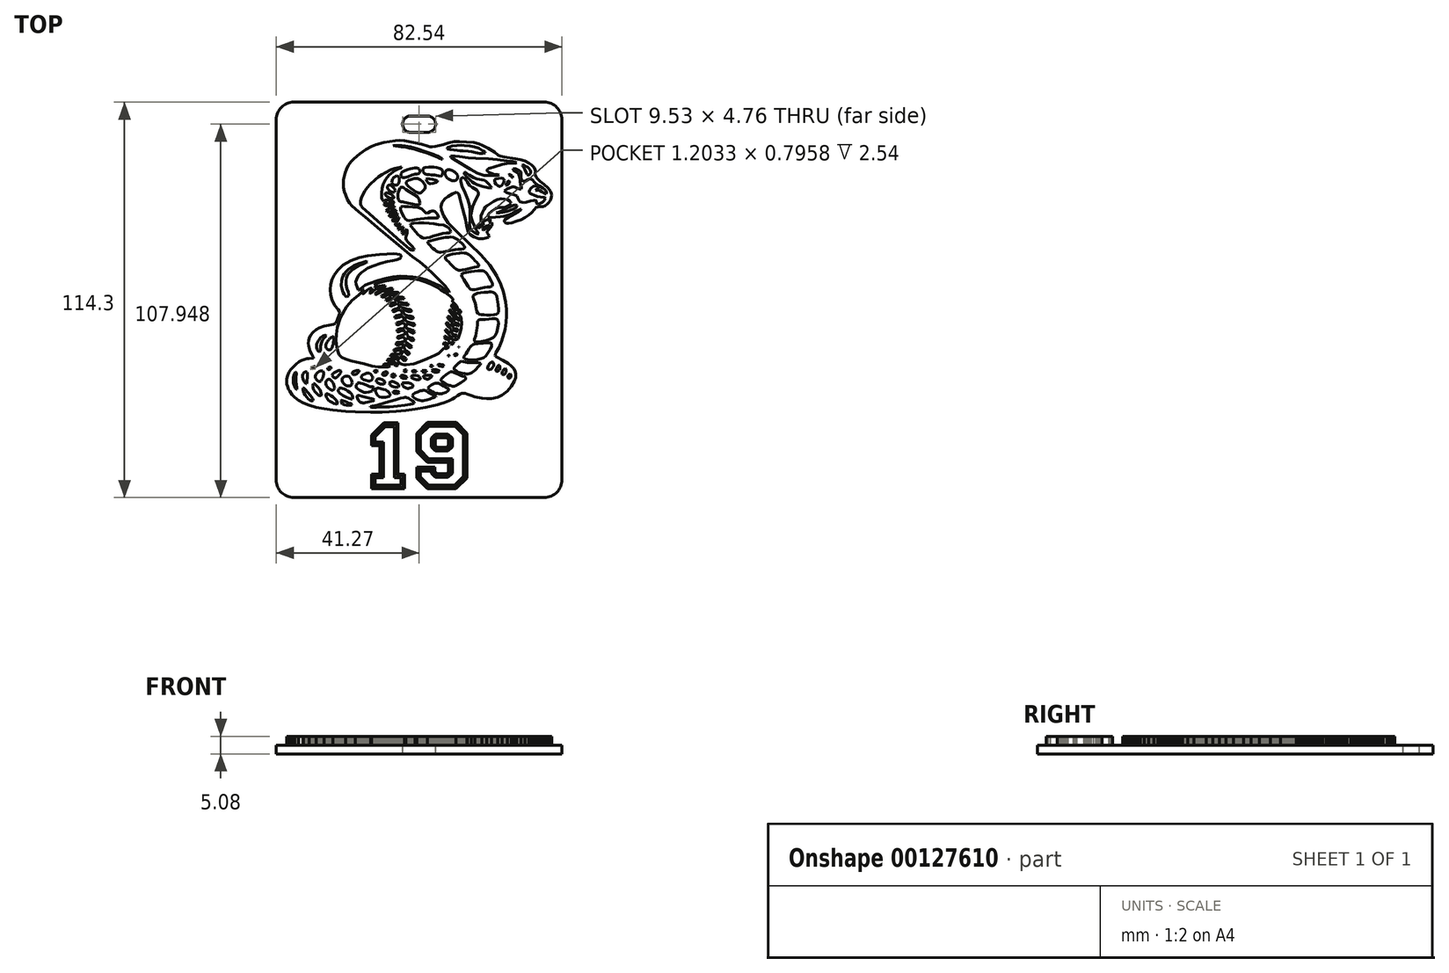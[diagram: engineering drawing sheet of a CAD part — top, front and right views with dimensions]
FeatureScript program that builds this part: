
annotation { "Feature Type Name" : "Feature", "Feature Type Description" : "" }
export const myFeature = defineFeature(function(context is Context, id is Id, definition is map)
    precondition{}
    {
        {
            var Q0;
            Q0=qCreatedBy(makeId("Top.planeOp"),FACE);
            var sketch = newSketch(context, id + "F0", { "sketchPlane" : qUnion([Q0])});
            skLineSegment(sketch, "E0", {"start": v(-25, -17.47) * mm, "end": v(-25.2, -17.55) * mm});
            skLineSegment(sketch, "E1", {"start": v(-25.2, -17.55) * mm, "end": v(-25.4, -17.66) * mm});
            skLineSegment(sketch, "E2", {"start": v(-25.4, -17.66) * mm, "end": v(-25.6, -17.8) * mm});
            skLineSegment(sketch, "E3", {"start": v(-25.6, -17.8) * mm, "end": v(-25.8, -17.96) * mm});
            skLineSegment(sketch, "E4", {"start": v(-25.8, -17.96) * mm, "end": v(-25.99, -18.14) * mm});
            skLineSegment(sketch, "E5", {"start": v(-25.99, -18.14) * mm, "end": v(-26.17, -18.34) * mm});
            skLineSegment(sketch, "E6", {"start": v(-26.17, -18.34) * mm, "end": v(-26.34, -18.55) * mm});
            skLineSegment(sketch, "E7", {"start": v(-26.34, -18.55) * mm, "end": v(-26.5, -18.77) * mm});
            skLineSegment(sketch, "E8", {"start": v(-26.5, -18.77) * mm, "end": v(-26.63, -19) * mm});
            skLineSegment(sketch, "E9", {"start": v(-26.63, -19) * mm, "end": v(-26.75, -19.22) * mm});
            skLineSegment(sketch, "E10", {"start": v(-26.75, -19.22) * mm, "end": v(-26.85, -19.44) * mm});
            skLineSegment(sketch, "E11", {"start": v(-26.85, -19.44) * mm, "end": v(-26.92, -19.66) * mm});
            skLineSegment(sketch, "E12", {"start": v(-26.92, -19.66) * mm, "end": v(-26.97, -19.87) * mm});
            skLineSegment(sketch, "E13", {"start": v(-26.97, -19.87) * mm, "end": v(-26.98, -20.1) * mm});
            skLineSegment(sketch, "E14", {"start": v(-26.98, -20.1) * mm, "end": v(-26.96, -20.32) * mm});
            skLineSegment(sketch, "E15", {"start": v(-26.96, -20.32) * mm, "end": v(-26.9, -20.53) * mm});
            skLineSegment(sketch, "E16", {"start": v(-26.9, -20.53) * mm, "end": v(-26.82, -20.72) * mm});
            skLineSegment(sketch, "E17", {"start": v(-26.82, -20.72) * mm, "end": v(-26.7, -20.88) * mm});
            skLineSegment(sketch, "E18", {"start": v(-26.7, -20.88) * mm, "end": v(-26.56, -21.02) * mm});
            skLineSegment(sketch, "E19", {"start": v(-26.56, -21.02) * mm, "end": v(-26.39, -21.13) * mm});
            skLineSegment(sketch, "E20", {"start": v(-26.39, -21.13) * mm, "end": v(-26.2, -21.2) * mm});
            skLineSegment(sketch, "E21", {"start": v(-26.2, -21.2) * mm, "end": v(-25.98, -21.2) * mm});
            skLineSegment(sketch, "E22", {"start": v(-25.98, -21.2) * mm, "end": v(-25.75, -21.17) * mm});
            skLineSegment(sketch, "E23", {"start": v(-25.75, -21.17) * mm, "end": v(-25.56, -21.1) * mm});
            skLineSegment(sketch, "E24", {"start": v(-25.56, -21.1) * mm, "end": v(-25.44, -20.98) * mm});
            skLineSegment(sketch, "E25", {"start": v(-25.44, -20.98) * mm, "end": v(-25.32, -20.82) * mm});
            skLineSegment(sketch, "E26", {"start": v(-25.32, -20.82) * mm, "end": v(-25.2, -20.6) * mm});
            skLineSegment(sketch, "E27", {"start": v(-25.2, -20.6) * mm, "end": v(-25.1, -20.36) * mm});
            skLineSegment(sketch, "E28", {"start": v(-25.1, -20.36) * mm, "end": v(-25.01, -20.09) * mm});
            skLineSegment(sketch, "E29", {"start": v(-25.01, -20.09) * mm, "end": v(-24.93, -19.8) * mm});
            skLineSegment(sketch, "E30", {"start": v(-24.93, -19.8) * mm, "end": v(-24.85, -19.52) * mm});
            skLineSegment(sketch, "E31", {"start": v(-24.85, -19.52) * mm, "end": v(-24.79, -19.23) * mm});
            skLineSegment(sketch, "E32", {"start": v(-24.79, -19.23) * mm, "end": v(-24.73, -18.97) * mm});
            skLineSegment(sketch, "E33", {"start": v(-24.73, -18.97) * mm, "end": v(-24.68, -18.72) * mm});
            skLineSegment(sketch, "E34", {"start": v(-24.68, -18.72) * mm, "end": v(-24.65, -18.51) * mm});
            skLineSegment(sketch, "E35", {"start": v(-24.65, -18.51) * mm, "end": v(-24.62, -18.35) * mm});
            skLineSegment(sketch, "E36", {"start": v(-24.62, -18.35) * mm, "end": v(-24.6, -18.17) * mm});
            skLineSegment(sketch, "E37", {"start": v(-24.6, -18.17) * mm, "end": v(-24.6, -17.96) * mm});
            skLineSegment(sketch, "E38", {"start": v(-24.6, -17.96) * mm, "end": v(-24.6, -17.74) * mm});
            skLineSegment(sketch, "E39", {"start": v(-24.6, -17.74) * mm, "end": v(-24.67, -17.56) * mm});
            skLineSegment(sketch, "E40", {"start": v(-24.67, -17.56) * mm, "end": v(-24.8, -17.46) * mm});
            skLineSegment(sketch, "E41", {"start": v(-24.8, -17.46) * mm, "end": v(-25, -17.47) * mm});
            skLineSegment(sketch, "E42", {"start": v(-12.5, 38.08) * mm, "end": v(-13.78, 37.58) * mm});
            skLineSegment(sketch, "E43", {"start": v(-13.78, 37.58) * mm, "end": v(-15.37, 36.7) * mm});
            skLineSegment(sketch, "E44", {"start": v(-15.37, 36.7) * mm, "end": v(-17.17, 35.45) * mm});
            skLineSegment(sketch, "E45", {"start": v(-17.17, 35.45) * mm, "end": v(-18.84, 34.02) * mm});
            skLineSegment(sketch, "E46", {"start": v(-18.84, 34.02) * mm, "end": v(-19.59, 33.23) * mm});
            skLineSegment(sketch, "E47", {"start": v(-19.59, 33.23) * mm, "end": v(-20.42, 32.07) * mm});
            skLineSegment(sketch, "E48", {"start": v(-20.42, 32.07) * mm, "end": v(-21.02, 30.93) * mm});
            skLineSegment(sketch, "E49", {"start": v(-21.02, 30.93) * mm, "end": v(-21.4, 29.95) * mm});
            skLineSegment(sketch, "E50", {"start": v(-21.4, 29.95) * mm, "end": v(-21.75, 28.48) * mm});
            skLineSegment(sketch, "E51", {"start": v(-21.75, 28.48) * mm, "end": v(-21.82, 27.9) * mm});
            skLineSegment(sketch, "E52", {"start": v(-21.82, 27.9) * mm, "end": v(-21.87, 26.75) * mm});
            skLineSegment(sketch, "E53", {"start": v(-21.87, 26.75) * mm, "end": v(-21.82, 25.82) * mm});
            skLineSegment(sketch, "E54", {"start": v(-21.82, 25.82) * mm, "end": v(-21.57, 24.45) * mm});
            skLineSegment(sketch, "E55", {"start": v(-21.57, 24.45) * mm, "end": v(-21.3, 23.55) * mm});
            skLineSegment(sketch, "E56", {"start": v(-21.3, 23.55) * mm, "end": v(-20.71, 22.25) * mm});
            skLineSegment(sketch, "E57", {"start": v(-20.71, 22.25) * mm, "end": v(-20.07, 21.21) * mm});
            skLineSegment(sketch, "E58", {"start": v(-20.07, 21.21) * mm, "end": v(-19.42, 20.42) * mm});
            skLineSegment(sketch, "E59", {"start": v(-19.42, 20.42) * mm, "end": v(-18.5, 19.54) * mm});
            skLineSegment(sketch, "E60", {"start": v(-18.5, 19.54) * mm, "end": v(-17.42, 18.64) * mm});
            skLineSegment(sketch, "E61", {"start": v(-17.42, 18.64) * mm, "end": v(-15.55, 17.08) * mm});
            skLineSegment(sketch, "E62", {"start": v(-15.55, 17.08) * mm, "end": v(-11.25, 13.43) * mm});
            skLineSegment(sketch, "E63", {"start": v(-11.25, 13.43) * mm, "end": v(-6.61, 9.59) * mm});
            skLineSegment(sketch, "E64", {"start": v(-6.61, 9.59) * mm, "end": v(-3.48, 6.97) * mm});
            skLineSegment(sketch, "E65", {"start": v(-3.48, 6.97) * mm, "end": v(-1.87, 5.73) * mm});
            skLineSegment(sketch, "E66", {"start": v(-1.87, 5.73) * mm, "end": v(0.18, 4.21) * mm});
            skLineSegment(sketch, "E67", {"start": v(0.18, 4.21) * mm, "end": v(1.93, 2.74) * mm});
            skLineSegment(sketch, "E68", {"start": v(1.93, 2.74) * mm, "end": v(4.36, 0.48) * mm});
            skLineSegment(sketch, "E69", {"start": v(4.36, 0.48) * mm, "end": v(6.86, -2.06) * mm});
            skLineSegment(sketch, "E70", {"start": v(6.86, -2.06) * mm, "end": v(7.56, -2.84) * mm});
            skLineSegment(sketch, "E71", {"start": v(7.56, -2.84) * mm, "end": v(8.48, -4.07) * mm});
            skLineSegment(sketch, "E72", {"start": v(8.48, -4.07) * mm, "end": v(8.76, -4.46) * mm});
            skLineSegment(sketch, "E73", {"start": v(8.76, -4.46) * mm, "end": v(8.71, -4.6) * mm});
            skLineSegment(sketch, "E74", {"start": v(8.71, -4.6) * mm, "end": v(7.64, -3.81) * mm});
            skLineSegment(sketch, "E75", {"start": v(7.64, -3.81) * mm, "end": v(6.2, -2.87) * mm});
            skLineSegment(sketch, "E76", {"start": v(6.2, -2.87) * mm, "end": v(4.71, -2.12) * mm});
            skLineSegment(sketch, "E77", {"start": v(4.71, -2.12) * mm, "end": v(2.14, -1.05) * mm});
            skLineSegment(sketch, "E78", {"start": v(2.14, -1.05) * mm, "end": v(0.04, -0.43) * mm});
            skLineSegment(sketch, "E79", {"start": v(0.04, -0.43) * mm, "end": v(-1.8, -0.1) * mm});
            skLineSegment(sketch, "E80", {"start": v(-1.8, -0.1) * mm, "end": v(-3.45, 0.04) * mm});
            skLineSegment(sketch, "E81", {"start": v(-3.45, 0.04) * mm, "end": v(-5.49, 0.05) * mm});
            skLineSegment(sketch, "E82", {"start": v(-5.49, 0.05) * mm, "end": v(-7.5, -0.12) * mm});
            skLineSegment(sketch, "E83", {"start": v(-7.5, -0.12) * mm, "end": v(-9.48, -0.47) * mm});
            skLineSegment(sketch, "E84", {"start": v(-9.48, -0.47) * mm, "end": v(-11.8, -1.16) * mm});
            skLineSegment(sketch, "E85", {"start": v(-11.8, -1.16) * mm, "end": v(-14.7, -2.17) * mm});
            skLineSegment(sketch, "E86", {"start": v(-14.7, -2.17) * mm, "end": v(-15.63, -2.56) * mm});
            skLineSegment(sketch, "E87", {"start": v(-15.63, -2.56) * mm, "end": v(-16.3, -3) * mm});
            skLineSegment(sketch, "E88", {"start": v(-16.3, -3) * mm, "end": v(-16.86, -3.54) * mm});
            skLineSegment(sketch, "E89", {"start": v(-16.86, -3.54) * mm, "end": v(-17.17, -3.82) * mm});
            skLineSegment(sketch, "E90", {"start": v(-17.17, -3.82) * mm, "end": v(-17.34, -3.95) * mm});
            skLineSegment(sketch, "E91", {"start": v(-17.34, -3.95) * mm, "end": v(-17.56, -3.93) * mm});
            skLineSegment(sketch, "E92", {"start": v(-17.56, -3.93) * mm, "end": v(-17.85, -3.32) * mm});
            skLineSegment(sketch, "E93", {"start": v(-17.85, -3.32) * mm, "end": v(-18.2, -2.35) * mm});
            skLineSegment(sketch, "E94", {"start": v(-18.2, -2.35) * mm, "end": v(-18.28, -1.6) * mm});
            skLineSegment(sketch, "E95", {"start": v(-18.28, -1.6) * mm, "end": v(-18.12, -0.9) * mm});
            skLineSegment(sketch, "E96", {"start": v(-18.12, -0.9) * mm, "end": v(-17.5, 0.19) * mm});
            skLineSegment(sketch, "E97", {"start": v(-17.5, 0.19) * mm, "end": v(-16.7, 1.08) * mm});
            skLineSegment(sketch, "E98", {"start": v(-16.7, 1.08) * mm, "end": v(-15.96, 1.7) * mm});
            skLineSegment(sketch, "E99", {"start": v(-15.96, 1.7) * mm, "end": v(-14.9, 2.35) * mm});
            skLineSegment(sketch, "E100", {"start": v(-14.9, 2.35) * mm, "end": v(-13.29, 3.1) * mm});
            skLineSegment(sketch, "E101", {"start": v(-13.29, 3.1) * mm, "end": v(-11.09, 3.81) * mm});
            skLineSegment(sketch, "E102", {"start": v(-11.09, 3.81) * mm, "end": v(-9.17, 4.31) * mm});
            skLineSegment(sketch, "E103", {"start": v(-9.17, 4.31) * mm, "end": v(-7.68, 4.6) * mm});
            skLineSegment(sketch, "E104", {"start": v(-7.68, 4.6) * mm, "end": v(-6.49, 4.84) * mm});
            skLineSegment(sketch, "E105", {"start": v(-6.49, 4.84) * mm, "end": v(-5.5, 5.25) * mm});
            skLineSegment(sketch, "E106", {"start": v(-5.5, 5.25) * mm, "end": v(-5.2, 5.6) * mm});
            skLineSegment(sketch, "E107", {"start": v(-5.2, 5.6) * mm, "end": v(-5.24, 6.07) * mm});
            skLineSegment(sketch, "E108", {"start": v(-5.24, 6.07) * mm, "end": v(-5.54, 6.37) * mm});
            skLineSegment(sketch, "E109", {"start": v(-5.54, 6.37) * mm, "end": v(-6.43, 6.46) * mm});
            skLineSegment(sketch, "E110", {"start": v(-6.43, 6.46) * mm, "end": v(-7.45, 6.57) * mm});
            skLineSegment(sketch, "E111", {"start": v(-7.45, 6.57) * mm, "end": v(-9.23, 6.5) * mm});
            skLineSegment(sketch, "E112", {"start": v(-9.23, 6.5) * mm, "end": v(-11.41, 6.4) * mm});
            skLineSegment(sketch, "E113", {"start": v(-11.41, 6.4) * mm, "end": v(-14.93, 6.01) * mm});
            skLineSegment(sketch, "E114", {"start": v(-14.93, 6.01) * mm, "end": v(-17.28, 5.47) * mm});
            skLineSegment(sketch, "E115", {"start": v(-17.28, 5.47) * mm, "end": v(-19.74, 4.54) * mm});
            skLineSegment(sketch, "E116", {"start": v(-19.74, 4.54) * mm, "end": v(-21.95, 3.24) * mm});
            skLineSegment(sketch, "E117", {"start": v(-21.95, 3.24) * mm, "end": v(-23.55, 1.78) * mm});
            skLineSegment(sketch, "E118", {"start": v(-23.55, 1.78) * mm, "end": v(-24.57, 0.39) * mm});
            skLineSegment(sketch, "E119", {"start": v(-24.57, 0.39) * mm, "end": v(-25.2, -0.89) * mm});
            skLineSegment(sketch, "E120", {"start": v(-25.2, -0.89) * mm, "end": v(-25.61, -2.29) * mm});
            skLineSegment(sketch, "E121", {"start": v(-25.61, -2.29) * mm, "end": v(-25.72, -3.78) * mm});
            skLineSegment(sketch, "E122", {"start": v(-25.72, -3.78) * mm, "end": v(-25.56, -5.3) * mm});
            skLineSegment(sketch, "E123", {"start": v(-25.56, -5.3) * mm, "end": v(-25.17, -6.8) * mm});
            skLineSegment(sketch, "E124", {"start": v(-25.17, -6.8) * mm, "end": v(-24.4, -8.44) * mm});
            skLineSegment(sketch, "E125", {"start": v(-24.4, -8.44) * mm, "end": v(-23.39, -9.6) * mm});
            skLineSegment(sketch, "E126", {"start": v(-23.39, -9.6) * mm, "end": v(-22.97, -10.2) * mm});
            skLineSegment(sketch, "E127", {"start": v(-22.97, -10.2) * mm, "end": v(-22.91, -10.52) * mm});
            skLineSegment(sketch, "E128", {"start": v(-22.91, -10.52) * mm, "end": v(-23.1, -11.24) * mm});
            skLineSegment(sketch, "E129", {"start": v(-23.1, -11.24) * mm, "end": v(-23.62, -12.57) * mm});
            skLineSegment(sketch, "E130", {"start": v(-23.62, -12.57) * mm, "end": v(-23.9, -13.16) * mm});
            skLineSegment(sketch, "E131", {"start": v(-23.9, -13.16) * mm, "end": v(-24, -13.4) * mm});
            skLineSegment(sketch, "E132", {"start": v(-24, -13.4) * mm, "end": v(-24.16, -13.58) * mm});
            skLineSegment(sketch, "E133", {"start": v(-24.16, -13.58) * mm, "end": v(-24.78, -13.85) * mm});
            skLineSegment(sketch, "E134", {"start": v(-24.78, -13.85) * mm, "end": v(-26.07, -14.09) * mm});
            skLineSegment(sketch, "E135", {"start": v(-26.07, -14.09) * mm, "end": v(-27.5, -14.33) * mm});
            skLineSegment(sketch, "E136", {"start": v(-27.5, -14.33) * mm, "end": v(-28.88, -14.85) * mm});
            skLineSegment(sketch, "E137", {"start": v(-28.88, -14.85) * mm, "end": v(-29.72, -15.33) * mm});
            skLineSegment(sketch, "E138", {"start": v(-29.72, -15.33) * mm, "end": v(-30.64, -16.1) * mm});
            skLineSegment(sketch, "E139", {"start": v(-30.64, -16.1) * mm, "end": v(-31.37, -17.06) * mm});
            skLineSegment(sketch, "E140", {"start": v(-31.37, -17.06) * mm, "end": v(-31.8, -17.97) * mm});
            skLineSegment(sketch, "E141", {"start": v(-31.8, -17.97) * mm, "end": v(-31.94, -18.58) * mm});
            skLineSegment(sketch, "E142", {"start": v(-31.94, -18.58) * mm, "end": v(-31.99, -19.3) * mm});
            skLineSegment(sketch, "E143", {"start": v(-31.99, -19.3) * mm, "end": v(-31.88, -20.14) * mm});
            skLineSegment(sketch, "E144", {"start": v(-31.88, -20.14) * mm, "end": v(-31.62, -21.1) * mm});
            skLineSegment(sketch, "E145", {"start": v(-31.62, -21.1) * mm, "end": v(-31.46, -21.57) * mm});
            skLineSegment(sketch, "E146", {"start": v(-31.46, -21.57) * mm, "end": v(-31.01, -22.54) * mm});
            skLineSegment(sketch, "E147", {"start": v(-31.01, -22.54) * mm, "end": v(-30.59, -23.23) * mm});
            skLineSegment(sketch, "E148", {"start": v(-30.59, -23.23) * mm, "end": v(-30.53, -23.34) * mm});
            skLineSegment(sketch, "E149", {"start": v(-30.53, -23.34) * mm, "end": v(-30.55, -23.58) * mm});
            skLineSegment(sketch, "E150", {"start": v(-30.55, -23.58) * mm, "end": v(-30.98, -23.69) * mm});
            skLineSegment(sketch, "E151", {"start": v(-30.98, -23.69) * mm, "end": v(-31.83, -23.74) * mm});
            skLineSegment(sketch, "E152", {"start": v(-31.83, -23.74) * mm, "end": v(-32.4, -23.77) * mm});
            skLineSegment(sketch, "E153", {"start": v(-32.4, -23.77) * mm, "end": v(-32.85, -23.85) * mm});
            skLineSegment(sketch, "E154", {"start": v(-32.85, -23.85) * mm, "end": v(-33.87, -24.26) * mm});
            skLineSegment(sketch, "E155", {"start": v(-33.87, -24.26) * mm, "end": v(-34.68, -24.71) * mm});
            skLineSegment(sketch, "E156", {"start": v(-34.68, -24.71) * mm, "end": v(-35.63, -25.4) * mm});
            skLineSegment(sketch, "E157", {"start": v(-35.63, -25.4) * mm, "end": v(-36.41, -26.13) * mm});
            skLineSegment(sketch, "E158", {"start": v(-36.41, -26.13) * mm, "end": v(-37.09, -26.95) * mm});
            skLineSegment(sketch, "E159", {"start": v(-37.09, -26.95) * mm, "end": v(-37.58, -27.74) * mm});
            skLineSegment(sketch, "E160", {"start": v(-37.58, -27.74) * mm, "end": v(-38, -28.7) * mm});
            skLineSegment(sketch, "E161", {"start": v(-38, -28.7) * mm, "end": v(-38.21, -29.58) * mm});
            skLineSegment(sketch, "E162", {"start": v(-38.21, -29.58) * mm, "end": v(-38.27, -30.38) * mm});
            skLineSegment(sketch, "E163", {"start": v(-38.27, -30.38) * mm, "end": v(-38.21, -31.08) * mm});
            skLineSegment(sketch, "E164", {"start": v(-38.21, -31.08) * mm, "end": v(-38.05, -31.77) * mm});
            skLineSegment(sketch, "E165", {"start": v(-38.05, -31.77) * mm, "end": v(-37.73, -32.62) * mm});
            skLineSegment(sketch, "E166", {"start": v(-37.73, -32.62) * mm, "end": v(-37.42, -33.22) * mm});
            skLineSegment(sketch, "E167", {"start": v(-37.42, -33.22) * mm, "end": v(-36.7, -34.2) * mm});
            skLineSegment(sketch, "E168", {"start": v(-36.7, -34.2) * mm, "end": v(-36, -34.9) * mm});
            skLineSegment(sketch, "E169", {"start": v(-36, -34.9) * mm, "end": v(-34.81, -35.8) * mm});
            skLineSegment(sketch, "E170", {"start": v(-34.81, -35.8) * mm, "end": v(-33.37, -36.58) * mm});
            skLineSegment(sketch, "E171", {"start": v(-33.37, -36.58) * mm, "end": v(-31.8, -37.22) * mm});
            skLineSegment(sketch, "E172", {"start": v(-31.8, -37.22) * mm, "end": v(-29.8, -37.8) * mm});
            skLineSegment(sketch, "E173", {"start": v(-29.8, -37.8) * mm, "end": v(-27.44, -38.3) * mm});
            skLineSegment(sketch, "E174", {"start": v(-27.44, -38.3) * mm, "end": v(-24.92, -38.64) * mm});
            skLineSegment(sketch, "E175", {"start": v(-24.92, -38.64) * mm, "end": v(-21.2, -39) * mm});
            skLineSegment(sketch, "E176", {"start": v(-21.2, -39) * mm, "end": v(-18.43, -39.18) * mm});
            skLineSegment(sketch, "E177", {"start": v(-18.43, -39.18) * mm, "end": v(-14, -39.3) * mm});
            skLineSegment(sketch, "E178", {"start": v(-14, -39.3) * mm, "end": v(-10.69, -39.24) * mm});
            skLineSegment(sketch, "E179", {"start": v(-10.69, -39.24) * mm, "end": v(-6.63, -39) * mm});
            skLineSegment(sketch, "E180", {"start": v(-6.63, -39) * mm, "end": v(-3.85, -38.73) * mm});
            skLineSegment(sketch, "E181", {"start": v(-3.85, -38.73) * mm, "end": v(-1.2, -38.37) * mm});
            skLineSegment(sketch, "E182", {"start": v(-1.2, -38.37) * mm, "end": v(1.91, -37.82) * mm});
            skLineSegment(sketch, "E183", {"start": v(1.91, -37.82) * mm, "end": v(5.37, -37.04) * mm});
            skLineSegment(sketch, "E184", {"start": v(5.37, -37.04) * mm, "end": v(6.11, -36.83) * mm});
            skLineSegment(sketch, "E185", {"start": v(6.11, -36.83) * mm, "end": v(7.35, -36.42) * mm});
            skLineSegment(sketch, "E186", {"start": v(7.35, -36.42) * mm, "end": v(8.57, -35.92) * mm});
            skLineSegment(sketch, "E187", {"start": v(8.57, -35.92) * mm, "end": v(9.61, -35.42) * mm});
            skLineSegment(sketch, "E188", {"start": v(9.61, -35.42) * mm, "end": v(10.24, -35.06) * mm});
            skLineSegment(sketch, "E189", {"start": v(10.24, -35.06) * mm, "end": v(11.1, -34.46) * mm});
            skLineSegment(sketch, "E190", {"start": v(11.1, -34.46) * mm, "end": v(11.8, -34.04) * mm});
            skLineSegment(sketch, "E191", {"start": v(11.8, -34.04) * mm, "end": v(12.34, -33.83) * mm});
            skLineSegment(sketch, "E192", {"start": v(12.34, -33.83) * mm, "end": v(12.66, -33.78) * mm});
            skLineSegment(sketch, "E193", {"start": v(12.66, -33.78) * mm, "end": v(13.24, -33.84) * mm});
            skLineSegment(sketch, "E194", {"start": v(13.24, -33.84) * mm, "end": v(14, -34.05) * mm});
            skLineSegment(sketch, "E195", {"start": v(14, -34.05) * mm, "end": v(15.13, -34.47) * mm});
            skLineSegment(sketch, "E196", {"start": v(15.13, -34.47) * mm, "end": v(16.14, -34.77) * mm});
            skLineSegment(sketch, "E197", {"start": v(16.14, -34.77) * mm, "end": v(18.11, -35.15) * mm});
            skLineSegment(sketch, "E198", {"start": v(18.11, -35.15) * mm, "end": v(19.54, -35.28) * mm});
            skLineSegment(sketch, "E199", {"start": v(19.54, -35.28) * mm, "end": v(20.95, -35.26) * mm});
            skLineSegment(sketch, "E200", {"start": v(20.95, -35.26) * mm, "end": v(22.74, -34.91) * mm});
            skLineSegment(sketch, "E201", {"start": v(22.74, -34.91) * mm, "end": v(23.97, -34.28) * mm});
            skLineSegment(sketch, "E202", {"start": v(23.97, -34.28) * mm, "end": v(25.45, -33.1) * mm});
            skLineSegment(sketch, "E203", {"start": v(25.45, -33.1) * mm, "end": v(26.6, -31.82) * mm});
            skLineSegment(sketch, "E204", {"start": v(26.6, -31.82) * mm, "end": v(27.54, -30.3) * mm});
            skLineSegment(sketch, "E205", {"start": v(27.54, -30.3) * mm, "end": v(27.91, -29.21) * mm});
            skLineSegment(sketch, "E206", {"start": v(27.91, -29.21) * mm, "end": v(27.97, -28.25) * mm});
            skLineSegment(sketch, "E207", {"start": v(27.97, -28.25) * mm, "end": v(27.79, -27.53) * mm});
            skLineSegment(sketch, "E208", {"start": v(27.79, -27.53) * mm, "end": v(27.36, -26.75) * mm});
            skLineSegment(sketch, "E209", {"start": v(27.36, -26.75) * mm, "end": v(26.7, -25.97) * mm});
            skLineSegment(sketch, "E210", {"start": v(26.7, -25.97) * mm, "end": v(25.74, -25.16) * mm});
            skLineSegment(sketch, "E211", {"start": v(25.74, -25.16) * mm, "end": v(24.3, -24.24) * mm});
            skLineSegment(sketch, "E212", {"start": v(24.3, -24.24) * mm, "end": v(22.38, -23.32) * mm});
            skLineSegment(sketch, "E213", {"start": v(22.38, -23.32) * mm, "end": v(22.07, -23.07) * mm});
            skLineSegment(sketch, "E214", {"start": v(22.07, -23.07) * mm, "end": v(22, -22.85) * mm});
            skLineSegment(sketch, "E215", {"start": v(22, -22.85) * mm, "end": v(22.07, -22.5) * mm});
            skLineSegment(sketch, "E216", {"start": v(22.07, -22.5) * mm, "end": v(22.26, -22) * mm});
            skLineSegment(sketch, "E217", {"start": v(22.26, -22) * mm, "end": v(23.08, -20.59) * mm});
            skLineSegment(sketch, "E218", {"start": v(23.08, -20.59) * mm, "end": v(23.8, -18.74) * mm});
            skLineSegment(sketch, "E219", {"start": v(23.8, -18.74) * mm, "end": v(24.83, -15.27) * mm});
            skLineSegment(sketch, "E220", {"start": v(24.83, -15.27) * mm, "end": v(25.17, -13.27) * mm});
            skLineSegment(sketch, "E221", {"start": v(25.17, -13.27) * mm, "end": v(25.29, -11.45) * mm});
            skLineSegment(sketch, "E222", {"start": v(25.29, -11.45) * mm, "end": v(25.25, -9.52) * mm});
            skLineSegment(sketch, "E223", {"start": v(25.25, -9.52) * mm, "end": v(25, -7.32) * mm});
            skLineSegment(sketch, "E224", {"start": v(25, -7.32) * mm, "end": v(24.35, -4.46) * mm});
            skLineSegment(sketch, "E225", {"start": v(24.35, -4.46) * mm, "end": v(23.58, -2.27) * mm});
            skLineSegment(sketch, "E226", {"start": v(23.58, -2.27) * mm, "end": v(22.42, 0.17) * mm});
            skLineSegment(sketch, "E227", {"start": v(22.42, 0.17) * mm, "end": v(20.4, 3.28) * mm});
            skLineSegment(sketch, "E228", {"start": v(20.4, 3.28) * mm, "end": v(17.82, 6.24) * mm});
            skLineSegment(sketch, "E229", {"start": v(17.82, 6.24) * mm, "end": v(14.58, 9.4) * mm});
            skLineSegment(sketch, "E230", {"start": v(14.58, 9.4) * mm, "end": v(11.12, 12.71) * mm});
            skLineSegment(sketch, "E231", {"start": v(11.12, 12.71) * mm, "end": v(8.41, 15.53) * mm});
            skLineSegment(sketch, "E232", {"start": v(8.41, 15.53) * mm, "end": v(7.06, 17.49) * mm});
            skLineSegment(sketch, "E233", {"start": v(7.06, 17.49) * mm, "end": v(6.42, 19.21) * mm});
            skLineSegment(sketch, "E234", {"start": v(6.42, 19.21) * mm, "end": v(6.35, 20.23) * mm});
            skLineSegment(sketch, "E235", {"start": v(6.35, 20.23) * mm, "end": v(6.62, 21.33) * mm});
            skLineSegment(sketch, "E236", {"start": v(6.62, 21.33) * mm, "end": v(7.47, 22.5) * mm});
            skLineSegment(sketch, "E237", {"start": v(7.47, 22.5) * mm, "end": v(8.32, 23.15) * mm});
            skLineSegment(sketch, "E238", {"start": v(8.32, 23.15) * mm, "end": v(9.58, 23.9) * mm});
            skLineSegment(sketch, "E239", {"start": v(9.58, 23.9) * mm, "end": v(10.5, 24.28) * mm});
            skLineSegment(sketch, "E240", {"start": v(10.5, 24.28) * mm, "end": v(10.82, 24.33) * mm});
            skLineSegment(sketch, "E241", {"start": v(10.82, 24.33) * mm, "end": v(11.2, 24.18) * mm});
            skLineSegment(sketch, "E242", {"start": v(11.2, 24.18) * mm, "end": v(11.5, 23.7) * mm});
            skLineSegment(sketch, "E243", {"start": v(11.5, 23.7) * mm, "end": v(11.85, 22.6) * mm});
            skLineSegment(sketch, "E244", {"start": v(11.85, 22.6) * mm, "end": v(12.21, 21.03) * mm});
            skLineSegment(sketch, "E245", {"start": v(12.21, 21.03) * mm, "end": v(13.4, 16.32) * mm});
            skLineSegment(sketch, "E246", {"start": v(13.4, 16.32) * mm, "end": v(13.66, 14.7) * mm});
            skLineSegment(sketch, "E247", {"start": v(13.66, 14.7) * mm, "end": v(14.2, 12.79) * mm});
            skLineSegment(sketch, "E248", {"start": v(14.2, 12.79) * mm, "end": v(14.8, 12.05) * mm});
            skLineSegment(sketch, "E249", {"start": v(14.8, 12.05) * mm, "end": v(15.83, 11.4) * mm});
            skLineSegment(sketch, "E250", {"start": v(15.83, 11.4) * mm, "end": v(17.26, 10.97) * mm});
            skLineSegment(sketch, "E251", {"start": v(17.26, 10.97) * mm, "end": v(18.46, 10.86) * mm});
            skLineSegment(sketch, "E252", {"start": v(18.46, 10.86) * mm, "end": v(20.02, 11.24) * mm});
            skLineSegment(sketch, "E253", {"start": v(20.02, 11.24) * mm, "end": v(20.23, 11.5) * mm});
            skLineSegment(sketch, "E254", {"start": v(20.23, 11.5) * mm, "end": v(20.26, 11.77) * mm});
            skLineSegment(sketch, "E255", {"start": v(20.26, 11.77) * mm, "end": v(20.08, 12.08) * mm});
            skLineSegment(sketch, "E256", {"start": v(20.08, 12.08) * mm, "end": v(19.69, 12.5) * mm});
            skLineSegment(sketch, "E257", {"start": v(19.69, 12.5) * mm, "end": v(19.6, 12.73) * mm});
            skLineSegment(sketch, "E258", {"start": v(19.6, 12.73) * mm, "end": v(19.68, 13.04) * mm});
            skLineSegment(sketch, "E259", {"start": v(19.68, 13.04) * mm, "end": v(19.89, 13.35) * mm});
            skLineSegment(sketch, "E260", {"start": v(19.89, 13.35) * mm, "end": v(20.73, 14.23) * mm});
            skLineSegment(sketch, "E261", {"start": v(20.73, 14.23) * mm, "end": v(20.98, 14.58) * mm});
            skLineSegment(sketch, "E262", {"start": v(20.98, 14.58) * mm, "end": v(21.12, 15) * mm});
            skLineSegment(sketch, "E263", {"start": v(21.12, 15) * mm, "end": v(21.1, 15.38) * mm});
            skLineSegment(sketch, "E264", {"start": v(21.1, 15.38) * mm, "end": v(20.91, 15.6) * mm});
            skLineSegment(sketch, "E265", {"start": v(20.91, 15.6) * mm, "end": v(20.43, 15.6) * mm});
            skLineSegment(sketch, "E266", {"start": v(20.43, 15.6) * mm, "end": v(20.24, 15.56) * mm});
            skLineSegment(sketch, "E267", {"start": v(20.24, 15.56) * mm, "end": v(20.37, 15.84) * mm});
            skLineSegment(sketch, "E268", {"start": v(20.37, 15.84) * mm, "end": v(20.52, 16.07) * mm});
            skLineSegment(sketch, "E269", {"start": v(20.52, 16.07) * mm, "end": v(20.58, 16.29) * mm});
            skLineSegment(sketch, "E270", {"start": v(20.58, 16.29) * mm, "end": v(20.49, 16.49) * mm});
            skLineSegment(sketch, "E271", {"start": v(20.49, 16.49) * mm, "end": v(20.2, 16.55) * mm});
            skLineSegment(sketch, "E272", {"start": v(20.2, 16.55) * mm, "end": v(19.68, 16.41) * mm});
            skLineSegment(sketch, "E273", {"start": v(19.68, 16.41) * mm, "end": v(18.97, 16.1) * mm});
            skLineSegment(sketch, "E274", {"start": v(18.97, 16.1) * mm, "end": v(18.17, 15.77) * mm});
            skLineSegment(sketch, "E275", {"start": v(18.17, 15.77) * mm, "end": v(18.05, 15.75) * mm});
            skLineSegment(sketch, "E276", {"start": v(18.05, 15.75) * mm, "end": v(17.97, 15.8) * mm});
            skLineSegment(sketch, "E277", {"start": v(17.97, 15.8) * mm, "end": v(17.9, 15.98) * mm});
            skLineSegment(sketch, "E278", {"start": v(17.9, 15.98) * mm, "end": v(17.83, 16.62) * mm});
            skLineSegment(sketch, "E279", {"start": v(17.83, 16.62) * mm, "end": v(17.83, 16.98) * mm});
            skLineSegment(sketch, "E280", {"start": v(17.83, 16.98) * mm, "end": v(17.94, 17.53) * mm});
            skLineSegment(sketch, "E281", {"start": v(17.94, 17.53) * mm, "end": v(18.3, 18.46) * mm});
            skLineSegment(sketch, "E282", {"start": v(18.3, 18.46) * mm, "end": v(18.8, 19.45) * mm});
            skLineSegment(sketch, "E283", {"start": v(18.8, 19.45) * mm, "end": v(19.11, 20) * mm});
            skLineSegment(sketch, "E284", {"start": v(19.11, 20) * mm, "end": v(19.36, 20.27) * mm});
            skLineSegment(sketch, "E285", {"start": v(19.36, 20.27) * mm, "end": v(19.65, 20.44) * mm});
            skLineSegment(sketch, "E286", {"start": v(19.65, 20.44) * mm, "end": v(20.1, 20.7) * mm});
            skLineSegment(sketch, "E287", {"start": v(20.1, 20.7) * mm, "end": v(21.5, 21.7) * mm});
            skLineSegment(sketch, "E288", {"start": v(21.5, 21.7) * mm, "end": v(22.58, 22.2) * mm});
            skLineSegment(sketch, "E289", {"start": v(22.58, 22.2) * mm, "end": v(23.78, 22.42) * mm});
            skLineSegment(sketch, "E290", {"start": v(23.78, 22.42) * mm, "end": v(24.74, 22.36) * mm});
            skLineSegment(sketch, "E291", {"start": v(24.74, 22.36) * mm, "end": v(25.55, 22.15) * mm});
            skLineSegment(sketch, "E292", {"start": v(25.55, 22.15) * mm, "end": v(26.08, 21.89) * mm});
            skLineSegment(sketch, "E293", {"start": v(26.08, 21.89) * mm, "end": v(26.43, 21.53) * mm});
            skLineSegment(sketch, "E294", {"start": v(26.43, 21.53) * mm, "end": v(26.47, 21.2) * mm});
            skLineSegment(sketch, "E295", {"start": v(26.47, 21.2) * mm, "end": v(26.25, 20.8) * mm});
            skLineSegment(sketch, "E296", {"start": v(26.25, 20.8) * mm, "end": v(25.7, 20.43) * mm});
            skLineSegment(sketch, "E297", {"start": v(25.7, 20.43) * mm, "end": v(24.96, 20.1) * mm});
            skLineSegment(sketch, "E298", {"start": v(24.96, 20.1) * mm, "end": v(24.43, 19.95) * mm});
            skLineSegment(sketch, "E299", {"start": v(24.43, 19.95) * mm, "end": v(23.61, 19.91) * mm});
            skLineSegment(sketch, "E300", {"start": v(23.61, 19.91) * mm, "end": v(23.02, 19.88) * mm});
            skLineSegment(sketch, "E301", {"start": v(23.02, 19.88) * mm, "end": v(22.2, 19.62) * mm});
            skLineSegment(sketch, "E302", {"start": v(22.2, 19.62) * mm, "end": v(21.08, 18.88) * mm});
            skLineSegment(sketch, "E303", {"start": v(21.08, 18.88) * mm, "end": v(20.17, 18.09) * mm});
            skLineSegment(sketch, "E304", {"start": v(20.17, 18.09) * mm, "end": v(19.9, 17.7) * mm});
            skLineSegment(sketch, "E305", {"start": v(19.9, 17.7) * mm, "end": v(19.88, 17.39) * mm});
            skLineSegment(sketch, "E306", {"start": v(19.88, 17.39) * mm, "end": v(19.97, 17.25) * mm});
            skLineSegment(sketch, "E307", {"start": v(19.97, 17.25) * mm, "end": v(20.13, 17.15) * mm});
            skLineSegment(sketch, "E308", {"start": v(20.13, 17.15) * mm, "end": v(20.35, 17.1) * mm});
            skLineSegment(sketch, "E309", {"start": v(20.35, 17.1) * mm, "end": v(20.88, 17.05) * mm});
            skLineSegment(sketch, "E310", {"start": v(20.88, 17.05) * mm, "end": v(22.12, 17.1) * mm});
            skLineSegment(sketch, "E311", {"start": v(22.12, 17.1) * mm, "end": v(23.42, 17.2) * mm});
            skLineSegment(sketch, "E312", {"start": v(23.42, 17.2) * mm, "end": v(24.5, 17.4) * mm});
            skLineSegment(sketch, "E313", {"start": v(24.5, 17.4) * mm, "end": v(25.87, 17.78) * mm});
            skLineSegment(sketch, "E314", {"start": v(25.87, 17.78) * mm, "end": v(27.16, 18.28) * mm});
            skLineSegment(sketch, "E315", {"start": v(27.16, 18.28) * mm, "end": v(28.18, 18.85) * mm});
            skLineSegment(sketch, "E316", {"start": v(28.18, 18.85) * mm, "end": v(29, 19.34) * mm});
            skLineSegment(sketch, "E317", {"start": v(29, 19.34) * mm, "end": v(29.34, 19.41) * mm});
            skLineSegment(sketch, "E318", {"start": v(29.34, 19.41) * mm, "end": v(29.43, 19.38) * mm});
            skLineSegment(sketch, "E319", {"start": v(29.43, 19.38) * mm, "end": v(29.45, 19.3) * mm});
            skLineSegment(sketch, "E320", {"start": v(29.45, 19.3) * mm, "end": v(29.4, 19.23) * mm});
            skLineSegment(sketch, "E321", {"start": v(29.4, 19.23) * mm, "end": v(29.27, 19.1) * mm});
            skLineSegment(sketch, "E322", {"start": v(29.27, 19.1) * mm, "end": v(28.63, 18.65) * mm});
            skLineSegment(sketch, "E323", {"start": v(28.63, 18.65) * mm, "end": v(27.81, 18.13) * mm});
            skLineSegment(sketch, "E324", {"start": v(27.81, 18.13) * mm, "end": v(26.91, 17.6) * mm});
            skLineSegment(sketch, "E325", {"start": v(26.91, 17.6) * mm, "end": v(25.54, 16.87) * mm});
            skLineSegment(sketch, "E326", {"start": v(25.54, 16.87) * mm, "end": v(24.86, 16.5) * mm});
            skLineSegment(sketch, "E327", {"start": v(24.86, 16.5) * mm, "end": v(24.64, 16.3) * mm});
            skLineSegment(sketch, "E328", {"start": v(24.64, 16.3) * mm, "end": v(24.56, 16.14) * mm});
            skLineSegment(sketch, "E329", {"start": v(24.56, 16.14) * mm, "end": v(24.58, 15.94) * mm});
            skLineSegment(sketch, "E330", {"start": v(24.58, 15.94) * mm, "end": v(24.74, 15.68) * mm});
            skLineSegment(sketch, "E331", {"start": v(24.74, 15.68) * mm, "end": v(24.98, 15.51) * mm});
            skLineSegment(sketch, "E332", {"start": v(24.98, 15.51) * mm, "end": v(25.38, 15.4) * mm});
            skLineSegment(sketch, "E333", {"start": v(25.38, 15.4) * mm, "end": v(25.86, 15.38) * mm});
            skLineSegment(sketch, "E334", {"start": v(25.86, 15.38) * mm, "end": v(26.75, 15.53) * mm});
            skLineSegment(sketch, "E335", {"start": v(26.75, 15.53) * mm, "end": v(28.12, 15.95) * mm});
            skLineSegment(sketch, "E336", {"start": v(28.12, 15.95) * mm, "end": v(29.42, 16.41) * mm});
            skLineSegment(sketch, "E337", {"start": v(29.42, 16.41) * mm, "end": v(30.59, 16.98) * mm});
            skLineSegment(sketch, "E338", {"start": v(30.59, 16.98) * mm, "end": v(31.77, 17.75) * mm});
            skLineSegment(sketch, "E339", {"start": v(31.77, 17.75) * mm, "end": v(32.54, 18.43) * mm});
            skLineSegment(sketch, "E340", {"start": v(32.54, 18.43) * mm, "end": v(33.36, 19.4) * mm});
            skLineSegment(sketch, "E341", {"start": v(33.36, 19.4) * mm, "end": v(33.8, 19.86) * mm});
            skLineSegment(sketch, "E342", {"start": v(33.8, 19.86) * mm, "end": v(34.2, 20.11) * mm});
            skLineSegment(sketch, "E343", {"start": v(34.2, 20.11) * mm, "end": v(34.56, 20.18) * mm});
            skLineSegment(sketch, "E344", {"start": v(34.56, 20.18) * mm, "end": v(35.1, 20.16) * mm});
            skLineSegment(sketch, "E345", {"start": v(35.1, 20.16) * mm, "end": v(35.73, 20.2) * mm});
            skLineSegment(sketch, "E346", {"start": v(35.73, 20.2) * mm, "end": v(36.42, 20.48) * mm});
            skLineSegment(sketch, "E347", {"start": v(36.42, 20.48) * mm, "end": v(37, 20.9) * mm});
            skLineSegment(sketch, "E348", {"start": v(37, 20.9) * mm, "end": v(37.42, 21.34) * mm});
            skLineSegment(sketch, "E349", {"start": v(37.42, 21.34) * mm, "end": v(37.76, 21.85) * mm});
            skLineSegment(sketch, "E350", {"start": v(37.76, 21.85) * mm, "end": v(38.04, 22.4) * mm});
            skLineSegment(sketch, "E351", {"start": v(38.04, 22.4) * mm, "end": v(38.23, 23) * mm});
            skLineSegment(sketch, "E352", {"start": v(38.23, 23) * mm, "end": v(38.27, 23.48) * mm});
            skLineSegment(sketch, "E353", {"start": v(38.27, 23.48) * mm, "end": v(38.2, 24) * mm});
            skLineSegment(sketch, "E354", {"start": v(38.2, 24) * mm, "end": v(37.93, 24.65) * mm});
            skLineSegment(sketch, "E355", {"start": v(37.93, 24.65) * mm, "end": v(37.3, 25.45) * mm});
            skLineSegment(sketch, "E356", {"start": v(37.3, 25.45) * mm, "end": v(36, 26.61) * mm});
            skLineSegment(sketch, "E357", {"start": v(36, 26.61) * mm, "end": v(35.01, 27.43) * mm});
            skLineSegment(sketch, "E358", {"start": v(35.01, 27.43) * mm, "end": v(34.28, 28.16) * mm});
            skLineSegment(sketch, "E359", {"start": v(34.28, 28.16) * mm, "end": v(33.8, 28.8) * mm});
            skLineSegment(sketch, "E360", {"start": v(33.8, 28.8) * mm, "end": v(33.5, 29.4) * mm});
            skLineSegment(sketch, "E361", {"start": v(33.5, 29.4) * mm, "end": v(33.48, 29.73) * mm});
            skLineSegment(sketch, "E362", {"start": v(33.48, 29.73) * mm, "end": v(33.58, 30.16) * mm});
            skLineSegment(sketch, "E363", {"start": v(33.58, 30.16) * mm, "end": v(33.64, 30.48) * mm});
            skLineSegment(sketch, "E364", {"start": v(33.64, 30.48) * mm, "end": v(33.56, 30.8) * mm});
            skLineSegment(sketch, "E365", {"start": v(33.56, 30.8) * mm, "end": v(33.2, 31.42) * mm});
            skLineSegment(sketch, "E366", {"start": v(33.2, 31.42) * mm, "end": v(32.44, 32.27) * mm});
            skLineSegment(sketch, "E367", {"start": v(32.44, 32.27) * mm, "end": v(31.71, 32.8) * mm});
            skLineSegment(sketch, "E368", {"start": v(31.71, 32.8) * mm, "end": v(30.6, 33.35) * mm});
            skLineSegment(sketch, "E369", {"start": v(30.6, 33.35) * mm, "end": v(29.24, 33.77) * mm});
            skLineSegment(sketch, "E370", {"start": v(29.24, 33.77) * mm, "end": v(27.82, 34.05) * mm});
            skLineSegment(sketch, "E371", {"start": v(27.82, 34.05) * mm, "end": v(24.57, 34.54) * mm});
            skLineSegment(sketch, "E372", {"start": v(24.57, 34.54) * mm, "end": v(23.54, 34.76) * mm});
            skLineSegment(sketch, "E373", {"start": v(23.54, 34.76) * mm, "end": v(22.88, 35.1) * mm});
            skLineSegment(sketch, "E374", {"start": v(22.88, 35.1) * mm, "end": v(21.85, 35.9) * mm});
            skLineSegment(sketch, "E375", {"start": v(21.85, 35.9) * mm, "end": v(19.96, 37.08) * mm});
            skLineSegment(sketch, "E376", {"start": v(19.96, 37.08) * mm, "end": v(18.43, 37.88) * mm});
            skLineSegment(sketch, "E377", {"start": v(18.43, 37.88) * mm, "end": v(17.21, 38.35) * mm});
            skLineSegment(sketch, "E378", {"start": v(17.21, 38.35) * mm, "end": v(15.9, 38.66) * mm});
            skLineSegment(sketch, "E379", {"start": v(15.9, 38.66) * mm, "end": v(13.68, 38.9) * mm});
            skLineSegment(sketch, "E380", {"start": v(13.68, 38.9) * mm, "end": v(11.67, 39) * mm});
            skLineSegment(sketch, "E381", {"start": v(11.67, 39) * mm, "end": v(10.11, 38.94) * mm});
            skLineSegment(sketch, "E382", {"start": v(10.11, 38.94) * mm, "end": v(8.52, 38.61) * mm});
            skLineSegment(sketch, "E383", {"start": v(8.52, 38.61) * mm, "end": v(6.93, 38.1) * mm});
            skLineSegment(sketch, "E384", {"start": v(6.93, 38.1) * mm, "end": v(4.73, 37.52) * mm});
            skLineSegment(sketch, "E385", {"start": v(4.73, 37.52) * mm, "end": v(3.78, 37.41) * mm});
            skLineSegment(sketch, "E386", {"start": v(3.78, 37.41) * mm, "end": v(3.1, 37.46) * mm});
            skLineSegment(sketch, "E387", {"start": v(3.1, 37.46) * mm, "end": v(2.37, 37.64) * mm});
            skLineSegment(sketch, "E388", {"start": v(2.37, 37.64) * mm, "end": v(0.73, 38.2) * mm});
            skLineSegment(sketch, "E389", {"start": v(0.73, 38.2) * mm, "end": v(-0.98, 38.62) * mm});
            skLineSegment(sketch, "E390", {"start": v(-0.98, 38.62) * mm, "end": v(-2.9, 39) * mm});
            skLineSegment(sketch, "E391", {"start": v(-2.9, 39) * mm, "end": v(-4.2, 39.2) * mm});
            skLineSegment(sketch, "E392", {"start": v(-4.2, 39.2) * mm, "end": v(-5.63, 39.3) * mm});
            skLineSegment(sketch, "E393", {"start": v(-5.63, 39.3) * mm, "end": v(-6.88, 39.26) * mm});
            skLineSegment(sketch, "E394", {"start": v(-6.88, 39.26) * mm, "end": v(-10.18, 38.67) * mm});
            skLineSegment(sketch, "E395", {"start": v(-10.18, 38.67) * mm, "end": v(-12.5, 38.08) * mm});
            skLineSegment(sketch, "E396", {"start": v(10.87, -18.23) * mm, "end": v(11.21, -18) * mm});
            skLineSegment(sketch, "E397", {"start": v(11.21, -18) * mm, "end": v(11.44, -17.55) * mm});
            skLineSegment(sketch, "E398", {"start": v(11.44, -17.55) * mm, "end": v(11.85, -16.44) * mm});
            skLineSegment(sketch, "E399", {"start": v(11.85, -16.44) * mm, "end": v(12.2, -14.97) * mm});
            skLineSegment(sketch, "E400", {"start": v(12.2, -14.97) * mm, "end": v(12.31, -13.5) * mm});
            skLineSegment(sketch, "E401", {"start": v(12.31, -13.5) * mm, "end": v(12.22, -12.15) * mm});
            skLineSegment(sketch, "E402", {"start": v(12.22, -12.15) * mm, "end": v(11.94, -11.43) * mm});
            skLineSegment(sketch, "E403", {"start": v(11.94, -11.43) * mm, "end": v(11.64, -11) * mm});
            skLineSegment(sketch, "E404", {"start": v(11.64, -11) * mm, "end": v(11.37, -10.77) * mm});
            skLineSegment(sketch, "E405", {"start": v(11.37, -10.77) * mm, "end": v(11.19, -10.68) * mm});
            skLineSegment(sketch, "E406", {"start": v(11.19, -10.68) * mm, "end": v(11, -10.66) * mm});
            skLineSegment(sketch, "E407", {"start": v(11, -10.66) * mm, "end": v(10.8, -10.7) * mm});
            skLineSegment(sketch, "E408", {"start": v(10.8, -10.7) * mm, "end": v(10.59, -10.82) * mm});
            skLineSegment(sketch, "E409", {"start": v(10.59, -10.82) * mm, "end": v(10.48, -10.95) * mm});
            skLineSegment(sketch, "E410", {"start": v(10.48, -10.95) * mm, "end": v(10.46, -11.09) * mm});
            skLineSegment(sketch, "E411", {"start": v(10.46, -11.09) * mm, "end": v(10.55, -11.3) * mm});
            skLineSegment(sketch, "E412", {"start": v(10.55, -11.3) * mm, "end": v(10.8, -11.57) * mm});
            skLineSegment(sketch, "E413", {"start": v(10.8, -11.57) * mm, "end": v(11.57, -12.22) * mm});
            skLineSegment(sketch, "E414", {"start": v(11.57, -12.22) * mm, "end": v(11.76, -12.42) * mm});
            skLineSegment(sketch, "E415", {"start": v(11.76, -12.42) * mm, "end": v(11.85, -12.55) * mm});
            skLineSegment(sketch, "E416", {"start": v(11.85, -12.55) * mm, "end": v(11.86, -12.67) * mm});
            skLineSegment(sketch, "E417", {"start": v(11.86, -12.67) * mm, "end": v(11.79, -12.77) * mm});
            skLineSegment(sketch, "E418", {"start": v(11.79, -12.77) * mm, "end": v(11.67, -12.81) * mm});
            skLineSegment(sketch, "E419", {"start": v(11.67, -12.81) * mm, "end": v(11.48, -12.76) * mm});
            skLineSegment(sketch, "E420", {"start": v(11.48, -12.76) * mm, "end": v(11.34, -12.67) * mm});
            skLineSegment(sketch, "E421", {"start": v(11.34, -12.67) * mm, "end": v(10.9, -12.33) * mm});
            skLineSegment(sketch, "E422", {"start": v(10.9, -12.33) * mm, "end": v(10.67, -12.2) * mm});
            skLineSegment(sketch, "E423", {"start": v(10.67, -12.2) * mm, "end": v(10.46, -12.2) * mm});
            skLineSegment(sketch, "E424", {"start": v(10.46, -12.2) * mm, "end": v(10.26, -12.33) * mm});
            skLineSegment(sketch, "E425", {"start": v(10.26, -12.33) * mm, "end": v(10.11, -12.61) * mm});
            skLineSegment(sketch, "E426", {"start": v(10.11, -12.61) * mm, "end": v(10.05, -12.86) * mm});
            skLineSegment(sketch, "E427", {"start": v(10.05, -12.86) * mm, "end": v(10.09, -13.05) * mm});
            skLineSegment(sketch, "E428", {"start": v(10.09, -13.05) * mm, "end": v(10.2, -13.2) * mm});
            skLineSegment(sketch, "E429", {"start": v(10.2, -13.2) * mm, "end": v(10.41, -13.35) * mm});
            skLineSegment(sketch, "E430", {"start": v(10.41, -13.35) * mm, "end": v(10.76, -13.49) * mm});
            skLineSegment(sketch, "E431", {"start": v(10.76, -13.49) * mm, "end": v(11.25, -13.65) * mm});
            skLineSegment(sketch, "E432", {"start": v(11.25, -13.65) * mm, "end": v(11.45, -13.78) * mm});
            skLineSegment(sketch, "E433", {"start": v(11.45, -13.78) * mm, "end": v(11.53, -13.9) * mm});
            skLineSegment(sketch, "E434", {"start": v(11.53, -13.9) * mm, "end": v(11.55, -14.1) * mm});
            skLineSegment(sketch, "E435", {"start": v(11.55, -14.1) * mm, "end": v(11.48, -14.22) * mm});
            skLineSegment(sketch, "E436", {"start": v(11.48, -14.22) * mm, "end": v(11.39, -14.3) * mm});
            skLineSegment(sketch, "E437", {"start": v(11.39, -14.3) * mm, "end": v(11.19, -14.31) * mm});
            skLineSegment(sketch, "E438", {"start": v(11.19, -14.31) * mm, "end": v(11, -14.26) * mm});
            skLineSegment(sketch, "E439", {"start": v(11, -14.26) * mm, "end": v(10.48, -14.02) * mm});
            skLineSegment(sketch, "E440", {"start": v(10.48, -14.02) * mm, "end": v(10.28, -13.96) * mm});
            skLineSegment(sketch, "E441", {"start": v(10.28, -13.96) * mm, "end": v(10.16, -13.94) * mm});
            skLineSegment(sketch, "E442", {"start": v(10.16, -13.94) * mm, "end": v(10, -13.97) * mm});
            skLineSegment(sketch, "E443", {"start": v(10, -13.97) * mm, "end": v(9.85, -14.08) * mm});
            skLineSegment(sketch, "E444", {"start": v(9.85, -14.08) * mm, "end": v(9.76, -14.31) * mm});
            skLineSegment(sketch, "E445", {"start": v(9.76, -14.31) * mm, "end": v(9.71, -14.62) * mm});
            skLineSegment(sketch, "E446", {"start": v(9.71, -14.62) * mm, "end": v(9.74, -14.77) * mm});
            skLineSegment(sketch, "E447", {"start": v(9.74, -14.77) * mm, "end": v(9.83, -14.88) * mm});
            skLineSegment(sketch, "E448", {"start": v(9.83, -14.88) * mm, "end": v(10.02, -15) * mm});
            skLineSegment(sketch, "E449", {"start": v(10.02, -15) * mm, "end": v(10.35, -15.1) * mm});
            skLineSegment(sketch, "E450", {"start": v(10.35, -15.1) * mm, "end": v(10.72, -15.17) * mm});
            skLineSegment(sketch, "E451", {"start": v(10.72, -15.17) * mm, "end": v(10.96, -15.23) * mm});
            skLineSegment(sketch, "E452", {"start": v(10.96, -15.23) * mm, "end": v(11.2, -15.35) * mm});
            skLineSegment(sketch, "E453", {"start": v(11.2, -15.35) * mm, "end": v(11.26, -15.51) * mm});
            skLineSegment(sketch, "E454", {"start": v(11.26, -15.51) * mm, "end": v(11.22, -15.73) * mm});
            skLineSegment(sketch, "E455", {"start": v(11.22, -15.73) * mm, "end": v(11.12, -15.82) * mm});
            skLineSegment(sketch, "E456", {"start": v(11.12, -15.82) * mm, "end": v(10.92, -15.86) * mm});
            skLineSegment(sketch, "E457", {"start": v(10.92, -15.86) * mm, "end": v(10.76, -15.83) * mm});
            skLineSegment(sketch, "E458", {"start": v(10.76, -15.83) * mm, "end": v(10.2, -15.65) * mm});
            skLineSegment(sketch, "E459", {"start": v(10.2, -15.65) * mm, "end": v(9.93, -15.6) * mm});
            skLineSegment(sketch, "E460", {"start": v(9.93, -15.6) * mm, "end": v(9.7, -15.62) * mm});
            skLineSegment(sketch, "E461", {"start": v(9.7, -15.62) * mm, "end": v(9.51, -15.76) * mm});
            skLineSegment(sketch, "E462", {"start": v(9.51, -15.76) * mm, "end": v(9.37, -16.04) * mm});
            skLineSegment(sketch, "E463", {"start": v(9.37, -16.04) * mm, "end": v(9.34, -16.2) * mm});
            skLineSegment(sketch, "E464", {"start": v(9.34, -16.2) * mm, "end": v(9.35, -16.39) * mm});
            skLineSegment(sketch, "E465", {"start": v(9.35, -16.39) * mm, "end": v(9.5, -16.56) * mm});
            skLineSegment(sketch, "E466", {"start": v(9.5, -16.56) * mm, "end": v(9.74, -16.67) * mm});
            skLineSegment(sketch, "E467", {"start": v(9.74, -16.67) * mm, "end": v(9.96, -16.73) * mm});
            skLineSegment(sketch, "E468", {"start": v(9.96, -16.73) * mm, "end": v(10.7, -16.87) * mm});
            skLineSegment(sketch, "E469", {"start": v(10.7, -16.87) * mm, "end": v(10.9, -16.97) * mm});
            skLineSegment(sketch, "E470", {"start": v(10.9, -16.97) * mm, "end": v(10.95, -17.1) * mm});
            skLineSegment(sketch, "E471", {"start": v(10.95, -17.1) * mm, "end": v(10.95, -17.2) * mm});
            skLineSegment(sketch, "E472", {"start": v(10.95, -17.2) * mm, "end": v(10.87, -17.33) * mm});
            skLineSegment(sketch, "E473", {"start": v(10.87, -17.33) * mm, "end": v(10.78, -17.39) * mm});
            skLineSegment(sketch, "E474", {"start": v(10.78, -17.39) * mm, "end": v(10.61, -17.42) * mm});
            skLineSegment(sketch, "E475", {"start": v(10.61, -17.42) * mm, "end": v(10.38, -17.4) * mm});
            skLineSegment(sketch, "E476", {"start": v(10.38, -17.4) * mm, "end": v(9.8, -17.3) * mm});
            skLineSegment(sketch, "E477", {"start": v(9.8, -17.3) * mm, "end": v(9.56, -17.32) * mm});
            skLineSegment(sketch, "E478", {"start": v(9.56, -17.32) * mm, "end": v(9.4, -17.4) * mm});
            skLineSegment(sketch, "E479", {"start": v(9.4, -17.4) * mm, "end": v(9.2, -17.58) * mm});
            skLineSegment(sketch, "E480", {"start": v(9.2, -17.58) * mm, "end": v(9.11, -17.7) * mm});
            skLineSegment(sketch, "E481", {"start": v(9.11, -17.7) * mm, "end": v(9.08, -17.83) * mm});
            skLineSegment(sketch, "E482", {"start": v(9.08, -17.83) * mm, "end": v(9.1, -17.93) * mm});
            skLineSegment(sketch, "E483", {"start": v(9.1, -17.93) * mm, "end": v(9.2, -18.06) * mm});
            skLineSegment(sketch, "E484", {"start": v(9.2, -18.06) * mm, "end": v(9.4, -18.15) * mm});
            skLineSegment(sketch, "E485", {"start": v(9.4, -18.15) * mm, "end": v(9.7, -18.23) * mm});
            skLineSegment(sketch, "E486", {"start": v(9.7, -18.23) * mm, "end": v(10.02, -18.28) * mm});
            skLineSegment(sketch, "E487", {"start": v(10.02, -18.28) * mm, "end": v(10.3, -18.29) * mm});
            skLineSegment(sketch, "E488", {"start": v(10.3, -18.29) * mm, "end": v(10.66, -18.27) * mm});
            skLineSegment(sketch, "E489", {"start": v(10.66, -18.27) * mm, "end": v(10.87, -18.23) * mm});
            skLineSegment(sketch, "E490", {"start": v(9.36, -19.66) * mm, "end": v(9.67, -19.55) * mm});
            skLineSegment(sketch, "E491", {"start": v(9.67, -19.55) * mm, "end": v(9.96, -19.22) * mm});
            skLineSegment(sketch, "E492", {"start": v(9.96, -19.22) * mm, "end": v(10, -19.09) * mm});
            skLineSegment(sketch, "E493", {"start": v(10, -19.09) * mm, "end": v(9.98, -18.99) * mm});
            skLineSegment(sketch, "E494", {"start": v(9.98, -18.99) * mm, "end": v(9.88, -18.93) * mm});
            skLineSegment(sketch, "E495", {"start": v(9.88, -18.93) * mm, "end": v(9.7, -18.92) * mm});
            skLineSegment(sketch, "E496", {"start": v(9.7, -18.92) * mm, "end": v(9.54, -19) * mm});
            skLineSegment(sketch, "E497", {"start": v(9.54, -19) * mm, "end": v(9.4, -19.12) * mm});
            skLineSegment(sketch, "E498", {"start": v(9.4, -19.12) * mm, "end": v(9.26, -19.27) * mm});
            skLineSegment(sketch, "E499", {"start": v(9.26, -19.27) * mm, "end": v(9.18, -19.43) * mm});
            skLineSegment(sketch, "E500", {"start": v(9.18, -19.43) * mm, "end": v(9.17, -19.54) * mm});
            skLineSegment(sketch, "E501", {"start": v(9.17, -19.54) * mm, "end": v(9.21, -19.62) * mm});
            skLineSegment(sketch, "E502", {"start": v(9.21, -19.62) * mm, "end": v(9.36, -19.66) * mm});
            skLineSegment(sketch, "E503", {"start": v(12.04, -10.33) * mm, "end": v(12.02, -10.2) * mm});
            skLineSegment(sketch, "E504", {"start": v(12.02, -10.2) * mm, "end": v(11.89, -9.93) * mm});
            skLineSegment(sketch, "E505", {"start": v(11.89, -9.93) * mm, "end": v(11.7, -9.7) * mm});
            skLineSegment(sketch, "E506", {"start": v(11.7, -9.7) * mm, "end": v(11.52, -9.57) * mm});
            skLineSegment(sketch, "E507", {"start": v(11.52, -9.57) * mm, "end": v(11.39, -9.53) * mm});
            skLineSegment(sketch, "E508", {"start": v(11.39, -9.53) * mm, "end": v(11.28, -9.54) * mm});
            skLineSegment(sketch, "E509", {"start": v(11.28, -9.54) * mm, "end": v(11.13, -9.63) * mm});
            skLineSegment(sketch, "E510", {"start": v(11.13, -9.63) * mm, "end": v(11.09, -9.76) * mm});
            skLineSegment(sketch, "E511", {"start": v(11.09, -9.76) * mm, "end": v(11.11, -9.92) * mm});
            skLineSegment(sketch, "E512", {"start": v(11.11, -9.92) * mm, "end": v(11.2, -10.08) * mm});
            skLineSegment(sketch, "E513", {"start": v(11.2, -10.08) * mm, "end": v(11.36, -10.28) * mm});
            skLineSegment(sketch, "E514", {"start": v(11.36, -10.28) * mm, "end": v(11.56, -10.44) * mm});
            skLineSegment(sketch, "E515", {"start": v(11.56, -10.44) * mm, "end": v(11.75, -10.54) * mm});
            skLineSegment(sketch, "E516", {"start": v(11.75, -10.54) * mm, "end": v(11.85, -10.55) * mm});
            skLineSegment(sketch, "E517", {"start": v(11.85, -10.55) * mm, "end": v(11.94, -10.53) * mm});
            skLineSegment(sketch, "E518", {"start": v(11.94, -10.53) * mm, "end": v(12.01, -10.47) * mm});
            skLineSegment(sketch, "E519", {"start": v(12.01, -10.47) * mm, "end": v(12.04, -10.38) * mm});
            skLineSegment(sketch, "E520", {"start": v(12.04, -10.38) * mm, "end": v(12.04, -10.33) * mm});
            skLineSegment(sketch, "E521", {"start": v(-6.64, -25.8) * mm, "end": v(-6.37, -25.78) * mm});
            skLineSegment(sketch, "E522", {"start": v(-6.37, -25.78) * mm, "end": v(-6.16, -25.7) * mm});
            skLineSegment(sketch, "E523", {"start": v(-6.16, -25.7) * mm, "end": v(-6.11, -25.6) * mm});
            skLineSegment(sketch, "E524", {"start": v(-6.11, -25.6) * mm, "end": v(-6.11, -25.46) * mm});
            skLineSegment(sketch, "E525", {"start": v(-6.11, -25.46) * mm, "end": v(-6.27, -25.27) * mm});
            skLineSegment(sketch, "E526", {"start": v(-6.27, -25.27) * mm, "end": v(-6.51, -25.13) * mm});
            skLineSegment(sketch, "E527", {"start": v(-6.51, -25.13) * mm, "end": v(-6.78, -25.12) * mm});
            skLineSegment(sketch, "E528", {"start": v(-6.78, -25.12) * mm, "end": v(-6.88, -25.17) * mm});
            skLineSegment(sketch, "E529", {"start": v(-6.88, -25.17) * mm, "end": v(-7.04, -25.28) * mm});
            skLineSegment(sketch, "E530", {"start": v(-7.04, -25.28) * mm, "end": v(-7.11, -25.4) * mm});
            skLineSegment(sketch, "E531", {"start": v(-7.11, -25.4) * mm, "end": v(-7.09, -25.55) * mm});
            skLineSegment(sketch, "E532", {"start": v(-7.09, -25.55) * mm, "end": v(-6.97, -25.69) * mm});
            skLineSegment(sketch, "E533", {"start": v(-6.97, -25.69) * mm, "end": v(-6.82, -25.77) * mm});
            skLineSegment(sketch, "E534", {"start": v(-6.82, -25.77) * mm, "end": v(-6.64, -25.8) * mm});
            skLineSegment(sketch, "E535", {"start": v(-3.75, -25.5) * mm, "end": v(-1.54, -25.24) * mm});
            skLineSegment(sketch, "E536", {"start": v(-1.54, -25.24) * mm, "end": v(0.22, -24.7) * mm});
            skLineSegment(sketch, "E537", {"start": v(0.22, -24.7) * mm, "end": v(2.38, -23.8) * mm});
            skLineSegment(sketch, "E538", {"start": v(2.38, -23.8) * mm, "end": v(4.64, -22.8) * mm});
            skLineSegment(sketch, "E539", {"start": v(4.64, -22.8) * mm, "end": v(5.65, -22.23) * mm});
            skLineSegment(sketch, "E540", {"start": v(5.65, -22.23) * mm, "end": v(6.74, -21.17) * mm});
            skLineSegment(sketch, "E541", {"start": v(6.74, -21.17) * mm, "end": v(7.1, -20.82) * mm});
            skLineSegment(sketch, "E542", {"start": v(7.1, -20.82) * mm, "end": v(7.17, -20.78) * mm});
            skLineSegment(sketch, "E543", {"start": v(7.17, -20.78) * mm, "end": v(7.28, -20.74) * mm});
            skLineSegment(sketch, "E544", {"start": v(7.28, -20.74) * mm, "end": v(7.4, -20.75) * mm});
            skLineSegment(sketch, "E545", {"start": v(7.4, -20.75) * mm, "end": v(7.56, -20.8) * mm});
            skLineSegment(sketch, "E546", {"start": v(7.56, -20.8) * mm, "end": v(7.8, -20.83) * mm});
            skLineSegment(sketch, "E547", {"start": v(7.8, -20.83) * mm, "end": v(8.06, -20.8) * mm});
            skLineSegment(sketch, "E548", {"start": v(8.06, -20.8) * mm, "end": v(8.35, -20.64) * mm});
            skLineSegment(sketch, "E549", {"start": v(8.35, -20.64) * mm, "end": v(8.53, -20.47) * mm});
            skLineSegment(sketch, "E550", {"start": v(8.53, -20.47) * mm, "end": v(8.58, -20.28) * mm});
            skLineSegment(sketch, "E551", {"start": v(8.58, -20.28) * mm, "end": v(8.5, -20.13) * mm});
            skLineSegment(sketch, "E552", {"start": v(8.5, -20.13) * mm, "end": v(8.37, -20.03) * mm});
            skLineSegment(sketch, "E553", {"start": v(8.37, -20.03) * mm, "end": v(8.11, -19.95) * mm});
            skLineSegment(sketch, "E554", {"start": v(8.11, -19.95) * mm, "end": v(7.7, -19.9) * mm});
            skLineSegment(sketch, "E555", {"start": v(7.7, -19.9) * mm, "end": v(7.4, -19.84) * mm});
            skLineSegment(sketch, "E556", {"start": v(7.4, -19.84) * mm, "end": v(7.24, -19.77) * mm});
            skLineSegment(sketch, "E557", {"start": v(7.24, -19.77) * mm, "end": v(7.1, -19.6) * mm});
            skLineSegment(sketch, "E558", {"start": v(7.1, -19.6) * mm, "end": v(7.06, -19.42) * mm});
            skLineSegment(sketch, "E559", {"start": v(7.06, -19.42) * mm, "end": v(7.16, -19.18) * mm});
            skLineSegment(sketch, "E560", {"start": v(7.16, -19.18) * mm, "end": v(7.28, -19.08) * mm});
            skLineSegment(sketch, "E561", {"start": v(7.28, -19.08) * mm, "end": v(7.57, -19.13) * mm});
            skLineSegment(sketch, "E562", {"start": v(7.57, -19.13) * mm, "end": v(8.04, -19.38) * mm});
            skLineSegment(sketch, "E563", {"start": v(8.04, -19.38) * mm, "end": v(8.33, -19.42) * mm});
            skLineSegment(sketch, "E564", {"start": v(8.33, -19.42) * mm, "end": v(8.55, -19.35) * mm});
            skLineSegment(sketch, "E565", {"start": v(8.55, -19.35) * mm, "end": v(8.72, -19.16) * mm});
            skLineSegment(sketch, "E566", {"start": v(8.72, -19.16) * mm, "end": v(8.71, -18.86) * mm});
            skLineSegment(sketch, "E567", {"start": v(8.71, -18.86) * mm, "end": v(8.66, -18.7) * mm});
            skLineSegment(sketch, "E568", {"start": v(8.66, -18.7) * mm, "end": v(8.5, -18.5) * mm});
            skLineSegment(sketch, "E569", {"start": v(8.5, -18.5) * mm, "end": v(8.32, -18.34) * mm});
            skLineSegment(sketch, "E570", {"start": v(8.32, -18.34) * mm, "end": v(7.93, -18.17) * mm});
            skLineSegment(sketch, "E571", {"start": v(7.93, -18.17) * mm, "end": v(7.64, -18.04) * mm});
            skLineSegment(sketch, "E572", {"start": v(7.64, -18.04) * mm, "end": v(7.43, -17.9) * mm});
            skLineSegment(sketch, "E573", {"start": v(7.43, -17.9) * mm, "end": v(7.3, -17.7) * mm});
            skLineSegment(sketch, "E574", {"start": v(7.3, -17.7) * mm, "end": v(7.27, -17.49) * mm});
            skLineSegment(sketch, "E575", {"start": v(7.27, -17.49) * mm, "end": v(7.3, -17.39) * mm});
            skLineSegment(sketch, "E576", {"start": v(7.3, -17.39) * mm, "end": v(7.4, -17.27) * mm});
            skLineSegment(sketch, "E577", {"start": v(7.4, -17.27) * mm, "end": v(7.54, -17.24) * mm});
            skLineSegment(sketch, "E578", {"start": v(7.54, -17.24) * mm, "end": v(7.7, -17.29) * mm});
            skLineSegment(sketch, "E579", {"start": v(7.7, -17.29) * mm, "end": v(7.87, -17.39) * mm});
            skLineSegment(sketch, "E580", {"start": v(7.87, -17.39) * mm, "end": v(8.22, -17.67) * mm});
            skLineSegment(sketch, "E581", {"start": v(8.22, -17.67) * mm, "end": v(8.52, -17.92) * mm});
            skLineSegment(sketch, "E582", {"start": v(8.52, -17.92) * mm, "end": v(8.65, -17.98) * mm});
            skLineSegment(sketch, "E583", {"start": v(8.65, -17.98) * mm, "end": v(8.74, -17.97) * mm});
            skLineSegment(sketch, "E584", {"start": v(8.74, -17.97) * mm, "end": v(8.83, -17.86) * mm});
            skLineSegment(sketch, "E585", {"start": v(8.83, -17.86) * mm, "end": v(8.9, -17.68) * mm});
            skLineSegment(sketch, "E586", {"start": v(8.9, -17.68) * mm, "end": v(8.92, -17.51) * mm});
            skLineSegment(sketch, "E587", {"start": v(8.92, -17.51) * mm, "end": v(8.9, -17.27) * mm});
            skLineSegment(sketch, "E588", {"start": v(8.9, -17.27) * mm, "end": v(8.8, -17.03) * mm});
            skLineSegment(sketch, "E589", {"start": v(8.8, -17.03) * mm, "end": v(8.58, -16.74) * mm});
            skLineSegment(sketch, "E590", {"start": v(8.58, -16.74) * mm, "end": v(8.38, -16.53) * mm});
            skLineSegment(sketch, "E591", {"start": v(8.38, -16.53) * mm, "end": v(7.74, -15.92) * mm});
            skLineSegment(sketch, "E592", {"start": v(7.74, -15.92) * mm, "end": v(7.62, -15.76) * mm});
            skLineSegment(sketch, "E593", {"start": v(7.62, -15.76) * mm, "end": v(7.59, -15.71) * mm});
            skLineSegment(sketch, "E594", {"start": v(7.59, -15.71) * mm, "end": v(7.57, -15.52) * mm});
            skLineSegment(sketch, "E595", {"start": v(7.57, -15.52) * mm, "end": v(7.63, -15.39) * mm});
            skLineSegment(sketch, "E596", {"start": v(7.63, -15.39) * mm, "end": v(7.74, -15.32) * mm});
            skLineSegment(sketch, "E597", {"start": v(7.74, -15.32) * mm, "end": v(7.87, -15.33) * mm});
            skLineSegment(sketch, "E598", {"start": v(7.87, -15.33) * mm, "end": v(8, -15.4) * mm});
            skLineSegment(sketch, "E599", {"start": v(8, -15.4) * mm, "end": v(8.14, -15.54) * mm});
            skLineSegment(sketch, "E600", {"start": v(8.14, -15.54) * mm, "end": v(8.42, -15.87) * mm});
            skLineSegment(sketch, "E601", {"start": v(8.42, -15.87) * mm, "end": v(8.63, -16.08) * mm});
            skLineSegment(sketch, "E602", {"start": v(8.63, -16.08) * mm, "end": v(8.7, -16.12) * mm});
            skLineSegment(sketch, "E603", {"start": v(8.7, -16.12) * mm, "end": v(8.85, -16.16) * mm});
            skLineSegment(sketch, "E604", {"start": v(8.85, -16.16) * mm, "end": v(9, -16.11) * mm});
            skLineSegment(sketch, "E605", {"start": v(9, -16.11) * mm, "end": v(9.18, -15.95) * mm});
            skLineSegment(sketch, "E606", {"start": v(9.18, -15.95) * mm, "end": v(9.24, -15.83) * mm});
            skLineSegment(sketch, "E607", {"start": v(9.24, -15.83) * mm, "end": v(9.26, -15.63) * mm});
            skLineSegment(sketch, "E608", {"start": v(9.26, -15.63) * mm, "end": v(9.21, -15.43) * mm});
            skLineSegment(sketch, "E609", {"start": v(9.21, -15.43) * mm, "end": v(9.05, -15.15) * mm});
            skLineSegment(sketch, "E610", {"start": v(9.05, -15.15) * mm, "end": v(8.8, -14.87) * mm});
            skLineSegment(sketch, "E611", {"start": v(8.8, -14.87) * mm, "end": v(8.4, -14.45) * mm});
            skLineSegment(sketch, "E612", {"start": v(8.4, -14.45) * mm, "end": v(8.07, -14.12) * mm});
            skLineSegment(sketch, "E613", {"start": v(8.07, -14.12) * mm, "end": v(7.85, -13.83) * mm});
            skLineSegment(sketch, "E614", {"start": v(7.85, -13.83) * mm, "end": v(7.8, -13.67) * mm});
            skLineSegment(sketch, "E615", {"start": v(7.8, -13.67) * mm, "end": v(7.8, -13.53) * mm});
            skLineSegment(sketch, "E616", {"start": v(7.8, -13.53) * mm, "end": v(7.87, -13.45) * mm});
            skLineSegment(sketch, "E617", {"start": v(7.87, -13.45) * mm, "end": v(8, -13.37) * mm});
            skLineSegment(sketch, "E618", {"start": v(8, -13.37) * mm, "end": v(8.2, -13.38) * mm});
            skLineSegment(sketch, "E619", {"start": v(8.2, -13.38) * mm, "end": v(8.34, -13.47) * mm});
            skLineSegment(sketch, "E620", {"start": v(8.34, -13.47) * mm, "end": v(8.63, -13.84) * mm});
            skLineSegment(sketch, "E621", {"start": v(8.63, -13.84) * mm, "end": v(8.8, -14.08) * mm});
            skLineSegment(sketch, "E622", {"start": v(8.8, -14.08) * mm, "end": v(9.02, -14.25) * mm});
            skLineSegment(sketch, "E623", {"start": v(9.02, -14.25) * mm, "end": v(9.25, -14.3) * mm});
            skLineSegment(sketch, "E624", {"start": v(9.25, -14.3) * mm, "end": v(9.35, -14.2) * mm});
            skLineSegment(sketch, "E625", {"start": v(9.35, -14.2) * mm, "end": v(9.45, -13.94) * mm});
            skLineSegment(sketch, "E626", {"start": v(9.45, -13.94) * mm, "end": v(9.5, -13.61) * mm});
            skLineSegment(sketch, "E627", {"start": v(9.5, -13.61) * mm, "end": v(9.5, -13.41) * mm});
            skLineSegment(sketch, "E628", {"start": v(9.5, -13.41) * mm, "end": v(9.44, -13.28) * mm});
            skLineSegment(sketch, "E629", {"start": v(9.44, -13.28) * mm, "end": v(9.14, -12.95) * mm});
            skLineSegment(sketch, "E630", {"start": v(9.14, -12.95) * mm, "end": v(8.48, -12.32) * mm});
            skLineSegment(sketch, "E631", {"start": v(8.48, -12.32) * mm, "end": v(8.3, -12.1) * mm});
            skLineSegment(sketch, "E632", {"start": v(8.3, -12.1) * mm, "end": v(8.24, -11.95) * mm});
            skLineSegment(sketch, "E633", {"start": v(8.24, -11.95) * mm, "end": v(8.22, -11.82) * mm});
            skLineSegment(sketch, "E634", {"start": v(8.22, -11.82) * mm, "end": v(8.26, -11.7) * mm});
            skLineSegment(sketch, "E635", {"start": v(8.26, -11.7) * mm, "end": v(8.46, -11.55) * mm});
            skLineSegment(sketch, "E636", {"start": v(8.46, -11.55) * mm, "end": v(8.65, -11.56) * mm});
            skLineSegment(sketch, "E637", {"start": v(8.65, -11.56) * mm, "end": v(8.89, -11.75) * mm});
            skLineSegment(sketch, "E638", {"start": v(8.89, -11.75) * mm, "end": v(9.08, -12.02) * mm});
            skLineSegment(sketch, "E639", {"start": v(9.08, -12.02) * mm, "end": v(9.32, -12.39) * mm});
            skLineSegment(sketch, "E640", {"start": v(9.32, -12.39) * mm, "end": v(9.51, -12.53) * mm});
            skLineSegment(sketch, "E641", {"start": v(9.51, -12.53) * mm, "end": v(9.65, -12.55) * mm});
            skLineSegment(sketch, "E642", {"start": v(9.65, -12.55) * mm, "end": v(9.82, -12.48) * mm});
            skLineSegment(sketch, "E643", {"start": v(9.82, -12.48) * mm, "end": v(9.97, -12.33) * mm});
            skLineSegment(sketch, "E644", {"start": v(9.97, -12.33) * mm, "end": v(10.03, -12.16) * mm});
            skLineSegment(sketch, "E645", {"start": v(10.03, -12.16) * mm, "end": v(10, -11.88) * mm});
            skLineSegment(sketch, "E646", {"start": v(10, -11.88) * mm, "end": v(9.84, -11.57) * mm});
            skLineSegment(sketch, "E647", {"start": v(9.84, -11.57) * mm, "end": v(9.62, -11.24) * mm});
            skLineSegment(sketch, "E648", {"start": v(9.62, -11.24) * mm, "end": v(9, -10.43) * mm});
            skLineSegment(sketch, "E649", {"start": v(9, -10.43) * mm, "end": v(8.82, -10.15) * mm});
            skLineSegment(sketch, "E650", {"start": v(8.82, -10.15) * mm, "end": v(8.76, -10.03) * mm});
            skLineSegment(sketch, "E651", {"start": v(8.76, -10.03) * mm, "end": v(8.73, -9.88) * mm});
            skLineSegment(sketch, "E652", {"start": v(8.73, -9.88) * mm, "end": v(8.77, -9.76) * mm});
            skLineSegment(sketch, "E653", {"start": v(8.77, -9.76) * mm, "end": v(8.88, -9.7) * mm});
            skLineSegment(sketch, "E654", {"start": v(8.88, -9.7) * mm, "end": v(9.03, -9.67) * mm});
            skLineSegment(sketch, "E655", {"start": v(9.03, -9.67) * mm, "end": v(9.17, -9.7) * mm});
            skLineSegment(sketch, "E656", {"start": v(9.17, -9.7) * mm, "end": v(9.3, -9.8) * mm});
            skLineSegment(sketch, "E657", {"start": v(9.3, -9.8) * mm, "end": v(9.4, -9.95) * mm});
            skLineSegment(sketch, "E658", {"start": v(9.4, -9.95) * mm, "end": v(9.5, -10.12) * mm});
            skLineSegment(sketch, "E659", {"start": v(9.5, -10.12) * mm, "end": v(9.79, -10.71) * mm});
            skLineSegment(sketch, "E660", {"start": v(9.79, -10.71) * mm, "end": v(9.9, -10.9) * mm});
            skLineSegment(sketch, "E661", {"start": v(9.9, -10.9) * mm, "end": v(10.04, -11.02) * mm});
            skLineSegment(sketch, "E662", {"start": v(10.04, -11.02) * mm, "end": v(10.23, -10.99) * mm});
            skLineSegment(sketch, "E663", {"start": v(10.23, -10.99) * mm, "end": v(10.37, -10.9) * mm});
            skLineSegment(sketch, "E664", {"start": v(10.37, -10.9) * mm, "end": v(10.53, -10.69) * mm});
            skLineSegment(sketch, "E665", {"start": v(10.53, -10.69) * mm, "end": v(10.54, -10.5) * mm});
            skLineSegment(sketch, "E666", {"start": v(10.54, -10.5) * mm, "end": v(10.5, -10.3) * mm});
            skLineSegment(sketch, "E667", {"start": v(10.5, -10.3) * mm, "end": v(10.3, -9.92) * mm});
            skLineSegment(sketch, "E668", {"start": v(10.3, -9.92) * mm, "end": v(10.02, -9.53) * mm});
            skLineSegment(sketch, "E669", {"start": v(10.02, -9.53) * mm, "end": v(9.53, -8.85) * mm});
            skLineSegment(sketch, "E670", {"start": v(9.53, -8.85) * mm, "end": v(9.39, -8.59) * mm});
            skLineSegment(sketch, "E671", {"start": v(9.39, -8.59) * mm, "end": v(9.35, -8.41) * mm});
            skLineSegment(sketch, "E672", {"start": v(9.35, -8.41) * mm, "end": v(9.38, -8.27) * mm});
            skLineSegment(sketch, "E673", {"start": v(9.38, -8.27) * mm, "end": v(9.44, -8.19) * mm});
            skLineSegment(sketch, "E674", {"start": v(9.44, -8.19) * mm, "end": v(9.63, -8.13) * mm});
            skLineSegment(sketch, "E675", {"start": v(9.63, -8.13) * mm, "end": v(9.76, -8.17) * mm});
            skLineSegment(sketch, "E676", {"start": v(9.76, -8.17) * mm, "end": v(9.95, -8.33) * mm});
            skLineSegment(sketch, "E677", {"start": v(9.95, -8.33) * mm, "end": v(10.24, -8.77) * mm});
            skLineSegment(sketch, "E678", {"start": v(10.24, -8.77) * mm, "end": v(10.4, -9.06) * mm});
            skLineSegment(sketch, "E679", {"start": v(10.4, -9.06) * mm, "end": v(10.6, -9.36) * mm});
            skLineSegment(sketch, "E680", {"start": v(10.6, -9.36) * mm, "end": v(10.64, -9.4) * mm});
            skLineSegment(sketch, "E681", {"start": v(10.64, -9.4) * mm, "end": v(10.73, -9.47) * mm});
            skLineSegment(sketch, "E682", {"start": v(10.73, -9.47) * mm, "end": v(10.86, -9.39) * mm});
            skLineSegment(sketch, "E683", {"start": v(10.86, -9.39) * mm, "end": v(10.97, -9.14) * mm});
            skLineSegment(sketch, "E684", {"start": v(10.97, -9.14) * mm, "end": v(10.98, -8.94) * mm});
            skLineSegment(sketch, "E685", {"start": v(10.98, -8.94) * mm, "end": v(10.9, -8.65) * mm});
            skLineSegment(sketch, "E686", {"start": v(10.9, -8.65) * mm, "end": v(10.72, -8.37) * mm});
            skLineSegment(sketch, "E687", {"start": v(10.72, -8.37) * mm, "end": v(10.49, -8.1) * mm});
            skLineSegment(sketch, "E688", {"start": v(10.49, -8.1) * mm, "end": v(9.83, -7.5) * mm});
            skLineSegment(sketch, "E689", {"start": v(9.83, -7.5) * mm, "end": v(9.7, -7.33) * mm});
            skLineSegment(sketch, "E690", {"start": v(9.7, -7.33) * mm, "end": v(9.67, -7.16) * mm});
            skLineSegment(sketch, "E691", {"start": v(9.67, -7.16) * mm, "end": v(9.7, -7.02) * mm});
            skLineSegment(sketch, "E692", {"start": v(9.7, -7.02) * mm, "end": v(9.79, -6.9) * mm});
            skLineSegment(sketch, "E693", {"start": v(9.79, -6.9) * mm, "end": v(9.8, -6.68) * mm});
            skLineSegment(sketch, "E694", {"start": v(9.8, -6.68) * mm, "end": v(9.6, -6.33) * mm});
            skLineSegment(sketch, "E695", {"start": v(9.6, -6.33) * mm, "end": v(9.05, -5.77) * mm});
            skLineSegment(sketch, "E696", {"start": v(9.05, -5.77) * mm, "end": v(7.53, -4.64) * mm});
            skLineSegment(sketch, "E697", {"start": v(7.53, -4.64) * mm, "end": v(6.26, -3.78) * mm});
            skLineSegment(sketch, "E698", {"start": v(6.26, -3.78) * mm, "end": v(5.1, -3.1) * mm});
            skLineSegment(sketch, "E699", {"start": v(5.1, -3.1) * mm, "end": v(3.52, -2.31) * mm});
            skLineSegment(sketch, "E700", {"start": v(3.52, -2.31) * mm, "end": v(1.99, -1.69) * mm});
            skLineSegment(sketch, "E701", {"start": v(1.99, -1.69) * mm, "end": v(0.05, -1.08) * mm});
            skLineSegment(sketch, "E702", {"start": v(0.05, -1.08) * mm, "end": v(-1.19, -0.8) * mm});
            skLineSegment(sketch, "E703", {"start": v(-1.19, -0.8) * mm, "end": v(-2.67, -0.6) * mm});
            skLineSegment(sketch, "E704", {"start": v(-2.67, -0.6) * mm, "end": v(-3.9, -0.53) * mm});
            skLineSegment(sketch, "E705", {"start": v(-3.9, -0.53) * mm, "end": v(-5.24, -0.58) * mm});
            skLineSegment(sketch, "E706", {"start": v(-5.24, -0.58) * mm, "end": v(-7.43, -0.93) * mm});
            skLineSegment(sketch, "E707", {"start": v(-7.43, -0.93) * mm, "end": v(-9.55, -1.26) * mm});
            skLineSegment(sketch, "E708", {"start": v(-9.55, -1.26) * mm, "end": v(-11.91, -1.98) * mm});
            skLineSegment(sketch, "E709", {"start": v(-11.91, -1.98) * mm, "end": v(-13.03, -2.5) * mm});
            skLineSegment(sketch, "E710", {"start": v(-13.03, -2.5) * mm, "end": v(-13.04, -2.56) * mm});
            skLineSegment(sketch, "E711", {"start": v(-13.04, -2.56) * mm, "end": v(-12.98, -2.58) * mm});
            skLineSegment(sketch, "E712", {"start": v(-12.98, -2.58) * mm, "end": v(-12.7, -2.54) * mm});
            skLineSegment(sketch, "E713", {"start": v(-12.7, -2.54) * mm, "end": v(-12.46, -2.5) * mm});
            skLineSegment(sketch, "E714", {"start": v(-12.46, -2.5) * mm, "end": v(-12.25, -2.56) * mm});
            skLineSegment(sketch, "E715", {"start": v(-12.25, -2.56) * mm, "end": v(-12.16, -2.68) * mm});
            skLineSegment(sketch, "E716", {"start": v(-12.16, -2.68) * mm, "end": v(-12.18, -2.79) * mm});
            skLineSegment(sketch, "E717", {"start": v(-12.18, -2.79) * mm, "end": v(-12.3, -2.9) * mm});
            skLineSegment(sketch, "E718", {"start": v(-12.3, -2.9) * mm, "end": v(-12.55, -3) * mm});
            skLineSegment(sketch, "E719", {"start": v(-12.55, -3) * mm, "end": v(-12.88, -3.13) * mm});
            skLineSegment(sketch, "E720", {"start": v(-12.88, -3.13) * mm, "end": v(-12.9, -3.16) * mm});
            skLineSegment(sketch, "E721", {"start": v(-12.9, -3.16) * mm, "end": v(-12.9, -3.17) * mm});
            skLineSegment(sketch, "E722", {"start": v(-12.9, -3.17) * mm, "end": v(-12.74, -3.19) * mm});
            skLineSegment(sketch, "E723", {"start": v(-12.74, -3.19) * mm, "end": v(-12.47, -3.16) * mm});
            skLineSegment(sketch, "E724", {"start": v(-12.47, -3.16) * mm, "end": v(-12.18, -3.1) * mm});
            skLineSegment(sketch, "E725", {"start": v(-12.18, -3.1) * mm, "end": v(-11.44, -2.87) * mm});
            skLineSegment(sketch, "E726", {"start": v(-11.44, -2.87) * mm, "end": v(-10.65, -2.65) * mm});
            skLineSegment(sketch, "E727", {"start": v(-10.65, -2.65) * mm, "end": v(-10.2, -2.6) * mm});
            skLineSegment(sketch, "E728", {"start": v(-10.2, -2.6) * mm, "end": v(-9.95, -2.64) * mm});
            skLineSegment(sketch, "E729", {"start": v(-9.95, -2.64) * mm, "end": v(-9.83, -2.72) * mm});
            skLineSegment(sketch, "E730", {"start": v(-9.83, -2.72) * mm, "end": v(-9.76, -2.84) * mm});
            skLineSegment(sketch, "E731", {"start": v(-9.76, -2.84) * mm, "end": v(-9.76, -2.96) * mm});
            skLineSegment(sketch, "E732", {"start": v(-9.76, -2.96) * mm, "end": v(-9.9, -3.1) * mm});
            skLineSegment(sketch, "E733", {"start": v(-9.9, -3.1) * mm, "end": v(-10.17, -3.2) * mm});
            skLineSegment(sketch, "E734", {"start": v(-10.17, -3.2) * mm, "end": v(-10.6, -3.28) * mm});
            skLineSegment(sketch, "E735", {"start": v(-10.6, -3.28) * mm, "end": v(-11.17, -3.35) * mm});
            skLineSegment(sketch, "E736", {"start": v(-11.17, -3.35) * mm, "end": v(-11.32, -3.38) * mm});
            skLineSegment(sketch, "E737", {"start": v(-11.32, -3.38) * mm, "end": v(-11.42, -3.44) * mm});
            skLineSegment(sketch, "E738", {"start": v(-11.42, -3.44) * mm, "end": v(-11.41, -3.49) * mm});
            skLineSegment(sketch, "E739", {"start": v(-11.41, -3.49) * mm, "end": v(-11.3, -3.6) * mm});
            skLineSegment(sketch, "E740", {"start": v(-11.3, -3.6) * mm, "end": v(-11.1, -3.7) * mm});
            skLineSegment(sketch, "E741", {"start": v(-11.1, -3.7) * mm, "end": v(-10.86, -3.75) * mm});
            skLineSegment(sketch, "E742", {"start": v(-10.86, -3.75) * mm, "end": v(-10.55, -3.77) * mm});
            skLineSegment(sketch, "E743", {"start": v(-10.55, -3.77) * mm, "end": v(-10.06, -3.74) * mm});
            skLineSegment(sketch, "E744", {"start": v(-10.06, -3.74) * mm, "end": v(-9.46, -3.65) * mm});
            skLineSegment(sketch, "E745", {"start": v(-9.46, -3.65) * mm, "end": v(-8.84, -3.54) * mm});
            skLineSegment(sketch, "E746", {"start": v(-8.84, -3.54) * mm, "end": v(-8.43, -3.46) * mm});
            skLineSegment(sketch, "E747", {"start": v(-8.43, -3.46) * mm, "end": v(-8.13, -3.44) * mm});
            skLineSegment(sketch, "E748", {"start": v(-8.13, -3.44) * mm, "end": v(-7.89, -3.46) * mm});
            skLineSegment(sketch, "E749", {"start": v(-7.89, -3.46) * mm, "end": v(-7.7, -3.53) * mm});
            skLineSegment(sketch, "E750", {"start": v(-7.7, -3.53) * mm, "end": v(-7.62, -3.61) * mm});
            skLineSegment(sketch, "E751", {"start": v(-7.62, -3.61) * mm, "end": v(-7.6, -3.72) * mm});
            skLineSegment(sketch, "E752", {"start": v(-7.6, -3.72) * mm, "end": v(-7.65, -3.83) * mm});
            skLineSegment(sketch, "E753", {"start": v(-7.65, -3.83) * mm, "end": v(-7.8, -3.9) * mm});
            skLineSegment(sketch, "E754", {"start": v(-7.8, -3.9) * mm, "end": v(-7.96, -3.95) * mm});
            skLineSegment(sketch, "E755", {"start": v(-7.96, -3.95) * mm, "end": v(-8.25, -4) * mm});
            skLineSegment(sketch, "E756", {"start": v(-8.25, -4) * mm, "end": v(-9.25, -4.13) * mm});
            skLineSegment(sketch, "E757", {"start": v(-9.25, -4.13) * mm, "end": v(-9.45, -4.17) * mm});
            skLineSegment(sketch, "E758", {"start": v(-9.45, -4.17) * mm, "end": v(-9.5, -4.2) * mm});
            skLineSegment(sketch, "E759", {"start": v(-9.5, -4.2) * mm, "end": v(-9.5, -4.25) * mm});
            skLineSegment(sketch, "E760", {"start": v(-9.5, -4.25) * mm, "end": v(-9.38, -4.42) * mm});
            skLineSegment(sketch, "E761", {"start": v(-9.38, -4.42) * mm, "end": v(-9.25, -4.52) * mm});
            skLineSegment(sketch, "E762", {"start": v(-9.25, -4.52) * mm, "end": v(-9.08, -4.6) * mm});
            skLineSegment(sketch, "E763", {"start": v(-9.08, -4.6) * mm, "end": v(-8.93, -4.64) * mm});
            skLineSegment(sketch, "E764", {"start": v(-8.93, -4.64) * mm, "end": v(-8.67, -4.67) * mm});
            skLineSegment(sketch, "E765", {"start": v(-8.67, -4.67) * mm, "end": v(-8.32, -4.67) * mm});
            skLineSegment(sketch, "E766", {"start": v(-8.32, -4.67) * mm, "end": v(-8, -4.65) * mm});
            skLineSegment(sketch, "E767", {"start": v(-8, -4.65) * mm, "end": v(-7.37, -4.58) * mm});
            skLineSegment(sketch, "E768", {"start": v(-7.37, -4.58) * mm, "end": v(-6.81, -4.53) * mm});
            skLineSegment(sketch, "E769", {"start": v(-6.81, -4.53) * mm, "end": v(-6.52, -4.54) * mm});
            skLineSegment(sketch, "E770", {"start": v(-6.52, -4.54) * mm, "end": v(-6.25, -4.57) * mm});
            skLineSegment(sketch, "E771", {"start": v(-6.25, -4.57) * mm, "end": v(-6.04, -4.67) * mm});
            skLineSegment(sketch, "E772", {"start": v(-6.04, -4.67) * mm, "end": v(-5.86, -4.85) * mm});
            skLineSegment(sketch, "E773", {"start": v(-5.86, -4.85) * mm, "end": v(-5.82, -5) * mm});
            skLineSegment(sketch, "E774", {"start": v(-5.82, -5) * mm, "end": v(-5.85, -5.1) * mm});
            skLineSegment(sketch, "E775", {"start": v(-5.85, -5.1) * mm, "end": v(-5.95, -5.15) * mm});
            skLineSegment(sketch, "E776", {"start": v(-5.95, -5.15) * mm, "end": v(-6.09, -5.17) * mm});
            skLineSegment(sketch, "E777", {"start": v(-6.09, -5.17) * mm, "end": v(-6.23, -5.18) * mm});
            skLineSegment(sketch, "E778", {"start": v(-6.23, -5.18) * mm, "end": v(-6.58, -5.17) * mm});
            skLineSegment(sketch, "E779", {"start": v(-6.58, -5.17) * mm, "end": v(-7.28, -5.12) * mm});
            skLineSegment(sketch, "E780", {"start": v(-7.28, -5.12) * mm, "end": v(-7.52, -5.13) * mm});
            skLineSegment(sketch, "E781", {"start": v(-7.52, -5.13) * mm, "end": v(-7.66, -5.16) * mm});
            skLineSegment(sketch, "E782", {"start": v(-7.66, -5.16) * mm, "end": v(-7.75, -5.2) * mm});
            skLineSegment(sketch, "E783", {"start": v(-7.75, -5.2) * mm, "end": v(-7.78, -5.29) * mm});
            skLineSegment(sketch, "E784", {"start": v(-7.78, -5.29) * mm, "end": v(-7.77, -5.4) * mm});
            skLineSegment(sketch, "E785", {"start": v(-7.77, -5.4) * mm, "end": v(-7.74, -5.52) * mm});
            skLineSegment(sketch, "E786", {"start": v(-7.74, -5.52) * mm, "end": v(-7.6, -5.7) * mm});
            skLineSegment(sketch, "E787", {"start": v(-7.6, -5.7) * mm, "end": v(-7.47, -5.78) * mm});
            skLineSegment(sketch, "E788", {"start": v(-7.47, -5.78) * mm, "end": v(-7.27, -5.86) * mm});
            skLineSegment(sketch, "E789", {"start": v(-7.27, -5.86) * mm, "end": v(-7.03, -5.92) * mm});
            skLineSegment(sketch, "E790", {"start": v(-7.03, -5.92) * mm, "end": v(-6.67, -5.96) * mm});
            skLineSegment(sketch, "E791", {"start": v(-6.67, -5.96) * mm, "end": v(-5.94, -5.99) * mm});
            skLineSegment(sketch, "E792", {"start": v(-5.94, -5.99) * mm, "end": v(-5.11, -6) * mm});
            skLineSegment(sketch, "E793", {"start": v(-5.11, -6) * mm, "end": v(-4.8, -6.04) * mm});
            skLineSegment(sketch, "E794", {"start": v(-4.8, -6.04) * mm, "end": v(-4.55, -6.1) * mm});
            skLineSegment(sketch, "E795", {"start": v(-4.55, -6.1) * mm, "end": v(-4.38, -6.22) * mm});
            skLineSegment(sketch, "E796", {"start": v(-4.38, -6.22) * mm, "end": v(-4.3, -6.33) * mm});
            skLineSegment(sketch, "E797", {"start": v(-4.3, -6.33) * mm, "end": v(-4.32, -6.42) * mm});
            skLineSegment(sketch, "E798", {"start": v(-4.32, -6.42) * mm, "end": v(-4.4, -6.49) * mm});
            skLineSegment(sketch, "E799", {"start": v(-4.4, -6.49) * mm, "end": v(-4.52, -6.53) * mm});
            skLineSegment(sketch, "E800", {"start": v(-4.52, -6.53) * mm, "end": v(-4.68, -6.55) * mm});
            skLineSegment(sketch, "E801", {"start": v(-4.68, -6.55) * mm, "end": v(-4.9, -6.56) * mm});
            skLineSegment(sketch, "E802", {"start": v(-4.9, -6.56) * mm, "end": v(-5.46, -6.54) * mm});
            skLineSegment(sketch, "E803", {"start": v(-5.46, -6.54) * mm, "end": v(-6.14, -6.52) * mm});
            skLineSegment(sketch, "E804", {"start": v(-6.14, -6.52) * mm, "end": v(-6.4, -6.53) * mm});
            skLineSegment(sketch, "E805", {"start": v(-6.4, -6.53) * mm, "end": v(-6.54, -6.57) * mm});
            skLineSegment(sketch, "E806", {"start": v(-6.54, -6.57) * mm, "end": v(-6.56, -6.63) * mm});
            skLineSegment(sketch, "E807", {"start": v(-6.56, -6.63) * mm, "end": v(-6.53, -6.71) * mm});
            skLineSegment(sketch, "E808", {"start": v(-6.53, -6.71) * mm, "end": v(-6.44, -6.86) * mm});
            skLineSegment(sketch, "E809", {"start": v(-6.44, -6.86) * mm, "end": v(-6.1, -7.17) * mm});
            skLineSegment(sketch, "E810", {"start": v(-6.1, -7.17) * mm, "end": v(-5.78, -7.32) * mm});
            skLineSegment(sketch, "E811", {"start": v(-5.78, -7.32) * mm, "end": v(-5.2, -7.5) * mm});
            skLineSegment(sketch, "E812", {"start": v(-5.2, -7.5) * mm, "end": v(-4.05, -7.72) * mm});
            skLineSegment(sketch, "E813", {"start": v(-4.05, -7.72) * mm, "end": v(-3.34, -7.8) * mm});
            skLineSegment(sketch, "E814", {"start": v(-3.34, -7.8) * mm, "end": v(-3.13, -7.97) * mm});
            skLineSegment(sketch, "E815", {"start": v(-3.13, -7.97) * mm, "end": v(-3.06, -8.12) * mm});
            skLineSegment(sketch, "E816", {"start": v(-3.06, -8.12) * mm, "end": v(-3.07, -8.23) * mm});
            skLineSegment(sketch, "E817", {"start": v(-3.07, -8.23) * mm, "end": v(-3.14, -8.3) * mm});
            skLineSegment(sketch, "E818", {"start": v(-3.14, -8.3) * mm, "end": v(-3.34, -8.34) * mm});
            skLineSegment(sketch, "E819", {"start": v(-3.34, -8.34) * mm, "end": v(-3.74, -8.3) * mm});
            skLineSegment(sketch, "E820", {"start": v(-3.74, -8.3) * mm, "end": v(-4.7, -8.12) * mm});
            skLineSegment(sketch, "E821", {"start": v(-4.7, -8.12) * mm, "end": v(-5.21, -8.03) * mm});
            skLineSegment(sketch, "E822", {"start": v(-5.21, -8.03) * mm, "end": v(-5.38, -8.03) * mm});
            skLineSegment(sketch, "E823", {"start": v(-5.38, -8.03) * mm, "end": v(-5.5, -8.08) * mm});
            skLineSegment(sketch, "E824", {"start": v(-5.5, -8.08) * mm, "end": v(-5.52, -8.23) * mm});
            skLineSegment(sketch, "E825", {"start": v(-5.52, -8.23) * mm, "end": v(-5.51, -8.4) * mm});
            skLineSegment(sketch, "E826", {"start": v(-5.51, -8.4) * mm, "end": v(-5.43, -8.66) * mm});
            skLineSegment(sketch, "E827", {"start": v(-5.43, -8.66) * mm, "end": v(-5.28, -8.84) * mm});
            skLineSegment(sketch, "E828", {"start": v(-5.28, -8.84) * mm, "end": v(-5.09, -8.97) * mm});
            skLineSegment(sketch, "E829", {"start": v(-5.09, -8.97) * mm, "end": v(-4.76, -9.12) * mm});
            skLineSegment(sketch, "E830", {"start": v(-4.76, -9.12) * mm, "end": v(-4.38, -9.22) * mm});
            skLineSegment(sketch, "E831", {"start": v(-4.38, -9.22) * mm, "end": v(-3.56, -9.35) * mm});
            skLineSegment(sketch, "E832", {"start": v(-3.56, -9.35) * mm, "end": v(-2.72, -9.5) * mm});
            skLineSegment(sketch, "E833", {"start": v(-2.72, -9.5) * mm, "end": v(-2.44, -9.62) * mm});
            skLineSegment(sketch, "E834", {"start": v(-2.44, -9.62) * mm, "end": v(-2.26, -9.76) * mm});
            skLineSegment(sketch, "E835", {"start": v(-2.26, -9.76) * mm, "end": v(-2.2, -9.91) * mm});
            skLineSegment(sketch, "E836", {"start": v(-2.2, -9.91) * mm, "end": v(-2.2, -10.1) * mm});
            skLineSegment(sketch, "E837", {"start": v(-2.2, -10.1) * mm, "end": v(-2.32, -10.2) * mm});
            skLineSegment(sketch, "E838", {"start": v(-2.32, -10.2) * mm, "end": v(-2.44, -10.22) * mm});
            skLineSegment(sketch, "E839", {"start": v(-2.44, -10.22) * mm, "end": v(-2.6, -10.22) * mm});
            skLineSegment(sketch, "E840", {"start": v(-2.6, -10.22) * mm, "end": v(-3.08, -10.12) * mm});
            skLineSegment(sketch, "E841", {"start": v(-3.08, -10.12) * mm, "end": v(-4.06, -9.82) * mm});
            skLineSegment(sketch, "E842", {"start": v(-4.06, -9.82) * mm, "end": v(-4.41, -9.74) * mm});
            skLineSegment(sketch, "E843", {"start": v(-4.41, -9.74) * mm, "end": v(-4.55, -9.74) * mm});
            skLineSegment(sketch, "E844", {"start": v(-4.55, -9.74) * mm, "end": v(-4.68, -9.79) * mm});
            skLineSegment(sketch, "E845", {"start": v(-4.68, -9.79) * mm, "end": v(-4.71, -9.87) * mm});
            skLineSegment(sketch, "E846", {"start": v(-4.71, -9.87) * mm, "end": v(-4.72, -10.07) * mm});
            skLineSegment(sketch, "E847", {"start": v(-4.72, -10.07) * mm, "end": v(-4.66, -10.36) * mm});
            skLineSegment(sketch, "E848", {"start": v(-4.66, -10.36) * mm, "end": v(-4.52, -10.6) * mm});
            skLineSegment(sketch, "E849", {"start": v(-4.52, -10.6) * mm, "end": v(-4.21, -10.92) * mm});
            skLineSegment(sketch, "E850", {"start": v(-4.21, -10.92) * mm, "end": v(-3.88, -11.13) * mm});
            skLineSegment(sketch, "E851", {"start": v(-3.88, -11.13) * mm, "end": v(-3.48, -11.3) * mm});
            skLineSegment(sketch, "E852", {"start": v(-3.48, -11.3) * mm, "end": v(-3.04, -11.42) * mm});
            skLineSegment(sketch, "E853", {"start": v(-3.04, -11.42) * mm, "end": v(-2.62, -11.49) * mm});
            skLineSegment(sketch, "E854", {"start": v(-2.62, -11.49) * mm, "end": v(-2.07, -11.55) * mm});
            skLineSegment(sketch, "E855", {"start": v(-2.07, -11.55) * mm, "end": v(-1.87, -11.63) * mm});
            skLineSegment(sketch, "E856", {"start": v(-1.87, -11.63) * mm, "end": v(-1.72, -11.77) * mm});
            skLineSegment(sketch, "E857", {"start": v(-1.72, -11.77) * mm, "end": v(-1.66, -11.97) * mm});
            skLineSegment(sketch, "E858", {"start": v(-1.66, -11.97) * mm, "end": v(-1.69, -12.12) * mm});
            skLineSegment(sketch, "E859", {"start": v(-1.69, -12.12) * mm, "end": v(-1.76, -12.2) * mm});
            skLineSegment(sketch, "E860", {"start": v(-1.76, -12.2) * mm, "end": v(-1.89, -12.24) * mm});
            skLineSegment(sketch, "E861", {"start": v(-1.89, -12.24) * mm, "end": v(-2.1, -12.24) * mm});
            skLineSegment(sketch, "E862", {"start": v(-2.1, -12.24) * mm, "end": v(-2.44, -12.17) * mm});
            skLineSegment(sketch, "E863", {"start": v(-2.44, -12.17) * mm, "end": v(-3.41, -11.88) * mm});
            skLineSegment(sketch, "E864", {"start": v(-3.41, -11.88) * mm, "end": v(-3.73, -11.8) * mm});
            skLineSegment(sketch, "E865", {"start": v(-3.73, -11.8) * mm, "end": v(-3.89, -11.78) * mm});
            skLineSegment(sketch, "E866", {"start": v(-3.89, -11.78) * mm, "end": v(-4, -11.8) * mm});
            skLineSegment(sketch, "E867", {"start": v(-4, -11.8) * mm, "end": v(-4.06, -11.85) * mm});
            skLineSegment(sketch, "E868", {"start": v(-4.06, -11.85) * mm, "end": v(-4.1, -11.98) * mm});
            skLineSegment(sketch, "E869", {"start": v(-4.1, -11.98) * mm, "end": v(-4.07, -12.27) * mm});
            skLineSegment(sketch, "E870", {"start": v(-4.07, -12.27) * mm, "end": v(-3.94, -12.66) * mm});
            skLineSegment(sketch, "E871", {"start": v(-3.94, -12.66) * mm, "end": v(-3.82, -12.82) * mm});
            skLineSegment(sketch, "E872", {"start": v(-3.82, -12.82) * mm, "end": v(-3.4, -13.13) * mm});
            skLineSegment(sketch, "E873", {"start": v(-3.4, -13.13) * mm, "end": v(-2.66, -13.38) * mm});
            skLineSegment(sketch, "E874", {"start": v(-2.66, -13.38) * mm, "end": v(-2.15, -13.5) * mm});
            skLineSegment(sketch, "E875", {"start": v(-2.15, -13.5) * mm, "end": v(-1.6, -13.61) * mm});
            skLineSegment(sketch, "E876", {"start": v(-1.6, -13.61) * mm, "end": v(-1.43, -13.73) * mm});
            skLineSegment(sketch, "E877", {"start": v(-1.43, -13.73) * mm, "end": v(-1.35, -13.91) * mm});
            skLineSegment(sketch, "E878", {"start": v(-1.35, -13.91) * mm, "end": v(-1.35, -14.1) * mm});
            skLineSegment(sketch, "E879", {"start": v(-1.35, -14.1) * mm, "end": v(-1.46, -14.22) * mm});
            skLineSegment(sketch, "E880", {"start": v(-1.46, -14.22) * mm, "end": v(-1.58, -14.24) * mm});
            skLineSegment(sketch, "E881", {"start": v(-1.58, -14.24) * mm, "end": v(-1.9, -14.18) * mm});
            skLineSegment(sketch, "E882", {"start": v(-1.9, -14.18) * mm, "end": v(-2.3, -14.03) * mm});
            skLineSegment(sketch, "E883", {"start": v(-2.3, -14.03) * mm, "end": v(-3.02, -13.75) * mm});
            skLineSegment(sketch, "E884", {"start": v(-3.02, -13.75) * mm, "end": v(-3.28, -13.68) * mm});
            skLineSegment(sketch, "E885", {"start": v(-3.28, -13.68) * mm, "end": v(-3.48, -13.7) * mm});
            skLineSegment(sketch, "E886", {"start": v(-3.48, -13.7) * mm, "end": v(-3.62, -13.8) * mm});
            skLineSegment(sketch, "E887", {"start": v(-3.62, -13.8) * mm, "end": v(-3.76, -14.12) * mm});
            skLineSegment(sketch, "E888", {"start": v(-3.76, -14.12) * mm, "end": v(-3.81, -14.47) * mm});
            skLineSegment(sketch, "E889", {"start": v(-3.81, -14.47) * mm, "end": v(-3.77, -14.68) * mm});
            skLineSegment(sketch, "E890", {"start": v(-3.77, -14.68) * mm, "end": v(-3.68, -14.85) * mm});
            skLineSegment(sketch, "E891", {"start": v(-3.68, -14.85) * mm, "end": v(-3.53, -14.99) * mm});
            skLineSegment(sketch, "E892", {"start": v(-3.53, -14.99) * mm, "end": v(-3.2, -15.16) * mm});
            skLineSegment(sketch, "E893", {"start": v(-3.2, -15.16) * mm, "end": v(-2.72, -15.3) * mm});
            skLineSegment(sketch, "E894", {"start": v(-2.72, -15.3) * mm, "end": v(-2.05, -15.47) * mm});
            skLineSegment(sketch, "E895", {"start": v(-2.05, -15.47) * mm, "end": v(-1.58, -15.66) * mm});
            skLineSegment(sketch, "E896", {"start": v(-1.58, -15.66) * mm, "end": v(-1.37, -15.86) * mm});
            skLineSegment(sketch, "E897", {"start": v(-1.37, -15.86) * mm, "end": v(-1.32, -16.06) * mm});
            skLineSegment(sketch, "E898", {"start": v(-1.32, -16.06) * mm, "end": v(-1.4, -16.25) * mm});
            skLineSegment(sketch, "E899", {"start": v(-1.4, -16.25) * mm, "end": v(-1.6, -16.36) * mm});
            skLineSegment(sketch, "E900", {"start": v(-1.6, -16.36) * mm, "end": v(-1.8, -16.36) * mm});
            skLineSegment(sketch, "E901", {"start": v(-1.8, -16.36) * mm, "end": v(-2.8, -15.93) * mm});
            skLineSegment(sketch, "E902", {"start": v(-2.8, -15.93) * mm, "end": v(-3.19, -15.82) * mm});
            skLineSegment(sketch, "E903", {"start": v(-3.19, -15.82) * mm, "end": v(-3.28, -15.83) * mm});
            skLineSegment(sketch, "E904", {"start": v(-3.28, -15.83) * mm, "end": v(-3.45, -15.9) * mm});
            skLineSegment(sketch, "E905", {"start": v(-3.45, -15.9) * mm, "end": v(-3.62, -16.12) * mm});
            skLineSegment(sketch, "E906", {"start": v(-3.62, -16.12) * mm, "end": v(-3.62, -16.54) * mm});
            skLineSegment(sketch, "E907", {"start": v(-3.62, -16.54) * mm, "end": v(-3.5, -16.87) * mm});
            skLineSegment(sketch, "E908", {"start": v(-3.5, -16.87) * mm, "end": v(-3.23, -17.26) * mm});
            skLineSegment(sketch, "E909", {"start": v(-3.23, -17.26) * mm, "end": v(-2.95, -17.52) * mm});
            skLineSegment(sketch, "E910", {"start": v(-2.95, -17.52) * mm, "end": v(-2.63, -17.66) * mm});
            skLineSegment(sketch, "E911", {"start": v(-2.63, -17.66) * mm, "end": v(-1.99, -17.82) * mm});
            skLineSegment(sketch, "E912", {"start": v(-1.99, -17.82) * mm, "end": v(-1.77, -17.92) * mm});
            skLineSegment(sketch, "E913", {"start": v(-1.77, -17.92) * mm, "end": v(-1.56, -18.17) * mm});
            skLineSegment(sketch, "E914", {"start": v(-1.56, -18.17) * mm, "end": v(-1.6, -18.48) * mm});
            skLineSegment(sketch, "E915", {"start": v(-1.6, -18.48) * mm, "end": v(-1.76, -18.65) * mm});
            skLineSegment(sketch, "E916", {"start": v(-1.76, -18.65) * mm, "end": v(-2.05, -18.62) * mm});
            skLineSegment(sketch, "E917", {"start": v(-2.05, -18.62) * mm, "end": v(-2.39, -18.42) * mm});
            skLineSegment(sketch, "E918", {"start": v(-2.39, -18.42) * mm, "end": v(-3.11, -17.95) * mm});
            skLineSegment(sketch, "E919", {"start": v(-3.11, -17.95) * mm, "end": v(-3.36, -17.87) * mm});
            skLineSegment(sketch, "E920", {"start": v(-3.36, -17.87) * mm, "end": v(-3.58, -17.9) * mm});
            skLineSegment(sketch, "E921", {"start": v(-3.58, -17.9) * mm, "end": v(-3.77, -18.08) * mm});
            skLineSegment(sketch, "E922", {"start": v(-3.77, -18.08) * mm, "end": v(-3.92, -18.34) * mm});
            skLineSegment(sketch, "E923", {"start": v(-3.92, -18.34) * mm, "end": v(-3.96, -18.65) * mm});
            skLineSegment(sketch, "E924", {"start": v(-3.96, -18.65) * mm, "end": v(-3.86, -18.92) * mm});
            skLineSegment(sketch, "E925", {"start": v(-3.86, -18.92) * mm, "end": v(-3.6, -19.21) * mm});
            skLineSegment(sketch, "E926", {"start": v(-3.6, -19.21) * mm, "end": v(-3.38, -19.37) * mm});
            skLineSegment(sketch, "E927", {"start": v(-3.38, -19.37) * mm, "end": v(-2.4, -19.94) * mm});
            skLineSegment(sketch, "E928", {"start": v(-2.4, -19.94) * mm, "end": v(-2.16, -20.15) * mm});
            skLineSegment(sketch, "E929", {"start": v(-2.16, -20.15) * mm, "end": v(-2.1, -20.31) * mm});
            skLineSegment(sketch, "E930", {"start": v(-2.1, -20.31) * mm, "end": v(-2.12, -20.4) * mm});
            skLineSegment(sketch, "E931", {"start": v(-2.12, -20.4) * mm, "end": v(-2.27, -20.58) * mm});
            skLineSegment(sketch, "E932", {"start": v(-2.27, -20.58) * mm, "end": v(-2.39, -20.62) * mm});
            skLineSegment(sketch, "E933", {"start": v(-2.39, -20.62) * mm, "end": v(-2.52, -20.62) * mm});
            skLineSegment(sketch, "E934", {"start": v(-2.52, -20.62) * mm, "end": v(-2.74, -20.53) * mm});
            skLineSegment(sketch, "E935", {"start": v(-2.74, -20.53) * mm, "end": v(-2.9, -20.44) * mm});
            skLineSegment(sketch, "E936", {"start": v(-2.9, -20.44) * mm, "end": v(-3.6, -19.92) * mm});
            skLineSegment(sketch, "E937", {"start": v(-3.6, -19.92) * mm, "end": v(-3.8, -19.84) * mm});
            skLineSegment(sketch, "E938", {"start": v(-3.8, -19.84) * mm, "end": v(-3.93, -19.8) * mm});
            skLineSegment(sketch, "E939", {"start": v(-3.93, -19.8) * mm, "end": v(-4.04, -19.85) * mm});
            skLineSegment(sketch, "E940", {"start": v(-4.04, -19.85) * mm, "end": v(-4.23, -20.07) * mm});
            skLineSegment(sketch, "E941", {"start": v(-4.23, -20.07) * mm, "end": v(-4.33, -20.36) * mm});
            skLineSegment(sketch, "E942", {"start": v(-4.33, -20.36) * mm, "end": v(-4.35, -20.57) * mm});
            skLineSegment(sketch, "E943", {"start": v(-4.35, -20.57) * mm, "end": v(-4.26, -20.9) * mm});
            skLineSegment(sketch, "E944", {"start": v(-4.26, -20.9) * mm, "end": v(-4.12, -21.13) * mm});
            skLineSegment(sketch, "E945", {"start": v(-4.12, -21.13) * mm, "end": v(-3.8, -21.43) * mm});
            skLineSegment(sketch, "E946", {"start": v(-3.8, -21.43) * mm, "end": v(-3.51, -21.63) * mm});
            skLineSegment(sketch, "E947", {"start": v(-3.51, -21.63) * mm, "end": v(-3.02, -21.85) * mm});
            skLineSegment(sketch, "E948", {"start": v(-3.02, -21.85) * mm, "end": v(-2.8, -22.07) * mm});
            skLineSegment(sketch, "E949", {"start": v(-2.8, -22.07) * mm, "end": v(-2.82, -22.28) * mm});
            skLineSegment(sketch, "E950", {"start": v(-2.82, -22.28) * mm, "end": v(-2.94, -22.5) * mm});
            skLineSegment(sketch, "E951", {"start": v(-2.94, -22.5) * mm, "end": v(-3.03, -22.58) * mm});
            skLineSegment(sketch, "E952", {"start": v(-3.03, -22.58) * mm, "end": v(-3.24, -22.58) * mm});
            skLineSegment(sketch, "E953", {"start": v(-3.24, -22.58) * mm, "end": v(-3.47, -22.44) * mm});
            skLineSegment(sketch, "E954", {"start": v(-3.47, -22.44) * mm, "end": v(-3.78, -22.15) * mm});
            skLineSegment(sketch, "E955", {"start": v(-3.78, -22.15) * mm, "end": v(-4.17, -21.8) * mm});
            skLineSegment(sketch, "E956", {"start": v(-4.17, -21.8) * mm, "end": v(-4.42, -21.66) * mm});
            skLineSegment(sketch, "E957", {"start": v(-4.42, -21.66) * mm, "end": v(-4.6, -21.66) * mm});
            skLineSegment(sketch, "E958", {"start": v(-4.6, -21.66) * mm, "end": v(-4.8, -21.8) * mm});
            skLineSegment(sketch, "E959", {"start": v(-4.8, -21.8) * mm, "end": v(-4.98, -22.26) * mm});
            skLineSegment(sketch, "E960", {"start": v(-4.98, -22.26) * mm, "end": v(-5.2, -22.81) * mm});
            skLineSegment(sketch, "E961", {"start": v(-5.2, -22.81) * mm, "end": v(-5.12, -23.01) * mm});
            skLineSegment(sketch, "E962", {"start": v(-5.12, -23.01) * mm, "end": v(-4.97, -23.14) * mm});
            skLineSegment(sketch, "E963", {"start": v(-4.97, -23.14) * mm, "end": v(-4.66, -23.3) * mm});
            skLineSegment(sketch, "E964", {"start": v(-4.66, -23.3) * mm, "end": v(-3.95, -23.63) * mm});
            skLineSegment(sketch, "E965", {"start": v(-3.95, -23.63) * mm, "end": v(-3.75, -23.8) * mm});
            skLineSegment(sketch, "E966", {"start": v(-3.75, -23.8) * mm, "end": v(-3.7, -23.92) * mm});
            skLineSegment(sketch, "E967", {"start": v(-3.7, -23.92) * mm, "end": v(-3.71, -24.04) * mm});
            skLineSegment(sketch, "E968", {"start": v(-3.71, -24.04) * mm, "end": v(-3.92, -24.3) * mm});
            skLineSegment(sketch, "E969", {"start": v(-3.92, -24.3) * mm, "end": v(-4.2, -24.39) * mm});
            skLineSegment(sketch, "E970", {"start": v(-4.2, -24.39) * mm, "end": v(-4.45, -24.27) * mm});
            skLineSegment(sketch, "E971", {"start": v(-4.45, -24.27) * mm, "end": v(-4.66, -24.08) * mm});
            skLineSegment(sketch, "E972", {"start": v(-4.66, -24.08) * mm, "end": v(-5.09, -23.64) * mm});
            skLineSegment(sketch, "E973", {"start": v(-5.09, -23.64) * mm, "end": v(-5.32, -23.51) * mm});
            skLineSegment(sketch, "E974", {"start": v(-5.32, -23.51) * mm, "end": v(-5.53, -23.48) * mm});
            skLineSegment(sketch, "E975", {"start": v(-5.53, -23.48) * mm, "end": v(-5.8, -23.64) * mm});
            skLineSegment(sketch, "E976", {"start": v(-5.8, -23.64) * mm, "end": v(-6.02, -24) * mm});
            skLineSegment(sketch, "E977", {"start": v(-6.02, -24) * mm, "end": v(-6.1, -24.25) * mm});
            skLineSegment(sketch, "E978", {"start": v(-6.1, -24.25) * mm, "end": v(-6.09, -24.49) * mm});
            skLineSegment(sketch, "E979", {"start": v(-6.09, -24.49) * mm, "end": v(-5.85, -24.84) * mm});
            skLineSegment(sketch, "E980", {"start": v(-5.85, -24.84) * mm, "end": v(-5.56, -25.1) * mm});
            skLineSegment(sketch, "E981", {"start": v(-5.56, -25.1) * mm, "end": v(-5.23, -25.29) * mm});
            skLineSegment(sketch, "E982", {"start": v(-5.23, -25.29) * mm, "end": v(-4.88, -25.42) * mm});
            skLineSegment(sketch, "E983", {"start": v(-4.88, -25.42) * mm, "end": v(-4.4, -25.48) * mm});
            skLineSegment(sketch, "E984", {"start": v(-4.4, -25.48) * mm, "end": v(-3.75, -25.5) * mm});
            skLineSegment(sketch, "E985", {"start": v(-11.85, -26.16) * mm, "end": v(-10.99, -26.23) * mm});
            skLineSegment(sketch, "E986", {"start": v(-10.99, -26.23) * mm, "end": v(-10.01, -26.22) * mm});
            skLineSegment(sketch, "E987", {"start": v(-10.01, -26.22) * mm, "end": v(-9.06, -26.12) * mm});
            skLineSegment(sketch, "E988", {"start": v(-9.06, -26.12) * mm, "end": v(-8.7, -26.04) * mm});
            skLineSegment(sketch, "E989", {"start": v(-8.7, -26.04) * mm, "end": v(-8.38, -25.96) * mm});
            skLineSegment(sketch, "E990", {"start": v(-8.38, -25.96) * mm, "end": v(-8.32, -25.94) * mm});
            skLineSegment(sketch, "E991", {"start": v(-8.32, -25.94) * mm, "end": v(-8.33, -25.9) * mm});
            skLineSegment(sketch, "E992", {"start": v(-8.33, -25.9) * mm, "end": v(-8.4, -25.9) * mm});
            skLineSegment(sketch, "E993", {"start": v(-8.4, -25.9) * mm, "end": v(-8.87, -25.88) * mm});
            skLineSegment(sketch, "E994", {"start": v(-8.87, -25.88) * mm, "end": v(-9.53, -25.85) * mm});
            skLineSegment(sketch, "E995", {"start": v(-9.53, -25.85) * mm, "end": v(-9.86, -25.82) * mm});
            skLineSegment(sketch, "E996", {"start": v(-9.86, -25.82) * mm, "end": v(-10.18, -25.75) * mm});
            skLineSegment(sketch, "E997", {"start": v(-10.18, -25.75) * mm, "end": v(-10.3, -25.7) * mm});
            skLineSegment(sketch, "E998", {"start": v(-10.3, -25.7) * mm, "end": v(-10.35, -25.63) * mm});
            skLineSegment(sketch, "E999", {"start": v(-10.35, -25.63) * mm, "end": v(-10.34, -25.54) * mm});
            skLineSegment(sketch, "E1000", {"start": v(-10.34, -25.54) * mm, "end": v(-10.24, -25.38) * mm});
            skLineSegment(sketch, "E1001", {"start": v(-10.24, -25.38) * mm, "end": v(-10.06, -25.3) * mm});
            skLineSegment(sketch, "E1002", {"start": v(-10.06, -25.3) * mm, "end": v(-9.84, -25.25) * mm});
            skLineSegment(sketch, "E1003", {"start": v(-9.84, -25.25) * mm, "end": v(-9.58, -25.23) * mm});
            skLineSegment(sketch, "E1004", {"start": v(-9.58, -25.23) * mm, "end": v(-9.07, -25.26) * mm});
            skLineSegment(sketch, "E1005", {"start": v(-9.07, -25.26) * mm, "end": v(-8.5, -25.3) * mm});
            skLineSegment(sketch, "E1006", {"start": v(-8.5, -25.3) * mm, "end": v(-8.02, -25.3) * mm});
            skLineSegment(sketch, "E1007", {"start": v(-8.02, -25.3) * mm, "end": v(-7.66, -25.26) * mm});
            skLineSegment(sketch, "E1008", {"start": v(-7.66, -25.26) * mm, "end": v(-7.42, -25.15) * mm});
            skLineSegment(sketch, "E1009", {"start": v(-7.42, -25.15) * mm, "end": v(-7.24, -24.98) * mm});
            skLineSegment(sketch, "E1010", {"start": v(-7.24, -24.98) * mm, "end": v(-7.18, -24.88) * mm});
            skLineSegment(sketch, "E1011", {"start": v(-7.18, -24.88) * mm, "end": v(-7.13, -24.65) * mm});
            skLineSegment(sketch, "E1012", {"start": v(-7.13, -24.65) * mm, "end": v(-7.16, -24.55) * mm});
            skLineSegment(sketch, "E1013", {"start": v(-7.16, -24.55) * mm, "end": v(-7.3, -24.46) * mm});
            skLineSegment(sketch, "E1014", {"start": v(-7.3, -24.46) * mm, "end": v(-7.67, -24.44) * mm});
            skLineSegment(sketch, "E1015", {"start": v(-7.67, -24.44) * mm, "end": v(-8.55, -24.55) * mm});
            skLineSegment(sketch, "E1016", {"start": v(-8.55, -24.55) * mm, "end": v(-8.88, -24.57) * mm});
            skLineSegment(sketch, "E1017", {"start": v(-8.88, -24.57) * mm, "end": v(-9.05, -24.55) * mm});
            skLineSegment(sketch, "E1018", {"start": v(-9.05, -24.55) * mm, "end": v(-9.2, -24.47) * mm});
            skLineSegment(sketch, "E1019", {"start": v(-9.2, -24.47) * mm, "end": v(-9.21, -24.31) * mm});
            skLineSegment(sketch, "E1020", {"start": v(-9.21, -24.31) * mm, "end": v(-9.17, -24.18) * mm});
            skLineSegment(sketch, "E1021", {"start": v(-9.17, -24.18) * mm, "end": v(-9.03, -24.02) * mm});
            skLineSegment(sketch, "E1022", {"start": v(-9.03, -24.02) * mm, "end": v(-8.81, -23.93) * mm});
            skLineSegment(sketch, "E1023", {"start": v(-8.81, -23.93) * mm, "end": v(-8.55, -23.88) * mm});
            skLineSegment(sketch, "E1024", {"start": v(-8.55, -23.88) * mm, "end": v(-8.14, -23.87) * mm});
            skLineSegment(sketch, "E1025", {"start": v(-8.14, -23.87) * mm, "end": v(-7.3, -23.89) * mm});
            skLineSegment(sketch, "E1026", {"start": v(-7.3, -23.89) * mm, "end": v(-6.88, -23.87) * mm});
            skLineSegment(sketch, "E1027", {"start": v(-6.88, -23.87) * mm, "end": v(-6.6, -23.82) * mm});
            skLineSegment(sketch, "E1028", {"start": v(-6.6, -23.82) * mm, "end": v(-6.35, -23.72) * mm});
            skLineSegment(sketch, "E1029", {"start": v(-6.35, -23.72) * mm, "end": v(-6.15, -23.57) * mm});
            skLineSegment(sketch, "E1030", {"start": v(-6.15, -23.57) * mm, "end": v(-6.03, -23.37) * mm});
            skLineSegment(sketch, "E1031", {"start": v(-6.03, -23.37) * mm, "end": v(-6.01, -23.21) * mm});
            skLineSegment(sketch, "E1032", {"start": v(-6.01, -23.21) * mm, "end": v(-6.1, -23.12) * mm});
            skLineSegment(sketch, "E1033", {"start": v(-6.1, -23.12) * mm, "end": v(-6.34, -23.07) * mm});
            skLineSegment(sketch, "E1034", {"start": v(-6.34, -23.07) * mm, "end": v(-6.67, -23.08) * mm});
            skLineSegment(sketch, "E1035", {"start": v(-6.67, -23.08) * mm, "end": v(-7.16, -23.14) * mm});
            skLineSegment(sketch, "E1036", {"start": v(-7.16, -23.14) * mm, "end": v(-7.59, -23.2) * mm});
            skLineSegment(sketch, "E1037", {"start": v(-7.59, -23.2) * mm, "end": v(-7.96, -23.2) * mm});
            skLineSegment(sketch, "E1038", {"start": v(-7.96, -23.2) * mm, "end": v(-8.14, -23.18) * mm});
            skLineSegment(sketch, "E1039", {"start": v(-8.14, -23.18) * mm, "end": v(-8.24, -23.1) * mm});
            skLineSegment(sketch, "E1040", {"start": v(-8.24, -23.1) * mm, "end": v(-8.26, -22.99) * mm});
            skLineSegment(sketch, "E1041", {"start": v(-8.26, -22.99) * mm, "end": v(-8.16, -22.8) * mm});
            skLineSegment(sketch, "E1042", {"start": v(-8.16, -22.8) * mm, "end": v(-8.03, -22.67) * mm});
            skLineSegment(sketch, "E1043", {"start": v(-8.03, -22.67) * mm, "end": v(-7.8, -22.56) * mm});
            skLineSegment(sketch, "E1044", {"start": v(-7.8, -22.56) * mm, "end": v(-7.56, -22.5) * mm});
            skLineSegment(sketch, "E1045", {"start": v(-7.56, -22.5) * mm, "end": v(-7.25, -22.46) * mm});
            skLineSegment(sketch, "E1046", {"start": v(-7.25, -22.46) * mm, "end": v(-7.02, -22.45) * mm});
            skLineSegment(sketch, "E1047", {"start": v(-7.02, -22.45) * mm, "end": v(-6.2, -22.44) * mm});
            skLineSegment(sketch, "E1048", {"start": v(-6.2, -22.44) * mm, "end": v(-5.65, -22.35) * mm});
            skLineSegment(sketch, "E1049", {"start": v(-5.65, -22.35) * mm, "end": v(-5.38, -22.21) * mm});
            skLineSegment(sketch, "E1050", {"start": v(-5.38, -22.21) * mm, "end": v(-5.18, -21.98) * mm});
            skLineSegment(sketch, "E1051", {"start": v(-5.18, -21.98) * mm, "end": v(-5.13, -21.83) * mm});
            skLineSegment(sketch, "E1052", {"start": v(-5.13, -21.83) * mm, "end": v(-5.08, -21.5) * mm});
            skLineSegment(sketch, "E1053", {"start": v(-5.08, -21.5) * mm, "end": v(-5.25, -21.3) * mm});
            skLineSegment(sketch, "E1054", {"start": v(-5.25, -21.3) * mm, "end": v(-5.46, -21.28) * mm});
            skLineSegment(sketch, "E1055", {"start": v(-5.46, -21.28) * mm, "end": v(-5.78, -21.33) * mm});
            skLineSegment(sketch, "E1056", {"start": v(-5.78, -21.33) * mm, "end": v(-6.45, -21.5) * mm});
            skLineSegment(sketch, "E1057", {"start": v(-6.45, -21.5) * mm, "end": v(-6.81, -21.6) * mm});
            skLineSegment(sketch, "E1058", {"start": v(-6.81, -21.6) * mm, "end": v(-7.07, -21.63) * mm});
            skLineSegment(sketch, "E1059", {"start": v(-7.07, -21.63) * mm, "end": v(-7.2, -21.62) * mm});
            skLineSegment(sketch, "E1060", {"start": v(-7.2, -21.62) * mm, "end": v(-7.3, -21.55) * mm});
            skLineSegment(sketch, "E1061", {"start": v(-7.3, -21.55) * mm, "end": v(-7.32, -21.43) * mm});
            skLineSegment(sketch, "E1062", {"start": v(-7.32, -21.43) * mm, "end": v(-7.29, -21.27) * mm});
            skLineSegment(sketch, "E1063", {"start": v(-7.29, -21.27) * mm, "end": v(-7.2, -21.13) * mm});
            skLineSegment(sketch, "E1064", {"start": v(-7.2, -21.13) * mm, "end": v(-7.07, -21.04) * mm});
            skLineSegment(sketch, "E1065", {"start": v(-7.07, -21.04) * mm, "end": v(-6.79, -20.92) * mm});
            skLineSegment(sketch, "E1066", {"start": v(-6.79, -20.92) * mm, "end": v(-6.42, -20.84) * mm});
            skLineSegment(sketch, "E1067", {"start": v(-6.42, -20.84) * mm, "end": v(-5.83, -20.75) * mm});
            skLineSegment(sketch, "E1068", {"start": v(-5.83, -20.75) * mm, "end": v(-5.38, -20.67) * mm});
            skLineSegment(sketch, "E1069", {"start": v(-5.38, -20.67) * mm, "end": v(-5, -20.56) * mm});
            skLineSegment(sketch, "E1070", {"start": v(-5, -20.56) * mm, "end": v(-4.73, -20.42) * mm});
            skLineSegment(sketch, "E1071", {"start": v(-4.73, -20.42) * mm, "end": v(-4.59, -20.25) * mm});
            skLineSegment(sketch, "E1072", {"start": v(-4.59, -20.25) * mm, "end": v(-4.5, -19.99) * mm});
            skLineSegment(sketch, "E1073", {"start": v(-4.5, -19.99) * mm, "end": v(-4.47, -19.79) * mm});
            skLineSegment(sketch, "E1074", {"start": v(-4.47, -19.79) * mm, "end": v(-4.53, -19.66) * mm});
            skLineSegment(sketch, "E1075", {"start": v(-4.53, -19.66) * mm, "end": v(-4.63, -19.59) * mm});
            skLineSegment(sketch, "E1076", {"start": v(-4.63, -19.59) * mm, "end": v(-4.78, -19.56) * mm});
            skLineSegment(sketch, "E1077", {"start": v(-4.78, -19.56) * mm, "end": v(-5.04, -19.57) * mm});
            skLineSegment(sketch, "E1078", {"start": v(-5.04, -19.57) * mm, "end": v(-5.26, -19.61) * mm});
            skLineSegment(sketch, "E1079", {"start": v(-5.26, -19.61) * mm, "end": v(-6.05, -19.78) * mm});
            skLineSegment(sketch, "E1080", {"start": v(-6.05, -19.78) * mm, "end": v(-6.26, -19.8) * mm});
            skLineSegment(sketch, "E1081", {"start": v(-6.26, -19.8) * mm, "end": v(-6.44, -19.8) * mm});
            skLineSegment(sketch, "E1082", {"start": v(-6.44, -19.8) * mm, "end": v(-6.57, -19.76) * mm});
            skLineSegment(sketch, "E1083", {"start": v(-6.57, -19.76) * mm, "end": v(-6.66, -19.68) * mm});
            skLineSegment(sketch, "E1084", {"start": v(-6.66, -19.68) * mm, "end": v(-6.68, -19.53) * mm});
            skLineSegment(sketch, "E1085", {"start": v(-6.68, -19.53) * mm, "end": v(-6.67, -19.42) * mm});
            skLineSegment(sketch, "E1086", {"start": v(-6.67, -19.42) * mm, "end": v(-6.6, -19.27) * mm});
            skLineSegment(sketch, "E1087", {"start": v(-6.6, -19.27) * mm, "end": v(-6.46, -19.17) * mm});
            skLineSegment(sketch, "E1088", {"start": v(-6.46, -19.17) * mm, "end": v(-6.23, -19.09) * mm});
            skLineSegment(sketch, "E1089", {"start": v(-6.23, -19.09) * mm, "end": v(-5.94, -19.04) * mm});
            skLineSegment(sketch, "E1090", {"start": v(-5.94, -19.04) * mm, "end": v(-5.04, -18.98) * mm});
            skLineSegment(sketch, "E1091", {"start": v(-5.04, -18.98) * mm, "end": v(-4.73, -18.93) * mm});
            skLineSegment(sketch, "E1092", {"start": v(-4.73, -18.93) * mm, "end": v(-4.47, -18.83) * mm});
            skLineSegment(sketch, "E1093", {"start": v(-4.47, -18.83) * mm, "end": v(-4.26, -18.67) * mm});
            skLineSegment(sketch, "E1094", {"start": v(-4.26, -18.67) * mm, "end": v(-4.14, -18.42) * mm});
            skLineSegment(sketch, "E1095", {"start": v(-4.14, -18.42) * mm, "end": v(-4.13, -18.07) * mm});
            skLineSegment(sketch, "E1096", {"start": v(-4.13, -18.07) * mm, "end": v(-4.17, -17.9) * mm});
            skLineSegment(sketch, "E1097", {"start": v(-4.17, -17.9) * mm, "end": v(-4.29, -17.69) * mm});
            skLineSegment(sketch, "E1098", {"start": v(-4.29, -17.69) * mm, "end": v(-4.52, -17.55) * mm});
            skLineSegment(sketch, "E1099", {"start": v(-4.52, -17.55) * mm, "end": v(-4.78, -17.54) * mm});
            skLineSegment(sketch, "E1100", {"start": v(-4.78, -17.54) * mm, "end": v(-5.21, -17.67) * mm});
            skLineSegment(sketch, "E1101", {"start": v(-5.21, -17.67) * mm, "end": v(-5.65, -17.83) * mm});
            skLineSegment(sketch, "E1102", {"start": v(-5.65, -17.83) * mm, "end": v(-5.87, -17.9) * mm});
            skLineSegment(sketch, "E1103", {"start": v(-5.87, -17.9) * mm, "end": v(-6.12, -17.9) * mm});
            skLineSegment(sketch, "E1104", {"start": v(-6.12, -17.9) * mm, "end": v(-6.24, -17.8) * mm});
            skLineSegment(sketch, "E1105", {"start": v(-6.24, -17.8) * mm, "end": v(-6.27, -17.53) * mm});
            skLineSegment(sketch, "E1106", {"start": v(-6.27, -17.53) * mm, "end": v(-6.17, -17.39) * mm});
            skLineSegment(sketch, "E1107", {"start": v(-6.17, -17.39) * mm, "end": v(-5.9, -17.25) * mm});
            skLineSegment(sketch, "E1108", {"start": v(-5.9, -17.25) * mm, "end": v(-5.32, -17.1) * mm});
            skLineSegment(sketch, "E1109", {"start": v(-5.32, -17.1) * mm, "end": v(-4.57, -16.88) * mm});
            skLineSegment(sketch, "E1110", {"start": v(-4.57, -16.88) * mm, "end": v(-4.32, -16.77) * mm});
            skLineSegment(sketch, "E1111", {"start": v(-4.32, -16.77) * mm, "end": v(-4.08, -16.45) * mm});
            skLineSegment(sketch, "E1112", {"start": v(-4.08, -16.45) * mm, "end": v(-4.04, -16.1) * mm});
            skLineSegment(sketch, "E1113", {"start": v(-4.04, -16.1) * mm, "end": v(-4.13, -15.8) * mm});
            skLineSegment(sketch, "E1114", {"start": v(-4.13, -15.8) * mm, "end": v(-4.29, -15.66) * mm});
            skLineSegment(sketch, "E1115", {"start": v(-4.29, -15.66) * mm, "end": v(-4.55, -15.6) * mm});
            skLineSegment(sketch, "E1116", {"start": v(-4.55, -15.6) * mm, "end": v(-4.87, -15.65) * mm});
            skLineSegment(sketch, "E1117", {"start": v(-4.87, -15.65) * mm, "end": v(-5.33, -15.79) * mm});
            skLineSegment(sketch, "E1118", {"start": v(-5.33, -15.79) * mm, "end": v(-5.84, -15.96) * mm});
            skLineSegment(sketch, "E1119", {"start": v(-5.84, -15.96) * mm, "end": v(-6.17, -16) * mm});
            skLineSegment(sketch, "E1120", {"start": v(-6.17, -16) * mm, "end": v(-6.3, -15.92) * mm});
            skLineSegment(sketch, "E1121", {"start": v(-6.3, -15.92) * mm, "end": v(-6.35, -15.74) * mm});
            skLineSegment(sketch, "E1122", {"start": v(-6.35, -15.74) * mm, "end": v(-6.32, -15.58) * mm});
            skLineSegment(sketch, "E1123", {"start": v(-6.32, -15.58) * mm, "end": v(-6.18, -15.4) * mm});
            skLineSegment(sketch, "E1124", {"start": v(-6.18, -15.4) * mm, "end": v(-5.9, -15.27) * mm});
            skLineSegment(sketch, "E1125", {"start": v(-5.9, -15.27) * mm, "end": v(-5.46, -15.14) * mm});
            skLineSegment(sketch, "E1126", {"start": v(-5.46, -15.14) * mm, "end": v(-4.64, -14.96) * mm});
            skLineSegment(sketch, "E1127", {"start": v(-4.64, -14.96) * mm, "end": v(-4.23, -14.8) * mm});
            skLineSegment(sketch, "E1128", {"start": v(-4.23, -14.8) * mm, "end": v(-4.05, -14.62) * mm});
            skLineSegment(sketch, "E1129", {"start": v(-4.05, -14.62) * mm, "end": v(-3.98, -14.3) * mm});
            skLineSegment(sketch, "E1130", {"start": v(-3.98, -14.3) * mm, "end": v(-4.06, -13.96) * mm});
            skLineSegment(sketch, "E1131", {"start": v(-4.06, -13.96) * mm, "end": v(-4.3, -13.6) * mm});
            skLineSegment(sketch, "E1132", {"start": v(-4.3, -13.6) * mm, "end": v(-4.49, -13.5) * mm});
            skLineSegment(sketch, "E1133", {"start": v(-4.49, -13.5) * mm, "end": v(-4.8, -13.5) * mm});
            skLineSegment(sketch, "E1134", {"start": v(-4.8, -13.5) * mm, "end": v(-5.17, -13.61) * mm});
            skLineSegment(sketch, "E1135", {"start": v(-5.17, -13.61) * mm, "end": v(-5.99, -13.93) * mm});
            skLineSegment(sketch, "E1136", {"start": v(-5.99, -13.93) * mm, "end": v(-6.29, -13.97) * mm});
            skLineSegment(sketch, "E1137", {"start": v(-6.29, -13.97) * mm, "end": v(-6.53, -13.83) * mm});
            skLineSegment(sketch, "E1138", {"start": v(-6.53, -13.83) * mm, "end": v(-6.6, -13.67) * mm});
            skLineSegment(sketch, "E1139", {"start": v(-6.6, -13.67) * mm, "end": v(-6.55, -13.5) * mm});
            skLineSegment(sketch, "E1140", {"start": v(-6.55, -13.5) * mm, "end": v(-6.3, -13.32) * mm});
            skLineSegment(sketch, "E1141", {"start": v(-6.3, -13.32) * mm, "end": v(-5.89, -13.21) * mm});
            skLineSegment(sketch, "E1142", {"start": v(-5.89, -13.21) * mm, "end": v(-5.24, -13.08) * mm});
            skLineSegment(sketch, "E1143", {"start": v(-5.24, -13.08) * mm, "end": v(-4.66, -12.89) * mm});
            skLineSegment(sketch, "E1144", {"start": v(-4.66, -12.89) * mm, "end": v(-4.46, -12.73) * mm});
            skLineSegment(sketch, "E1145", {"start": v(-4.46, -12.73) * mm, "end": v(-4.37, -12.6) * mm});
            skLineSegment(sketch, "E1146", {"start": v(-4.37, -12.6) * mm, "end": v(-4.33, -12.33) * mm});
            skLineSegment(sketch, "E1147", {"start": v(-4.33, -12.33) * mm, "end": v(-4.47, -11.91) * mm});
            skLineSegment(sketch, "E1148", {"start": v(-4.47, -11.91) * mm, "end": v(-4.78, -11.63) * mm});
            skLineSegment(sketch, "E1149", {"start": v(-4.78, -11.63) * mm, "end": v(-5.27, -11.64) * mm});
            skLineSegment(sketch, "E1150", {"start": v(-5.27, -11.64) * mm, "end": v(-5.72, -11.77) * mm});
            skLineSegment(sketch, "E1151", {"start": v(-5.72, -11.77) * mm, "end": v(-6.39, -12.01) * mm});
            skLineSegment(sketch, "E1152", {"start": v(-6.39, -12.01) * mm, "end": v(-6.7, -12.07) * mm});
            skLineSegment(sketch, "E1153", {"start": v(-6.7, -12.07) * mm, "end": v(-7.01, -11.9) * mm});
            skLineSegment(sketch, "E1154", {"start": v(-7.01, -11.9) * mm, "end": v(-7.06, -11.68) * mm});
            skLineSegment(sketch, "E1155", {"start": v(-7.06, -11.68) * mm, "end": v(-6.92, -11.5) * mm});
            skLineSegment(sketch, "E1156", {"start": v(-6.92, -11.5) * mm, "end": v(-6.47, -11.31) * mm});
            skLineSegment(sketch, "E1157", {"start": v(-6.47, -11.31) * mm, "end": v(-5.37, -11.04) * mm});
            skLineSegment(sketch, "E1158", {"start": v(-5.37, -11.04) * mm, "end": v(-5, -10.85) * mm});
            skLineSegment(sketch, "E1159", {"start": v(-5, -10.85) * mm, "end": v(-4.9, -10.55) * mm});
            skLineSegment(sketch, "E1160", {"start": v(-4.9, -10.55) * mm, "end": v(-5.16, -9.87) * mm});
            skLineSegment(sketch, "E1161", {"start": v(-5.16, -9.87) * mm, "end": v(-5.47, -9.7) * mm});
            skLineSegment(sketch, "E1162", {"start": v(-5.47, -9.7) * mm, "end": v(-5.93, -9.72) * mm});
            skLineSegment(sketch, "E1163", {"start": v(-5.93, -9.72) * mm, "end": v(-6.63, -9.95) * mm});
            skLineSegment(sketch, "E1164", {"start": v(-6.63, -9.95) * mm, "end": v(-7.1, -10.12) * mm});
            skLineSegment(sketch, "E1165", {"start": v(-7.1, -10.12) * mm, "end": v(-7.44, -10.13) * mm});
            skLineSegment(sketch, "E1166", {"start": v(-7.44, -10.13) * mm, "end": v(-7.61, -10.01) * mm});
            skLineSegment(sketch, "E1167", {"start": v(-7.61, -10.01) * mm, "end": v(-7.65, -9.76) * mm});
            skLineSegment(sketch, "E1168", {"start": v(-7.65, -9.76) * mm, "end": v(-7.56, -9.64) * mm});
            skLineSegment(sketch, "E1169", {"start": v(-7.56, -9.64) * mm, "end": v(-7.2, -9.46) * mm});
            skLineSegment(sketch, "E1170", {"start": v(-7.2, -9.46) * mm, "end": v(-6.44, -9.28) * mm});
            skLineSegment(sketch, "E1171", {"start": v(-6.44, -9.28) * mm, "end": v(-5.93, -9.08) * mm});
            skLineSegment(sketch, "E1172", {"start": v(-5.93, -9.08) * mm, "end": v(-5.73, -8.85) * mm});
            skLineSegment(sketch, "E1173", {"start": v(-5.73, -8.85) * mm, "end": v(-5.73, -8.47) * mm});
            skLineSegment(sketch, "E1174", {"start": v(-5.73, -8.47) * mm, "end": v(-5.92, -8.12) * mm});
            skLineSegment(sketch, "E1175", {"start": v(-5.92, -8.12) * mm, "end": v(-6.12, -7.98) * mm});
            skLineSegment(sketch, "E1176", {"start": v(-6.12, -7.98) * mm, "end": v(-6.41, -7.93) * mm});
            skLineSegment(sketch, "E1177", {"start": v(-6.41, -7.93) * mm, "end": v(-6.95, -8.1) * mm});
            skLineSegment(sketch, "E1178", {"start": v(-6.95, -8.1) * mm, "end": v(-7.88, -8.48) * mm});
            skLineSegment(sketch, "E1179", {"start": v(-7.88, -8.48) * mm, "end": v(-8.1, -8.5) * mm});
            skLineSegment(sketch, "E1180", {"start": v(-8.1, -8.5) * mm, "end": v(-8.36, -8.4) * mm});
            skLineSegment(sketch, "E1181", {"start": v(-8.36, -8.4) * mm, "end": v(-8.48, -8.21) * mm});
            skLineSegment(sketch, "E1182", {"start": v(-8.48, -8.21) * mm, "end": v(-8.46, -8.05) * mm});
            skLineSegment(sketch, "E1183", {"start": v(-8.46, -8.05) * mm, "end": v(-8.17, -7.89) * mm});
            skLineSegment(sketch, "E1184", {"start": v(-8.17, -7.89) * mm, "end": v(-7.6, -7.67) * mm});
            skLineSegment(sketch, "E1185", {"start": v(-7.6, -7.67) * mm, "end": v(-7.07, -7.47) * mm});
            skLineSegment(sketch, "E1186", {"start": v(-7.07, -7.47) * mm, "end": v(-6.8, -7.3) * mm});
            skLineSegment(sketch, "E1187", {"start": v(-6.8, -7.3) * mm, "end": v(-6.7, -7.05) * mm});
            skLineSegment(sketch, "E1188", {"start": v(-6.7, -7.05) * mm, "end": v(-6.83, -6.68) * mm});
            skLineSegment(sketch, "E1189", {"start": v(-6.83, -6.68) * mm, "end": v(-7.07, -6.45) * mm});
            skLineSegment(sketch, "E1190", {"start": v(-7.07, -6.45) * mm, "end": v(-7.33, -6.4) * mm});
            skLineSegment(sketch, "E1191", {"start": v(-7.33, -6.4) * mm, "end": v(-7.77, -6.47) * mm});
            skLineSegment(sketch, "E1192", {"start": v(-7.77, -6.47) * mm, "end": v(-8.25, -6.66) * mm});
            skLineSegment(sketch, "E1193", {"start": v(-8.25, -6.66) * mm, "end": v(-9.1, -6.97) * mm});
            skLineSegment(sketch, "E1194", {"start": v(-9.1, -6.97) * mm, "end": v(-9.34, -7) * mm});
            skLineSegment(sketch, "E1195", {"start": v(-9.34, -7) * mm, "end": v(-9.5, -6.94) * mm});
            skLineSegment(sketch, "E1196", {"start": v(-9.5, -6.94) * mm, "end": v(-9.64, -6.76) * mm});
            skLineSegment(sketch, "E1197", {"start": v(-9.64, -6.76) * mm, "end": v(-9.56, -6.59) * mm});
            skLineSegment(sketch, "E1198", {"start": v(-9.56, -6.59) * mm, "end": v(-9.33, -6.45) * mm});
            skLineSegment(sketch, "E1199", {"start": v(-9.33, -6.45) * mm, "end": v(-8.35, -6.03) * mm});
            skLineSegment(sketch, "E1200", {"start": v(-8.35, -6.03) * mm, "end": v(-8.12, -5.75) * mm});
            skLineSegment(sketch, "E1201", {"start": v(-8.12, -5.75) * mm, "end": v(-8.2, -5.47) * mm});
            skLineSegment(sketch, "E1202", {"start": v(-8.2, -5.47) * mm, "end": v(-8.45, -5.21) * mm});
            skLineSegment(sketch, "E1203", {"start": v(-8.45, -5.21) * mm, "end": v(-8.86, -5.17) * mm});
            skLineSegment(sketch, "E1204", {"start": v(-8.86, -5.17) * mm, "end": v(-9.34, -5.35) * mm});
            skLineSegment(sketch, "E1205", {"start": v(-9.34, -5.35) * mm, "end": v(-10.35, -5.94) * mm});
            skLineSegment(sketch, "E1206", {"start": v(-10.35, -5.94) * mm, "end": v(-10.74, -5.92) * mm});
            skLineSegment(sketch, "E1207", {"start": v(-10.74, -5.92) * mm, "end": v(-10.9, -5.73) * mm});
            skLineSegment(sketch, "E1208", {"start": v(-10.9, -5.73) * mm, "end": v(-10.8, -5.52) * mm});
            skLineSegment(sketch, "E1209", {"start": v(-10.8, -5.52) * mm, "end": v(-10.46, -5.33) * mm});
            skLineSegment(sketch, "E1210", {"start": v(-10.46, -5.33) * mm, "end": v(-9.68, -4.96) * mm});
            skLineSegment(sketch, "E1211", {"start": v(-9.68, -4.96) * mm, "end": v(-9.53, -4.72) * mm});
            skLineSegment(sketch, "E1212", {"start": v(-9.53, -4.72) * mm, "end": v(-9.62, -4.44) * mm});
            skLineSegment(sketch, "E1213", {"start": v(-9.62, -4.44) * mm, "end": v(-9.92, -4.23) * mm});
            skLineSegment(sketch, "E1214", {"start": v(-9.92, -4.23) * mm, "end": v(-10.56, -4.26) * mm});
            skLineSegment(sketch, "E1215", {"start": v(-10.56, -4.26) * mm, "end": v(-11.4, -4.69) * mm});
            skLineSegment(sketch, "E1216", {"start": v(-11.4, -4.69) * mm, "end": v(-12.21, -5.15) * mm});
            skLineSegment(sketch, "E1217", {"start": v(-12.21, -5.15) * mm, "end": v(-12.5, -5.23) * mm});
            skLineSegment(sketch, "E1218", {"start": v(-12.5, -5.23) * mm, "end": v(-12.63, -5.17) * mm});
            skLineSegment(sketch, "E1219", {"start": v(-12.63, -5.17) * mm, "end": v(-12.68, -5.04) * mm});
            skLineSegment(sketch, "E1220", {"start": v(-12.68, -5.04) * mm, "end": v(-12.55, -4.82) * mm});
            skLineSegment(sketch, "E1221", {"start": v(-12.55, -4.82) * mm, "end": v(-11.7, -4.23) * mm});
            skLineSegment(sketch, "E1222", {"start": v(-11.7, -4.23) * mm, "end": v(-11.57, -4.07) * mm});
            skLineSegment(sketch, "E1223", {"start": v(-11.57, -4.07) * mm, "end": v(-11.63, -3.83) * mm});
            skLineSegment(sketch, "E1224", {"start": v(-11.63, -3.83) * mm, "end": v(-11.92, -3.63) * mm});
            skLineSegment(sketch, "E1225", {"start": v(-11.92, -3.63) * mm, "end": v(-12.32, -3.61) * mm});
            skLineSegment(sketch, "E1226", {"start": v(-12.32, -3.61) * mm, "end": v(-12.7, -3.77) * mm});
            skLineSegment(sketch, "E1227", {"start": v(-12.7, -3.77) * mm, "end": v(-13.2, -4.22) * mm});
            skLineSegment(sketch, "E1228", {"start": v(-13.2, -4.22) * mm, "end": v(-13.83, -4.78) * mm});
            skLineSegment(sketch, "E1229", {"start": v(-13.83, -4.78) * mm, "end": v(-14.11, -4.9) * mm});
            skLineSegment(sketch, "E1230", {"start": v(-14.11, -4.9) * mm, "end": v(-14.3, -4.86) * mm});
            skLineSegment(sketch, "E1231", {"start": v(-14.3, -4.86) * mm, "end": v(-14.38, -4.76) * mm});
            skLineSegment(sketch, "E1232", {"start": v(-14.38, -4.76) * mm, "end": v(-14.28, -4.53) * mm});
            skLineSegment(sketch, "E1233", {"start": v(-14.28, -4.53) * mm, "end": v(-13.6, -3.74) * mm});
            skLineSegment(sketch, "E1234", {"start": v(-13.6, -3.74) * mm, "end": v(-13.58, -3.64) * mm});
            skLineSegment(sketch, "E1235", {"start": v(-13.58, -3.64) * mm, "end": v(-13.65, -3.48) * mm});
            skLineSegment(sketch, "E1236", {"start": v(-13.65, -3.48) * mm, "end": v(-13.84, -3.42) * mm});
            skLineSegment(sketch, "E1237", {"start": v(-13.84, -3.42) * mm, "end": v(-14.23, -3.48) * mm});
            skLineSegment(sketch, "E1238", {"start": v(-14.23, -3.48) * mm, "end": v(-14.66, -3.64) * mm});
            skLineSegment(sketch, "E1239", {"start": v(-14.66, -3.64) * mm, "end": v(-15.07, -4) * mm});
            skLineSegment(sketch, "E1240", {"start": v(-15.07, -4) * mm, "end": v(-15.62, -4.6) * mm});
            skLineSegment(sketch, "E1241", {"start": v(-15.62, -4.6) * mm, "end": v(-15.85, -4.78) * mm});
            skLineSegment(sketch, "E1242", {"start": v(-15.85, -4.78) * mm, "end": v(-16.12, -4.9) * mm});
            skLineSegment(sketch, "E1243", {"start": v(-16.12, -4.9) * mm, "end": v(-16.3, -4.94) * mm});
            skLineSegment(sketch, "E1244", {"start": v(-16.3, -4.94) * mm, "end": v(-16.43, -4.92) * mm});
            skLineSegment(sketch, "E1245", {"start": v(-16.43, -4.92) * mm, "end": v(-16.47, -4.84) * mm});
            skLineSegment(sketch, "E1246", {"start": v(-16.47, -4.84) * mm, "end": v(-16.45, -4.72) * mm});
            skLineSegment(sketch, "E1247", {"start": v(-16.45, -4.72) * mm, "end": v(-16.32, -4.47) * mm});
            skLineSegment(sketch, "E1248", {"start": v(-16.32, -4.47) * mm, "end": v(-15.99, -4.02) * mm});
            skLineSegment(sketch, "E1249", {"start": v(-15.99, -4.02) * mm, "end": v(-15.9, -3.89) * mm});
            skLineSegment(sketch, "E1250", {"start": v(-15.9, -3.89) * mm, "end": v(-15.95, -3.86) * mm});
            skLineSegment(sketch, "E1251", {"start": v(-15.95, -3.86) * mm, "end": v(-16.1, -3.89) * mm});
            skLineSegment(sketch, "E1252", {"start": v(-16.1, -3.89) * mm, "end": v(-16.34, -4.03) * mm});
            skLineSegment(sketch, "E1253", {"start": v(-16.34, -4.03) * mm, "end": v(-16.6, -4.32) * mm});
            skLineSegment(sketch, "E1254", {"start": v(-16.6, -4.32) * mm, "end": v(-16.95, -4.9) * mm});
            skLineSegment(sketch, "E1255", {"start": v(-16.95, -4.9) * mm, "end": v(-17.47, -5.41) * mm});
            skLineSegment(sketch, "E1256", {"start": v(-17.47, -5.41) * mm, "end": v(-18.83, -6.44) * mm});
            skLineSegment(sketch, "E1257", {"start": v(-18.83, -6.44) * mm, "end": v(-19.34, -6.86) * mm});
            skLineSegment(sketch, "E1258", {"start": v(-19.34, -6.86) * mm, "end": v(-20.13, -7.73) * mm});
            skLineSegment(sketch, "E1259", {"start": v(-20.13, -7.73) * mm, "end": v(-20.92, -8.76) * mm});
            skLineSegment(sketch, "E1260", {"start": v(-20.92, -8.76) * mm, "end": v(-21.51, -9.67) * mm});
            skLineSegment(sketch, "E1261", {"start": v(-21.51, -9.67) * mm, "end": v(-22.28, -11.06) * mm});
            skLineSegment(sketch, "E1262", {"start": v(-22.28, -11.06) * mm, "end": v(-22.83, -12.3) * mm});
            skLineSegment(sketch, "E1263", {"start": v(-22.83, -12.3) * mm, "end": v(-23.62, -14.77) * mm});
            skLineSegment(sketch, "E1264", {"start": v(-23.62, -14.77) * mm, "end": v(-23.96, -16.83) * mm});
            skLineSegment(sketch, "E1265", {"start": v(-23.96, -16.83) * mm, "end": v(-24.02, -18.53) * mm});
            skLineSegment(sketch, "E1266", {"start": v(-24.02, -18.53) * mm, "end": v(-23.8, -20.44) * mm});
            skLineSegment(sketch, "E1267", {"start": v(-23.8, -20.44) * mm, "end": v(-23.45, -21.83) * mm});
            skLineSegment(sketch, "E1268", {"start": v(-23.45, -21.83) * mm, "end": v(-23.13, -22.59) * mm});
            skLineSegment(sketch, "E1269", {"start": v(-23.13, -22.59) * mm, "end": v(-22.41, -23.34) * mm});
            skLineSegment(sketch, "E1270", {"start": v(-22.41, -23.34) * mm, "end": v(-21.2, -23.95) * mm});
            skLineSegment(sketch, "E1271", {"start": v(-21.2, -23.95) * mm, "end": v(-19.66, -24.37) * mm});
            skLineSegment(sketch, "E1272", {"start": v(-19.66, -24.37) * mm, "end": v(-15.7, -25.34) * mm});
            skLineSegment(sketch, "E1273", {"start": v(-15.7, -25.34) * mm, "end": v(-13.6, -25.86) * mm});
            skLineSegment(sketch, "E1274", {"start": v(-13.6, -25.86) * mm, "end": v(-11.85, -26.16) * mm});
            skLineSegment(sketch, "E1275", {"start": v(22.43, 18.36) * mm, "end": v(22.64, 18.33) * mm});
            skLineSegment(sketch, "E1276", {"start": v(22.64, 18.33) * mm, "end": v(23.2, 18.4) * mm});
            skLineSegment(sketch, "E1277", {"start": v(23.2, 18.4) * mm, "end": v(24.06, 18.5) * mm});
            skLineSegment(sketch, "E1278", {"start": v(24.06, 18.5) * mm, "end": v(25.31, 18.75) * mm});
            skLineSegment(sketch, "E1279", {"start": v(25.31, 18.75) * mm, "end": v(27.1, 19.48) * mm});
            skLineSegment(sketch, "E1280", {"start": v(27.1, 19.48) * mm, "end": v(28, 19.92) * mm});
            skLineSegment(sketch, "E1281", {"start": v(28, 19.92) * mm, "end": v(28.26, 20.27) * mm});
            skLineSegment(sketch, "E1282", {"start": v(28.26, 20.27) * mm, "end": v(28.24, 20.44) * mm});
            skLineSegment(sketch, "E1283", {"start": v(28.24, 20.44) * mm, "end": v(28.1, 20.56) * mm});
            skLineSegment(sketch, "E1284", {"start": v(28.1, 20.56) * mm, "end": v(27.75, 20.63) * mm});
            skLineSegment(sketch, "E1285", {"start": v(27.75, 20.63) * mm, "end": v(27.28, 20.57) * mm});
            skLineSegment(sketch, "E1286", {"start": v(27.28, 20.57) * mm, "end": v(26.36, 20.2) * mm});
            skLineSegment(sketch, "E1287", {"start": v(26.36, 20.2) * mm, "end": v(25.27, 19.64) * mm});
            skLineSegment(sketch, "E1288", {"start": v(25.27, 19.64) * mm, "end": v(24.14, 19.05) * mm});
            skLineSegment(sketch, "E1289", {"start": v(24.14, 19.05) * mm, "end": v(23.2, 18.7) * mm});
            skLineSegment(sketch, "E1290", {"start": v(23.2, 18.7) * mm, "end": v(22.35, 18.4) * mm});
            skLineSegment(sketch, "E1291", {"start": v(22.35, 18.4) * mm, "end": v(22.43, 18.36) * mm});
            skLineSegment(sketch, "E1292", {"start": v(18.9, 15.34) * mm, "end": v(18.66, 15.2) * mm});
            skLineSegment(sketch, "E1293", {"start": v(18.66, 15.2) * mm, "end": v(18.18, 14.68) * mm});
            skLineSegment(sketch, "E1294", {"start": v(18.18, 14.68) * mm, "end": v(17.8, 14.31) * mm});
            skLineSegment(sketch, "E1295", {"start": v(17.8, 14.31) * mm, "end": v(17.39, 14.05) * mm});
            skLineSegment(sketch, "E1296", {"start": v(17.39, 14.05) * mm, "end": v(17.17, 14) * mm});
            skLineSegment(sketch, "E1297", {"start": v(17.17, 14) * mm, "end": v(16.94, 14.04) * mm});
            skLineSegment(sketch, "E1298", {"start": v(16.94, 14.04) * mm, "end": v(16.8, 14.17) * mm});
            skLineSegment(sketch, "E1299", {"start": v(16.8, 14.17) * mm, "end": v(16.85, 14.42) * mm});
            skLineSegment(sketch, "E1300", {"start": v(16.85, 14.42) * mm, "end": v(17.02, 14.59) * mm});
            skLineSegment(sketch, "E1301", {"start": v(17.02, 14.59) * mm, "end": v(17.32, 14.76) * mm});
            skLineSegment(sketch, "E1302", {"start": v(17.32, 14.76) * mm, "end": v(18.1, 15.11) * mm});
            skLineSegment(sketch, "E1303", {"start": v(18.1, 15.11) * mm, "end": v(18.6, 15.28) * mm});
            skLineSegment(sketch, "E1304", {"start": v(18.6, 15.28) * mm, "end": v(18.9, 15.34) * mm});
            skLineSegment(sketch, "E1305", {"start": v(20.4, 14.82) * mm, "end": v(20.15, 14.68) * mm});
            skLineSegment(sketch, "E1306", {"start": v(20.15, 14.68) * mm, "end": v(19.67, 14.16) * mm});
            skLineSegment(sketch, "E1307", {"start": v(19.67, 14.16) * mm, "end": v(19.3, 13.8) * mm});
            skLineSegment(sketch, "E1308", {"start": v(19.3, 13.8) * mm, "end": v(18.88, 13.53) * mm});
            skLineSegment(sketch, "E1309", {"start": v(18.88, 13.53) * mm, "end": v(18.67, 13.48) * mm});
            skLineSegment(sketch, "E1310", {"start": v(18.67, 13.48) * mm, "end": v(18.43, 13.52) * mm});
            skLineSegment(sketch, "E1311", {"start": v(18.43, 13.52) * mm, "end": v(18.29, 13.65) * mm});
            skLineSegment(sketch, "E1312", {"start": v(18.29, 13.65) * mm, "end": v(18.34, 13.9) * mm});
            skLineSegment(sketch, "E1313", {"start": v(18.34, 13.9) * mm, "end": v(18.51, 14.07) * mm});
            skLineSegment(sketch, "E1314", {"start": v(18.51, 14.07) * mm, "end": v(18.81, 14.24) * mm});
            skLineSegment(sketch, "E1315", {"start": v(18.81, 14.24) * mm, "end": v(19.6, 14.6) * mm});
            skLineSegment(sketch, "E1316", {"start": v(19.6, 14.6) * mm, "end": v(20.1, 14.76) * mm});
            skLineSegment(sketch, "E1317", {"start": v(20.1, 14.76) * mm, "end": v(20.4, 14.82) * mm});
            skLineSegment(sketch, "E1318", {"start": v(33.58, 24.9) * mm, "end": v(33.72, 24.87) * mm});
            skLineSegment(sketch, "E1319", {"start": v(33.72, 24.87) * mm, "end": v(34.19, 24.92) * mm});
            skLineSegment(sketch, "E1320", {"start": v(34.19, 24.92) * mm, "end": v(34.53, 24.98) * mm});
            skLineSegment(sketch, "E1321", {"start": v(34.53, 24.98) * mm, "end": v(34.68, 24.98) * mm});
            skLineSegment(sketch, "E1322", {"start": v(34.68, 24.98) * mm, "end": v(34.83, 24.93) * mm});
            skLineSegment(sketch, "E1323", {"start": v(34.83, 24.93) * mm, "end": v(35.43, 24.51) * mm});
            skLineSegment(sketch, "E1324", {"start": v(35.43, 24.51) * mm, "end": v(36.26, 24) * mm});
            skLineSegment(sketch, "E1325", {"start": v(36.26, 24) * mm, "end": v(36.5, 23.9) * mm});
            skLineSegment(sketch, "E1326", {"start": v(36.5, 23.9) * mm, "end": v(36.73, 23.92) * mm});
            skLineSegment(sketch, "E1327", {"start": v(36.73, 23.92) * mm, "end": v(36.82, 24.06) * mm});
            skLineSegment(sketch, "E1328", {"start": v(36.82, 24.06) * mm, "end": v(36.82, 24.32) * mm});
            skLineSegment(sketch, "E1329", {"start": v(36.82, 24.32) * mm, "end": v(36.73, 24.59) * mm});
            skLineSegment(sketch, "E1330", {"start": v(36.73, 24.59) * mm, "end": v(36.58, 24.84) * mm});
            skLineSegment(sketch, "E1331", {"start": v(36.58, 24.84) * mm, "end": v(36.28, 25.16) * mm});
            skLineSegment(sketch, "E1332", {"start": v(36.28, 25.16) * mm, "end": v(35.8, 25.54) * mm});
            skLineSegment(sketch, "E1333", {"start": v(35.8, 25.54) * mm, "end": v(34.78, 26.16) * mm});
            skLineSegment(sketch, "E1334", {"start": v(34.78, 26.16) * mm, "end": v(33.9, 26.68) * mm});
            skLineSegment(sketch, "E1335", {"start": v(33.9, 26.68) * mm, "end": v(33.31, 27.13) * mm});
            skLineSegment(sketch, "E1336", {"start": v(33.31, 27.13) * mm, "end": v(32.68, 27.89) * mm});
            skLineSegment(sketch, "E1337", {"start": v(32.68, 27.89) * mm, "end": v(32.28, 28.15) * mm});
            skLineSegment(sketch, "E1338", {"start": v(32.28, 28.15) * mm, "end": v(31.88, 28.18) * mm});
            skLineSegment(sketch, "E1339", {"start": v(31.88, 28.18) * mm, "end": v(31.38, 27.98) * mm});
            skLineSegment(sketch, "E1340", {"start": v(31.38, 27.98) * mm, "end": v(30.7, 27.6) * mm});
            skLineSegment(sketch, "E1341", {"start": v(30.7, 27.6) * mm, "end": v(30.2, 27.5) * mm});
            skLineSegment(sketch, "E1342", {"start": v(30.2, 27.5) * mm, "end": v(29.8, 27.65) * mm});
            skLineSegment(sketch, "E1343", {"start": v(29.8, 27.65) * mm, "end": v(29.62, 27.87) * mm});
            skLineSegment(sketch, "E1344", {"start": v(29.62, 27.87) * mm, "end": v(29.5, 28.14) * mm});
            skLineSegment(sketch, "E1345", {"start": v(29.5, 28.14) * mm, "end": v(29.47, 28.45) * mm});
            skLineSegment(sketch, "E1346", {"start": v(29.47, 28.45) * mm, "end": v(29.5, 29.26) * mm});
            skLineSegment(sketch, "E1347", {"start": v(29.5, 29.26) * mm, "end": v(29.46, 30.05) * mm});
            skLineSegment(sketch, "E1348", {"start": v(29.46, 30.05) * mm, "end": v(29.42, 30.18) * mm});
            skLineSegment(sketch, "E1349", {"start": v(29.42, 30.18) * mm, "end": v(29.28, 30.38) * mm});
            skLineSegment(sketch, "E1350", {"start": v(29.28, 30.38) * mm, "end": v(28.94, 30.63) * mm});
            skLineSegment(sketch, "E1351", {"start": v(28.94, 30.63) * mm, "end": v(28.46, 30.88) * mm});
            skLineSegment(sketch, "E1352", {"start": v(28.46, 30.88) * mm, "end": v(27.93, 31.08) * mm});
            skLineSegment(sketch, "E1353", {"start": v(27.93, 31.08) * mm, "end": v(27.57, 31.15) * mm});
            skLineSegment(sketch, "E1354", {"start": v(27.57, 31.15) * mm, "end": v(27.28, 31.14) * mm});
            skLineSegment(sketch, "E1355", {"start": v(27.28, 31.14) * mm, "end": v(27.14, 31.06) * mm});
            skLineSegment(sketch, "E1356", {"start": v(27.14, 31.06) * mm, "end": v(27.1, 31) * mm});
            skLineSegment(sketch, "E1357", {"start": v(27.1, 31) * mm, "end": v(27.13, 30.9) * mm});
            skLineSegment(sketch, "E1358", {"start": v(27.13, 30.9) * mm, "end": v(27.27, 30.76) * mm});
            skLineSegment(sketch, "E1359", {"start": v(27.27, 30.76) * mm, "end": v(27.89, 30.35) * mm});
            skLineSegment(sketch, "E1360", {"start": v(27.89, 30.35) * mm, "end": v(28.59, 29.9) * mm});
            skLineSegment(sketch, "E1361", {"start": v(28.59, 29.9) * mm, "end": v(28.87, 29.44) * mm});
            skLineSegment(sketch, "E1362", {"start": v(28.87, 29.44) * mm, "end": v(29.14, 28.22) * mm});
            skLineSegment(sketch, "E1363", {"start": v(29.14, 28.22) * mm, "end": v(29.22, 27.43) * mm});
            skLineSegment(sketch, "E1364", {"start": v(29.22, 27.43) * mm, "end": v(29.36, 26.57) * mm});
            skLineSegment(sketch, "E1365", {"start": v(29.36, 26.57) * mm, "end": v(29.61, 25.8) * mm});
            skLineSegment(sketch, "E1366", {"start": v(29.61, 25.8) * mm, "end": v(29.62, 25.45) * mm});
            skLineSegment(sketch, "E1367", {"start": v(29.62, 25.45) * mm, "end": v(29.47, 25.3) * mm});
            skLineSegment(sketch, "E1368", {"start": v(29.47, 25.3) * mm, "end": v(29.1, 25.22) * mm});
            skLineSegment(sketch, "E1369", {"start": v(29.1, 25.22) * mm, "end": v(28.52, 25.42) * mm});
            skLineSegment(sketch, "E1370", {"start": v(28.52, 25.42) * mm, "end": v(27.8, 25.78) * mm});
            skLineSegment(sketch, "E1371", {"start": v(27.8, 25.78) * mm, "end": v(27.4, 25.9) * mm});
            skLineSegment(sketch, "E1372", {"start": v(27.4, 25.9) * mm, "end": v(26.96, 25.84) * mm});
            skLineSegment(sketch, "E1373", {"start": v(26.96, 25.84) * mm, "end": v(25.42, 25.22) * mm});
            skLineSegment(sketch, "E1374", {"start": v(25.42, 25.22) * mm, "end": v(24.81, 24.9) * mm});
            skLineSegment(sketch, "E1375", {"start": v(24.81, 24.9) * mm, "end": v(24.66, 24.74) * mm});
            skLineSegment(sketch, "E1376", {"start": v(24.66, 24.74) * mm, "end": v(24.77, 24.6) * mm});
            skLineSegment(sketch, "E1377", {"start": v(24.77, 24.6) * mm, "end": v(25.3, 24.23) * mm});
            skLineSegment(sketch, "E1378", {"start": v(25.3, 24.23) * mm, "end": v(26.33, 23.9) * mm});
            skLineSegment(sketch, "E1379", {"start": v(26.33, 23.9) * mm, "end": v(27.38, 23.64) * mm});
            skLineSegment(sketch, "E1380", {"start": v(27.38, 23.64) * mm, "end": v(27.98, 23.4) * mm});
            skLineSegment(sketch, "E1381", {"start": v(27.98, 23.4) * mm, "end": v(28.24, 23.17) * mm});
            skLineSegment(sketch, "E1382", {"start": v(28.24, 23.17) * mm, "end": v(28.47, 22.78) * mm});
            skLineSegment(sketch, "E1383", {"start": v(28.47, 22.78) * mm, "end": v(28.76, 22.04) * mm});
            skLineSegment(sketch, "E1384", {"start": v(28.76, 22.04) * mm, "end": v(28.92, 21.78) * mm});
            skLineSegment(sketch, "E1385", {"start": v(28.92, 21.78) * mm, "end": v(29.18, 21.57) * mm});
            skLineSegment(sketch, "E1386", {"start": v(29.18, 21.57) * mm, "end": v(29.72, 21.38) * mm});
            skLineSegment(sketch, "E1387", {"start": v(29.72, 21.38) * mm, "end": v(30.3, 21.33) * mm});
            skLineSegment(sketch, "E1388", {"start": v(30.3, 21.33) * mm, "end": v(30.98, 21.41) * mm});
            skLineSegment(sketch, "E1389", {"start": v(30.98, 21.41) * mm, "end": v(32.2, 21.77) * mm});
            skLineSegment(sketch, "E1390", {"start": v(32.2, 21.77) * mm, "end": v(33.09, 22) * mm});
            skLineSegment(sketch, "E1391", {"start": v(33.09, 22) * mm, "end": v(33.64, 22.05) * mm});
            skLineSegment(sketch, "E1392", {"start": v(33.64, 22.05) * mm, "end": v(33.78, 21.97) * mm});
            skLineSegment(sketch, "E1393", {"start": v(33.78, 21.97) * mm, "end": v(33.85, 21.79) * mm});
            skLineSegment(sketch, "E1394", {"start": v(33.85, 21.79) * mm, "end": v(33.87, 21.23) * mm});
            skLineSegment(sketch, "E1395", {"start": v(33.87, 21.23) * mm, "end": v(34.01, 21.06) * mm});
            skLineSegment(sketch, "E1396", {"start": v(34.01, 21.06) * mm, "end": v(34.39, 20.95) * mm});
            skLineSegment(sketch, "E1397", {"start": v(34.39, 20.95) * mm, "end": v(34.94, 21.04) * mm});
            skLineSegment(sketch, "E1398", {"start": v(34.94, 21.04) * mm, "end": v(35.6, 21.4) * mm});
            skLineSegment(sketch, "E1399", {"start": v(35.6, 21.4) * mm, "end": v(36.22, 21.97) * mm});
            skLineSegment(sketch, "E1400", {"start": v(36.22, 21.97) * mm, "end": v(36.48, 22.41) * mm});
            skLineSegment(sketch, "E1401", {"start": v(36.48, 22.41) * mm, "end": v(36.49, 22.6) * mm});
            skLineSegment(sketch, "E1402", {"start": v(36.49, 22.6) * mm, "end": v(36.26, 22.8) * mm});
            skLineSegment(sketch, "E1403", {"start": v(36.26, 22.8) * mm, "end": v(35.86, 22.9) * mm});
            skLineSegment(sketch, "E1404", {"start": v(35.86, 22.9) * mm, "end": v(35, 22.98) * mm});
            skLineSegment(sketch, "E1405", {"start": v(35, 22.98) * mm, "end": v(34.16, 23.15) * mm});
            skLineSegment(sketch, "E1406", {"start": v(34.16, 23.15) * mm, "end": v(33.2, 23.43) * mm});
            skLineSegment(sketch, "E1407", {"start": v(33.2, 23.43) * mm, "end": v(32.57, 23.7) * mm});
            skLineSegment(sketch, "E1408", {"start": v(32.57, 23.7) * mm, "end": v(32.1, 24.01) * mm});
            skLineSegment(sketch, "E1409", {"start": v(32.1, 24.01) * mm, "end": v(31.9, 24.3) * mm});
            skLineSegment(sketch, "E1410", {"start": v(31.9, 24.3) * mm, "end": v(31.87, 24.63) * mm});
            skLineSegment(sketch, "E1411", {"start": v(31.87, 24.63) * mm, "end": v(31.99, 24.98) * mm});
            skLineSegment(sketch, "E1412", {"start": v(31.99, 24.98) * mm, "end": v(32.24, 25.37) * mm});
            skLineSegment(sketch, "E1413", {"start": v(32.24, 25.37) * mm, "end": v(32.5, 25.65) * mm});
            skLineSegment(sketch, "E1414", {"start": v(32.5, 25.65) * mm, "end": v(33.05, 26.01) * mm});
            skLineSegment(sketch, "E1415", {"start": v(33.05, 26.01) * mm, "end": v(33.54, 26.15) * mm});
            skLineSegment(sketch, "E1416", {"start": v(33.54, 26.15) * mm, "end": v(33.92, 26.13) * mm});
            skLineSegment(sketch, "E1417", {"start": v(33.92, 26.13) * mm, "end": v(34.26, 25.95) * mm});
            skLineSegment(sketch, "E1418", {"start": v(34.26, 25.95) * mm, "end": v(34.47, 25.71) * mm});
            skLineSegment(sketch, "E1419", {"start": v(34.47, 25.71) * mm, "end": v(34.44, 25.45) * mm});
            skLineSegment(sketch, "E1420", {"start": v(34.44, 25.45) * mm, "end": v(34.23, 25.24) * mm});
            skLineSegment(sketch, "E1421", {"start": v(34.23, 25.24) * mm, "end": v(33.58, 24.9) * mm});
            skLineSegment(sketch, "E1422", {"start": v(17.3, 12.28) * mm, "end": v(16.47, 13.5) * mm});
            skLineSegment(sketch, "E1423", {"start": v(16.47, 13.5) * mm, "end": v(15.52, 15.7) * mm});
            skLineSegment(sketch, "E1424", {"start": v(15.52, 15.7) * mm, "end": v(15.08, 16.87) * mm});
            skLineSegment(sketch, "E1425", {"start": v(15.08, 16.87) * mm, "end": v(15, 17.8) * mm});
            skLineSegment(sketch, "E1426", {"start": v(15, 17.8) * mm, "end": v(15.17, 19.03) * mm});
            skLineSegment(sketch, "E1427", {"start": v(15.17, 19.03) * mm, "end": v(15.5, 20.14) * mm});
            skLineSegment(sketch, "E1428", {"start": v(15.5, 20.14) * mm, "end": v(16.36, 22.26) * mm});
            skLineSegment(sketch, "E1429", {"start": v(16.36, 22.26) * mm, "end": v(17.08, 23.67) * mm});
            skLineSegment(sketch, "E1430", {"start": v(17.08, 23.67) * mm, "end": v(17.17, 24.32) * mm});
            skLineSegment(sketch, "E1431", {"start": v(17.17, 24.32) * mm, "end": v(16.65, 25) * mm});
            skLineSegment(sketch, "E1432", {"start": v(16.65, 25) * mm, "end": v(15.4, 25.77) * mm});
            skLineSegment(sketch, "E1433", {"start": v(15.4, 25.77) * mm, "end": v(14.6, 26.29) * mm});
            skLineSegment(sketch, "E1434", {"start": v(14.6, 26.29) * mm, "end": v(13.89, 27.3) * mm});
            skLineSegment(sketch, "E1435", {"start": v(13.89, 27.3) * mm, "end": v(13.26, 28.2) * mm});
            skLineSegment(sketch, "E1436", {"start": v(13.26, 28.2) * mm, "end": v(12.86, 28.52) * mm});
            skLineSegment(sketch, "E1437", {"start": v(12.86, 28.52) * mm, "end": v(12.43, 28.5) * mm});
            skLineSegment(sketch, "E1438", {"start": v(12.43, 28.5) * mm, "end": v(12.1, 28.14) * mm});
            skLineSegment(sketch, "E1439", {"start": v(12.1, 28.14) * mm, "end": v(12.05, 27.43) * mm});
            skLineSegment(sketch, "E1440", {"start": v(12.05, 27.43) * mm, "end": v(12.45, 26.04) * mm});
            skLineSegment(sketch, "E1441", {"start": v(12.45, 26.04) * mm, "end": v(13.36, 24.06) * mm});
            skLineSegment(sketch, "E1442", {"start": v(13.36, 24.06) * mm, "end": v(14.03, 22.26) * mm});
            skLineSegment(sketch, "E1443", {"start": v(14.03, 22.26) * mm, "end": v(14.52, 20.4) * mm});
            skLineSegment(sketch, "E1444", {"start": v(14.52, 20.4) * mm, "end": v(14.75, 19) * mm});
            skLineSegment(sketch, "E1445", {"start": v(14.75, 19) * mm, "end": v(14.66, 16.49) * mm});
            skLineSegment(sketch, "E1446", {"start": v(14.66, 16.49) * mm, "end": v(14.58, 15.22) * mm});
            skLineSegment(sketch, "E1447", {"start": v(14.58, 15.22) * mm, "end": v(14.7, 14.13) * mm});
            skLineSegment(sketch, "E1448", {"start": v(14.7, 14.13) * mm, "end": v(15.1, 13.34) * mm});
            skLineSegment(sketch, "E1449", {"start": v(15.1, 13.34) * mm, "end": v(15.92, 12.7) * mm});
            skLineSegment(sketch, "E1450", {"start": v(15.92, 12.7) * mm, "end": v(16.76, 12.34) * mm});
            skLineSegment(sketch, "E1451", {"start": v(16.76, 12.34) * mm, "end": v(17.3, 12.28) * mm});
            skLineSegment(sketch, "E1452", {"start": v(9.09, 34.6) * mm, "end": v(9.19, 34.44) * mm});
            skLineSegment(sketch, "E1453", {"start": v(9.19, 34.44) * mm, "end": v(10.7, 33.49) * mm});
            skLineSegment(sketch, "E1454", {"start": v(10.7, 33.49) * mm, "end": v(14.84, 30.93) * mm});
            skLineSegment(sketch, "E1455", {"start": v(14.84, 30.93) * mm, "end": v(16.89, 29.82) * mm});
            skLineSegment(sketch, "E1456", {"start": v(16.89, 29.82) * mm, "end": v(18.74, 29.25) * mm});
            skLineSegment(sketch, "E1457", {"start": v(18.74, 29.25) * mm, "end": v(20.61, 29.18) * mm});
            skLineSegment(sketch, "E1458", {"start": v(20.61, 29.18) * mm, "end": v(21.5, 29.24) * mm});
            skLineSegment(sketch, "E1459", {"start": v(21.5, 29.24) * mm, "end": v(22.97, 29.25) * mm});
            skLineSegment(sketch, "E1460", {"start": v(22.97, 29.25) * mm, "end": v(23.08, 29.29) * mm});
            skLineSegment(sketch, "E1461", {"start": v(23.08, 29.29) * mm, "end": v(23.14, 29.34) * mm});
            skLineSegment(sketch, "E1462", {"start": v(23.14, 29.34) * mm, "end": v(23.08, 29.36) * mm});
            skLineSegment(sketch, "E1463", {"start": v(23.08, 29.36) * mm, "end": v(22.61, 29.4) * mm});
            skLineSegment(sketch, "E1464", {"start": v(22.61, 29.4) * mm, "end": v(21.8, 29.5) * mm});
            skLineSegment(sketch, "E1465", {"start": v(21.8, 29.5) * mm, "end": v(20.8, 29.77) * mm});
            skLineSegment(sketch, "E1466", {"start": v(20.8, 29.77) * mm, "end": v(20.13, 30.06) * mm});
            skLineSegment(sketch, "E1467", {"start": v(20.13, 30.06) * mm, "end": v(19.74, 30.34) * mm});
            skLineSegment(sketch, "E1468", {"start": v(19.74, 30.34) * mm, "end": v(19.6, 30.59) * mm});
            skLineSegment(sketch, "E1469", {"start": v(19.6, 30.59) * mm, "end": v(19.63, 30.78) * mm});
            skLineSegment(sketch, "E1470", {"start": v(19.63, 30.78) * mm, "end": v(19.82, 30.98) * mm});
            skLineSegment(sketch, "E1471", {"start": v(19.82, 30.98) * mm, "end": v(20.14, 31.17) * mm});
            skLineSegment(sketch, "E1472", {"start": v(20.14, 31.17) * mm, "end": v(20.64, 31.34) * mm});
            skLineSegment(sketch, "E1473", {"start": v(20.64, 31.34) * mm, "end": v(21.62, 31.6) * mm});
            skLineSegment(sketch, "E1474", {"start": v(21.62, 31.6) * mm, "end": v(23.95, 32.35) * mm});
            skLineSegment(sketch, "E1475", {"start": v(23.95, 32.35) * mm, "end": v(25.2, 32.64) * mm});
            skLineSegment(sketch, "E1476", {"start": v(25.2, 32.64) * mm, "end": v(25.96, 32.71) * mm});
            skLineSegment(sketch, "E1477", {"start": v(25.96, 32.71) * mm, "end": v(27.59, 32.73) * mm});
            skLineSegment(sketch, "E1478", {"start": v(27.59, 32.73) * mm, "end": v(27.86, 32.75) * mm});
            skLineSegment(sketch, "E1479", {"start": v(27.86, 32.75) * mm, "end": v(28.18, 32.83) * mm});
            skLineSegment(sketch, "E1480", {"start": v(28.18, 32.83) * mm, "end": v(28.22, 32.89) * mm});
            skLineSegment(sketch, "E1481", {"start": v(28.22, 32.89) * mm, "end": v(27.82, 33) * mm});
            skLineSegment(sketch, "E1482", {"start": v(27.82, 33) * mm, "end": v(26.85, 33.25) * mm});
            skLineSegment(sketch, "E1483", {"start": v(26.85, 33.25) * mm, "end": v(25.39, 33.44) * mm});
            skLineSegment(sketch, "E1484", {"start": v(25.39, 33.44) * mm, "end": v(22.63, 33.83) * mm});
            skLineSegment(sketch, "E1485", {"start": v(22.63, 33.83) * mm, "end": v(20.06, 33.97) * mm});
            skLineSegment(sketch, "E1486", {"start": v(20.06, 33.97) * mm, "end": v(16.38, 34.1) * mm});
            skLineSegment(sketch, "E1487", {"start": v(16.38, 34.1) * mm, "end": v(14.25, 34.29) * mm});
            skLineSegment(sketch, "E1488", {"start": v(14.25, 34.29) * mm, "end": v(11.61, 34.66) * mm});
            skLineSegment(sketch, "E1489", {"start": v(11.61, 34.66) * mm, "end": v(10.34, 34.74) * mm});
            skLineSegment(sketch, "E1490", {"start": v(10.34, 34.74) * mm, "end": v(9.74, 34.76) * mm});
            skLineSegment(sketch, "E1491", {"start": v(9.74, 34.76) * mm, "end": v(9.44, 34.77) * mm});
            skLineSegment(sketch, "E1492", {"start": v(9.44, 34.77) * mm, "end": v(9.18, 34.74) * mm});
            skLineSegment(sketch, "E1493", {"start": v(9.18, 34.74) * mm, "end": v(9.09, 34.6) * mm});
            skLineSegment(sketch, "E1494", {"start": v(16.02, 26.92) * mm, "end": v(16.8, 26.53) * mm});
            skLineSegment(sketch, "E1495", {"start": v(16.8, 26.53) * mm, "end": v(18.22, 26.02) * mm});
            skLineSegment(sketch, "E1496", {"start": v(18.22, 26.02) * mm, "end": v(19.95, 25.6) * mm});
            skLineSegment(sketch, "E1497", {"start": v(19.95, 25.6) * mm, "end": v(20.56, 25.53) * mm});
            skLineSegment(sketch, "E1498", {"start": v(20.56, 25.53) * mm, "end": v(20.88, 25.58) * mm});
            skLineSegment(sketch, "E1499", {"start": v(20.88, 25.58) * mm, "end": v(20.96, 25.65) * mm});
            skLineSegment(sketch, "E1500", {"start": v(20.96, 25.65) * mm, "end": v(20.81, 25.92) * mm});
            skLineSegment(sketch, "E1501", {"start": v(20.81, 25.92) * mm, "end": v(20.17, 26.65) * mm});
            skLineSegment(sketch, "E1502", {"start": v(20.17, 26.65) * mm, "end": v(19.4, 27.43) * mm});
            skLineSegment(sketch, "E1503", {"start": v(19.4, 27.43) * mm, "end": v(18.88, 27.74) * mm});
            skLineSegment(sketch, "E1504", {"start": v(18.88, 27.74) * mm, "end": v(18.17, 27.93) * mm});
            skLineSegment(sketch, "E1505", {"start": v(18.17, 27.93) * mm, "end": v(16.8, 28.2) * mm});
            skLineSegment(sketch, "E1506", {"start": v(16.8, 28.2) * mm, "end": v(15.72, 28.61) * mm});
            skLineSegment(sketch, "E1507", {"start": v(15.72, 28.61) * mm, "end": v(14.5, 29.34) * mm});
            skLineSegment(sketch, "E1508", {"start": v(14.5, 29.34) * mm, "end": v(13.74, 29.87) * mm});
            skLineSegment(sketch, "E1509", {"start": v(13.74, 29.87) * mm, "end": v(13.38, 30.05) * mm});
            skLineSegment(sketch, "E1510", {"start": v(13.38, 30.05) * mm, "end": v(13.16, 30.07) * mm});
            skLineSegment(sketch, "E1511", {"start": v(13.16, 30.07) * mm, "end": v(13.03, 29.98) * mm});
            skLineSegment(sketch, "E1512", {"start": v(13.03, 29.98) * mm, "end": v(13, 29.79) * mm});
            skLineSegment(sketch, "E1513", {"start": v(13, 29.79) * mm, "end": v(13.2, 29.39) * mm});
            skLineSegment(sketch, "E1514", {"start": v(13.2, 29.39) * mm, "end": v(13.76, 28.74) * mm});
            skLineSegment(sketch, "E1515", {"start": v(13.76, 28.74) * mm, "end": v(14.68, 27.88) * mm});
            skLineSegment(sketch, "E1516", {"start": v(14.68, 27.88) * mm, "end": v(15.38, 27.33) * mm});
            skLineSegment(sketch, "E1517", {"start": v(15.38, 27.33) * mm, "end": v(16.02, 26.92) * mm});
            skLineSegment(sketch, "E1518", {"start": v(22.25, 26.71) * mm, "end": v(22.69, 26.32) * mm});
            skLineSegment(sketch, "E1519", {"start": v(22.69, 26.32) * mm, "end": v(23.15, 26.08) * mm});
            skLineSegment(sketch, "E1520", {"start": v(23.15, 26.08) * mm, "end": v(23.49, 26.08) * mm});
            skLineSegment(sketch, "E1521", {"start": v(23.49, 26.08) * mm, "end": v(23.83, 26.28) * mm});
            skLineSegment(sketch, "E1522", {"start": v(23.83, 26.28) * mm, "end": v(24.23, 26.74) * mm});
            skLineSegment(sketch, "E1523", {"start": v(24.23, 26.74) * mm, "end": v(24.52, 27.32) * mm});
            skLineSegment(sketch, "E1524", {"start": v(24.52, 27.32) * mm, "end": v(24.6, 27.66) * mm});
            skLineSegment(sketch, "E1525", {"start": v(24.6, 27.66) * mm, "end": v(24.55, 28.06) * mm});
            skLineSegment(sketch, "E1526", {"start": v(24.55, 28.06) * mm, "end": v(24.25, 28.32) * mm});
            skLineSegment(sketch, "E1527", {"start": v(24.25, 28.32) * mm, "end": v(23.75, 28.4) * mm});
            skLineSegment(sketch, "E1528", {"start": v(23.75, 28.4) * mm, "end": v(23, 28.35) * mm});
            skLineSegment(sketch, "E1529", {"start": v(23, 28.35) * mm, "end": v(22.18, 28.23) * mm});
            skLineSegment(sketch, "E1530", {"start": v(22.18, 28.23) * mm, "end": v(21.87, 28.01) * mm});
            skLineSegment(sketch, "E1531", {"start": v(21.87, 28.01) * mm, "end": v(21.79, 27.7) * mm});
            skLineSegment(sketch, "E1532", {"start": v(21.79, 27.7) * mm, "end": v(21.87, 27.3) * mm});
            skLineSegment(sketch, "E1533", {"start": v(21.87, 27.3) * mm, "end": v(22.25, 26.71) * mm});
            skLineSegment(sketch, "E1534", {"start": v(25.88, 26.77) * mm, "end": v(26.08, 27.21) * mm});
            skLineSegment(sketch, "E1535", {"start": v(26.08, 27.21) * mm, "end": v(26.1, 27.38) * mm});
            skLineSegment(sketch, "E1536", {"start": v(26.1, 27.38) * mm, "end": v(26.02, 27.52) * mm});
            skLineSegment(sketch, "E1537", {"start": v(26.02, 27.52) * mm, "end": v(25.9, 27.55) * mm});
            skLineSegment(sketch, "E1538", {"start": v(25.9, 27.55) * mm, "end": v(25.62, 27.36) * mm});
            skLineSegment(sketch, "E1539", {"start": v(25.62, 27.36) * mm, "end": v(25.4, 27.09) * mm});
            skLineSegment(sketch, "E1540", {"start": v(25.4, 27.09) * mm, "end": v(25.14, 26.58) * mm});
            skLineSegment(sketch, "E1541", {"start": v(25.14, 26.58) * mm, "end": v(25.15, 26.37) * mm});
            skLineSegment(sketch, "E1542", {"start": v(25.15, 26.37) * mm, "end": v(25.32, 26.29) * mm});
            skLineSegment(sketch, "E1543", {"start": v(25.32, 26.29) * mm, "end": v(25.56, 26.4) * mm});
            skLineSegment(sketch, "E1544", {"start": v(25.56, 26.4) * mm, "end": v(25.88, 26.77) * mm});
            skLineSegment(sketch, "E1545", {"start": v(26.59, 28.88) * mm, "end": v(26.83, 28.66) * mm});
            skLineSegment(sketch, "E1546", {"start": v(26.83, 28.66) * mm, "end": v(26.9, 28.6) * mm});
            skLineSegment(sketch, "E1547", {"start": v(26.9, 28.6) * mm, "end": v(27.02, 28.6) * mm});
            skLineSegment(sketch, "E1548", {"start": v(27.02, 28.6) * mm, "end": v(27.07, 28.7) * mm});
            skLineSegment(sketch, "E1549", {"start": v(27.07, 28.7) * mm, "end": v(27.05, 28.8) * mm});
            skLineSegment(sketch, "E1550", {"start": v(27.05, 28.8) * mm, "end": v(26.9, 29.01) * mm});
            skLineSegment(sketch, "E1551", {"start": v(26.9, 29.01) * mm, "end": v(26.63, 29.24) * mm});
            skLineSegment(sketch, "E1552", {"start": v(26.63, 29.24) * mm, "end": v(26.35, 29.38) * mm});
            skLineSegment(sketch, "E1553", {"start": v(26.35, 29.38) * mm, "end": v(26.12, 29.43) * mm});
            skLineSegment(sketch, "E1554", {"start": v(26.12, 29.43) * mm, "end": v(25.97, 29.4) * mm});
            skLineSegment(sketch, "E1555", {"start": v(25.97, 29.4) * mm, "end": v(25.9, 29.36) * mm});
            skLineSegment(sketch, "E1556", {"start": v(25.9, 29.36) * mm, "end": v(25.98, 29.37) * mm});
            skLineSegment(sketch, "E1557", {"start": v(25.98, 29.37) * mm, "end": v(26.07, 29.35) * mm});
            skLineSegment(sketch, "E1558", {"start": v(26.07, 29.35) * mm, "end": v(26.23, 29.24) * mm});
            skLineSegment(sketch, "E1559", {"start": v(26.23, 29.24) * mm, "end": v(26.59, 28.88) * mm});
            skLineSegment(sketch, "E1560", {"start": v(30.56, 30.82) * mm, "end": v(30.93, 29.95) * mm});
            skLineSegment(sketch, "E1561", {"start": v(30.93, 29.95) * mm, "end": v(31.26, 29.44) * mm});
            skLineSegment(sketch, "E1562", {"start": v(31.26, 29.44) * mm, "end": v(31.47, 29.3) * mm});
            skLineSegment(sketch, "E1563", {"start": v(31.47, 29.3) * mm, "end": v(31.65, 29.28) * mm});
            skLineSegment(sketch, "E1564", {"start": v(31.65, 29.28) * mm, "end": v(31.89, 29.43) * mm});
            skLineSegment(sketch, "E1565", {"start": v(31.89, 29.43) * mm, "end": v(32.08, 29.68) * mm});
            skLineSegment(sketch, "E1566", {"start": v(32.08, 29.68) * mm, "end": v(32.22, 30.01) * mm});
            skLineSegment(sketch, "E1567", {"start": v(32.22, 30.01) * mm, "end": v(32.25, 30.32) * mm});
            skLineSegment(sketch, "E1568", {"start": v(32.25, 30.32) * mm, "end": v(32.1, 30.72) * mm});
            skLineSegment(sketch, "E1569", {"start": v(32.1, 30.72) * mm, "end": v(31.76, 31.18) * mm});
            skLineSegment(sketch, "E1570", {"start": v(31.76, 31.18) * mm, "end": v(31.3, 31.56) * mm});
            skLineSegment(sketch, "E1571", {"start": v(31.3, 31.56) * mm, "end": v(30.78, 31.9) * mm});
            skLineSegment(sketch, "E1572", {"start": v(30.78, 31.9) * mm, "end": v(30.37, 32.1) * mm});
            skLineSegment(sketch, "E1573", {"start": v(30.37, 32.1) * mm, "end": v(30.1, 32.2) * mm});
            skLineSegment(sketch, "E1574", {"start": v(30.1, 32.2) * mm, "end": v(29.9, 32.22) * mm});
            skLineSegment(sketch, "E1575", {"start": v(29.9, 32.22) * mm, "end": v(29.85, 32.08) * mm});
            skLineSegment(sketch, "E1576", {"start": v(29.85, 32.08) * mm, "end": v(29.93, 31.86) * mm});
            skLineSegment(sketch, "E1577", {"start": v(29.93, 31.86) * mm, "end": v(30.28, 31.37) * mm});
            skLineSegment(sketch, "E1578", {"start": v(30.28, 31.37) * mm, "end": v(30.56, 30.82) * mm});
            skLineSegment(sketch, "E1579", {"start": v(12.67, 36.26) * mm, "end": v(14.14, 36.17) * mm});
            skLineSegment(sketch, "E1580", {"start": v(14.14, 36.17) * mm, "end": v(15.22, 36.04) * mm});
            skLineSegment(sketch, "E1581", {"start": v(15.22, 36.04) * mm, "end": v(16.17, 35.78) * mm});
            skLineSegment(sketch, "E1582", {"start": v(16.17, 35.78) * mm, "end": v(17.45, 35.59) * mm});
            skLineSegment(sketch, "E1583", {"start": v(17.45, 35.59) * mm, "end": v(18.28, 35.54) * mm});
            skLineSegment(sketch, "E1584", {"start": v(18.28, 35.54) * mm, "end": v(18.93, 35.61) * mm});
            skLineSegment(sketch, "E1585", {"start": v(18.93, 35.61) * mm, "end": v(19.1, 35.7) * mm});
            skLineSegment(sketch, "E1586", {"start": v(19.1, 35.7) * mm, "end": v(19.04, 35.92) * mm});
            skLineSegment(sketch, "E1587", {"start": v(19.04, 35.92) * mm, "end": v(18.39, 36.37) * mm});
            skLineSegment(sketch, "E1588", {"start": v(18.39, 36.37) * mm, "end": v(17.28, 37) * mm});
            skLineSegment(sketch, "E1589", {"start": v(17.28, 37) * mm, "end": v(16, 37.47) * mm});
            skLineSegment(sketch, "E1590", {"start": v(16, 37.47) * mm, "end": v(14.77, 37.73) * mm});
            skLineSegment(sketch, "E1591", {"start": v(14.77, 37.73) * mm, "end": v(13.1, 37.89) * mm});
            skLineSegment(sketch, "E1592", {"start": v(13.1, 37.89) * mm, "end": v(12.19, 37.9) * mm});
            skLineSegment(sketch, "E1593", {"start": v(12.19, 37.9) * mm, "end": v(10.92, 37.83) * mm});
            skLineSegment(sketch, "E1594", {"start": v(10.92, 37.83) * mm, "end": v(9.5, 37.66) * mm});
            skLineSegment(sketch, "E1595", {"start": v(9.5, 37.66) * mm, "end": v(8.8, 37.51) * mm});
            skLineSegment(sketch, "E1596", {"start": v(8.8, 37.51) * mm, "end": v(8.3, 37.3) * mm});
            skLineSegment(sketch, "E1597", {"start": v(8.3, 37.3) * mm, "end": v(8.11, 37.1) * mm});
            skLineSegment(sketch, "E1598", {"start": v(8.11, 37.1) * mm, "end": v(8.15, 36.96) * mm});
            skLineSegment(sketch, "E1599", {"start": v(8.15, 36.96) * mm, "end": v(8.32, 36.85) * mm});
            skLineSegment(sketch, "E1600", {"start": v(8.32, 36.85) * mm, "end": v(9.04, 36.7) * mm});
            skLineSegment(sketch, "E1601", {"start": v(9.04, 36.7) * mm, "end": v(9.96, 36.6) * mm});
            skLineSegment(sketch, "E1602", {"start": v(9.96, 36.6) * mm, "end": v(10.96, 36.43) * mm});
            skLineSegment(sketch, "E1603", {"start": v(10.96, 36.43) * mm, "end": v(11.78, 36.33) * mm});
            skLineSegment(sketch, "E1604", {"start": v(11.78, 36.33) * mm, "end": v(12.67, 36.26) * mm});
            skLineSegment(sketch, "E1605", {"start": v(-7.5, 37.74) * mm, "end": v(-7.27, 37.84) * mm});
            skLineSegment(sketch, "E1606", {"start": v(-7.27, 37.84) * mm, "end": v(-6.33, 37.89) * mm});
            skLineSegment(sketch, "E1607", {"start": v(-6.33, 37.89) * mm, "end": v(-4.98, 37.79) * mm});
            skLineSegment(sketch, "E1608", {"start": v(-4.98, 37.79) * mm, "end": v(-3.91, 37.74) * mm});
            skLineSegment(sketch, "E1609", {"start": v(-3.91, 37.74) * mm, "end": v(-2.43, 37.5) * mm});
            skLineSegment(sketch, "E1610", {"start": v(-2.43, 37.5) * mm, "end": v(-0.62, 37) * mm});
            skLineSegment(sketch, "E1611", {"start": v(-0.62, 37) * mm, "end": v(1.87, 36.1) * mm});
            skLineSegment(sketch, "E1612", {"start": v(1.87, 36.1) * mm, "end": v(4.1, 35.31) * mm});
            skLineSegment(sketch, "E1613", {"start": v(4.1, 35.31) * mm, "end": v(5.32, 34.73) * mm});
            skLineSegment(sketch, "E1614", {"start": v(5.32, 34.73) * mm, "end": v(6.3, 34.2) * mm});
            skLineSegment(sketch, "E1615", {"start": v(6.3, 34.2) * mm, "end": v(6.67, 34.02) * mm});
            skLineSegment(sketch, "E1616", {"start": v(6.67, 34.02) * mm, "end": v(6.7, 33.9) * mm});
            skLineSegment(sketch, "E1617", {"start": v(6.7, 33.9) * mm, "end": v(6.6, 33.88) * mm});
            skLineSegment(sketch, "E1618", {"start": v(6.6, 33.88) * mm, "end": v(6.37, 33.91) * mm});
            skLineSegment(sketch, "E1619", {"start": v(6.37, 33.91) * mm, "end": v(6.18, 34) * mm});
            skLineSegment(sketch, "E1620", {"start": v(6.18, 34) * mm, "end": v(5.8, 34.2) * mm});
            skLineSegment(sketch, "E1621", {"start": v(5.8, 34.2) * mm, "end": v(5.4, 34.4) * mm});
            skLineSegment(sketch, "E1622", {"start": v(5.4, 34.4) * mm, "end": v(4.55, 34.75) * mm});
            skLineSegment(sketch, "E1623", {"start": v(4.55, 34.75) * mm, "end": v(3.57, 35.16) * mm});
            skLineSegment(sketch, "E1624", {"start": v(3.57, 35.16) * mm, "end": v(2.28, 35.7) * mm});
            skLineSegment(sketch, "E1625", {"start": v(2.28, 35.7) * mm, "end": v(0.53, 36.16) * mm});
            skLineSegment(sketch, "E1626", {"start": v(0.53, 36.16) * mm, "end": v(-1.41, 36.76) * mm});
            skLineSegment(sketch, "E1627", {"start": v(-1.41, 36.76) * mm, "end": v(-2.76, 37.11) * mm});
            skLineSegment(sketch, "E1628", {"start": v(-2.76, 37.11) * mm, "end": v(-3.76, 37.3) * mm});
            skLineSegment(sketch, "E1629", {"start": v(-3.76, 37.3) * mm, "end": v(-5.23, 37.4) * mm});
            skLineSegment(sketch, "E1630", {"start": v(-5.23, 37.4) * mm, "end": v(-6, 37.55) * mm});
            skLineSegment(sketch, "E1631", {"start": v(-6, 37.55) * mm, "end": v(-6.8, 37.71) * mm});
            skLineSegment(sketch, "E1632", {"start": v(-6.8, 37.71) * mm, "end": v(-7.2, 37.77) * mm});
            skLineSegment(sketch, "E1633", {"start": v(-7.2, 37.77) * mm, "end": v(-7.5, 37.74) * mm});
            skLineSegment(sketch, "E1634", {"start": v(-15.45, 18.98) * mm, "end": v(-5.31, 10.2) * mm});
            skLineSegment(sketch, "E1635", {"start": v(-5.31, 10.2) * mm, "end": v(-2.8, 7.95) * mm});
            skLineSegment(sketch, "E1636", {"start": v(-2.8, 7.95) * mm, "end": v(-2.13, 7.57) * mm});
            skLineSegment(sketch, "E1637", {"start": v(-2.13, 7.57) * mm, "end": v(-1.55, 7.62) * mm});
            skLineSegment(sketch, "E1638", {"start": v(-1.55, 7.62) * mm, "end": v(-1.44, 7.77) * mm});
            skLineSegment(sketch, "E1639", {"start": v(-1.44, 7.77) * mm, "end": v(-1.53, 8.05) * mm});
            skLineSegment(sketch, "E1640", {"start": v(-1.53, 8.05) * mm, "end": v(-2.07, 8.7) * mm});
            skLineSegment(sketch, "E1641", {"start": v(-2.07, 8.7) * mm, "end": v(-3.1, 9.75) * mm});
            skLineSegment(sketch, "E1642", {"start": v(-3.1, 9.75) * mm, "end": v(-3.65, 10.47) * mm});
            skLineSegment(sketch, "E1643", {"start": v(-3.65, 10.47) * mm, "end": v(-3.82, 10.87) * mm});
            skLineSegment(sketch, "E1644", {"start": v(-3.82, 10.87) * mm, "end": v(-3.8, 11.33) * mm});
            skLineSegment(sketch, "E1645", {"start": v(-3.8, 11.33) * mm, "end": v(-3.65, 11.8) * mm});
            skLineSegment(sketch, "E1646", {"start": v(-3.65, 11.8) * mm, "end": v(-3.5, 12.55) * mm});
            skLineSegment(sketch, "E1647", {"start": v(-3.5, 12.55) * mm, "end": v(-3.51, 13.32) * mm});
            skLineSegment(sketch, "E1648", {"start": v(-3.51, 13.32) * mm, "end": v(-3.56, 13.55) * mm});
            skLineSegment(sketch, "E1649", {"start": v(-3.56, 13.55) * mm, "end": v(-3.62, 13.65) * mm});
            skLineSegment(sketch, "E1650", {"start": v(-3.62, 13.65) * mm, "end": v(-3.71, 13.6) * mm});
            skLineSegment(sketch, "E1651", {"start": v(-3.71, 13.6) * mm, "end": v(-3.84, 13.3) * mm});
            skLineSegment(sketch, "E1652", {"start": v(-3.84, 13.3) * mm, "end": v(-4.14, 12.5) * mm});
            skLineSegment(sketch, "E1653", {"start": v(-4.14, 12.5) * mm, "end": v(-4.27, 12.34) * mm});
            skLineSegment(sketch, "E1654", {"start": v(-4.27, 12.34) * mm, "end": v(-4.4, 12.28) * mm});
            skLineSegment(sketch, "E1655", {"start": v(-4.4, 12.28) * mm, "end": v(-4.62, 12.23) * mm});
            skLineSegment(sketch, "E1656", {"start": v(-4.62, 12.23) * mm, "end": v(-4.85, 12.33) * mm});
            skLineSegment(sketch, "E1657", {"start": v(-4.85, 12.33) * mm, "end": v(-4.92, 12.46) * mm});
            skLineSegment(sketch, "E1658", {"start": v(-4.92, 12.46) * mm, "end": v(-4.94, 12.63) * mm});
            skLineSegment(sketch, "E1659", {"start": v(-4.94, 12.63) * mm, "end": v(-4.87, 13.04) * mm});
            skLineSegment(sketch, "E1660", {"start": v(-4.87, 13.04) * mm, "end": v(-4.67, 13.71) * mm});
            skLineSegment(sketch, "E1661", {"start": v(-4.67, 13.71) * mm, "end": v(-4.57, 14.1) * mm});
            skLineSegment(sketch, "E1662", {"start": v(-4.57, 14.1) * mm, "end": v(-4.56, 14.24) * mm});
            skLineSegment(sketch, "E1663", {"start": v(-4.56, 14.24) * mm, "end": v(-4.57, 14.29) * mm});
            skLineSegment(sketch, "E1664", {"start": v(-4.57, 14.29) * mm, "end": v(-4.62, 14.35) * mm});
            skLineSegment(sketch, "E1665", {"start": v(-4.62, 14.35) * mm, "end": v(-4.69, 14.34) * mm});
            skLineSegment(sketch, "E1666", {"start": v(-4.69, 14.34) * mm, "end": v(-4.9, 14.15) * mm});
            skLineSegment(sketch, "E1667", {"start": v(-4.9, 14.15) * mm, "end": v(-5.26, 13.78) * mm});
            skLineSegment(sketch, "E1668", {"start": v(-5.26, 13.78) * mm, "end": v(-5.4, 13.65) * mm});
            skLineSegment(sketch, "E1669", {"start": v(-5.4, 13.65) * mm, "end": v(-5.59, 13.53) * mm});
            skLineSegment(sketch, "E1670", {"start": v(-5.59, 13.53) * mm, "end": v(-5.77, 13.5) * mm});
            skLineSegment(sketch, "E1671", {"start": v(-5.77, 13.5) * mm, "end": v(-5.98, 13.6) * mm});
            skLineSegment(sketch, "E1672", {"start": v(-5.98, 13.6) * mm, "end": v(-6.03, 13.71) * mm});
            skLineSegment(sketch, "E1673", {"start": v(-6.03, 13.71) * mm, "end": v(-6, 13.95) * mm});
            skLineSegment(sketch, "E1674", {"start": v(-6, 13.95) * mm, "end": v(-5.83, 14.36) * mm});
            skLineSegment(sketch, "E1675", {"start": v(-5.83, 14.36) * mm, "end": v(-5.52, 15.02) * mm});
            skLineSegment(sketch, "E1676", {"start": v(-5.52, 15.02) * mm, "end": v(-5.51, 15.2) * mm});
            skLineSegment(sketch, "E1677", {"start": v(-5.51, 15.2) * mm, "end": v(-5.57, 15.25) * mm});
            skLineSegment(sketch, "E1678", {"start": v(-5.57, 15.25) * mm, "end": v(-5.69, 15.25) * mm});
            skLineSegment(sketch, "E1679", {"start": v(-5.69, 15.25) * mm, "end": v(-5.87, 15.16) * mm});
            skLineSegment(sketch, "E1680", {"start": v(-5.87, 15.16) * mm, "end": v(-6.4, 14.75) * mm});
            skLineSegment(sketch, "E1681", {"start": v(-6.4, 14.75) * mm, "end": v(-6.55, 14.68) * mm});
            skLineSegment(sketch, "E1682", {"start": v(-6.55, 14.68) * mm, "end": v(-6.73, 14.75) * mm});
            skLineSegment(sketch, "E1683", {"start": v(-6.73, 14.75) * mm, "end": v(-6.83, 14.9) * mm});
            skLineSegment(sketch, "E1684", {"start": v(-6.83, 14.9) * mm, "end": v(-6.83, 15.11) * mm});
            skLineSegment(sketch, "E1685", {"start": v(-6.83, 15.11) * mm, "end": v(-6.76, 15.33) * mm});
            skLineSegment(sketch, "E1686", {"start": v(-6.76, 15.33) * mm, "end": v(-6.55, 15.67) * mm});
            skLineSegment(sketch, "E1687", {"start": v(-6.55, 15.67) * mm, "end": v(-5.96, 16.45) * mm});
            skLineSegment(sketch, "E1688", {"start": v(-5.96, 16.45) * mm, "end": v(-5.73, 16.9) * mm});
            skLineSegment(sketch, "E1689", {"start": v(-5.73, 16.9) * mm, "end": v(-5.72, 17) * mm});
            skLineSegment(sketch, "E1690", {"start": v(-5.72, 17) * mm, "end": v(-5.79, 17.04) * mm});
            skLineSegment(sketch, "E1691", {"start": v(-5.79, 17.04) * mm, "end": v(-5.95, 16.96) * mm});
            skLineSegment(sketch, "E1692", {"start": v(-5.95, 16.96) * mm, "end": v(-6.5, 16.5) * mm});
            skLineSegment(sketch, "E1693", {"start": v(-6.5, 16.5) * mm, "end": v(-7.04, 16.07) * mm});
            skLineSegment(sketch, "E1694", {"start": v(-7.04, 16.07) * mm, "end": v(-7.26, 15.95) * mm});
            skLineSegment(sketch, "E1695", {"start": v(-7.26, 15.95) * mm, "end": v(-7.5, 15.92) * mm});
            skLineSegment(sketch, "E1696", {"start": v(-7.5, 15.92) * mm, "end": v(-7.63, 16) * mm});
            skLineSegment(sketch, "E1697", {"start": v(-7.63, 16) * mm, "end": v(-7.7, 16.24) * mm});
            skLineSegment(sketch, "E1698", {"start": v(-7.7, 16.24) * mm, "end": v(-7.62, 16.42) * mm});
            skLineSegment(sketch, "E1699", {"start": v(-7.62, 16.42) * mm, "end": v(-7.46, 16.63) * mm});
            skLineSegment(sketch, "E1700", {"start": v(-7.46, 16.63) * mm, "end": v(-7.1, 16.97) * mm});
            skLineSegment(sketch, "E1701", {"start": v(-7.1, 16.97) * mm, "end": v(-6.5, 17.49) * mm});
            skLineSegment(sketch, "E1702", {"start": v(-6.5, 17.49) * mm, "end": v(-6.3, 17.71) * mm});
            skLineSegment(sketch, "E1703", {"start": v(-6.3, 17.71) * mm, "end": v(-6.17, 17.92) * mm});
            skLineSegment(sketch, "E1704", {"start": v(-6.17, 17.92) * mm, "end": v(-6.21, 18.06) * mm});
            skLineSegment(sketch, "E1705", {"start": v(-6.21, 18.06) * mm, "end": v(-6.29, 18.1) * mm});
            skLineSegment(sketch, "E1706", {"start": v(-6.29, 18.1) * mm, "end": v(-6.46, 18.08) * mm});
            skLineSegment(sketch, "E1707", {"start": v(-6.46, 18.08) * mm, "end": v(-6.82, 17.91) * mm});
            skLineSegment(sketch, "E1708", {"start": v(-6.82, 17.91) * mm, "end": v(-7.58, 17.5) * mm});
            skLineSegment(sketch, "E1709", {"start": v(-7.58, 17.5) * mm, "end": v(-8.04, 17.29) * mm});
            skLineSegment(sketch, "E1710", {"start": v(-8.04, 17.29) * mm, "end": v(-8.33, 17.22) * mm});
            skLineSegment(sketch, "E1711", {"start": v(-8.33, 17.22) * mm, "end": v(-8.47, 17.24) * mm});
            skLineSegment(sketch, "E1712", {"start": v(-8.47, 17.24) * mm, "end": v(-8.6, 17.33) * mm});
            skLineSegment(sketch, "E1713", {"start": v(-8.6, 17.33) * mm, "end": v(-8.66, 17.48) * mm});
            skLineSegment(sketch, "E1714", {"start": v(-8.66, 17.48) * mm, "end": v(-8.63, 17.69) * mm});
            skLineSegment(sketch, "E1715", {"start": v(-8.63, 17.69) * mm, "end": v(-8.45, 17.87) * mm});
            skLineSegment(sketch, "E1716", {"start": v(-8.45, 17.87) * mm, "end": v(-8.22, 18.03) * mm});
            skLineSegment(sketch, "E1717", {"start": v(-8.22, 18.03) * mm, "end": v(-7.69, 18.29) * mm});
            skLineSegment(sketch, "E1718", {"start": v(-7.69, 18.29) * mm, "end": v(-6.95, 18.63) * mm});
            skLineSegment(sketch, "E1719", {"start": v(-6.95, 18.63) * mm, "end": v(-6.72, 18.79) * mm});
            skLineSegment(sketch, "E1720", {"start": v(-6.72, 18.79) * mm, "end": v(-6.6, 18.94) * mm});
            skLineSegment(sketch, "E1721", {"start": v(-6.6, 18.94) * mm, "end": v(-6.61, 19.03) * mm});
            skLineSegment(sketch, "E1722", {"start": v(-6.61, 19.03) * mm, "end": v(-6.68, 19.11) * mm});
            skLineSegment(sketch, "E1723", {"start": v(-6.68, 19.11) * mm, "end": v(-6.84, 19.17) * mm});
            skLineSegment(sketch, "E1724", {"start": v(-6.84, 19.17) * mm, "end": v(-6.98, 19.16) * mm});
            skLineSegment(sketch, "E1725", {"start": v(-6.98, 19.16) * mm, "end": v(-7.14, 19.13) * mm});
            skLineSegment(sketch, "E1726", {"start": v(-7.14, 19.13) * mm, "end": v(-7.52, 19.01) * mm});
            skLineSegment(sketch, "E1727", {"start": v(-7.52, 19.01) * mm, "end": v(-8.12, 18.8) * mm});
            skLineSegment(sketch, "E1728", {"start": v(-8.12, 18.8) * mm, "end": v(-8.48, 18.68) * mm});
            skLineSegment(sketch, "E1729", {"start": v(-8.48, 18.68) * mm, "end": v(-8.78, 18.62) * mm});
            skLineSegment(sketch, "E1730", {"start": v(-8.78, 18.62) * mm, "end": v(-9.05, 18.6) * mm});
            skLineSegment(sketch, "E1731", {"start": v(-9.05, 18.6) * mm, "end": v(-9.33, 18.71) * mm});
            skLineSegment(sketch, "E1732", {"start": v(-9.33, 18.71) * mm, "end": v(-9.46, 18.9) * mm});
            skLineSegment(sketch, "E1733", {"start": v(-9.46, 18.9) * mm, "end": v(-9.5, 19.04) * mm});
            skLineSegment(sketch, "E1734", {"start": v(-9.5, 19.04) * mm, "end": v(-9.44, 19.2) * mm});
            skLineSegment(sketch, "E1735", {"start": v(-9.44, 19.2) * mm, "end": v(-9.28, 19.32) * mm});
            skLineSegment(sketch, "E1736", {"start": v(-9.28, 19.32) * mm, "end": v(-9.06, 19.4) * mm});
            skLineSegment(sketch, "E1737", {"start": v(-9.06, 19.4) * mm, "end": v(-8.67, 19.49) * mm});
            skLineSegment(sketch, "E1738", {"start": v(-8.67, 19.49) * mm, "end": v(-7.83, 19.62) * mm});
            skLineSegment(sketch, "E1739", {"start": v(-7.83, 19.62) * mm, "end": v(-7.35, 19.77) * mm});
            skLineSegment(sketch, "E1740", {"start": v(-7.35, 19.77) * mm, "end": v(-7.16, 19.89) * mm});
            skLineSegment(sketch, "E1741", {"start": v(-7.16, 19.89) * mm, "end": v(-7.09, 20.06) * mm});
            skLineSegment(sketch, "E1742", {"start": v(-7.09, 20.06) * mm, "end": v(-7.12, 20.25) * mm});
            skLineSegment(sketch, "E1743", {"start": v(-7.12, 20.25) * mm, "end": v(-7.3, 20.35) * mm});
            skLineSegment(sketch, "E1744", {"start": v(-7.3, 20.35) * mm, "end": v(-7.7, 20.39) * mm});
            skLineSegment(sketch, "E1745", {"start": v(-7.7, 20.39) * mm, "end": v(-8.55, 20.34) * mm});
            skLineSegment(sketch, "E1746", {"start": v(-8.55, 20.34) * mm, "end": v(-8.98, 20.34) * mm});
            skLineSegment(sketch, "E1747", {"start": v(-8.98, 20.34) * mm, "end": v(-9.57, 20.4) * mm});
            skLineSegment(sketch, "E1748", {"start": v(-9.57, 20.4) * mm, "end": v(-9.91, 20.54) * mm});
            skLineSegment(sketch, "E1749", {"start": v(-9.91, 20.54) * mm, "end": v(-10.1, 20.71) * mm});
            skLineSegment(sketch, "E1750", {"start": v(-10.1, 20.71) * mm, "end": v(-10.16, 20.9) * mm});
            skLineSegment(sketch, "E1751", {"start": v(-10.16, 20.9) * mm, "end": v(-10.1, 21.11) * mm});
            skLineSegment(sketch, "E1752", {"start": v(-10.1, 21.11) * mm, "end": v(-9.97, 21.18) * mm});
            skLineSegment(sketch, "E1753", {"start": v(-9.97, 21.18) * mm, "end": v(-9.81, 21.2) * mm});
            skLineSegment(sketch, "E1754", {"start": v(-9.81, 21.2) * mm, "end": v(-9.53, 21.21) * mm});
            skLineSegment(sketch, "E1755", {"start": v(-9.53, 21.21) * mm, "end": v(-9.26, 21.2) * mm});
            skLineSegment(sketch, "E1756", {"start": v(-9.26, 21.2) * mm, "end": v(-8.56, 21.1) * mm});
            skLineSegment(sketch, "E1757", {"start": v(-8.56, 21.1) * mm, "end": v(-8.1, 21.04) * mm});
            skLineSegment(sketch, "E1758", {"start": v(-8.1, 21.04) * mm, "end": v(-7.96, 21.04) * mm});
            skLineSegment(sketch, "E1759", {"start": v(-7.96, 21.04) * mm, "end": v(-7.77, 21.06) * mm});
            skLineSegment(sketch, "E1760", {"start": v(-7.77, 21.06) * mm, "end": v(-7.43, 21.17) * mm});
            skLineSegment(sketch, "E1761", {"start": v(-7.43, 21.17) * mm, "end": v(-7.31, 21.32) * mm});
            skLineSegment(sketch, "E1762", {"start": v(-7.31, 21.32) * mm, "end": v(-7.32, 21.47) * mm});
            skLineSegment(sketch, "E1763", {"start": v(-7.32, 21.47) * mm, "end": v(-7.38, 21.55) * mm});
            skLineSegment(sketch, "E1764", {"start": v(-7.38, 21.55) * mm, "end": v(-7.62, 21.69) * mm});
            skLineSegment(sketch, "E1765", {"start": v(-7.62, 21.69) * mm, "end": v(-8.14, 21.88) * mm});
            skLineSegment(sketch, "E1766", {"start": v(-8.14, 21.88) * mm, "end": v(-8.67, 22) * mm});
            skLineSegment(sketch, "E1767", {"start": v(-8.67, 22) * mm, "end": v(-9.17, 22.1) * mm});
            skLineSegment(sketch, "E1768", {"start": v(-9.17, 22.1) * mm, "end": v(-9.5, 22.12) * mm});
            skLineSegment(sketch, "E1769", {"start": v(-9.5, 22.12) * mm, "end": v(-9.68, 22.1) * mm});
            skLineSegment(sketch, "E1770", {"start": v(-9.68, 22.1) * mm, "end": v(-9.94, 21.95) * mm});
            skLineSegment(sketch, "E1771", {"start": v(-9.94, 21.95) * mm, "end": v(-10.17, 21.86) * mm});
            skLineSegment(sketch, "E1772", {"start": v(-10.17, 21.86) * mm, "end": v(-10.4, 21.93) * mm});
            skLineSegment(sketch, "E1773", {"start": v(-10.4, 21.93) * mm, "end": v(-10.54, 22.08) * mm});
            skLineSegment(sketch, "E1774", {"start": v(-10.54, 22.08) * mm, "end": v(-10.66, 22.28) * mm});
            skLineSegment(sketch, "E1775", {"start": v(-10.66, 22.28) * mm, "end": v(-10.78, 22.68) * mm});
            skLineSegment(sketch, "E1776", {"start": v(-10.78, 22.68) * mm, "end": v(-10.85, 23.26) * mm});
            skLineSegment(sketch, "E1777", {"start": v(-10.85, 23.26) * mm, "end": v(-10.85, 24.23) * mm});
            skLineSegment(sketch, "E1778", {"start": v(-10.85, 24.23) * mm, "end": v(-10.73, 25.35) * mm});
            skLineSegment(sketch, "E1779", {"start": v(-10.73, 25.35) * mm, "end": v(-10.41, 26.56) * mm});
            skLineSegment(sketch, "E1780", {"start": v(-10.41, 26.56) * mm, "end": v(-9.68, 28.05) * mm});
            skLineSegment(sketch, "E1781", {"start": v(-9.68, 28.05) * mm, "end": v(-8.63, 29.33) * mm});
            skLineSegment(sketch, "E1782", {"start": v(-8.63, 29.33) * mm, "end": v(-6.98, 30.64) * mm});
            skLineSegment(sketch, "E1783", {"start": v(-6.98, 30.64) * mm, "end": v(-6, 31.06) * mm});
            skLineSegment(sketch, "E1784", {"start": v(-6, 31.06) * mm, "end": v(-5.28, 31.4) * mm});
            skLineSegment(sketch, "E1785", {"start": v(-5.28, 31.4) * mm, "end": v(-5.15, 31.52) * mm});
            skLineSegment(sketch, "E1786", {"start": v(-5.15, 31.52) * mm, "end": v(-5.14, 31.6) * mm});
            skLineSegment(sketch, "E1787", {"start": v(-5.14, 31.6) * mm, "end": v(-5.23, 31.63) * mm});
            skLineSegment(sketch, "E1788", {"start": v(-5.23, 31.63) * mm, "end": v(-5.78, 31.53) * mm});
            skLineSegment(sketch, "E1789", {"start": v(-5.78, 31.53) * mm, "end": v(-6.97, 31.22) * mm});
            skLineSegment(sketch, "E1790", {"start": v(-6.97, 31.22) * mm, "end": v(-8.14, 30.8) * mm});
            skLineSegment(sketch, "E1791", {"start": v(-8.14, 30.8) * mm, "end": v(-9.74, 30.02) * mm});
            skLineSegment(sketch, "E1792", {"start": v(-9.74, 30.02) * mm, "end": v(-10.74, 29.42) * mm});
            skLineSegment(sketch, "E1793", {"start": v(-10.74, 29.42) * mm, "end": v(-11.69, 28.77) * mm});
            skLineSegment(sketch, "E1794", {"start": v(-11.69, 28.77) * mm, "end": v(-12.79, 27.9) * mm});
            skLineSegment(sketch, "E1795", {"start": v(-12.79, 27.9) * mm, "end": v(-14.07, 26.7) * mm});
            skLineSegment(sketch, "E1796", {"start": v(-14.07, 26.7) * mm, "end": v(-15.03, 25.62) * mm});
            skLineSegment(sketch, "E1797", {"start": v(-15.03, 25.62) * mm, "end": v(-15.69, 24.72) * mm});
            skLineSegment(sketch, "E1798", {"start": v(-15.69, 24.72) * mm, "end": v(-16.32, 23.57) * mm});
            skLineSegment(sketch, "E1799", {"start": v(-16.32, 23.57) * mm, "end": v(-16.69, 22.68) * mm});
            skLineSegment(sketch, "E1800", {"start": v(-16.69, 22.68) * mm, "end": v(-16.91, 21.8) * mm});
            skLineSegment(sketch, "E1801", {"start": v(-16.91, 21.8) * mm, "end": v(-16.95, 21.2) * mm});
            skLineSegment(sketch, "E1802", {"start": v(-16.95, 21.2) * mm, "end": v(-16.9, 20.77) * mm});
            skLineSegment(sketch, "E1803", {"start": v(-16.9, 20.77) * mm, "end": v(-16.7, 20.34) * mm});
            skLineSegment(sketch, "E1804", {"start": v(-16.7, 20.34) * mm, "end": v(-16.4, 19.92) * mm});
            skLineSegment(sketch, "E1805", {"start": v(-16.4, 19.92) * mm, "end": v(-15.45, 18.98) * mm});
            skLineSegment(sketch, "E1806", {"start": v(-20.8, -3.55) * mm, "end": v(-21.1, -2.3) * mm});
            skLineSegment(sketch, "E1807", {"start": v(-21.1, -2.3) * mm, "end": v(-21.14, -1.22) * mm});
            skLineSegment(sketch, "E1808", {"start": v(-21.14, -1.22) * mm, "end": v(-21, -0.42) * mm});
            skLineSegment(sketch, "E1809", {"start": v(-21, -0.42) * mm, "end": v(-20.56, 0.58) * mm});
            skLineSegment(sketch, "E1810", {"start": v(-20.56, 0.58) * mm, "end": v(-19.88, 1.44) * mm});
            skLineSegment(sketch, "E1811", {"start": v(-19.88, 1.44) * mm, "end": v(-19.02, 2.18) * mm});
            skLineSegment(sketch, "E1812", {"start": v(-19.02, 2.18) * mm, "end": v(-17.44, 3.14) * mm});
            skLineSegment(sketch, "E1813", {"start": v(-17.44, 3.14) * mm, "end": v(-16.33, 3.59) * mm});
            skLineSegment(sketch, "E1814", {"start": v(-16.33, 3.59) * mm, "end": v(-15.26, 4) * mm});
            skLineSegment(sketch, "E1815", {"start": v(-15.26, 4) * mm, "end": v(-15.08, 4.1) * mm});
            skLineSegment(sketch, "E1816", {"start": v(-15.08, 4.1) * mm, "end": v(-15.07, 4.17) * mm});
            skLineSegment(sketch, "E1817", {"start": v(-15.07, 4.17) * mm, "end": v(-15.13, 4.25) * mm});
            skLineSegment(sketch, "E1818", {"start": v(-15.13, 4.25) * mm, "end": v(-15.47, 4.26) * mm});
            skLineSegment(sketch, "E1819", {"start": v(-15.47, 4.26) * mm, "end": v(-16.27, 4.08) * mm});
            skLineSegment(sketch, "E1820", {"start": v(-16.27, 4.08) * mm, "end": v(-17.53, 3.67) * mm});
            skLineSegment(sketch, "E1821", {"start": v(-17.53, 3.67) * mm, "end": v(-18.8, 3.1) * mm});
            skLineSegment(sketch, "E1822", {"start": v(-18.8, 3.1) * mm, "end": v(-19.56, 2.67) * mm});
            skLineSegment(sketch, "E1823", {"start": v(-19.56, 2.67) * mm, "end": v(-20.47, 2) * mm});
            skLineSegment(sketch, "E1824", {"start": v(-20.47, 2) * mm, "end": v(-21.16, 1.32) * mm});
            skLineSegment(sketch, "E1825", {"start": v(-21.16, 1.32) * mm, "end": v(-21.6, 0.76) * mm});
            skLineSegment(sketch, "E1826", {"start": v(-21.6, 0.76) * mm, "end": v(-21.93, 0.15) * mm});
            skLineSegment(sketch, "E1827", {"start": v(-21.93, 0.15) * mm, "end": v(-22.1, -0.3) * mm});
            skLineSegment(sketch, "E1828", {"start": v(-22.1, -0.3) * mm, "end": v(-22.33, -1.16) * mm});
            skLineSegment(sketch, "E1829", {"start": v(-22.33, -1.16) * mm, "end": v(-22.44, -2.67) * mm});
            skLineSegment(sketch, "E1830", {"start": v(-22.44, -2.67) * mm, "end": v(-22.3, -3.66) * mm});
            skLineSegment(sketch, "E1831", {"start": v(-22.3, -3.66) * mm, "end": v(-21.99, -4.64) * mm});
            skLineSegment(sketch, "E1832", {"start": v(-21.99, -4.64) * mm, "end": v(-21.67, -5.26) * mm});
            skLineSegment(sketch, "E1833", {"start": v(-21.67, -5.26) * mm, "end": v(-21.28, -5.7) * mm});
            skLineSegment(sketch, "E1834", {"start": v(-21.28, -5.7) * mm, "end": v(-20.98, -5.83) * mm});
            skLineSegment(sketch, "E1835", {"start": v(-20.98, -5.83) * mm, "end": v(-20.64, -5.76) * mm});
            skLineSegment(sketch, "E1836", {"start": v(-20.64, -5.76) * mm, "end": v(-20.37, -5.56) * mm});
            skLineSegment(sketch, "E1837", {"start": v(-20.37, -5.56) * mm, "end": v(-20.3, -5.24) * mm});
            skLineSegment(sketch, "E1838", {"start": v(-20.3, -5.24) * mm, "end": v(-20.5, -4.49) * mm});
            skLineSegment(sketch, "E1839", {"start": v(-20.5, -4.49) * mm, "end": v(-20.8, -3.55) * mm});
            skLineSegment(sketch, "E1840", {"start": v(-28.35, -19.51) * mm, "end": v(-27.93, -18.37) * mm});
            skLineSegment(sketch, "E1841", {"start": v(-27.93, -18.37) * mm, "end": v(-27.5, -17.75) * mm});
            skLineSegment(sketch, "E1842", {"start": v(-27.5, -17.75) * mm, "end": v(-26.97, -17.31) * mm});
            skLineSegment(sketch, "E1843", {"start": v(-26.97, -17.31) * mm, "end": v(-26.83, -17.12) * mm});
            skLineSegment(sketch, "E1844", {"start": v(-26.83, -17.12) * mm, "end": v(-26.9, -17) * mm});
            skLineSegment(sketch, "E1845", {"start": v(-26.9, -17) * mm, "end": v(-27.15, -16.98) * mm});
            skLineSegment(sketch, "E1846", {"start": v(-27.15, -16.98) * mm, "end": v(-27.72, -17.17) * mm});
            skLineSegment(sketch, "E1847", {"start": v(-27.72, -17.17) * mm, "end": v(-28.14, -17.41) * mm});
            skLineSegment(sketch, "E1848", {"start": v(-28.14, -17.41) * mm, "end": v(-28.43, -17.64) * mm});
            skLineSegment(sketch, "E1849", {"start": v(-28.43, -17.64) * mm, "end": v(-28.78, -18) * mm});
            skLineSegment(sketch, "E1850", {"start": v(-28.78, -18) * mm, "end": v(-29.14, -18.5) * mm});
            skLineSegment(sketch, "E1851", {"start": v(-29.14, -18.5) * mm, "end": v(-29.41, -19.06) * mm});
            skLineSegment(sketch, "E1852", {"start": v(-29.41, -19.06) * mm, "end": v(-29.56, -19.52) * mm});
            skLineSegment(sketch, "E1853", {"start": v(-29.56, -19.52) * mm, "end": v(-29.63, -20.08) * mm});
            skLineSegment(sketch, "E1854", {"start": v(-29.63, -20.08) * mm, "end": v(-29.6, -20.48) * mm});
            skLineSegment(sketch, "E1855", {"start": v(-29.6, -20.48) * mm, "end": v(-29.43, -21.1) * mm});
            skLineSegment(sketch, "E1856", {"start": v(-29.43, -21.1) * mm, "end": v(-29.2, -21.51) * mm});
            skLineSegment(sketch, "E1857", {"start": v(-29.2, -21.51) * mm, "end": v(-29.05, -21.65) * mm});
            skLineSegment(sketch, "E1858", {"start": v(-29.05, -21.65) * mm, "end": v(-28.88, -21.72) * mm});
            skLineSegment(sketch, "E1859", {"start": v(-28.88, -21.72) * mm, "end": v(-28.62, -21.66) * mm});
            skLineSegment(sketch, "E1860", {"start": v(-28.62, -21.66) * mm, "end": v(-28.49, -21.44) * mm});
            skLineSegment(sketch, "E1861", {"start": v(-28.49, -21.44) * mm, "end": v(-28.47, -20.67) * mm});
            skLineSegment(sketch, "E1862", {"start": v(-28.47, -20.67) * mm, "end": v(-28.49, -20.18) * mm});
            skLineSegment(sketch, "E1863", {"start": v(-28.49, -20.18) * mm, "end": v(-28.35, -19.51) * mm});
            skLineSegment(sketch, "E1864", {"start": v(-35.57, -30.78) * mm, "end": v(-35.63, -29.9) * mm});
            skLineSegment(sketch, "E1865", {"start": v(-35.63, -29.9) * mm, "end": v(-35.58, -29.15) * mm});
            skLineSegment(sketch, "E1866", {"start": v(-35.58, -29.15) * mm, "end": v(-35.45, -28.33) * mm});
            skLineSegment(sketch, "E1867", {"start": v(-35.45, -28.33) * mm, "end": v(-35.42, -27.87) * mm});
            skLineSegment(sketch, "E1868", {"start": v(-35.42, -27.87) * mm, "end": v(-35.45, -27.79) * mm});
            skLineSegment(sketch, "E1869", {"start": v(-35.45, -27.79) * mm, "end": v(-35.53, -27.68) * mm});
            skLineSegment(sketch, "E1870", {"start": v(-35.53, -27.68) * mm, "end": v(-35.66, -27.68) * mm});
            skLineSegment(sketch, "E1871", {"start": v(-35.66, -27.68) * mm, "end": v(-35.84, -27.86) * mm});
            skLineSegment(sketch, "E1872", {"start": v(-35.84, -27.86) * mm, "end": v(-36.04, -28.11) * mm});
            skLineSegment(sketch, "E1873", {"start": v(-36.04, -28.11) * mm, "end": v(-36.14, -28.32) * mm});
            skLineSegment(sketch, "E1874", {"start": v(-36.14, -28.32) * mm, "end": v(-36.26, -28.66) * mm});
            skLineSegment(sketch, "E1875", {"start": v(-36.26, -28.66) * mm, "end": v(-36.36, -29.17) * mm});
            skLineSegment(sketch, "E1876", {"start": v(-36.36, -29.17) * mm, "end": v(-36.39, -29.5) * mm});
            skLineSegment(sketch, "E1877", {"start": v(-36.39, -29.5) * mm, "end": v(-36.4, -29.84) * mm});
            skLineSegment(sketch, "E1878", {"start": v(-36.4, -29.84) * mm, "end": v(-36.37, -30.37) * mm});
            skLineSegment(sketch, "E1879", {"start": v(-36.37, -30.37) * mm, "end": v(-36.32, -30.74) * mm});
            skLineSegment(sketch, "E1880", {"start": v(-36.32, -30.74) * mm, "end": v(-36.22, -31.17) * mm});
            skLineSegment(sketch, "E1881", {"start": v(-36.22, -31.17) * mm, "end": v(-35.97, -31.8) * mm});
            skLineSegment(sketch, "E1882", {"start": v(-35.97, -31.8) * mm, "end": v(-35.8, -32.2) * mm});
            skLineSegment(sketch, "E1883", {"start": v(-35.8, -32.2) * mm, "end": v(-35.65, -32.43) * mm});
            skLineSegment(sketch, "E1884", {"start": v(-35.65, -32.43) * mm, "end": v(-35.54, -32.55) * mm});
            skLineSegment(sketch, "E1885", {"start": v(-35.54, -32.55) * mm, "end": v(-35.44, -32.6) * mm});
            skLineSegment(sketch, "E1886", {"start": v(-35.44, -32.6) * mm, "end": v(-35.35, -32.6) * mm});
            skLineSegment(sketch, "E1887", {"start": v(-35.35, -32.6) * mm, "end": v(-35.28, -32.47) * mm});
            skLineSegment(sketch, "E1888", {"start": v(-35.28, -32.47) * mm, "end": v(-35.28, -32.23) * mm});
            skLineSegment(sketch, "E1889", {"start": v(-35.28, -32.23) * mm, "end": v(-35.32, -31.98) * mm});
            skLineSegment(sketch, "E1890", {"start": v(-35.32, -31.98) * mm, "end": v(-35.43, -31.5) * mm});
            skLineSegment(sketch, "E1891", {"start": v(-35.43, -31.5) * mm, "end": v(-35.52, -31.12) * mm});
            skLineSegment(sketch, "E1892", {"start": v(-35.52, -31.12) * mm, "end": v(-35.57, -30.78) * mm});
            skLineSegment(sketch, "E1893", {"start": v(-15.29, -33.5) * mm, "end": v(-14.48, -33.46) * mm});
            skLineSegment(sketch, "E1894", {"start": v(-14.48, -33.46) * mm, "end": v(-13.64, -33.2) * mm});
            skLineSegment(sketch, "E1895", {"start": v(-13.64, -33.2) * mm, "end": v(-13.47, -32.94) * mm});
            skLineSegment(sketch, "E1896", {"start": v(-13.47, -32.94) * mm, "end": v(-13.23, -32.37) * mm});
            skLineSegment(sketch, "E1897", {"start": v(-13.23, -32.37) * mm, "end": v(-13.16, -32.04) * mm});
            skLineSegment(sketch, "E1898", {"start": v(-13.16, -32.04) * mm, "end": v(-13.2, -31.95) * mm});
            skLineSegment(sketch, "E1899", {"start": v(-13.2, -31.95) * mm, "end": v(-13.32, -31.88) * mm});
            skLineSegment(sketch, "E1900", {"start": v(-13.32, -31.88) * mm, "end": v(-13.63, -31.84) * mm});
            skLineSegment(sketch, "E1901", {"start": v(-13.63, -31.84) * mm, "end": v(-14.1, -31.83) * mm});
            skLineSegment(sketch, "E1902", {"start": v(-14.1, -31.83) * mm, "end": v(-14.46, -31.77) * mm});
            skLineSegment(sketch, "E1903", {"start": v(-14.46, -31.77) * mm, "end": v(-15.3, -31.44) * mm});
            skLineSegment(sketch, "E1904", {"start": v(-15.3, -31.44) * mm, "end": v(-16.28, -31.04) * mm});
            skLineSegment(sketch, "E1905", {"start": v(-16.28, -31.04) * mm, "end": v(-16.92, -30.85) * mm});
            skLineSegment(sketch, "E1906", {"start": v(-16.92, -30.85) * mm, "end": v(-17.26, -30.8) * mm});
            skLineSegment(sketch, "E1907", {"start": v(-17.26, -30.8) * mm, "end": v(-17.55, -30.8) * mm});
            skLineSegment(sketch, "E1908", {"start": v(-17.55, -30.8) * mm, "end": v(-17.77, -30.9) * mm});
            skLineSegment(sketch, "E1909", {"start": v(-17.77, -30.9) * mm, "end": v(-17.96, -31.1) * mm});
            skLineSegment(sketch, "E1910", {"start": v(-17.96, -31.1) * mm, "end": v(-18.13, -31.36) * mm});
            skLineSegment(sketch, "E1911", {"start": v(-18.13, -31.36) * mm, "end": v(-18.19, -31.68) * mm});
            skLineSegment(sketch, "E1912", {"start": v(-18.19, -31.68) * mm, "end": v(-18.14, -31.9) * mm});
            skLineSegment(sketch, "E1913", {"start": v(-18.14, -31.9) * mm, "end": v(-18, -32.22) * mm});
            skLineSegment(sketch, "E1914", {"start": v(-18, -32.22) * mm, "end": v(-17.7, -32.58) * mm});
            skLineSegment(sketch, "E1915", {"start": v(-17.7, -32.58) * mm, "end": v(-17.21, -32.96) * mm});
            skLineSegment(sketch, "E1916", {"start": v(-17.21, -32.96) * mm, "end": v(-16.46, -33.34) * mm});
            skLineSegment(sketch, "E1917", {"start": v(-16.46, -33.34) * mm, "end": v(-15.9, -33.5) * mm});
            skLineSegment(sketch, "E1918", {"start": v(-15.9, -33.5) * mm, "end": v(-15.29, -33.5) * mm});
            skLineSegment(sketch, "E1919", {"start": v(-8.82, 22.8) * mm, "end": v(-8.42, 22.65) * mm});
            skLineSegment(sketch, "E1920", {"start": v(-8.42, 22.65) * mm, "end": v(-7.99, 22.56) * mm});
            skLineSegment(sketch, "E1921", {"start": v(-7.99, 22.56) * mm, "end": v(-7.6, 22.55) * mm});
            skLineSegment(sketch, "E1922", {"start": v(-7.6, 22.55) * mm, "end": v(-7.4, 22.62) * mm});
            skLineSegment(sketch, "E1923", {"start": v(-7.4, 22.62) * mm, "end": v(-7.29, 22.72) * mm});
            skLineSegment(sketch, "E1924", {"start": v(-7.29, 22.72) * mm, "end": v(-7.25, 22.89) * mm});
            skLineSegment(sketch, "E1925", {"start": v(-7.25, 22.89) * mm, "end": v(-7.36, 23.15) * mm});
            skLineSegment(sketch, "E1926", {"start": v(-7.36, 23.15) * mm, "end": v(-7.74, 23.5) * mm});
            skLineSegment(sketch, "E1927", {"start": v(-7.74, 23.5) * mm, "end": v(-8.24, 23.83) * mm});
            skLineSegment(sketch, "E1928", {"start": v(-8.24, 23.83) * mm, "end": v(-8.68, 24.04) * mm});
            skLineSegment(sketch, "E1929", {"start": v(-8.68, 24.04) * mm, "end": v(-9, 24.15) * mm});
            skLineSegment(sketch, "E1930", {"start": v(-9, 24.15) * mm, "end": v(-9.27, 24.2) * mm});
            skLineSegment(sketch, "E1931", {"start": v(-9.27, 24.2) * mm, "end": v(-9.54, 24.17) * mm});
            skLineSegment(sketch, "E1932", {"start": v(-9.54, 24.17) * mm, "end": v(-9.66, 24.07) * mm});
            skLineSegment(sketch, "E1933", {"start": v(-9.66, 24.07) * mm, "end": v(-9.79, 23.96) * mm});
            skLineSegment(sketch, "E1934", {"start": v(-9.79, 23.96) * mm, "end": v(-9.84, 23.85) * mm});
            skLineSegment(sketch, "E1935", {"start": v(-9.84, 23.85) * mm, "end": v(-9.82, 23.6) * mm});
            skLineSegment(sketch, "E1936", {"start": v(-9.82, 23.6) * mm, "end": v(-9.59, 23.3) * mm});
            skLineSegment(sketch, "E1937", {"start": v(-9.59, 23.3) * mm, "end": v(-9.27, 23.05) * mm});
            skLineSegment(sketch, "E1938", {"start": v(-9.27, 23.05) * mm, "end": v(-8.82, 22.8) * mm});
            skLineSegment(sketch, "E1939", {"start": v(-8.69, 24.88) * mm, "end": v(-8.45, 24.68) * mm});
            skLineSegment(sketch, "E1940", {"start": v(-8.45, 24.68) * mm, "end": v(-8.11, 24.47) * mm});
            skLineSegment(sketch, "E1941", {"start": v(-8.11, 24.47) * mm, "end": v(-7.77, 24.33) * mm});
            skLineSegment(sketch, "E1942", {"start": v(-7.77, 24.33) * mm, "end": v(-7.53, 24.29) * mm});
            skLineSegment(sketch, "E1943", {"start": v(-7.53, 24.29) * mm, "end": v(-7.31, 24.3) * mm});
            skLineSegment(sketch, "E1944", {"start": v(-7.31, 24.3) * mm, "end": v(-7.12, 24.42) * mm});
            skLineSegment(sketch, "E1945", {"start": v(-7.12, 24.42) * mm, "end": v(-6.97, 24.62) * mm});
            skLineSegment(sketch, "E1946", {"start": v(-6.97, 24.62) * mm, "end": v(-6.94, 24.85) * mm});
            skLineSegment(sketch, "E1947", {"start": v(-6.94, 24.85) * mm, "end": v(-6.99, 25.1) * mm});
            skLineSegment(sketch, "E1948", {"start": v(-6.99, 25.1) * mm, "end": v(-7.12, 25.36) * mm});
            skLineSegment(sketch, "E1949", {"start": v(-7.12, 25.36) * mm, "end": v(-7.38, 25.7) * mm});
            skLineSegment(sketch, "E1950", {"start": v(-7.38, 25.7) * mm, "end": v(-7.71, 26) * mm});
            skLineSegment(sketch, "E1951", {"start": v(-7.71, 26) * mm, "end": v(-8.07, 26.22) * mm});
            skLineSegment(sketch, "E1952", {"start": v(-8.07, 26.22) * mm, "end": v(-8.43, 26.35) * mm});
            skLineSegment(sketch, "E1953", {"start": v(-8.43, 26.35) * mm, "end": v(-8.68, 26.37) * mm});
            skLineSegment(sketch, "E1954", {"start": v(-8.68, 26.37) * mm, "end": v(-8.9, 26.28) * mm});
            skLineSegment(sketch, "E1955", {"start": v(-8.9, 26.28) * mm, "end": v(-9.1, 26.12) * mm});
            skLineSegment(sketch, "E1956", {"start": v(-9.1, 26.12) * mm, "end": v(-9.17, 26) * mm});
            skLineSegment(sketch, "E1957", {"start": v(-9.17, 26) * mm, "end": v(-9.2, 25.86) * mm});
            skLineSegment(sketch, "E1958", {"start": v(-9.2, 25.86) * mm, "end": v(-9.18, 25.64) * mm});
            skLineSegment(sketch, "E1959", {"start": v(-9.18, 25.64) * mm, "end": v(-9.1, 25.4) * mm});
            skLineSegment(sketch, "E1960", {"start": v(-9.1, 25.4) * mm, "end": v(-8.95, 25.18) * mm});
            skLineSegment(sketch, "E1961", {"start": v(-8.95, 25.18) * mm, "end": v(-8.69, 24.88) * mm});
            skLineSegment(sketch, "E1962", {"start": v(-5.83, 27.1) * mm, "end": v(-5.71, 27.52) * mm});
            skLineSegment(sketch, "E1963", {"start": v(-5.71, 27.52) * mm, "end": v(-5.7, 28.05) * mm});
            skLineSegment(sketch, "E1964", {"start": v(-5.7, 28.05) * mm, "end": v(-5.8, 28.5) * mm});
            skLineSegment(sketch, "E1965", {"start": v(-5.8, 28.5) * mm, "end": v(-5.91, 28.71) * mm});
            skLineSegment(sketch, "E1966", {"start": v(-5.91, 28.71) * mm, "end": v(-6.16, 28.94) * mm});
            skLineSegment(sketch, "E1967", {"start": v(-6.16, 28.94) * mm, "end": v(-6.5, 29.01) * mm});
            skLineSegment(sketch, "E1968", {"start": v(-6.5, 29.01) * mm, "end": v(-6.77, 28.95) * mm});
            skLineSegment(sketch, "E1969", {"start": v(-6.77, 28.95) * mm, "end": v(-7.18, 28.73) * mm});
            skLineSegment(sketch, "E1970", {"start": v(-7.18, 28.73) * mm, "end": v(-7.38, 28.55) * mm});
            skLineSegment(sketch, "E1971", {"start": v(-7.38, 28.55) * mm, "end": v(-7.64, 28.16) * mm});
            skLineSegment(sketch, "E1972", {"start": v(-7.64, 28.16) * mm, "end": v(-7.8, 27.74) * mm});
            skLineSegment(sketch, "E1973", {"start": v(-7.8, 27.74) * mm, "end": v(-7.84, 27.22) * mm});
            skLineSegment(sketch, "E1974", {"start": v(-7.84, 27.22) * mm, "end": v(-7.76, 26.91) * mm});
            skLineSegment(sketch, "E1975", {"start": v(-7.76, 26.91) * mm, "end": v(-7.6, 26.65) * mm});
            skLineSegment(sketch, "E1976", {"start": v(-7.6, 26.65) * mm, "end": v(-7.42, 26.5) * mm});
            skLineSegment(sketch, "E1977", {"start": v(-7.42, 26.5) * mm, "end": v(-7.1, 26.38) * mm});
            skLineSegment(sketch, "E1978", {"start": v(-7.1, 26.38) * mm, "end": v(-6.8, 26.35) * mm});
            skLineSegment(sketch, "E1979", {"start": v(-6.8, 26.35) * mm, "end": v(-6.5, 26.4) * mm});
            skLineSegment(sketch, "E1980", {"start": v(-6.5, 26.4) * mm, "end": v(-6.2, 26.57) * mm});
            skLineSegment(sketch, "E1981", {"start": v(-6.2, 26.57) * mm, "end": v(-5.96, 26.84) * mm});
            skLineSegment(sketch, "E1982", {"start": v(-5.96, 26.84) * mm, "end": v(-5.83, 27.1) * mm});
            skLineSegment(sketch, "E1983", {"start": v(8.49, 28.17) * mm, "end": v(8.98, 27.87) * mm});
            skLineSegment(sketch, "E1984", {"start": v(8.98, 27.87) * mm, "end": v(9.5, 27.68) * mm});
            skLineSegment(sketch, "E1985", {"start": v(9.5, 27.68) * mm, "end": v(9.94, 27.62) * mm});
            skLineSegment(sketch, "E1986", {"start": v(9.94, 27.62) * mm, "end": v(10.27, 27.66) * mm});
            skLineSegment(sketch, "E1987", {"start": v(10.27, 27.66) * mm, "end": v(10.67, 27.82) * mm});
            skLineSegment(sketch, "E1988", {"start": v(10.67, 27.82) * mm, "end": v(10.88, 27.99) * mm});
            skLineSegment(sketch, "E1989", {"start": v(10.88, 27.99) * mm, "end": v(11.06, 28.2) * mm});
            skLineSegment(sketch, "E1990", {"start": v(11.06, 28.2) * mm, "end": v(11.19, 28.51) * mm});
            skLineSegment(sketch, "E1991", {"start": v(11.19, 28.51) * mm, "end": v(11.2, 28.84) * mm});
            skLineSegment(sketch, "E1992", {"start": v(11.2, 28.84) * mm, "end": v(11.09, 29.24) * mm});
            skLineSegment(sketch, "E1993", {"start": v(11.09, 29.24) * mm, "end": v(10.84, 29.63) * mm});
            skLineSegment(sketch, "E1994", {"start": v(10.84, 29.63) * mm, "end": v(10.65, 29.86) * mm});
            skLineSegment(sketch, "E1995", {"start": v(10.65, 29.86) * mm, "end": v(10.26, 30.2) * mm});
            skLineSegment(sketch, "E1996", {"start": v(10.26, 30.2) * mm, "end": v(10, 30.38) * mm});
            skLineSegment(sketch, "E1997", {"start": v(10, 30.38) * mm, "end": v(9.63, 30.59) * mm});
            skLineSegment(sketch, "E1998", {"start": v(9.63, 30.59) * mm, "end": v(9.26, 30.74) * mm});
            skLineSegment(sketch, "E1999", {"start": v(9.26, 30.74) * mm, "end": v(8.89, 30.84) * mm});
            skLineSegment(sketch, "E2000", {"start": v(8.89, 30.84) * mm, "end": v(8.63, 30.87) * mm});
            skLineSegment(sketch, "E2001", {"start": v(8.63, 30.87) * mm, "end": v(8.38, 30.87) * mm});
            skLineSegment(sketch, "E2002", {"start": v(8.38, 30.87) * mm, "end": v(8.09, 30.79) * mm});
            skLineSegment(sketch, "E2003", {"start": v(8.09, 30.79) * mm, "end": v(7.96, 30.72) * mm});
            skLineSegment(sketch, "E2004", {"start": v(7.96, 30.72) * mm, "end": v(7.73, 30.47) * mm});
            skLineSegment(sketch, "E2005", {"start": v(7.73, 30.47) * mm, "end": v(7.62, 30.3) * mm});
            skLineSegment(sketch, "E2006", {"start": v(7.62, 30.3) * mm, "end": v(7.51, 29.96) * mm});
            skLineSegment(sketch, "E2007", {"start": v(7.51, 29.96) * mm, "end": v(7.52, 29.56) * mm});
            skLineSegment(sketch, "E2008", {"start": v(7.52, 29.56) * mm, "end": v(7.62, 29.25) * mm});
            skLineSegment(sketch, "E2009", {"start": v(7.62, 29.25) * mm, "end": v(7.83, 28.86) * mm});
            skLineSegment(sketch, "E2010", {"start": v(7.83, 28.86) * mm, "end": v(8.13, 28.5) * mm});
            skLineSegment(sketch, "E2011", {"start": v(8.13, 28.5) * mm, "end": v(8.49, 28.17) * mm});
            skLineSegment(sketch, "E2012", {"start": v(3.3, 26.82) * mm, "end": v(4.07, 26.93) * mm});
            skLineSegment(sketch, "E2013", {"start": v(4.07, 26.93) * mm, "end": v(4.92, 27.2) * mm});
            skLineSegment(sketch, "E2014", {"start": v(4.92, 27.2) * mm, "end": v(5.28, 27.42) * mm});
            skLineSegment(sketch, "E2015", {"start": v(5.28, 27.42) * mm, "end": v(5.32, 27.48) * mm});
            skLineSegment(sketch, "E2016", {"start": v(5.32, 27.48) * mm, "end": v(5.27, 27.61) * mm});
            skLineSegment(sketch, "E2017", {"start": v(5.27, 27.61) * mm, "end": v(5.05, 27.7) * mm});
            skLineSegment(sketch, "E2018", {"start": v(5.05, 27.7) * mm, "end": v(4.74, 27.77) * mm});
            skLineSegment(sketch, "E2019", {"start": v(4.74, 27.77) * mm, "end": v(3.87, 28) * mm});
            skLineSegment(sketch, "E2020", {"start": v(3.87, 28) * mm, "end": v(3, 28.2) * mm});
            skLineSegment(sketch, "E2021", {"start": v(3, 28.2) * mm, "end": v(2.48, 28.25) * mm});
            skLineSegment(sketch, "E2022", {"start": v(2.48, 28.25) * mm, "end": v(2.21, 28.2) * mm});
            skLineSegment(sketch, "E2023", {"start": v(2.21, 28.2) * mm, "end": v(2.05, 28.05) * mm});
            skLineSegment(sketch, "E2024", {"start": v(2.05, 28.05) * mm, "end": v(2.08, 27.75) * mm});
            skLineSegment(sketch, "E2025", {"start": v(2.08, 27.75) * mm, "end": v(2.35, 27.32) * mm});
            skLineSegment(sketch, "E2026", {"start": v(2.35, 27.32) * mm, "end": v(2.62, 27.04) * mm});
            skLineSegment(sketch, "E2027", {"start": v(2.62, 27.04) * mm, "end": v(2.85, 26.87) * mm});
            skLineSegment(sketch, "E2028", {"start": v(2.85, 26.87) * mm, "end": v(3.1, 26.82) * mm});
            skLineSegment(sketch, "E2029", {"start": v(3.1, 26.82) * mm, "end": v(3.3, 26.82) * mm});
            skLineSegment(sketch, "E2030", {"start": v(3.51, 29.34) * mm, "end": v(4.56, 29.27) * mm});
            skLineSegment(sketch, "E2031", {"start": v(4.56, 29.27) * mm, "end": v(5.07, 29.2) * mm});
            skLineSegment(sketch, "E2032", {"start": v(5.07, 29.2) * mm, "end": v(5.67, 29.04) * mm});
            skLineSegment(sketch, "E2033", {"start": v(5.67, 29.04) * mm, "end": v(6.12, 28.96) * mm});
            skLineSegment(sketch, "E2034", {"start": v(6.12, 28.96) * mm, "end": v(6.51, 29.08) * mm});
            skLineSegment(sketch, "E2035", {"start": v(6.51, 29.08) * mm, "end": v(6.72, 29.4) * mm});
            skLineSegment(sketch, "E2036", {"start": v(6.72, 29.4) * mm, "end": v(6.8, 29.85) * mm});
            skLineSegment(sketch, "E2037", {"start": v(6.8, 29.85) * mm, "end": v(6.8, 30.21) * mm});
            skLineSegment(sketch, "E2038", {"start": v(6.8, 30.21) * mm, "end": v(6.65, 30.76) * mm});
            skLineSegment(sketch, "E2039", {"start": v(6.65, 30.76) * mm, "end": v(6.5, 31) * mm});
            skLineSegment(sketch, "E2040", {"start": v(6.5, 31) * mm, "end": v(5.96, 31.27) * mm});
            skLineSegment(sketch, "E2041", {"start": v(5.96, 31.27) * mm, "end": v(5.1, 31.47) * mm});
            skLineSegment(sketch, "E2042", {"start": v(5.1, 31.47) * mm, "end": v(4.27, 31.57) * mm});
            skLineSegment(sketch, "E2043", {"start": v(4.27, 31.57) * mm, "end": v(3.49, 31.61) * mm});
            skLineSegment(sketch, "E2044", {"start": v(3.49, 31.61) * mm, "end": v(2.74, 31.6) * mm});
            skLineSegment(sketch, "E2045", {"start": v(2.74, 31.6) * mm, "end": v(1.8, 31.52) * mm});
            skLineSegment(sketch, "E2046", {"start": v(1.8, 31.52) * mm, "end": v(1.4, 31.39) * mm});
            skLineSegment(sketch, "E2047", {"start": v(1.4, 31.39) * mm, "end": v(1.16, 31.1) * mm});
            skLineSegment(sketch, "E2048", {"start": v(1.16, 31.1) * mm, "end": v(1.08, 30.7) * mm});
            skLineSegment(sketch, "E2049", {"start": v(1.08, 30.7) * mm, "end": v(1.15, 30.28) * mm});
            skLineSegment(sketch, "E2050", {"start": v(1.15, 30.28) * mm, "end": v(1.36, 29.92) * mm});
            skLineSegment(sketch, "E2051", {"start": v(1.36, 29.92) * mm, "end": v(1.6, 29.72) * mm});
            skLineSegment(sketch, "E2052", {"start": v(1.6, 29.72) * mm, "end": v(1.9, 29.58) * mm});
            skLineSegment(sketch, "E2053", {"start": v(1.9, 29.58) * mm, "end": v(2.27, 29.48) * mm});
            skLineSegment(sketch, "E2054", {"start": v(2.27, 29.48) * mm, "end": v(2.84, 29.39) * mm});
            skLineSegment(sketch, "E2055", {"start": v(2.84, 29.39) * mm, "end": v(3.51, 29.34) * mm});
            skLineSegment(sketch, "E2056", {"start": v(-3.16, 28.82) * mm, "end": v(-2.01, 29.3) * mm});
            skLineSegment(sketch, "E2057", {"start": v(-2.01, 29.3) * mm, "end": v(-1.55, 29.44) * mm});
            skLineSegment(sketch, "E2058", {"start": v(-1.55, 29.44) * mm, "end": v(-1.1, 29.52) * mm});
            skLineSegment(sketch, "E2059", {"start": v(-1.1, 29.52) * mm, "end": v(-0.6, 29.55) * mm});
            skLineSegment(sketch, "E2060", {"start": v(-0.6, 29.55) * mm, "end": v(-0.17, 29.68) * mm});
            skLineSegment(sketch, "E2061", {"start": v(-0.17, 29.68) * mm, "end": v(0.1, 29.94) * mm});
            skLineSegment(sketch, "E2062", {"start": v(0.1, 29.94) * mm, "end": v(0.18, 30.24) * mm});
            skLineSegment(sketch, "E2063", {"start": v(0.18, 30.24) * mm, "end": v(0.17, 30.57) * mm});
            skLineSegment(sketch, "E2064", {"start": v(0.17, 30.57) * mm, "end": v(0.06, 30.88) * mm});
            skLineSegment(sketch, "E2065", {"start": v(0.06, 30.88) * mm, "end": v(-0.06, 31.06) * mm});
            skLineSegment(sketch, "E2066", {"start": v(-0.06, 31.06) * mm, "end": v(-0.3, 31.27) * mm});
            skLineSegment(sketch, "E2067", {"start": v(-0.3, 31.27) * mm, "end": v(-0.71, 31.35) * mm});
            skLineSegment(sketch, "E2068", {"start": v(-0.71, 31.35) * mm, "end": v(-1.31, 31.33) * mm});
            skLineSegment(sketch, "E2069", {"start": v(-1.31, 31.33) * mm, "end": v(-1.96, 31.24) * mm});
            skLineSegment(sketch, "E2070", {"start": v(-1.96, 31.24) * mm, "end": v(-2.63, 31.09) * mm});
            skLineSegment(sketch, "E2071", {"start": v(-2.63, 31.09) * mm, "end": v(-3.41, 30.85) * mm});
            skLineSegment(sketch, "E2072", {"start": v(-3.41, 30.85) * mm, "end": v(-4.37, 30.45) * mm});
            skLineSegment(sketch, "E2073", {"start": v(-4.37, 30.45) * mm, "end": v(-4.86, 30.16) * mm});
            skLineSegment(sketch, "E2074", {"start": v(-4.86, 30.16) * mm, "end": v(-5.02, 30.02) * mm});
            skLineSegment(sketch, "E2075", {"start": v(-5.02, 30.02) * mm, "end": v(-5.21, 29.66) * mm});
            skLineSegment(sketch, "E2076", {"start": v(-5.21, 29.66) * mm, "end": v(-5.26, 29.36) * mm});
            skLineSegment(sketch, "E2077", {"start": v(-5.26, 29.36) * mm, "end": v(-5.22, 29.07) * mm});
            skLineSegment(sketch, "E2078", {"start": v(-5.22, 29.07) * mm, "end": v(-5.02, 28.73) * mm});
            skLineSegment(sketch, "E2079", {"start": v(-5.02, 28.73) * mm, "end": v(-4.85, 28.6) * mm});
            skLineSegment(sketch, "E2080", {"start": v(-4.85, 28.6) * mm, "end": v(-4.54, 28.5) * mm});
            skLineSegment(sketch, "E2081", {"start": v(-4.54, 28.5) * mm, "end": v(-4.23, 28.5) * mm});
            skLineSegment(sketch, "E2082", {"start": v(-4.23, 28.5) * mm, "end": v(-3.66, 28.64) * mm});
            skLineSegment(sketch, "E2083", {"start": v(-3.66, 28.64) * mm, "end": v(-3.16, 28.82) * mm});
            skLineSegment(sketch, "E2084", {"start": v(-2.44, 25.48) * mm, "end": v(-1.61, 24.84) * mm});
            skLineSegment(sketch, "E2085", {"start": v(-1.61, 24.84) * mm, "end": v(-1.02, 24.46) * mm});
            skLineSegment(sketch, "E2086", {"start": v(-1.02, 24.46) * mm, "end": v(-0.44, 24.19) * mm});
            skLineSegment(sketch, "E2087", {"start": v(-0.44, 24.19) * mm, "end": v(-0.1, 24.1) * mm});
            skLineSegment(sketch, "E2088", {"start": v(-0.1, 24.1) * mm, "end": v(0.36, 24.1) * mm});
            skLineSegment(sketch, "E2089", {"start": v(0.36, 24.1) * mm, "end": v(0.62, 24.23) * mm});
            skLineSegment(sketch, "E2090", {"start": v(0.62, 24.23) * mm, "end": v(1.02, 24.58) * mm});
            skLineSegment(sketch, "E2091", {"start": v(1.02, 24.58) * mm, "end": v(1.56, 25.25) * mm});
            skLineSegment(sketch, "E2092", {"start": v(1.56, 25.25) * mm, "end": v(1.73, 25.59) * mm});
            skLineSegment(sketch, "E2093", {"start": v(1.73, 25.59) * mm, "end": v(1.8, 25.97) * mm});
            skLineSegment(sketch, "E2094", {"start": v(1.8, 25.97) * mm, "end": v(1.72, 26.27) * mm});
            skLineSegment(sketch, "E2095", {"start": v(1.72, 26.27) * mm, "end": v(1.47, 26.8) * mm});
            skLineSegment(sketch, "E2096", {"start": v(1.47, 26.8) * mm, "end": v(0.95, 27.47) * mm});
            skLineSegment(sketch, "E2097", {"start": v(0.95, 27.47) * mm, "end": v(0.38, 27.95) * mm});
            skLineSegment(sketch, "E2098", {"start": v(0.38, 27.95) * mm, "end": v(-0.13, 28.21) * mm});
            skLineSegment(sketch, "E2099", {"start": v(-0.13, 28.21) * mm, "end": v(-0.45, 28.31) * mm});
            skLineSegment(sketch, "E2100", {"start": v(-0.45, 28.31) * mm, "end": v(-0.87, 28.34) * mm});
            skLineSegment(sketch, "E2101", {"start": v(-0.87, 28.34) * mm, "end": v(-1.47, 28.25) * mm});
            skLineSegment(sketch, "E2102", {"start": v(-1.47, 28.25) * mm, "end": v(-2.56, 27.98) * mm});
            skLineSegment(sketch, "E2103", {"start": v(-2.56, 27.98) * mm, "end": v(-3.08, 27.78) * mm});
            skLineSegment(sketch, "E2104", {"start": v(-3.08, 27.78) * mm, "end": v(-3.49, 27.53) * mm});
            skLineSegment(sketch, "E2105", {"start": v(-3.49, 27.53) * mm, "end": v(-3.7, 27.23) * mm});
            skLineSegment(sketch, "E2106", {"start": v(-3.7, 27.23) * mm, "end": v(-3.68, 26.9) * mm});
            skLineSegment(sketch, "E2107", {"start": v(-3.68, 26.9) * mm, "end": v(-3.43, 26.46) * mm});
            skLineSegment(sketch, "E2108", {"start": v(-3.43, 26.46) * mm, "end": v(-3.05, 26.05) * mm});
            skLineSegment(sketch, "E2109", {"start": v(-3.05, 26.05) * mm, "end": v(-2.44, 25.48) * mm});
            skLineSegment(sketch, "E2110", {"start": v(26.39, -29.26) * mm, "end": v(26.52, -28.99) * mm});
            skLineSegment(sketch, "E2111", {"start": v(26.52, -28.99) * mm, "end": v(26.56, -28.68) * mm});
            skLineSegment(sketch, "E2112", {"start": v(26.56, -28.68) * mm, "end": v(26.52, -28.4) * mm});
            skLineSegment(sketch, "E2113", {"start": v(26.52, -28.4) * mm, "end": v(26.34, -28.2) * mm});
            skLineSegment(sketch, "E2114", {"start": v(26.34, -28.2) * mm, "end": v(26.04, -28.32) * mm});
            skLineSegment(sketch, "E2115", {"start": v(26.04, -28.32) * mm, "end": v(25.79, -28.6) * mm});
            skLineSegment(sketch, "E2116", {"start": v(25.79, -28.6) * mm, "end": v(25.64, -28.95) * mm});
            skLineSegment(sketch, "E2117", {"start": v(25.64, -28.95) * mm, "end": v(25.64, -29.27) * mm});
            skLineSegment(sketch, "E2118", {"start": v(25.64, -29.27) * mm, "end": v(25.87, -29.45) * mm});
            skLineSegment(sketch, "E2119", {"start": v(25.87, -29.45) * mm, "end": v(26.17, -29.44) * mm});
            skLineSegment(sketch, "E2120", {"start": v(26.17, -29.44) * mm, "end": v(26.39, -29.26) * mm});
            skLineSegment(sketch, "E2121", {"start": v(24.9, -28.04) * mm, "end": v(25.07, -27.7) * mm});
            skLineSegment(sketch, "E2122", {"start": v(25.07, -27.7) * mm, "end": v(25.15, -27.35) * mm});
            skLineSegment(sketch, "E2123", {"start": v(25.15, -27.35) * mm, "end": v(25.14, -26.99) * mm});
            skLineSegment(sketch, "E2124", {"start": v(25.14, -26.99) * mm, "end": v(25.1, -26.76) * mm});
            skLineSegment(sketch, "E2125", {"start": v(25.1, -26.76) * mm, "end": v(25.03, -26.66) * mm});
            skLineSegment(sketch, "E2126", {"start": v(25.03, -26.66) * mm, "end": v(24.93, -26.56) * mm});
            skLineSegment(sketch, "E2127", {"start": v(24.93, -26.56) * mm, "end": v(24.74, -26.64) * mm});
            skLineSegment(sketch, "E2128", {"start": v(24.74, -26.64) * mm, "end": v(24.52, -26.88) * mm});
            skLineSegment(sketch, "E2129", {"start": v(24.52, -26.88) * mm, "end": v(24.34, -27.12) * mm});
            skLineSegment(sketch, "E2130", {"start": v(24.34, -27.12) * mm, "end": v(24.13, -27.48) * mm});
            skLineSegment(sketch, "E2131", {"start": v(24.13, -27.48) * mm, "end": v(23.98, -27.85) * mm});
            skLineSegment(sketch, "E2132", {"start": v(23.98, -27.85) * mm, "end": v(23.92, -28.1) * mm});
            skLineSegment(sketch, "E2133", {"start": v(23.92, -28.1) * mm, "end": v(23.96, -28.28) * mm});
            skLineSegment(sketch, "E2134", {"start": v(23.96, -28.28) * mm, "end": v(24.08, -28.4) * mm});
            skLineSegment(sketch, "E2135", {"start": v(24.08, -28.4) * mm, "end": v(24.22, -28.41) * mm});
            skLineSegment(sketch, "E2136", {"start": v(24.22, -28.41) * mm, "end": v(24.53, -28.34) * mm});
            skLineSegment(sketch, "E2137", {"start": v(24.53, -28.34) * mm, "end": v(24.73, -28.21) * mm});
            skLineSegment(sketch, "E2138", {"start": v(24.73, -28.21) * mm, "end": v(24.9, -28.04) * mm});
            skLineSegment(sketch, "E2139", {"start": v(23.16, -27.01) * mm, "end": v(23.32, -26.68) * mm});
            skLineSegment(sketch, "E2140", {"start": v(23.32, -26.68) * mm, "end": v(23.37, -26.36) * mm});
            skLineSegment(sketch, "E2141", {"start": v(23.37, -26.36) * mm, "end": v(23.37, -26.2) * mm});
            skLineSegment(sketch, "E2142", {"start": v(23.37, -26.2) * mm, "end": v(23.32, -25.94) * mm});
            skLineSegment(sketch, "E2143", {"start": v(23.32, -25.94) * mm, "end": v(23.24, -25.75) * mm});
            skLineSegment(sketch, "E2144", {"start": v(23.24, -25.75) * mm, "end": v(23.17, -25.68) * mm});
            skLineSegment(sketch, "E2145", {"start": v(23.17, -25.68) * mm, "end": v(23, -25.72) * mm});
            skLineSegment(sketch, "E2146", {"start": v(23, -25.72) * mm, "end": v(22.77, -25.94) * mm});
            skLineSegment(sketch, "E2147", {"start": v(22.77, -25.94) * mm, "end": v(22.58, -26.2) * mm});
            skLineSegment(sketch, "E2148", {"start": v(22.58, -26.2) * mm, "end": v(22.3, -26.7) * mm});
            skLineSegment(sketch, "E2149", {"start": v(22.3, -26.7) * mm, "end": v(22.19, -26.98) * mm});
            skLineSegment(sketch, "E2150", {"start": v(22.19, -26.98) * mm, "end": v(22.14, -27.24) * mm});
            skLineSegment(sketch, "E2151", {"start": v(22.14, -27.24) * mm, "end": v(22.15, -27.37) * mm});
            skLineSegment(sketch, "E2152", {"start": v(22.15, -27.37) * mm, "end": v(22.33, -27.51) * mm});
            skLineSegment(sketch, "E2153", {"start": v(22.33, -27.51) * mm, "end": v(22.52, -27.5) * mm});
            skLineSegment(sketch, "E2154", {"start": v(22.52, -27.5) * mm, "end": v(22.8, -27.38) * mm});
            skLineSegment(sketch, "E2155", {"start": v(22.8, -27.38) * mm, "end": v(22.98, -27.24) * mm});
            skLineSegment(sketch, "E2156", {"start": v(22.98, -27.24) * mm, "end": v(23.16, -27.01) * mm});
            skLineSegment(sketch, "E2157", {"start": v(21.43, -26.11) * mm, "end": v(21.56, -25.78) * mm});
            skLineSegment(sketch, "E2158", {"start": v(21.56, -25.78) * mm, "end": v(21.58, -25.47) * mm});
            skLineSegment(sketch, "E2159", {"start": v(21.58, -25.47) * mm, "end": v(21.49, -25.09) * mm});
            skLineSegment(sketch, "E2160", {"start": v(21.49, -25.09) * mm, "end": v(21.33, -24.8) * mm});
            skLineSegment(sketch, "E2161", {"start": v(21.33, -24.8) * mm, "end": v(21.16, -24.68) * mm});
            skLineSegment(sketch, "E2162", {"start": v(21.16, -24.68) * mm, "end": v(21, -24.67) * mm});
            skLineSegment(sketch, "E2163", {"start": v(21, -24.67) * mm, "end": v(20.7, -24.85) * mm});
            skLineSegment(sketch, "E2164", {"start": v(20.7, -24.85) * mm, "end": v(20.3, -25.27) * mm});
            skLineSegment(sketch, "E2165", {"start": v(20.3, -25.27) * mm, "end": v(20.03, -25.7) * mm});
            skLineSegment(sketch, "E2166", {"start": v(20.03, -25.7) * mm, "end": v(19.88, -26.06) * mm});
            skLineSegment(sketch, "E2167", {"start": v(19.88, -26.06) * mm, "end": v(19.81, -26.4) * mm});
            skLineSegment(sketch, "E2168", {"start": v(19.81, -26.4) * mm, "end": v(19.83, -26.6) * mm});
            skLineSegment(sketch, "E2169", {"start": v(19.83, -26.6) * mm, "end": v(19.93, -26.77) * mm});
            skLineSegment(sketch, "E2170", {"start": v(19.93, -26.77) * mm, "end": v(20.1, -26.88) * mm});
            skLineSegment(sketch, "E2171", {"start": v(20.1, -26.88) * mm, "end": v(20.35, -26.93) * mm});
            skLineSegment(sketch, "E2172", {"start": v(20.35, -26.93) * mm, "end": v(20.74, -26.86) * mm});
            skLineSegment(sketch, "E2173", {"start": v(20.74, -26.86) * mm, "end": v(21.08, -26.61) * mm});
            skLineSegment(sketch, "E2174", {"start": v(21.08, -26.61) * mm, "end": v(21.43, -26.11) * mm});
            skLineSegment(sketch, "E2175", {"start": v(-4.28, 21.47) * mm, "end": v(-2.5, 21.12) * mm});
            skLineSegment(sketch, "E2176", {"start": v(-2.5, 21.12) * mm, "end": v(-0.73, 20.73) * mm});
            skLineSegment(sketch, "E2177", {"start": v(-0.73, 20.73) * mm, "end": v(-0.06, 20.66) * mm});
            skLineSegment(sketch, "E2178", {"start": v(-0.06, 20.66) * mm, "end": v(0.16, 20.82) * mm});
            skLineSegment(sketch, "E2179", {"start": v(0.16, 20.82) * mm, "end": v(0.22, 21.14) * mm});
            skLineSegment(sketch, "E2180", {"start": v(0.22, 21.14) * mm, "end": v(0.16, 21.8) * mm});
            skLineSegment(sketch, "E2181", {"start": v(0.16, 21.8) * mm, "end": v(-0.04, 22.38) * mm});
            skLineSegment(sketch, "E2182", {"start": v(-0.04, 22.38) * mm, "end": v(-0.58, 23.04) * mm});
            skLineSegment(sketch, "E2183", {"start": v(-0.58, 23.04) * mm, "end": v(-1.5, 23.7) * mm});
            skLineSegment(sketch, "E2184", {"start": v(-1.5, 23.7) * mm, "end": v(-2.87, 24.5) * mm});
            skLineSegment(sketch, "E2185", {"start": v(-2.87, 24.5) * mm, "end": v(-3.8, 25.08) * mm});
            skLineSegment(sketch, "E2186", {"start": v(-3.8, 25.08) * mm, "end": v(-4.45, 25.62) * mm});
            skLineSegment(sketch, "E2187", {"start": v(-4.45, 25.62) * mm, "end": v(-4.78, 25.81) * mm});
            skLineSegment(sketch, "E2188", {"start": v(-4.78, 25.81) * mm, "end": v(-5.19, 25.82) * mm});
            skLineSegment(sketch, "E2189", {"start": v(-5.19, 25.82) * mm, "end": v(-5.47, 25.6) * mm});
            skLineSegment(sketch, "E2190", {"start": v(-5.47, 25.6) * mm, "end": v(-5.8, 25.03) * mm});
            skLineSegment(sketch, "E2191", {"start": v(-5.8, 25.03) * mm, "end": v(-5.99, 24.42) * mm});
            skLineSegment(sketch, "E2192", {"start": v(-5.99, 24.42) * mm, "end": v(-6.08, 23.88) * mm});
            skLineSegment(sketch, "E2193", {"start": v(-6.08, 23.88) * mm, "end": v(-6.11, 22.82) * mm});
            skLineSegment(sketch, "E2194", {"start": v(-6.11, 22.82) * mm, "end": v(-5.98, 22.18) * mm});
            skLineSegment(sketch, "E2195", {"start": v(-5.98, 22.18) * mm, "end": v(-5.72, 21.8) * mm});
            skLineSegment(sketch, "E2196", {"start": v(-5.72, 21.8) * mm, "end": v(-5.28, 21.59) * mm});
            skLineSegment(sketch, "E2197", {"start": v(-5.28, 21.59) * mm, "end": v(-4.78, 21.52) * mm});
            skLineSegment(sketch, "E2198", {"start": v(-4.78, 21.52) * mm, "end": v(-4.28, 21.47) * mm});
            skLineSegment(sketch, "E2199", {"start": v(-0.72, 16.44) * mm, "end": v(2.57, 16.85) * mm});
            skLineSegment(sketch, "E2200", {"start": v(2.57, 16.85) * mm, "end": v(3.65, 16.94) * mm});
            skLineSegment(sketch, "E2201", {"start": v(3.65, 16.94) * mm, "end": v(4.8, 16.89) * mm});
            skLineSegment(sketch, "E2202", {"start": v(4.8, 16.89) * mm, "end": v(5.23, 16.9) * mm});
            skLineSegment(sketch, "E2203", {"start": v(5.23, 16.9) * mm, "end": v(5.56, 17.03) * mm});
            skLineSegment(sketch, "E2204", {"start": v(5.56, 17.03) * mm, "end": v(5.6, 17.26) * mm});
            skLineSegment(sketch, "E2205", {"start": v(5.6, 17.26) * mm, "end": v(5.46, 17.67) * mm});
            skLineSegment(sketch, "E2206", {"start": v(5.46, 17.67) * mm, "end": v(5.12, 18.17) * mm});
            skLineSegment(sketch, "E2207", {"start": v(5.12, 18.17) * mm, "end": v(4.54, 18.78) * mm});
            skLineSegment(sketch, "E2208", {"start": v(4.54, 18.78) * mm, "end": v(4.11, 18.96) * mm});
            skLineSegment(sketch, "E2209", {"start": v(4.11, 18.96) * mm, "end": v(3.66, 18.9) * mm});
            skLineSegment(sketch, "E2210", {"start": v(3.66, 18.9) * mm, "end": v(3.29, 18.72) * mm});
            skLineSegment(sketch, "E2211", {"start": v(3.29, 18.72) * mm, "end": v(2.65, 18.37) * mm});
            skLineSegment(sketch, "E2212", {"start": v(2.65, 18.37) * mm, "end": v(2.27, 18.28) * mm});
            skLineSegment(sketch, "E2213", {"start": v(2.27, 18.28) * mm, "end": v(1.86, 18.4) * mm});
            skLineSegment(sketch, "E2214", {"start": v(1.86, 18.4) * mm, "end": v(1.26, 18.98) * mm});
            skLineSegment(sketch, "E2215", {"start": v(1.26, 18.98) * mm, "end": v(0.7, 19.5) * mm});
            skLineSegment(sketch, "E2216", {"start": v(0.7, 19.5) * mm, "end": v(-0.29, 19.86) * mm});
            skLineSegment(sketch, "E2217", {"start": v(-0.29, 19.86) * mm, "end": v(-1.86, 20.07) * mm});
            skLineSegment(sketch, "E2218", {"start": v(-1.86, 20.07) * mm, "end": v(-3.03, 20.12) * mm});
            skLineSegment(sketch, "E2219", {"start": v(-3.03, 20.12) * mm, "end": v(-4.13, 20.2) * mm});
            skLineSegment(sketch, "E2220", {"start": v(-4.13, 20.2) * mm, "end": v(-4.77, 20.25) * mm});
            skLineSegment(sketch, "E2221", {"start": v(-4.77, 20.25) * mm, "end": v(-5.23, 20.1) * mm});
            skLineSegment(sketch, "E2222", {"start": v(-5.23, 20.1) * mm, "end": v(-5.36, 19.74) * mm});
            skLineSegment(sketch, "E2223", {"start": v(-5.36, 19.74) * mm, "end": v(-5.3, 19.23) * mm});
            skLineSegment(sketch, "E2224", {"start": v(-5.3, 19.23) * mm, "end": v(-4.98, 18.33) * mm});
            skLineSegment(sketch, "E2225", {"start": v(-4.98, 18.33) * mm, "end": v(-4.36, 17.1) * mm});
            skLineSegment(sketch, "E2226", {"start": v(-4.36, 17.1) * mm, "end": v(-3.97, 16.6) * mm});
            skLineSegment(sketch, "E2227", {"start": v(-3.97, 16.6) * mm, "end": v(-3.41, 16.21) * mm});
            skLineSegment(sketch, "E2228", {"start": v(-3.41, 16.21) * mm, "end": v(-2.78, 16.13) * mm});
            skLineSegment(sketch, "E2229", {"start": v(-2.78, 16.13) * mm, "end": v(-1.95, 16.2) * mm});
            skLineSegment(sketch, "E2230", {"start": v(-1.95, 16.2) * mm, "end": v(-0.72, 16.44) * mm});
            skLineSegment(sketch, "E2231", {"start": v(4.1, 11.62) * mm, "end": v(5.57, 12.09) * mm});
            skLineSegment(sketch, "E2232", {"start": v(5.57, 12.09) * mm, "end": v(6.8, 12.4) * mm});
            skLineSegment(sketch, "E2233", {"start": v(6.8, 12.4) * mm, "end": v(7.9, 12.5) * mm});
            skLineSegment(sketch, "E2234", {"start": v(7.9, 12.5) * mm, "end": v(8.66, 12.56) * mm});
            skLineSegment(sketch, "E2235", {"start": v(8.66, 12.56) * mm, "end": v(9.04, 12.72) * mm});
            skLineSegment(sketch, "E2236", {"start": v(9.04, 12.72) * mm, "end": v(9.16, 12.95) * mm});
            skLineSegment(sketch, "E2237", {"start": v(9.16, 12.95) * mm, "end": v(9, 13.41) * mm});
            skLineSegment(sketch, "E2238", {"start": v(9, 13.41) * mm, "end": v(8.6, 13.9) * mm});
            skLineSegment(sketch, "E2239", {"start": v(8.6, 13.9) * mm, "end": v(8.06, 14.35) * mm});
            skLineSegment(sketch, "E2240", {"start": v(8.06, 14.35) * mm, "end": v(7.6, 14.63) * mm});
            skLineSegment(sketch, "E2241", {"start": v(7.6, 14.63) * mm, "end": v(7.1, 14.82) * mm});
            skLineSegment(sketch, "E2242", {"start": v(7.1, 14.82) * mm, "end": v(5.5, 15) * mm});
            skLineSegment(sketch, "E2243", {"start": v(5.5, 15) * mm, "end": v(4.25, 15.17) * mm});
            skLineSegment(sketch, "E2244", {"start": v(4.25, 15.17) * mm, "end": v(2.86, 15.34) * mm});
            skLineSegment(sketch, "E2245", {"start": v(2.86, 15.34) * mm, "end": v(1.35, 15.47) * mm});
            skLineSegment(sketch, "E2246", {"start": v(1.35, 15.47) * mm, "end": v(-0.19, 15.48) * mm});
            skLineSegment(sketch, "E2247", {"start": v(-0.19, 15.48) * mm, "end": v(-1.7, 15.36) * mm});
            skLineSegment(sketch, "E2248", {"start": v(-1.7, 15.36) * mm, "end": v(-2.2, 15.28) * mm});
            skLineSegment(sketch, "E2249", {"start": v(-2.2, 15.28) * mm, "end": v(-2.48, 15.1) * mm});
            skLineSegment(sketch, "E2250", {"start": v(-2.48, 15.1) * mm, "end": v(-2.53, 14.9) * mm});
            skLineSegment(sketch, "E2251", {"start": v(-2.53, 14.9) * mm, "end": v(-2.35, 14.46) * mm});
            skLineSegment(sketch, "E2252", {"start": v(-2.35, 14.46) * mm, "end": v(-1.55, 13.53) * mm});
            skLineSegment(sketch, "E2253", {"start": v(-1.55, 13.53) * mm, "end": v(-0.44, 12.22) * mm});
            skLineSegment(sketch, "E2254", {"start": v(-0.44, 12.22) * mm, "end": v(0.34, 11.5) * mm});
            skLineSegment(sketch, "E2255", {"start": v(0.34, 11.5) * mm, "end": v(0.95, 11.14) * mm});
            skLineSegment(sketch, "E2256", {"start": v(0.95, 11.14) * mm, "end": v(1.34, 11.05) * mm});
            skLineSegment(sketch, "E2257", {"start": v(1.34, 11.05) * mm, "end": v(2.15, 11.12) * mm});
            skLineSegment(sketch, "E2258", {"start": v(2.15, 11.12) * mm, "end": v(3.12, 11.33) * mm});
            skLineSegment(sketch, "E2259", {"start": v(3.12, 11.33) * mm, "end": v(4.1, 11.62) * mm});
            skLineSegment(sketch, "E2260", {"start": v(8.42, 7.3) * mm, "end": v(10.33, 7.7) * mm});
            skLineSegment(sketch, "E2261", {"start": v(10.33, 7.7) * mm, "end": v(11.27, 7.84) * mm});
            skLineSegment(sketch, "E2262", {"start": v(11.27, 7.84) * mm, "end": v(12.22, 7.9) * mm});
            skLineSegment(sketch, "E2263", {"start": v(12.22, 7.9) * mm, "end": v(12.76, 8) * mm});
            skLineSegment(sketch, "E2264", {"start": v(12.76, 8) * mm, "end": v(13.14, 8.21) * mm});
            skLineSegment(sketch, "E2265", {"start": v(13.14, 8.21) * mm, "end": v(13.18, 8.47) * mm});
            skLineSegment(sketch, "E2266", {"start": v(13.18, 8.47) * mm, "end": v(13.06, 8.77) * mm});
            skLineSegment(sketch, "E2267", {"start": v(13.06, 8.77) * mm, "end": v(12.53, 9.36) * mm});
            skLineSegment(sketch, "E2268", {"start": v(12.53, 9.36) * mm, "end": v(11.58, 10.27) * mm});
            skLineSegment(sketch, "E2269", {"start": v(11.58, 10.27) * mm, "end": v(11.12, 10.65) * mm});
            skLineSegment(sketch, "E2270", {"start": v(11.12, 10.65) * mm, "end": v(10.44, 11.05) * mm});
            skLineSegment(sketch, "E2271", {"start": v(10.44, 11.05) * mm, "end": v(9.82, 11.27) * mm});
            skLineSegment(sketch, "E2272", {"start": v(9.82, 11.27) * mm, "end": v(9.12, 11.36) * mm});
            skLineSegment(sketch, "E2273", {"start": v(9.12, 11.36) * mm, "end": v(8.46, 11.35) * mm});
            skLineSegment(sketch, "E2274", {"start": v(8.46, 11.35) * mm, "end": v(7.66, 11.24) * mm});
            skLineSegment(sketch, "E2275", {"start": v(7.66, 11.24) * mm, "end": v(5.75, 10.9) * mm});
            skLineSegment(sketch, "E2276", {"start": v(5.75, 10.9) * mm, "end": v(4.1, 10.53) * mm});
            skLineSegment(sketch, "E2277", {"start": v(4.1, 10.53) * mm, "end": v(3.22, 10.33) * mm});
            skLineSegment(sketch, "E2278", {"start": v(3.22, 10.33) * mm, "end": v(2.73, 10.13) * mm});
            skLineSegment(sketch, "E2279", {"start": v(2.73, 10.13) * mm, "end": v(2.57, 9.97) * mm});
            skLineSegment(sketch, "E2280", {"start": v(2.57, 9.97) * mm, "end": v(2.51, 9.78) * mm});
            skLineSegment(sketch, "E2281", {"start": v(2.51, 9.78) * mm, "end": v(2.57, 9.58) * mm});
            skLineSegment(sketch, "E2282", {"start": v(2.57, 9.58) * mm, "end": v(2.87, 9.2) * mm});
            skLineSegment(sketch, "E2283", {"start": v(2.87, 9.2) * mm, "end": v(3.97, 8.17) * mm});
            skLineSegment(sketch, "E2284", {"start": v(3.97, 8.17) * mm, "end": v(4.5, 7.72) * mm});
            skLineSegment(sketch, "E2285", {"start": v(4.5, 7.72) * mm, "end": v(4.94, 7.4) * mm});
            skLineSegment(sketch, "E2286", {"start": v(4.94, 7.4) * mm, "end": v(5.39, 7.14) * mm});
            skLineSegment(sketch, "E2287", {"start": v(5.39, 7.14) * mm, "end": v(5.93, 6.98) * mm});
            skLineSegment(sketch, "E2288", {"start": v(5.93, 6.98) * mm, "end": v(6.26, 6.98) * mm});
            skLineSegment(sketch, "E2289", {"start": v(6.26, 6.98) * mm, "end": v(7.02, 7.06) * mm});
            skLineSegment(sketch, "E2290", {"start": v(7.02, 7.06) * mm, "end": v(8.42, 7.3) * mm});
            skLineSegment(sketch, "E2291", {"start": v(13.38, 2.07) * mm, "end": v(15.42, 2.54) * mm});
            skLineSegment(sketch, "E2292", {"start": v(15.42, 2.54) * mm, "end": v(16.01, 2.66) * mm});
            skLineSegment(sketch, "E2293", {"start": v(16.01, 2.66) * mm, "end": v(16.78, 2.75) * mm});
            skLineSegment(sketch, "E2294", {"start": v(16.78, 2.75) * mm, "end": v(17.13, 2.86) * mm});
            skLineSegment(sketch, "E2295", {"start": v(17.13, 2.86) * mm, "end": v(17.26, 2.99) * mm});
            skLineSegment(sketch, "E2296", {"start": v(17.26, 2.99) * mm, "end": v(17.28, 3.17) * mm});
            skLineSegment(sketch, "E2297", {"start": v(17.28, 3.17) * mm, "end": v(17.2, 3.37) * mm});
            skLineSegment(sketch, "E2298", {"start": v(17.2, 3.37) * mm, "end": v(16.98, 3.7) * mm});
            skLineSegment(sketch, "E2299", {"start": v(16.98, 3.7) * mm, "end": v(16.59, 4.12) * mm});
            skLineSegment(sketch, "E2300", {"start": v(16.59, 4.12) * mm, "end": v(16.26, 4.45) * mm});
            skLineSegment(sketch, "E2301", {"start": v(16.26, 4.45) * mm, "end": v(15.65, 5.14) * mm});
            skLineSegment(sketch, "E2302", {"start": v(15.65, 5.14) * mm, "end": v(14.88, 5.91) * mm});
            skLineSegment(sketch, "E2303", {"start": v(14.88, 5.91) * mm, "end": v(14.27, 6.35) * mm});
            skLineSegment(sketch, "E2304", {"start": v(14.27, 6.35) * mm, "end": v(13.61, 6.66) * mm});
            skLineSegment(sketch, "E2305", {"start": v(13.61, 6.66) * mm, "end": v(13.07, 6.78) * mm});
            skLineSegment(sketch, "E2306", {"start": v(13.07, 6.78) * mm, "end": v(12.34, 6.82) * mm});
            skLineSegment(sketch, "E2307", {"start": v(12.34, 6.82) * mm, "end": v(11.63, 6.77) * mm});
            skLineSegment(sketch, "E2308", {"start": v(11.63, 6.77) * mm, "end": v(10.67, 6.64) * mm});
            skLineSegment(sketch, "E2309", {"start": v(10.67, 6.64) * mm, "end": v(9.58, 6.46) * mm});
            skLineSegment(sketch, "E2310", {"start": v(9.58, 6.46) * mm, "end": v(8.74, 6.27) * mm});
            skLineSegment(sketch, "E2311", {"start": v(8.74, 6.27) * mm, "end": v(8.37, 6.14) * mm});
            skLineSegment(sketch, "E2312", {"start": v(8.37, 6.14) * mm, "end": v(7.78, 5.83) * mm});
            skLineSegment(sketch, "E2313", {"start": v(7.78, 5.83) * mm, "end": v(7.57, 5.57) * mm});
            skLineSegment(sketch, "E2314", {"start": v(7.57, 5.57) * mm, "end": v(7.58, 5.26) * mm});
            skLineSegment(sketch, "E2315", {"start": v(7.58, 5.26) * mm, "end": v(7.77, 4.95) * mm});
            skLineSegment(sketch, "E2316", {"start": v(7.77, 4.95) * mm, "end": v(8.14, 4.6) * mm});
            skLineSegment(sketch, "E2317", {"start": v(8.14, 4.6) * mm, "end": v(8.5, 4.28) * mm});
            skLineSegment(sketch, "E2318", {"start": v(8.5, 4.28) * mm, "end": v(9.13, 3.57) * mm});
            skLineSegment(sketch, "E2319", {"start": v(9.13, 3.57) * mm, "end": v(10.15, 2.48) * mm});
            skLineSegment(sketch, "E2320", {"start": v(10.15, 2.48) * mm, "end": v(10.64, 2.09) * mm});
            skLineSegment(sketch, "E2321", {"start": v(10.64, 2.09) * mm, "end": v(11.12, 1.84) * mm});
            skLineSegment(sketch, "E2322", {"start": v(11.12, 1.84) * mm, "end": v(11.41, 1.77) * mm});
            skLineSegment(sketch, "E2323", {"start": v(11.41, 1.77) * mm, "end": v(11.97, 1.81) * mm});
            skLineSegment(sketch, "E2324", {"start": v(11.97, 1.81) * mm, "end": v(12.6, 1.91) * mm});
            skLineSegment(sketch, "E2325", {"start": v(12.6, 1.91) * mm, "end": v(13.38, 2.07) * mm});
            skLineSegment(sketch, "E2326", {"start": v(17.7, -3.45) * mm, "end": v(18.84, -3.19) * mm});
            skLineSegment(sketch, "E2327", {"start": v(18.84, -3.19) * mm, "end": v(19.6, -3.05) * mm});
            skLineSegment(sketch, "E2328", {"start": v(19.6, -3.05) * mm, "end": v(20.47, -3) * mm});
            skLineSegment(sketch, "E2329", {"start": v(20.47, -3) * mm, "end": v(21.04, -2.82) * mm});
            skLineSegment(sketch, "E2330", {"start": v(21.04, -2.82) * mm, "end": v(21.2, -2.55) * mm});
            skLineSegment(sketch, "E2331", {"start": v(21.2, -2.55) * mm, "end": v(21.18, -2.09) * mm});
            skLineSegment(sketch, "E2332", {"start": v(21.18, -2.09) * mm, "end": v(20.85, -1.28) * mm});
            skLineSegment(sketch, "E2333", {"start": v(20.85, -1.28) * mm, "end": v(20.09, 0.12) * mm});
            skLineSegment(sketch, "E2334", {"start": v(20.09, 0.12) * mm, "end": v(19.59, 0.82) * mm});
            skLineSegment(sketch, "E2335", {"start": v(19.59, 0.82) * mm, "end": v(19.17, 1.23) * mm});
            skLineSegment(sketch, "E2336", {"start": v(19.17, 1.23) * mm, "end": v(18.8, 1.48) * mm});
            skLineSegment(sketch, "E2337", {"start": v(18.8, 1.48) * mm, "end": v(18.4, 1.63) * mm});
            skLineSegment(sketch, "E2338", {"start": v(18.4, 1.63) * mm, "end": v(17.88, 1.67) * mm});
            skLineSegment(sketch, "E2339", {"start": v(17.88, 1.67) * mm, "end": v(17.05, 1.58) * mm});
            skLineSegment(sketch, "E2340", {"start": v(17.05, 1.58) * mm, "end": v(16.04, 1.48) * mm});
            skLineSegment(sketch, "E2341", {"start": v(16.04, 1.48) * mm, "end": v(14.9, 1.35) * mm});
            skLineSegment(sketch, "E2342", {"start": v(14.9, 1.35) * mm, "end": v(13.53, 1.1) * mm});
            skLineSegment(sketch, "E2343", {"start": v(13.53, 1.1) * mm, "end": v(12.88, 0.97) * mm});
            skLineSegment(sketch, "E2344", {"start": v(12.88, 0.97) * mm, "end": v(12.41, 0.77) * mm});
            skLineSegment(sketch, "E2345", {"start": v(12.41, 0.77) * mm, "end": v(12.21, 0.52) * mm});
            skLineSegment(sketch, "E2346", {"start": v(12.21, 0.52) * mm, "end": v(12.24, 0.2) * mm});
            skLineSegment(sketch, "E2347", {"start": v(12.24, 0.2) * mm, "end": v(12.4, -0.13) * mm});
            skLineSegment(sketch, "E2348", {"start": v(12.4, -0.13) * mm, "end": v(12.92, -0.85) * mm});
            skLineSegment(sketch, "E2349", {"start": v(12.92, -0.85) * mm, "end": v(13.3, -1.54) * mm});
            skLineSegment(sketch, "E2350", {"start": v(13.3, -1.54) * mm, "end": v(14.14, -2.97) * mm});
            skLineSegment(sketch, "E2351", {"start": v(14.14, -2.97) * mm, "end": v(14.53, -3.42) * mm});
            skLineSegment(sketch, "E2352", {"start": v(14.53, -3.42) * mm, "end": v(14.87, -3.68) * mm});
            skLineSegment(sketch, "E2353", {"start": v(14.87, -3.68) * mm, "end": v(15.39, -3.84) * mm});
            skLineSegment(sketch, "E2354", {"start": v(15.39, -3.84) * mm, "end": v(16.05, -3.79) * mm});
            skLineSegment(sketch, "E2355", {"start": v(16.05, -3.79) * mm, "end": v(16.68, -3.68) * mm});
            skLineSegment(sketch, "E2356", {"start": v(16.68, -3.68) * mm, "end": v(17.7, -3.45) * mm});
            skLineSegment(sketch, "E2357", {"start": v(19.6, -11.14) * mm, "end": v(20.62, -11.17) * mm});
            skLineSegment(sketch, "E2358", {"start": v(20.62, -11.17) * mm, "end": v(21.64, -11.1) * mm});
            skLineSegment(sketch, "E2359", {"start": v(21.64, -11.1) * mm, "end": v(22.35, -10.95) * mm});
            skLineSegment(sketch, "E2360", {"start": v(22.35, -10.95) * mm, "end": v(22.75, -10.67) * mm});
            skLineSegment(sketch, "E2361", {"start": v(22.75, -10.67) * mm, "end": v(22.94, -10.27) * mm});
            skLineSegment(sketch, "E2362", {"start": v(22.94, -10.27) * mm, "end": v(23, -9.57) * mm});
            skLineSegment(sketch, "E2363", {"start": v(23, -9.57) * mm, "end": v(22.8, -8.16) * mm});
            skLineSegment(sketch, "E2364", {"start": v(22.8, -8.16) * mm, "end": v(22.63, -6.63) * mm});
            skLineSegment(sketch, "E2365", {"start": v(22.63, -6.63) * mm, "end": v(22.4, -5.74) * mm});
            skLineSegment(sketch, "E2366", {"start": v(22.4, -5.74) * mm, "end": v(22.15, -5.26) * mm});
            skLineSegment(sketch, "E2367", {"start": v(22.15, -5.26) * mm, "end": v(21.8, -4.88) * mm});
            skLineSegment(sketch, "E2368", {"start": v(21.8, -4.88) * mm, "end": v(21.31, -4.63) * mm});
            skLineSegment(sketch, "E2369", {"start": v(21.31, -4.63) * mm, "end": v(20.8, -4.52) * mm});
            skLineSegment(sketch, "E2370", {"start": v(20.8, -4.52) * mm, "end": v(20.29, -4.52) * mm});
            skLineSegment(sketch, "E2371", {"start": v(20.29, -4.52) * mm, "end": v(19.77, -4.57) * mm});
            skLineSegment(sketch, "E2372", {"start": v(19.77, -4.57) * mm, "end": v(18.75, -4.65) * mm});
            skLineSegment(sketch, "E2373", {"start": v(18.75, -4.65) * mm, "end": v(17.77, -4.74) * mm});
            skLineSegment(sketch, "E2374", {"start": v(17.77, -4.74) * mm, "end": v(16.8, -4.9) * mm});
            skLineSegment(sketch, "E2375", {"start": v(16.8, -4.9) * mm, "end": v(16.33, -5.05) * mm});
            skLineSegment(sketch, "E2376", {"start": v(16.33, -5.05) * mm, "end": v(15.86, -5.3) * mm});
            skLineSegment(sketch, "E2377", {"start": v(15.86, -5.3) * mm, "end": v(15.61, -5.66) * mm});
            skLineSegment(sketch, "E2378", {"start": v(15.61, -5.66) * mm, "end": v(15.62, -5.98) * mm});
            skLineSegment(sketch, "E2379", {"start": v(15.62, -5.98) * mm, "end": v(15.76, -6.5) * mm});
            skLineSegment(sketch, "E2380", {"start": v(15.76, -6.5) * mm, "end": v(16.02, -7.16) * mm});
            skLineSegment(sketch, "E2381", {"start": v(16.02, -7.16) * mm, "end": v(16.2, -7.74) * mm});
            skLineSegment(sketch, "E2382", {"start": v(16.2, -7.74) * mm, "end": v(16.44, -9.17) * mm});
            skLineSegment(sketch, "E2383", {"start": v(16.44, -9.17) * mm, "end": v(16.66, -10.1) * mm});
            skLineSegment(sketch, "E2384", {"start": v(16.66, -10.1) * mm, "end": v(16.96, -10.7) * mm});
            skLineSegment(sketch, "E2385", {"start": v(16.96, -10.7) * mm, "end": v(17.34, -10.94) * mm});
            skLineSegment(sketch, "E2386", {"start": v(17.34, -10.94) * mm, "end": v(17.97, -11) * mm});
            skLineSegment(sketch, "E2387", {"start": v(17.97, -11) * mm, "end": v(18.34, -11.02) * mm});
            skLineSegment(sketch, "E2388", {"start": v(18.34, -11.02) * mm, "end": v(18.83, -11.07) * mm});
            skLineSegment(sketch, "E2389", {"start": v(18.83, -11.07) * mm, "end": v(19.6, -11.14) * mm});
            skLineSegment(sketch, "E2390", {"start": v(18.01, -18.82) * mm, "end": v(19.32, -18.55) * mm});
            skLineSegment(sketch, "E2391", {"start": v(19.32, -18.55) * mm, "end": v(20.38, -18.2) * mm});
            skLineSegment(sketch, "E2392", {"start": v(20.38, -18.2) * mm, "end": v(21.42, -17.65) * mm});
            skLineSegment(sketch, "E2393", {"start": v(21.42, -17.65) * mm, "end": v(21.97, -17.12) * mm});
            skLineSegment(sketch, "E2394", {"start": v(21.97, -17.12) * mm, "end": v(22.4, -16.14) * mm});
            skLineSegment(sketch, "E2395", {"start": v(22.4, -16.14) * mm, "end": v(22.77, -14.84) * mm});
            skLineSegment(sketch, "E2396", {"start": v(22.77, -14.84) * mm, "end": v(22.92, -13.62) * mm});
            skLineSegment(sketch, "E2397", {"start": v(22.92, -13.62) * mm, "end": v(22.82, -12.88) * mm});
            skLineSegment(sketch, "E2398", {"start": v(22.82, -12.88) * mm, "end": v(22.64, -12.52) * mm});
            skLineSegment(sketch, "E2399", {"start": v(22.64, -12.52) * mm, "end": v(22.35, -12.27) * mm});
            skLineSegment(sketch, "E2400", {"start": v(22.35, -12.27) * mm, "end": v(21.94, -12.16) * mm});
            skLineSegment(sketch, "E2401", {"start": v(21.94, -12.16) * mm, "end": v(21.12, -12.25) * mm});
            skLineSegment(sketch, "E2402", {"start": v(21.12, -12.25) * mm, "end": v(20.11, -12.38) * mm});
            skLineSegment(sketch, "E2403", {"start": v(20.11, -12.38) * mm, "end": v(19.1, -12.48) * mm});
            skLineSegment(sketch, "E2404", {"start": v(19.1, -12.48) * mm, "end": v(18.23, -12.5) * mm});
            skLineSegment(sketch, "E2405", {"start": v(18.23, -12.5) * mm, "end": v(17.67, -12.49) * mm});
            skLineSegment(sketch, "E2406", {"start": v(17.67, -12.49) * mm, "end": v(17.26, -12.58) * mm});
            skLineSegment(sketch, "E2407", {"start": v(17.26, -12.58) * mm, "end": v(17.02, -12.8) * mm});
            skLineSegment(sketch, "E2408", {"start": v(17.02, -12.8) * mm, "end": v(16.93, -13.15) * mm});
            skLineSegment(sketch, "E2409", {"start": v(16.93, -13.15) * mm, "end": v(16.9, -13.67) * mm});
            skLineSegment(sketch, "E2410", {"start": v(16.9, -13.67) * mm, "end": v(16.86, -14.16) * mm});
            skLineSegment(sketch, "E2411", {"start": v(16.86, -14.16) * mm, "end": v(16.63, -15.7) * mm});
            skLineSegment(sketch, "E2412", {"start": v(16.63, -15.7) * mm, "end": v(16.3, -17.2) * mm});
            skLineSegment(sketch, "E2413", {"start": v(16.3, -17.2) * mm, "end": v(15.98, -18.17) * mm});
            skLineSegment(sketch, "E2414", {"start": v(15.98, -18.17) * mm, "end": v(15.92, -18.55) * mm});
            skLineSegment(sketch, "E2415", {"start": v(15.92, -18.55) * mm, "end": v(15.96, -18.72) * mm});
            skLineSegment(sketch, "E2416", {"start": v(15.96, -18.72) * mm, "end": v(16.09, -18.82) * mm});
            skLineSegment(sketch, "E2417", {"start": v(16.09, -18.82) * mm, "end": v(16.42, -18.9) * mm});
            skLineSegment(sketch, "E2418", {"start": v(16.42, -18.9) * mm, "end": v(17, -18.9) * mm});
            skLineSegment(sketch, "E2419", {"start": v(17, -18.9) * mm, "end": v(18.01, -18.82) * mm});
            skLineSegment(sketch, "E2420", {"start": v(15.03, -24.16) * mm, "end": v(15.86, -24.12) * mm});
            skLineSegment(sketch, "E2421", {"start": v(15.86, -24.12) * mm, "end": v(16.88, -24.02) * mm});
            skLineSegment(sketch, "E2422", {"start": v(16.88, -24.02) * mm, "end": v(17.92, -23.81) * mm});
            skLineSegment(sketch, "E2423", {"start": v(17.92, -23.81) * mm, "end": v(18.62, -23.54) * mm});
            skLineSegment(sketch, "E2424", {"start": v(18.62, -23.54) * mm, "end": v(19.23, -23.06) * mm});
            skLineSegment(sketch, "E2425", {"start": v(19.23, -23.06) * mm, "end": v(19.83, -22.25) * mm});
            skLineSegment(sketch, "E2426", {"start": v(19.83, -22.25) * mm, "end": v(20.54, -21.05) * mm});
            skLineSegment(sketch, "E2427", {"start": v(20.54, -21.05) * mm, "end": v(20.87, -20.23) * mm});
            skLineSegment(sketch, "E2428", {"start": v(20.87, -20.23) * mm, "end": v(20.95, -19.75) * mm});
            skLineSegment(sketch, "E2429", {"start": v(20.95, -19.75) * mm, "end": v(20.9, -19.5) * mm});
            skLineSegment(sketch, "E2430", {"start": v(20.9, -19.5) * mm, "end": v(20.8, -19.35) * mm});
            skLineSegment(sketch, "E2431", {"start": v(20.8, -19.35) * mm, "end": v(20.6, -19.2) * mm});
            skLineSegment(sketch, "E2432", {"start": v(20.6, -19.2) * mm, "end": v(20.38, -19.15) * mm});
            skLineSegment(sketch, "E2433", {"start": v(20.38, -19.15) * mm, "end": v(20.09, -19.15) * mm});
            skLineSegment(sketch, "E2434", {"start": v(20.09, -19.15) * mm, "end": v(19.32, -19.22) * mm});
            skLineSegment(sketch, "E2435", {"start": v(19.32, -19.22) * mm, "end": v(18.55, -19.26) * mm});
            skLineSegment(sketch, "E2436", {"start": v(18.55, -19.26) * mm, "end": v(17.71, -19.31) * mm});
            skLineSegment(sketch, "E2437", {"start": v(17.71, -19.31) * mm, "end": v(17.02, -19.39) * mm});
            skLineSegment(sketch, "E2438", {"start": v(17.02, -19.39) * mm, "end": v(16.61, -19.45) * mm});
            skLineSegment(sketch, "E2439", {"start": v(16.61, -19.45) * mm, "end": v(16, -19.6) * mm});
            skLineSegment(sketch, "E2440", {"start": v(16, -19.6) * mm, "end": v(15.56, -19.75) * mm});
            skLineSegment(sketch, "E2441", {"start": v(15.56, -19.75) * mm, "end": v(15.2, -19.97) * mm});
            skLineSegment(sketch, "E2442", {"start": v(15.2, -19.97) * mm, "end": v(14.86, -20.28) * mm});
            skLineSegment(sketch, "E2443", {"start": v(14.86, -20.28) * mm, "end": v(14.48, -20.79) * mm});
            skLineSegment(sketch, "E2444", {"start": v(14.48, -20.79) * mm, "end": v(13.91, -21.7) * mm});
            skLineSegment(sketch, "E2445", {"start": v(13.91, -21.7) * mm, "end": v(13.51, -22.37) * mm});
            skLineSegment(sketch, "E2446", {"start": v(13.51, -22.37) * mm, "end": v(13.18, -22.85) * mm});
            skLineSegment(sketch, "E2447", {"start": v(13.18, -22.85) * mm, "end": v(12.96, -23.16) * mm});
            skLineSegment(sketch, "E2448", {"start": v(12.96, -23.16) * mm, "end": v(12.89, -23.5) * mm});
            skLineSegment(sketch, "E2449", {"start": v(12.89, -23.5) * mm, "end": v(13, -23.75) * mm});
            skLineSegment(sketch, "E2450", {"start": v(13, -23.75) * mm, "end": v(13.38, -23.95) * mm});
            skLineSegment(sketch, "E2451", {"start": v(13.38, -23.95) * mm, "end": v(13.92, -24.08) * mm});
            skLineSegment(sketch, "E2452", {"start": v(13.92, -24.08) * mm, "end": v(14.5, -24.14) * mm});
            skLineSegment(sketch, "E2453", {"start": v(14.5, -24.14) * mm, "end": v(15.03, -24.16) * mm});
            skLineSegment(sketch, "E2454", {"start": v(11.3, -27.67) * mm, "end": v(12.24, -27.96) * mm});
            skLineSegment(sketch, "E2455", {"start": v(12.24, -27.96) * mm, "end": v(13.19, -28.14) * mm});
            skLineSegment(sketch, "E2456", {"start": v(13.19, -28.14) * mm, "end": v(13.73, -28.18) * mm});
            skLineSegment(sketch, "E2457", {"start": v(13.73, -28.18) * mm, "end": v(14.12, -28.17) * mm});
            skLineSegment(sketch, "E2458", {"start": v(14.12, -28.17) * mm, "end": v(14.6, -28.1) * mm});
            skLineSegment(sketch, "E2459", {"start": v(14.6, -28.1) * mm, "end": v(14.92, -28) * mm});
            skLineSegment(sketch, "E2460", {"start": v(14.92, -28) * mm, "end": v(15.24, -27.85) * mm});
            skLineSegment(sketch, "E2461", {"start": v(15.24, -27.85) * mm, "end": v(15.65, -27.56) * mm});
            skLineSegment(sketch, "E2462", {"start": v(15.65, -27.56) * mm, "end": v(16.23, -27.01) * mm});
            skLineSegment(sketch, "E2463", {"start": v(16.23, -27.01) * mm, "end": v(17.25, -25.9) * mm});
            skLineSegment(sketch, "E2464", {"start": v(17.25, -25.9) * mm, "end": v(17.6, -25.51) * mm});
            skLineSegment(sketch, "E2465", {"start": v(17.6, -25.51) * mm, "end": v(17.7, -25.29) * mm});
            skLineSegment(sketch, "E2466", {"start": v(17.7, -25.29) * mm, "end": v(17.69, -25.18) * mm});
            skLineSegment(sketch, "E2467", {"start": v(17.69, -25.18) * mm, "end": v(17.52, -24.98) * mm});
            skLineSegment(sketch, "E2468", {"start": v(17.52, -24.98) * mm, "end": v(17.02, -24.91) * mm});
            skLineSegment(sketch, "E2469", {"start": v(17.02, -24.91) * mm, "end": v(16.3, -24.95) * mm});
            skLineSegment(sketch, "E2470", {"start": v(16.3, -24.95) * mm, "end": v(15.15, -24.96) * mm});
            skLineSegment(sketch, "E2471", {"start": v(15.15, -24.96) * mm, "end": v(14, -24.9) * mm});
            skLineSegment(sketch, "E2472", {"start": v(14, -24.9) * mm, "end": v(13.4, -24.78) * mm});
            skLineSegment(sketch, "E2473", {"start": v(13.4, -24.78) * mm, "end": v(12.8, -24.63) * mm});
            skLineSegment(sketch, "E2474", {"start": v(12.8, -24.63) * mm, "end": v(12.32, -24.58) * mm});
            skLineSegment(sketch, "E2475", {"start": v(12.32, -24.58) * mm, "end": v(11.97, -24.66) * mm});
            skLineSegment(sketch, "E2476", {"start": v(11.97, -24.66) * mm, "end": v(11.61, -24.85) * mm});
            skLineSegment(sketch, "E2477", {"start": v(11.61, -24.85) * mm, "end": v(11.4, -25.03) * mm});
            skLineSegment(sketch, "E2478", {"start": v(11.4, -25.03) * mm, "end": v(10.64, -25.75) * mm});
            skLineSegment(sketch, "E2479", {"start": v(10.64, -25.75) * mm, "end": v(10.27, -26.16) * mm});
            skLineSegment(sketch, "E2480", {"start": v(10.27, -26.16) * mm, "end": v(10.11, -26.5) * mm});
            skLineSegment(sketch, "E2481", {"start": v(10.11, -26.5) * mm, "end": v(10.1, -26.83) * mm});
            skLineSegment(sketch, "E2482", {"start": v(10.1, -26.83) * mm, "end": v(10.32, -27.13) * mm});
            skLineSegment(sketch, "E2483", {"start": v(10.32, -27.13) * mm, "end": v(10.88, -27.5) * mm});
            skLineSegment(sketch, "E2484", {"start": v(10.88, -27.5) * mm, "end": v(11.3, -27.67) * mm});
            skLineSegment(sketch, "E2485", {"start": v(11.2, -31.28) * mm, "end": v(12.07, -30.76) * mm});
            skLineSegment(sketch, "E2486", {"start": v(12.07, -30.76) * mm, "end": v(12.9, -30.15) * mm});
            skLineSegment(sketch, "E2487", {"start": v(12.9, -30.15) * mm, "end": v(13.25, -29.8) * mm});
            skLineSegment(sketch, "E2488", {"start": v(13.25, -29.8) * mm, "end": v(13.37, -29.64) * mm});
            skLineSegment(sketch, "E2489", {"start": v(13.37, -29.64) * mm, "end": v(13.46, -29.4) * mm});
            skLineSegment(sketch, "E2490", {"start": v(13.46, -29.4) * mm, "end": v(13.44, -29.25) * mm});
            skLineSegment(sketch, "E2491", {"start": v(13.44, -29.25) * mm, "end": v(13.2, -29.03) * mm});
            skLineSegment(sketch, "E2492", {"start": v(13.2, -29.03) * mm, "end": v(12.58, -28.83) * mm});
            skLineSegment(sketch, "E2493", {"start": v(12.58, -28.83) * mm, "end": v(12.13, -28.67) * mm});
            skLineSegment(sketch, "E2494", {"start": v(12.13, -28.67) * mm, "end": v(11.42, -28.35) * mm});
            skLineSegment(sketch, "E2495", {"start": v(11.42, -28.35) * mm, "end": v(10.74, -28.04) * mm});
            skLineSegment(sketch, "E2496", {"start": v(10.74, -28.04) * mm, "end": v(9.94, -27.74) * mm});
            skLineSegment(sketch, "E2497", {"start": v(9.94, -27.74) * mm, "end": v(9.47, -27.61) * mm});
            skLineSegment(sketch, "E2498", {"start": v(9.47, -27.61) * mm, "end": v(9.17, -27.58) * mm});
            skLineSegment(sketch, "E2499", {"start": v(9.17, -27.58) * mm, "end": v(9, -27.6) * mm});
            skLineSegment(sketch, "E2500", {"start": v(9, -27.6) * mm, "end": v(8.66, -27.78) * mm});
            skLineSegment(sketch, "E2501", {"start": v(8.66, -27.78) * mm, "end": v(7.76, -28.42) * mm});
            skLineSegment(sketch, "E2502", {"start": v(7.76, -28.42) * mm, "end": v(7.14, -28.93) * mm});
            skLineSegment(sketch, "E2503", {"start": v(7.14, -28.93) * mm, "end": v(6.54, -29.5) * mm});
            skLineSegment(sketch, "E2504", {"start": v(6.54, -29.5) * mm, "end": v(6.36, -29.75) * mm});
            skLineSegment(sketch, "E2505", {"start": v(6.36, -29.75) * mm, "end": v(6.3, -29.97) * mm});
            skLineSegment(sketch, "E2506", {"start": v(6.3, -29.97) * mm, "end": v(6.43, -30.26) * mm});
            skLineSegment(sketch, "E2507", {"start": v(6.43, -30.26) * mm, "end": v(6.73, -30.5) * mm});
            skLineSegment(sketch, "E2508", {"start": v(6.73, -30.5) * mm, "end": v(7.76, -31.09) * mm});
            skLineSegment(sketch, "E2509", {"start": v(7.76, -31.09) * mm, "end": v(8.57, -31.45) * mm});
            skLineSegment(sketch, "E2510", {"start": v(8.57, -31.45) * mm, "end": v(8.94, -31.57) * mm});
            skLineSegment(sketch, "E2511", {"start": v(8.94, -31.57) * mm, "end": v(9.67, -31.71) * mm});
            skLineSegment(sketch, "E2512", {"start": v(9.67, -31.71) * mm, "end": v(10.14, -31.7) * mm});
            skLineSegment(sketch, "E2513", {"start": v(10.14, -31.7) * mm, "end": v(10.72, -31.53) * mm});
            skLineSegment(sketch, "E2514", {"start": v(10.72, -31.53) * mm, "end": v(11.2, -31.28) * mm});
            skLineSegment(sketch, "E2515", {"start": v(6.9, -33.8) * mm, "end": v(7.68, -33.49) * mm});
            skLineSegment(sketch, "E2516", {"start": v(7.68, -33.49) * mm, "end": v(8.19, -33.22) * mm});
            skLineSegment(sketch, "E2517", {"start": v(8.19, -33.22) * mm, "end": v(8.38, -33.07) * mm});
            skLineSegment(sketch, "E2518", {"start": v(8.38, -33.07) * mm, "end": v(8.56, -32.84) * mm});
            skLineSegment(sketch, "E2519", {"start": v(8.56, -32.84) * mm, "end": v(8.58, -32.68) * mm});
            skLineSegment(sketch, "E2520", {"start": v(8.58, -32.68) * mm, "end": v(8.4, -32.41) * mm});
            skLineSegment(sketch, "E2521", {"start": v(8.4, -32.41) * mm, "end": v(8.08, -32.21) * mm});
            skLineSegment(sketch, "E2522", {"start": v(8.08, -32.21) * mm, "end": v(7.6, -31.98) * mm});
            skLineSegment(sketch, "E2523", {"start": v(7.6, -31.98) * mm, "end": v(7.2, -31.75) * mm});
            skLineSegment(sketch, "E2524", {"start": v(7.2, -31.75) * mm, "end": v(6.54, -31.35) * mm});
            skLineSegment(sketch, "E2525", {"start": v(6.54, -31.35) * mm, "end": v(5.85, -31) * mm});
            skLineSegment(sketch, "E2526", {"start": v(5.85, -31) * mm, "end": v(5.5, -30.9) * mm});
            skLineSegment(sketch, "E2527", {"start": v(5.5, -30.9) * mm, "end": v(5.17, -30.83) * mm});
            skLineSegment(sketch, "E2528", {"start": v(5.17, -30.83) * mm, "end": v(4.85, -30.85) * mm});
            skLineSegment(sketch, "E2529", {"start": v(4.85, -30.85) * mm, "end": v(4.62, -30.9) * mm});
            skLineSegment(sketch, "E2530", {"start": v(4.62, -30.9) * mm, "end": v(4.32, -31.04) * mm});
            skLineSegment(sketch, "E2531", {"start": v(4.32, -31.04) * mm, "end": v(3.54, -31.43) * mm});
            skLineSegment(sketch, "E2532", {"start": v(3.54, -31.43) * mm, "end": v(3.03, -31.75) * mm});
            skLineSegment(sketch, "E2533", {"start": v(3.03, -31.75) * mm, "end": v(2.73, -31.98) * mm});
            skLineSegment(sketch, "E2534", {"start": v(2.73, -31.98) * mm, "end": v(2.6, -32.13) * mm});
            skLineSegment(sketch, "E2535", {"start": v(2.6, -32.13) * mm, "end": v(2.54, -32.25) * mm});
            skLineSegment(sketch, "E2536", {"start": v(2.54, -32.25) * mm, "end": v(2.6, -32.46) * mm});
            skLineSegment(sketch, "E2537", {"start": v(2.6, -32.46) * mm, "end": v(2.82, -32.74) * mm});
            skLineSegment(sketch, "E2538", {"start": v(2.82, -32.74) * mm, "end": v(3.08, -32.95) * mm});
            skLineSegment(sketch, "E2539", {"start": v(3.08, -32.95) * mm, "end": v(3.64, -33.26) * mm});
            skLineSegment(sketch, "E2540", {"start": v(3.64, -33.26) * mm, "end": v(4.17, -33.48) * mm});
            skLineSegment(sketch, "E2541", {"start": v(4.17, -33.48) * mm, "end": v(4.58, -33.62) * mm});
            skLineSegment(sketch, "E2542", {"start": v(4.58, -33.62) * mm, "end": v(5.26, -33.8) * mm});
            skLineSegment(sketch, "E2543", {"start": v(5.26, -33.8) * mm, "end": v(5.65, -33.88) * mm});
            skLineSegment(sketch, "E2544", {"start": v(5.65, -33.88) * mm, "end": v(6, -33.92) * mm});
            skLineSegment(sketch, "E2545", {"start": v(6, -33.92) * mm, "end": v(6.3, -33.93) * mm});
            skLineSegment(sketch, "E2546", {"start": v(6.3, -33.93) * mm, "end": v(6.6, -33.89) * mm});
            skLineSegment(sketch, "E2547", {"start": v(6.6, -33.89) * mm, "end": v(6.9, -33.8) * mm});
            skLineSegment(sketch, "E2548", {"start": v(2.3, -35.73) * mm, "end": v(3.17, -35.42) * mm});
            skLineSegment(sketch, "E2549", {"start": v(3.17, -35.42) * mm, "end": v(3.88, -35.12) * mm});
            skLineSegment(sketch, "E2550", {"start": v(3.88, -35.12) * mm, "end": v(4.1, -35.02) * mm});
            skLineSegment(sketch, "E2551", {"start": v(4.1, -35.02) * mm, "end": v(4.62, -34.84) * mm});
            skLineSegment(sketch, "E2552", {"start": v(4.62, -34.84) * mm, "end": v(4.74, -34.77) * mm});
            skLineSegment(sketch, "E2553", {"start": v(4.74, -34.77) * mm, "end": v(4.88, -34.62) * mm});
            skLineSegment(sketch, "E2554", {"start": v(4.88, -34.62) * mm, "end": v(4.82, -34.49) * mm});
            skLineSegment(sketch, "E2555", {"start": v(4.82, -34.49) * mm, "end": v(4.44, -34.32) * mm});
            skLineSegment(sketch, "E2556", {"start": v(4.44, -34.32) * mm, "end": v(3.88, -34.15) * mm});
            skLineSegment(sketch, "E2557", {"start": v(3.88, -34.15) * mm, "end": v(3.12, -33.76) * mm});
            skLineSegment(sketch, "E2558", {"start": v(3.12, -33.76) * mm, "end": v(2.65, -33.49) * mm});
            skLineSegment(sketch, "E2559", {"start": v(2.65, -33.49) * mm, "end": v(1.82, -33.08) * mm});
            skLineSegment(sketch, "E2560", {"start": v(1.82, -33.08) * mm, "end": v(1.48, -32.97) * mm});
            skLineSegment(sketch, "E2561", {"start": v(1.48, -32.97) * mm, "end": v(1.16, -32.93) * mm});
            skLineSegment(sketch, "E2562", {"start": v(1.16, -32.93) * mm, "end": v(0.82, -32.97) * mm});
            skLineSegment(sketch, "E2563", {"start": v(0.82, -32.97) * mm, "end": v(0.38, -33.1) * mm});
            skLineSegment(sketch, "E2564", {"start": v(0.38, -33.1) * mm, "end": v(-0.44, -33.4) * mm});
            skLineSegment(sketch, "E2565", {"start": v(-0.44, -33.4) * mm, "end": v(-1.11, -33.71) * mm});
            skLineSegment(sketch, "E2566", {"start": v(-1.11, -33.71) * mm, "end": v(-1.55, -33.99) * mm});
            skLineSegment(sketch, "E2567", {"start": v(-1.55, -33.99) * mm, "end": v(-1.77, -34.2) * mm});
            skLineSegment(sketch, "E2568", {"start": v(-1.77, -34.2) * mm, "end": v(-1.82, -34.26) * mm});
            skLineSegment(sketch, "E2569", {"start": v(-1.82, -34.26) * mm, "end": v(-1.88, -34.48) * mm});
            skLineSegment(sketch, "E2570", {"start": v(-1.88, -34.48) * mm, "end": v(-1.81, -34.73) * mm});
            skLineSegment(sketch, "E2571", {"start": v(-1.81, -34.73) * mm, "end": v(-1.68, -34.92) * mm});
            skLineSegment(sketch, "E2572", {"start": v(-1.68, -34.92) * mm, "end": v(-1.3, -35.23) * mm});
            skLineSegment(sketch, "E2573", {"start": v(-1.3, -35.23) * mm, "end": v(-0.85, -35.46) * mm});
            skLineSegment(sketch, "E2574", {"start": v(-0.85, -35.46) * mm, "end": v(-0.33, -35.65) * mm});
            skLineSegment(sketch, "E2575", {"start": v(-0.33, -35.65) * mm, "end": v(0.19, -35.8) * mm});
            skLineSegment(sketch, "E2576", {"start": v(0.19, -35.8) * mm, "end": v(0.79, -35.9) * mm});
            skLineSegment(sketch, "E2577", {"start": v(0.79, -35.9) * mm, "end": v(1.17, -35.94) * mm});
            skLineSegment(sketch, "E2578", {"start": v(1.17, -35.94) * mm, "end": v(1.68, -35.88) * mm});
            skLineSegment(sketch, "E2579", {"start": v(1.68, -35.88) * mm, "end": v(2.3, -35.73) * mm});
            skLineSegment(sketch, "E2580", {"start": v(-10.62, -37.77) * mm, "end": v(-8.58, -37.68) * mm});
            skLineSegment(sketch, "E2581", {"start": v(-8.58, -37.68) * mm, "end": v(-6.3, -37.47) * mm});
            skLineSegment(sketch, "E2582", {"start": v(-6.3, -37.47) * mm, "end": v(-4.02, -37.17) * mm});
            skLineSegment(sketch, "E2583", {"start": v(-4.02, -37.17) * mm, "end": v(-3.34, -37.1) * mm});
            skLineSegment(sketch, "E2584", {"start": v(-3.34, -37.1) * mm, "end": v(-2.5, -37) * mm});
            skLineSegment(sketch, "E2585", {"start": v(-2.5, -37) * mm, "end": v(-1.87, -36.84) * mm});
            skLineSegment(sketch, "E2586", {"start": v(-1.87, -36.84) * mm, "end": v(-1.49, -36.62) * mm});
            skLineSegment(sketch, "E2587", {"start": v(-1.49, -36.62) * mm, "end": v(-1.4, -36.48) * mm});
            skLineSegment(sketch, "E2588", {"start": v(-1.4, -36.48) * mm, "end": v(-1.43, -36.32) * mm});
            skLineSegment(sketch, "E2589", {"start": v(-1.43, -36.32) * mm, "end": v(-1.67, -36.08) * mm});
            skLineSegment(sketch, "E2590", {"start": v(-1.67, -36.08) * mm, "end": v(-2.14, -35.78) * mm});
            skLineSegment(sketch, "E2591", {"start": v(-2.14, -35.78) * mm, "end": v(-3.09, -35.2) * mm});
            skLineSegment(sketch, "E2592", {"start": v(-3.09, -35.2) * mm, "end": v(-3.53, -35.03) * mm});
            skLineSegment(sketch, "E2593", {"start": v(-3.53, -35.03) * mm, "end": v(-3.88, -34.97) * mm});
            skLineSegment(sketch, "E2594", {"start": v(-3.88, -34.97) * mm, "end": v(-4.13, -34.96) * mm});
            skLineSegment(sketch, "E2595", {"start": v(-4.13, -34.96) * mm, "end": v(-4.52, -35) * mm});
            skLineSegment(sketch, "E2596", {"start": v(-4.52, -35) * mm, "end": v(-5.31, -35.24) * mm});
            skLineSegment(sketch, "E2597", {"start": v(-5.31, -35.24) * mm, "end": v(-6.86, -35.68) * mm});
            skLineSegment(sketch, "E2598", {"start": v(-6.86, -35.68) * mm, "end": v(-9.7, -36.5) * mm});
            skLineSegment(sketch, "E2599", {"start": v(-9.7, -36.5) * mm, "end": v(-12.03, -37.18) * mm});
            skLineSegment(sketch, "E2600", {"start": v(-12.03, -37.18) * mm, "end": v(-13.47, -37.46) * mm});
            skLineSegment(sketch, "E2601", {"start": v(-13.47, -37.46) * mm, "end": v(-14.02, -37.58) * mm});
            skLineSegment(sketch, "E2602", {"start": v(-14.02, -37.58) * mm, "end": v(-14.12, -37.64) * mm});
            skLineSegment(sketch, "E2603", {"start": v(-14.12, -37.64) * mm, "end": v(-14.11, -37.68) * mm});
            skLineSegment(sketch, "E2604", {"start": v(-14.11, -37.68) * mm, "end": v(-14.04, -37.73) * mm});
            skLineSegment(sketch, "E2605", {"start": v(-14.04, -37.73) * mm, "end": v(-13.9, -37.77) * mm});
            skLineSegment(sketch, "E2606", {"start": v(-13.9, -37.77) * mm, "end": v(-13.61, -37.82) * mm});
            skLineSegment(sketch, "E2607", {"start": v(-13.61, -37.82) * mm, "end": v(-13.2, -37.85) * mm});
            skLineSegment(sketch, "E2608", {"start": v(-13.2, -37.85) * mm, "end": v(-12.32, -37.84) * mm});
            skLineSegment(sketch, "E2609", {"start": v(-12.32, -37.84) * mm, "end": v(-11.5, -37.79) * mm});
            skLineSegment(sketch, "E2610", {"start": v(-11.5, -37.79) * mm, "end": v(-10.62, -37.77) * mm});
            skLineSegment(sketch, "E2611", {"start": v(-30.98, -26.81) * mm, "end": v(-30.06, -26.02) * mm});
            skLineSegment(sketch, "E2612", {"start": v(-30.06, -26.02) * mm, "end": v(-30.28, -26.02) * mm});
            skLineSegment(sketch, "E2613", {"start": v(-30.28, -26.02) * mm, "end": v(-31.26, -26.44) * mm});
            skLineSegment(sketch, "E2614", {"start": v(-31.26, -26.44) * mm, "end": v(-30.98, -26.81) * mm});
            skLineSegment(sketch, "E2615", {"start": v(-32.36, -30.16) * mm, "end": v(-32.25, -29.2) * mm});
            skLineSegment(sketch, "E2616", {"start": v(-32.25, -29.2) * mm, "end": v(-32.23, -28.54) * mm});
            skLineSegment(sketch, "E2617", {"start": v(-32.23, -28.54) * mm, "end": v(-32.3, -27.95) * mm});
            skLineSegment(sketch, "E2618", {"start": v(-32.3, -27.95) * mm, "end": v(-32.43, -27.71) * mm});
            skLineSegment(sketch, "E2619", {"start": v(-32.43, -27.71) * mm, "end": v(-32.6, -27.58) * mm});
            skLineSegment(sketch, "E2620", {"start": v(-32.6, -27.58) * mm, "end": v(-32.77, -27.57) * mm});
            skLineSegment(sketch, "E2621", {"start": v(-32.77, -27.57) * mm, "end": v(-33.08, -27.69) * mm});
            skLineSegment(sketch, "E2622", {"start": v(-33.08, -27.69) * mm, "end": v(-33.33, -27.87) * mm});
            skLineSegment(sketch, "E2623", {"start": v(-33.33, -27.87) * mm, "end": v(-33.53, -28.23) * mm});
            skLineSegment(sketch, "E2624", {"start": v(-33.53, -28.23) * mm, "end": v(-33.63, -28.65) * mm});
            skLineSegment(sketch, "E2625", {"start": v(-33.63, -28.65) * mm, "end": v(-33.63, -29.11) * mm});
            skLineSegment(sketch, "E2626", {"start": v(-33.63, -29.11) * mm, "end": v(-33.55, -29.56) * mm});
            skLineSegment(sketch, "E2627", {"start": v(-33.55, -29.56) * mm, "end": v(-33.42, -29.97) * mm});
            skLineSegment(sketch, "E2628", {"start": v(-33.42, -29.97) * mm, "end": v(-33.13, -30.46) * mm});
            skLineSegment(sketch, "E2629", {"start": v(-33.13, -30.46) * mm, "end": v(-32.86, -30.8) * mm});
            skLineSegment(sketch, "E2630", {"start": v(-32.86, -30.8) * mm, "end": v(-32.7, -30.94) * mm});
            skLineSegment(sketch, "E2631", {"start": v(-32.7, -30.94) * mm, "end": v(-32.58, -30.96) * mm});
            skLineSegment(sketch, "E2632", {"start": v(-32.58, -30.96) * mm, "end": v(-32.46, -30.81) * mm});
            skLineSegment(sketch, "E2633", {"start": v(-32.46, -30.81) * mm, "end": v(-32.36, -30.16) * mm});
            skLineSegment(sketch, "E2634", {"start": v(-31.4, -34.44) * mm, "end": v(-32.13, -33.52) * mm});
            skLineSegment(sketch, "E2635", {"start": v(-32.13, -33.52) * mm, "end": v(-32.87, -32.66) * mm});
            skLineSegment(sketch, "E2636", {"start": v(-32.87, -32.66) * mm, "end": v(-33.17, -32.36) * mm});
            skLineSegment(sketch, "E2637", {"start": v(-33.17, -32.36) * mm, "end": v(-33.38, -32.25) * mm});
            skLineSegment(sketch, "E2638", {"start": v(-33.38, -32.25) * mm, "end": v(-33.54, -32.3) * mm});
            skLineSegment(sketch, "E2639", {"start": v(-33.54, -32.3) * mm, "end": v(-33.6, -32.47) * mm});
            skLineSegment(sketch, "E2640", {"start": v(-33.6, -32.47) * mm, "end": v(-33.59, -32.83) * mm});
            skLineSegment(sketch, "E2641", {"start": v(-33.59, -32.83) * mm, "end": v(-33.44, -33.32) * mm});
            skLineSegment(sketch, "E2642", {"start": v(-33.44, -33.32) * mm, "end": v(-33.24, -33.73) * mm});
            skLineSegment(sketch, "E2643", {"start": v(-33.24, -33.73) * mm, "end": v(-32.91, -34.29) * mm});
            skLineSegment(sketch, "E2644", {"start": v(-32.91, -34.29) * mm, "end": v(-32.47, -34.92) * mm});
            skLineSegment(sketch, "E2645", {"start": v(-32.47, -34.92) * mm, "end": v(-32.04, -35.4) * mm});
            skLineSegment(sketch, "E2646", {"start": v(-32.04, -35.4) * mm, "end": v(-31.68, -35.71) * mm});
            skLineSegment(sketch, "E2647", {"start": v(-31.68, -35.71) * mm, "end": v(-31.4, -35.88) * mm});
            skLineSegment(sketch, "E2648", {"start": v(-31.4, -35.88) * mm, "end": v(-31.12, -35.96) * mm});
            skLineSegment(sketch, "E2649", {"start": v(-31.12, -35.96) * mm, "end": v(-30.88, -35.96) * mm});
            skLineSegment(sketch, "E2650", {"start": v(-30.88, -35.96) * mm, "end": v(-30.68, -35.89) * mm});
            skLineSegment(sketch, "E2651", {"start": v(-30.68, -35.89) * mm, "end": v(-30.66, -35.62) * mm});
            skLineSegment(sketch, "E2652", {"start": v(-30.66, -35.62) * mm, "end": v(-30.78, -35.37) * mm});
            skLineSegment(sketch, "E2653", {"start": v(-30.78, -35.37) * mm, "end": v(-31.4, -34.44) * mm});
            skLineSegment(sketch, "E2654", {"start": v(-28.82, -32.51) * mm, "end": v(-29.13, -32.12) * mm});
            skLineSegment(sketch, "E2655", {"start": v(-29.13, -32.12) * mm, "end": v(-29.5, -31.76) * mm});
            skLineSegment(sketch, "E2656", {"start": v(-29.5, -31.76) * mm, "end": v(-29.87, -31.42) * mm});
            skLineSegment(sketch, "E2657", {"start": v(-29.87, -31.42) * mm, "end": v(-30.16, -31.14) * mm});
            skLineSegment(sketch, "E2658", {"start": v(-30.16, -31.14) * mm, "end": v(-30.38, -31.02) * mm});
            skLineSegment(sketch, "E2659", {"start": v(-30.38, -31.02) * mm, "end": v(-30.54, -31.06) * mm});
            skLineSegment(sketch, "E2660", {"start": v(-30.54, -31.06) * mm, "end": v(-30.64, -31.23) * mm});
            skLineSegment(sketch, "E2661", {"start": v(-30.64, -31.23) * mm, "end": v(-30.7, -31.61) * mm});
            skLineSegment(sketch, "E2662", {"start": v(-30.7, -31.61) * mm, "end": v(-30.68, -32.11) * mm});
            skLineSegment(sketch, "E2663", {"start": v(-30.68, -32.11) * mm, "end": v(-30.6, -32.45) * mm});
            skLineSegment(sketch, "E2664", {"start": v(-30.6, -32.45) * mm, "end": v(-30.41, -32.86) * mm});
            skLineSegment(sketch, "E2665", {"start": v(-30.41, -32.86) * mm, "end": v(-30.13, -33.3) * mm});
            skLineSegment(sketch, "E2666", {"start": v(-30.13, -33.3) * mm, "end": v(-29.78, -33.72) * mm});
            skLineSegment(sketch, "E2667", {"start": v(-29.78, -33.72) * mm, "end": v(-29.38, -34.08) * mm});
            skLineSegment(sketch, "E2668", {"start": v(-29.38, -34.08) * mm, "end": v(-29.07, -34.29) * mm});
            skLineSegment(sketch, "E2669", {"start": v(-29.07, -34.29) * mm, "end": v(-28.86, -34.39) * mm});
            skLineSegment(sketch, "E2670", {"start": v(-28.86, -34.39) * mm, "end": v(-28.56, -34.47) * mm});
            skLineSegment(sketch, "E2671", {"start": v(-28.56, -34.47) * mm, "end": v(-28.37, -34.46) * mm});
            skLineSegment(sketch, "E2672", {"start": v(-28.37, -34.46) * mm, "end": v(-28.26, -34.36) * mm});
            skLineSegment(sketch, "E2673", {"start": v(-28.26, -34.36) * mm, "end": v(-28.24, -34.14) * mm});
            skLineSegment(sketch, "E2674", {"start": v(-28.24, -34.14) * mm, "end": v(-28.32, -33.75) * mm});
            skLineSegment(sketch, "E2675", {"start": v(-28.32, -33.75) * mm, "end": v(-28.47, -33.2) * mm});
            skLineSegment(sketch, "E2676", {"start": v(-28.47, -33.2) * mm, "end": v(-28.62, -32.84) * mm});
            skLineSegment(sketch, "E2677", {"start": v(-28.62, -32.84) * mm, "end": v(-28.82, -32.51) * mm});
            skLineSegment(sketch, "E2678", {"start": v(-27.82, -29.3) * mm, "end": v(-27.66, -28.8) * mm});
            skLineSegment(sketch, "E2679", {"start": v(-27.66, -28.8) * mm, "end": v(-27.58, -28.3) * mm});
            skLineSegment(sketch, "E2680", {"start": v(-27.58, -28.3) * mm, "end": v(-27.6, -27.85) * mm});
            skLineSegment(sketch, "E2681", {"start": v(-27.6, -27.85) * mm, "end": v(-27.68, -27.56) * mm});
            skLineSegment(sketch, "E2682", {"start": v(-27.68, -27.56) * mm, "end": v(-27.87, -27.36) * mm});
            skLineSegment(sketch, "E2683", {"start": v(-27.87, -27.36) * mm, "end": v(-28.07, -27.29) * mm});
            skLineSegment(sketch, "E2684", {"start": v(-28.07, -27.29) * mm, "end": v(-28.23, -27.28) * mm});
            skLineSegment(sketch, "E2685", {"start": v(-28.23, -27.28) * mm, "end": v(-28.53, -27.33) * mm});
            skLineSegment(sketch, "E2686", {"start": v(-28.53, -27.33) * mm, "end": v(-28.84, -27.46) * mm});
            skLineSegment(sketch, "E2687", {"start": v(-28.84, -27.46) * mm, "end": v(-29.26, -27.75) * mm});
            skLineSegment(sketch, "E2688", {"start": v(-29.26, -27.75) * mm, "end": v(-29.56, -28.03) * mm});
            skLineSegment(sketch, "E2689", {"start": v(-29.56, -28.03) * mm, "end": v(-29.73, -28.24) * mm});
            skLineSegment(sketch, "E2690", {"start": v(-29.73, -28.24) * mm, "end": v(-29.89, -28.52) * mm});
            skLineSegment(sketch, "E2691", {"start": v(-29.89, -28.52) * mm, "end": v(-29.99, -28.8) * mm});
            skLineSegment(sketch, "E2692", {"start": v(-29.99, -28.8) * mm, "end": v(-30, -29.02) * mm});
            skLineSegment(sketch, "E2693", {"start": v(-30, -29.02) * mm, "end": v(-29.98, -29.2) * mm});
            skLineSegment(sketch, "E2694", {"start": v(-29.98, -29.2) * mm, "end": v(-29.84, -29.5) * mm});
            skLineSegment(sketch, "E2695", {"start": v(-29.84, -29.5) * mm, "end": v(-29.64, -29.82) * mm});
            skLineSegment(sketch, "E2696", {"start": v(-29.64, -29.82) * mm, "end": v(-29.37, -30.1) * mm});
            skLineSegment(sketch, "E2697", {"start": v(-29.37, -30.1) * mm, "end": v(-29.07, -30.31) * mm});
            skLineSegment(sketch, "E2698", {"start": v(-29.07, -30.31) * mm, "end": v(-28.87, -30.38) * mm});
            skLineSegment(sketch, "E2699", {"start": v(-28.87, -30.38) * mm, "end": v(-28.6, -30.37) * mm});
            skLineSegment(sketch, "E2700", {"start": v(-28.6, -30.37) * mm, "end": v(-28.33, -30.19) * mm});
            skLineSegment(sketch, "E2701", {"start": v(-28.33, -30.19) * mm, "end": v(-28.04, -29.77) * mm});
            skLineSegment(sketch, "E2702", {"start": v(-28.04, -29.77) * mm, "end": v(-27.82, -29.3) * mm});
            skLineSegment(sketch, "E2703", {"start": v(-25.82, -26.84) * mm, "end": v(-25.57, -26.66) * mm});
            skLineSegment(sketch, "E2704", {"start": v(-25.57, -26.66) * mm, "end": v(-25.43, -26.44) * mm});
            skLineSegment(sketch, "E2705", {"start": v(-25.43, -26.44) * mm, "end": v(-25.42, -26.34) * mm});
            skLineSegment(sketch, "E2706", {"start": v(-25.42, -26.34) * mm, "end": v(-25.52, -26.24) * mm});
            skLineSegment(sketch, "E2707", {"start": v(-25.52, -26.24) * mm, "end": v(-25.65, -26.21) * mm});
            skLineSegment(sketch, "E2708", {"start": v(-25.65, -26.21) * mm, "end": v(-25.85, -26.23) * mm});
            skLineSegment(sketch, "E2709", {"start": v(-25.85, -26.23) * mm, "end": v(-26.1, -26.3) * mm});
            skLineSegment(sketch, "E2710", {"start": v(-26.1, -26.3) * mm, "end": v(-26.32, -26.48) * mm});
            skLineSegment(sketch, "E2711", {"start": v(-26.32, -26.48) * mm, "end": v(-26.4, -26.65) * mm});
            skLineSegment(sketch, "E2712", {"start": v(-26.4, -26.65) * mm, "end": v(-26.42, -26.79) * mm});
            skLineSegment(sketch, "E2713", {"start": v(-26.42, -26.79) * mm, "end": v(-26.37, -26.91) * mm});
            skLineSegment(sketch, "E2714", {"start": v(-26.37, -26.91) * mm, "end": v(-26.2, -26.96) * mm});
            skLineSegment(sketch, "E2715", {"start": v(-26.2, -26.96) * mm, "end": v(-26.02, -26.93) * mm});
            skLineSegment(sketch, "E2716", {"start": v(-26.02, -26.93) * mm, "end": v(-25.82, -26.84) * mm});
            skLineSegment(sketch, "E2717", {"start": v(-23.39, -28.78) * mm, "end": v(-23.01, -28.34) * mm});
            skLineSegment(sketch, "E2718", {"start": v(-23.01, -28.34) * mm, "end": v(-22.7, -27.84) * mm});
            skLineSegment(sketch, "E2719", {"start": v(-22.7, -27.84) * mm, "end": v(-22.59, -27.56) * mm});
            skLineSegment(sketch, "E2720", {"start": v(-22.59, -27.56) * mm, "end": v(-22.57, -27.42) * mm});
            skLineSegment(sketch, "E2721", {"start": v(-22.57, -27.42) * mm, "end": v(-22.63, -27.27) * mm});
            skLineSegment(sketch, "E2722", {"start": v(-22.63, -27.27) * mm, "end": v(-22.78, -27.19) * mm});
            skLineSegment(sketch, "E2723", {"start": v(-22.78, -27.19) * mm, "end": v(-22.95, -27.18) * mm});
            skLineSegment(sketch, "E2724", {"start": v(-22.95, -27.18) * mm, "end": v(-23.28, -27.24) * mm});
            skLineSegment(sketch, "E2725", {"start": v(-23.28, -27.24) * mm, "end": v(-23.53, -27.3) * mm});
            skLineSegment(sketch, "E2726", {"start": v(-23.53, -27.3) * mm, "end": v(-24.04, -27.51) * mm});
            skLineSegment(sketch, "E2727", {"start": v(-24.04, -27.51) * mm, "end": v(-24.52, -27.79) * mm});
            skLineSegment(sketch, "E2728", {"start": v(-24.52, -27.79) * mm, "end": v(-24.9, -28.1) * mm});
            skLineSegment(sketch, "E2729", {"start": v(-24.9, -28.1) * mm, "end": v(-25.09, -28.38) * mm});
            skLineSegment(sketch, "E2730", {"start": v(-25.09, -28.38) * mm, "end": v(-25.13, -28.58) * mm});
            skLineSegment(sketch, "E2731", {"start": v(-25.13, -28.58) * mm, "end": v(-25.09, -28.77) * mm});
            skLineSegment(sketch, "E2732", {"start": v(-25.09, -28.77) * mm, "end": v(-24.98, -28.95) * mm});
            skLineSegment(sketch, "E2733", {"start": v(-24.98, -28.95) * mm, "end": v(-24.78, -29.14) * mm});
            skLineSegment(sketch, "E2734", {"start": v(-24.78, -29.14) * mm, "end": v(-24.53, -29.29) * mm});
            skLineSegment(sketch, "E2735", {"start": v(-24.53, -29.29) * mm, "end": v(-24.32, -29.34) * mm});
            skLineSegment(sketch, "E2736", {"start": v(-24.32, -29.34) * mm, "end": v(-24.11, -29.34) * mm});
            skLineSegment(sketch, "E2737", {"start": v(-24.11, -29.34) * mm, "end": v(-23.9, -29.24) * mm});
            skLineSegment(sketch, "E2738", {"start": v(-23.9, -29.24) * mm, "end": v(-23.54, -28.94) * mm});
            skLineSegment(sketch, "E2739", {"start": v(-23.54, -28.94) * mm, "end": v(-23.39, -28.78) * mm});
            skLineSegment(sketch, "E2740", {"start": v(-24.63, -31.22) * mm, "end": v(-24.83, -30.82) * mm});
            skLineSegment(sketch, "E2741", {"start": v(-24.83, -30.82) * mm, "end": v(-25.14, -30.35) * mm});
            skLineSegment(sketch, "E2742", {"start": v(-25.14, -30.35) * mm, "end": v(-25.42, -30.06) * mm});
            skLineSegment(sketch, "E2743", {"start": v(-25.42, -30.06) * mm, "end": v(-25.72, -29.85) * mm});
            skLineSegment(sketch, "E2744", {"start": v(-25.72, -29.85) * mm, "end": v(-25.95, -29.77) * mm});
            skLineSegment(sketch, "E2745", {"start": v(-25.95, -29.77) * mm, "end": v(-26.16, -29.76) * mm});
            skLineSegment(sketch, "E2746", {"start": v(-26.16, -29.76) * mm, "end": v(-26.4, -29.86) * mm});
            skLineSegment(sketch, "E2747", {"start": v(-26.4, -29.86) * mm, "end": v(-26.69, -30.07) * mm});
            skLineSegment(sketch, "E2748", {"start": v(-26.69, -30.07) * mm, "end": v(-26.82, -30.23) * mm});
            skLineSegment(sketch, "E2749", {"start": v(-26.82, -30.23) * mm, "end": v(-26.94, -30.5) * mm});
            skLineSegment(sketch, "E2750", {"start": v(-26.94, -30.5) * mm, "end": v(-26.98, -30.79) * mm});
            skLineSegment(sketch, "E2751", {"start": v(-26.98, -30.79) * mm, "end": v(-26.94, -31.18) * mm});
            skLineSegment(sketch, "E2752", {"start": v(-26.94, -31.18) * mm, "end": v(-26.8, -31.57) * mm});
            skLineSegment(sketch, "E2753", {"start": v(-26.8, -31.57) * mm, "end": v(-26.57, -31.93) * mm});
            skLineSegment(sketch, "E2754", {"start": v(-26.57, -31.93) * mm, "end": v(-26.37, -32.16) * mm});
            skLineSegment(sketch, "E2755", {"start": v(-26.37, -32.16) * mm, "end": v(-26.07, -32.41) * mm});
            skLineSegment(sketch, "E2756", {"start": v(-26.07, -32.41) * mm, "end": v(-25.7, -32.64) * mm});
            skLineSegment(sketch, "E2757", {"start": v(-25.7, -32.64) * mm, "end": v(-25.37, -32.81) * mm});
            skLineSegment(sketch, "E2758", {"start": v(-25.37, -32.81) * mm, "end": v(-25.13, -32.87) * mm});
            skLineSegment(sketch, "E2759", {"start": v(-25.13, -32.87) * mm, "end": v(-24.91, -32.86) * mm});
            skLineSegment(sketch, "E2760", {"start": v(-24.91, -32.86) * mm, "end": v(-24.75, -32.76) * mm});
            skLineSegment(sketch, "E2761", {"start": v(-24.75, -32.76) * mm, "end": v(-24.58, -32.56) * mm});
            skLineSegment(sketch, "E2762", {"start": v(-24.58, -32.56) * mm, "end": v(-24.47, -32.23) * mm});
            skLineSegment(sketch, "E2763", {"start": v(-24.47, -32.23) * mm, "end": v(-24.48, -31.74) * mm});
            skLineSegment(sketch, "E2764", {"start": v(-24.48, -31.74) * mm, "end": v(-24.63, -31.22) * mm});
            skLineSegment(sketch, "E2765", {"start": v(-24.15, -35.53) * mm, "end": v(-24.48, -35.16) * mm});
            skLineSegment(sketch, "E2766", {"start": v(-24.48, -35.16) * mm, "end": v(-24.96, -34.8) * mm});
            skLineSegment(sketch, "E2767", {"start": v(-24.96, -34.8) * mm, "end": v(-25.5, -34.48) * mm});
            skLineSegment(sketch, "E2768", {"start": v(-25.5, -34.48) * mm, "end": v(-25.96, -34.24) * mm});
            skLineSegment(sketch, "E2769", {"start": v(-25.96, -34.24) * mm, "end": v(-26.29, -34.05) * mm});
            skLineSegment(sketch, "E2770", {"start": v(-26.29, -34.05) * mm, "end": v(-26.54, -33.94) * mm});
            skLineSegment(sketch, "E2771", {"start": v(-26.54, -33.94) * mm, "end": v(-26.77, -33.93) * mm});
            skLineSegment(sketch, "E2772", {"start": v(-26.77, -33.93) * mm, "end": v(-26.89, -34.1) * mm});
            skLineSegment(sketch, "E2773", {"start": v(-26.89, -34.1) * mm, "end": v(-26.9, -34.35) * mm});
            skLineSegment(sketch, "E2774", {"start": v(-26.9, -34.35) * mm, "end": v(-26.78, -34.76) * mm});
            skLineSegment(sketch, "E2775", {"start": v(-26.78, -34.76) * mm, "end": v(-26.63, -35.11) * mm});
            skLineSegment(sketch, "E2776", {"start": v(-26.63, -35.11) * mm, "end": v(-26.44, -35.45) * mm});
            skLineSegment(sketch, "E2777", {"start": v(-26.44, -35.45) * mm, "end": v(-26.13, -35.82) * mm});
            skLineSegment(sketch, "E2778", {"start": v(-26.13, -35.82) * mm, "end": v(-25.76, -36.11) * mm});
            skLineSegment(sketch, "E2779", {"start": v(-25.76, -36.11) * mm, "end": v(-25.1, -36.47) * mm});
            skLineSegment(sketch, "E2780", {"start": v(-25.1, -36.47) * mm, "end": v(-24.65, -36.66) * mm});
            skLineSegment(sketch, "E2781", {"start": v(-24.65, -36.66) * mm, "end": v(-24.04, -36.9) * mm});
            skLineSegment(sketch, "E2782", {"start": v(-24.04, -36.9) * mm, "end": v(-23.8, -36.94) * mm});
            skLineSegment(sketch, "E2783", {"start": v(-23.8, -36.94) * mm, "end": v(-23.64, -36.86) * mm});
            skLineSegment(sketch, "E2784", {"start": v(-23.64, -36.86) * mm, "end": v(-23.6, -36.67) * mm});
            skLineSegment(sketch, "E2785", {"start": v(-23.6, -36.67) * mm, "end": v(-23.66, -36.43) * mm});
            skLineSegment(sketch, "E2786", {"start": v(-23.66, -36.43) * mm, "end": v(-23.94, -35.87) * mm});
            skLineSegment(sketch, "E2787", {"start": v(-23.94, -35.87) * mm, "end": v(-24.15, -35.53) * mm});
            skLineSegment(sketch, "E2788", {"start": v(-20.48, -36.56) * mm, "end": v(-20.89, -36.38) * mm});
            skLineSegment(sketch, "E2789", {"start": v(-20.89, -36.38) * mm, "end": v(-21.52, -36.1) * mm});
            skLineSegment(sketch, "E2790", {"start": v(-21.52, -36.1) * mm, "end": v(-22.03, -35.92) * mm});
            skLineSegment(sketch, "E2791", {"start": v(-22.03, -35.92) * mm, "end": v(-22.37, -35.85) * mm});
            skLineSegment(sketch, "E2792", {"start": v(-22.37, -35.85) * mm, "end": v(-22.44, -35.85) * mm});
            skLineSegment(sketch, "E2793", {"start": v(-22.44, -35.85) * mm, "end": v(-22.56, -35.89) * mm});
            skLineSegment(sketch, "E2794", {"start": v(-22.56, -35.89) * mm, "end": v(-22.6, -35.98) * mm});
            skLineSegment(sketch, "E2795", {"start": v(-22.6, -35.98) * mm, "end": v(-22.52, -36.27) * mm});
            skLineSegment(sketch, "E2796", {"start": v(-22.52, -36.27) * mm, "end": v(-22.08, -36.89) * mm});
            skLineSegment(sketch, "E2797", {"start": v(-22.08, -36.89) * mm, "end": v(-21.88, -37.03) * mm});
            skLineSegment(sketch, "E2798", {"start": v(-21.88, -37.03) * mm, "end": v(-21.59, -37.15) * mm});
            skLineSegment(sketch, "E2799", {"start": v(-21.59, -37.15) * mm, "end": v(-21, -37.28) * mm});
            skLineSegment(sketch, "E2800", {"start": v(-21, -37.28) * mm, "end": v(-20.53, -37.32) * mm});
            skLineSegment(sketch, "E2801", {"start": v(-20.53, -37.32) * mm, "end": v(-20, -37.28) * mm});
            skLineSegment(sketch, "E2802", {"start": v(-20, -37.28) * mm, "end": v(-19.68, -37.19) * mm});
            skLineSegment(sketch, "E2803", {"start": v(-19.68, -37.19) * mm, "end": v(-19.5, -37.07) * mm});
            skLineSegment(sketch, "E2804", {"start": v(-19.5, -37.07) * mm, "end": v(-19.46, -36.96) * mm});
            skLineSegment(sketch, "E2805", {"start": v(-19.46, -36.96) * mm, "end": v(-19.56, -36.85) * mm});
            skLineSegment(sketch, "E2806", {"start": v(-19.56, -36.85) * mm, "end": v(-19.89, -36.76) * mm});
            skLineSegment(sketch, "E2807", {"start": v(-19.89, -36.76) * mm, "end": v(-20.48, -36.56) * mm});
            skLineSegment(sketch, "E2808", {"start": v(-22, -34.4) * mm, "end": v(-20.97, -34.9) * mm});
            skLineSegment(sketch, "E2809", {"start": v(-20.97, -34.9) * mm, "end": v(-20.3, -35.18) * mm});
            skLineSegment(sketch, "E2810", {"start": v(-20.3, -35.18) * mm, "end": v(-19.64, -35.41) * mm});
            skLineSegment(sketch, "E2811", {"start": v(-19.64, -35.41) * mm, "end": v(-19.34, -35.4) * mm});
            skLineSegment(sketch, "E2812", {"start": v(-19.34, -35.4) * mm, "end": v(-19.22, -35.24) * mm});
            skLineSegment(sketch, "E2813", {"start": v(-19.22, -35.24) * mm, "end": v(-19.22, -34.9) * mm});
            skLineSegment(sketch, "E2814", {"start": v(-19.22, -34.9) * mm, "end": v(-19.38, -34.35) * mm});
            skLineSegment(sketch, "E2815", {"start": v(-19.38, -34.35) * mm, "end": v(-19.54, -33.97) * mm});
            skLineSegment(sketch, "E2816", {"start": v(-19.54, -33.97) * mm, "end": v(-19.61, -33.87) * mm});
            skLineSegment(sketch, "E2817", {"start": v(-19.61, -33.87) * mm, "end": v(-20, -33.52) * mm});
            skLineSegment(sketch, "E2818", {"start": v(-20, -33.52) * mm, "end": v(-20.55, -33.13) * mm});
            skLineSegment(sketch, "E2819", {"start": v(-20.55, -33.13) * mm, "end": v(-21.08, -32.82) * mm});
            skLineSegment(sketch, "E2820", {"start": v(-21.08, -32.82) * mm, "end": v(-21.62, -32.55) * mm});
            skLineSegment(sketch, "E2821", {"start": v(-21.62, -32.55) * mm, "end": v(-22.14, -32.35) * mm});
            skLineSegment(sketch, "E2822", {"start": v(-22.14, -32.35) * mm, "end": v(-22.47, -32.27) * mm});
            skLineSegment(sketch, "E2823", {"start": v(-22.47, -32.27) * mm, "end": v(-22.76, -32.26) * mm});
            skLineSegment(sketch, "E2824", {"start": v(-22.76, -32.26) * mm, "end": v(-22.9, -32.3) * mm});
            skLineSegment(sketch, "E2825", {"start": v(-22.9, -32.3) * mm, "end": v(-23.09, -32.43) * mm});
            skLineSegment(sketch, "E2826", {"start": v(-23.09, -32.43) * mm, "end": v(-23.25, -32.61) * mm});
            skLineSegment(sketch, "E2827", {"start": v(-23.25, -32.61) * mm, "end": v(-23.33, -32.76) * mm});
            skLineSegment(sketch, "E2828", {"start": v(-23.33, -32.76) * mm, "end": v(-23.37, -32.9) * mm});
            skLineSegment(sketch, "E2829", {"start": v(-23.37, -32.9) * mm, "end": v(-23.38, -33.04) * mm});
            skLineSegment(sketch, "E2830", {"start": v(-23.38, -33.04) * mm, "end": v(-23.32, -33.25) * mm});
            skLineSegment(sketch, "E2831", {"start": v(-23.32, -33.25) * mm, "end": v(-23.16, -33.53) * mm});
            skLineSegment(sketch, "E2832", {"start": v(-23.16, -33.53) * mm, "end": v(-22.94, -33.77) * mm});
            skLineSegment(sketch, "E2833", {"start": v(-22.94, -33.77) * mm, "end": v(-22.39, -34.17) * mm});
            skLineSegment(sketch, "E2834", {"start": v(-22.39, -34.17) * mm, "end": v(-22, -34.4) * mm});
            skLineSegment(sketch, "E2835", {"start": v(-19.56, -29.85) * mm, "end": v(-19.8, -29.43) * mm});
            skLineSegment(sketch, "E2836", {"start": v(-19.8, -29.43) * mm, "end": v(-20.2, -29.02) * mm});
            skLineSegment(sketch, "E2837", {"start": v(-20.2, -29.02) * mm, "end": v(-20.6, -28.83) * mm});
            skLineSegment(sketch, "E2838", {"start": v(-20.6, -28.83) * mm, "end": v(-20.95, -28.8) * mm});
            skLineSegment(sketch, "E2839", {"start": v(-20.95, -28.8) * mm, "end": v(-21.26, -28.85) * mm});
            skLineSegment(sketch, "E2840", {"start": v(-21.26, -28.85) * mm, "end": v(-21.66, -28.98) * mm});
            skLineSegment(sketch, "E2841", {"start": v(-21.66, -28.98) * mm, "end": v(-21.94, -29.17) * mm});
            skLineSegment(sketch, "E2842", {"start": v(-21.94, -29.17) * mm, "end": v(-22.14, -29.4) * mm});
            skLineSegment(sketch, "E2843", {"start": v(-22.14, -29.4) * mm, "end": v(-22.26, -29.73) * mm});
            skLineSegment(sketch, "E2844", {"start": v(-22.26, -29.73) * mm, "end": v(-22.26, -30.08) * mm});
            skLineSegment(sketch, "E2845", {"start": v(-22.26, -30.08) * mm, "end": v(-22.12, -30.51) * mm});
            skLineSegment(sketch, "E2846", {"start": v(-22.12, -30.51) * mm, "end": v(-21.95, -30.8) * mm});
            skLineSegment(sketch, "E2847", {"start": v(-21.95, -30.8) * mm, "end": v(-21.74, -31.05) * mm});
            skLineSegment(sketch, "E2848", {"start": v(-21.74, -31.05) * mm, "end": v(-21.33, -31.37) * mm});
            skLineSegment(sketch, "E2849", {"start": v(-21.33, -31.37) * mm, "end": v(-20.85, -31.58) * mm});
            skLineSegment(sketch, "E2850", {"start": v(-20.85, -31.58) * mm, "end": v(-20.42, -31.65) * mm});
            skLineSegment(sketch, "E2851", {"start": v(-20.42, -31.65) * mm, "end": v(-19.96, -31.6) * mm});
            skLineSegment(sketch, "E2852", {"start": v(-19.96, -31.6) * mm, "end": v(-19.66, -31.46) * mm});
            skLineSegment(sketch, "E2853", {"start": v(-19.66, -31.46) * mm, "end": v(-19.44, -31.15) * mm});
            skLineSegment(sketch, "E2854", {"start": v(-19.44, -31.15) * mm, "end": v(-19.36, -30.76) * mm});
            skLineSegment(sketch, "E2855", {"start": v(-19.36, -30.76) * mm, "end": v(-19.42, -30.22) * mm});
            skLineSegment(sketch, "E2856", {"start": v(-19.42, -30.22) * mm, "end": v(-19.56, -29.85) * mm});
            skLineSegment(sketch, "E2857", {"start": v(-18.1, -28.2) * mm, "end": v(-17.8, -27.97) * mm});
            skLineSegment(sketch, "E2858", {"start": v(-17.8, -27.97) * mm, "end": v(-17.55, -27.7) * mm});
            skLineSegment(sketch, "E2859", {"start": v(-17.55, -27.7) * mm, "end": v(-17.4, -27.52) * mm});
            skLineSegment(sketch, "E2860", {"start": v(-17.4, -27.52) * mm, "end": v(-17.33, -27.35) * mm});
            skLineSegment(sketch, "E2861", {"start": v(-17.33, -27.35) * mm, "end": v(-17.35, -27.23) * mm});
            skLineSegment(sketch, "E2862", {"start": v(-17.35, -27.23) * mm, "end": v(-17.43, -27.17) * mm});
            skLineSegment(sketch, "E2863", {"start": v(-17.43, -27.17) * mm, "end": v(-17.56, -27.15) * mm});
            skLineSegment(sketch, "E2864", {"start": v(-17.56, -27.15) * mm, "end": v(-17.7, -27.16) * mm});
            skLineSegment(sketch, "E2865", {"start": v(-17.7, -27.16) * mm, "end": v(-18, -27.22) * mm});
            skLineSegment(sketch, "E2866", {"start": v(-18, -27.22) * mm, "end": v(-18.44, -27.32) * mm});
            skLineSegment(sketch, "E2867", {"start": v(-18.44, -27.32) * mm, "end": v(-18.82, -27.44) * mm});
            skLineSegment(sketch, "E2868", {"start": v(-18.82, -27.44) * mm, "end": v(-19.12, -27.58) * mm});
            skLineSegment(sketch, "E2869", {"start": v(-19.12, -27.58) * mm, "end": v(-19.21, -27.65) * mm});
            skLineSegment(sketch, "E2870", {"start": v(-19.21, -27.65) * mm, "end": v(-19.35, -27.81) * mm});
            skLineSegment(sketch, "E2871", {"start": v(-19.35, -27.81) * mm, "end": v(-19.38, -27.98) * mm});
            skLineSegment(sketch, "E2872", {"start": v(-19.38, -27.98) * mm, "end": v(-19.33, -28.1) * mm});
            skLineSegment(sketch, "E2873", {"start": v(-19.33, -28.1) * mm, "end": v(-19.16, -28.26) * mm});
            skLineSegment(sketch, "E2874", {"start": v(-19.16, -28.26) * mm, "end": v(-18.97, -28.35) * mm});
            skLineSegment(sketch, "E2875", {"start": v(-18.97, -28.35) * mm, "end": v(-18.67, -28.42) * mm});
            skLineSegment(sketch, "E2876", {"start": v(-18.67, -28.42) * mm, "end": v(-18.38, -28.37) * mm});
            skLineSegment(sketch, "E2877", {"start": v(-18.38, -28.37) * mm, "end": v(-18.1, -28.2) * mm});
            skLineSegment(sketch, "E2878", {"start": v(-16, -29.81) * mm, "end": v(-15.46, -30.01) * mm});
            skLineSegment(sketch, "E2879", {"start": v(-15.46, -30.01) * mm, "end": v(-14.65, -30.19) * mm});
            skLineSegment(sketch, "E2880", {"start": v(-14.65, -30.19) * mm, "end": v(-14.19, -30.19) * mm});
            skLineSegment(sketch, "E2881", {"start": v(-14.19, -30.19) * mm, "end": v(-13.74, -29.97) * mm});
            skLineSegment(sketch, "E2882", {"start": v(-13.74, -29.97) * mm, "end": v(-13.49, -29.66) * mm});
            skLineSegment(sketch, "E2883", {"start": v(-13.49, -29.66) * mm, "end": v(-13.42, -29.3) * mm});
            skLineSegment(sketch, "E2884", {"start": v(-13.42, -29.3) * mm, "end": v(-13.47, -28.99) * mm});
            skLineSegment(sketch, "E2885", {"start": v(-13.47, -28.99) * mm, "end": v(-13.7, -28.54) * mm});
            skLineSegment(sketch, "E2886", {"start": v(-13.7, -28.54) * mm, "end": v(-14, -28.23) * mm});
            skLineSegment(sketch, "E2887", {"start": v(-14, -28.23) * mm, "end": v(-14.39, -28) * mm});
            skLineSegment(sketch, "E2888", {"start": v(-14.39, -28) * mm, "end": v(-14.82, -27.91) * mm});
            skLineSegment(sketch, "E2889", {"start": v(-14.82, -27.91) * mm, "end": v(-15.2, -27.95) * mm});
            skLineSegment(sketch, "E2890", {"start": v(-15.2, -27.95) * mm, "end": v(-15.7, -28.15) * mm});
            skLineSegment(sketch, "E2891", {"start": v(-15.7, -28.15) * mm, "end": v(-16.27, -28.48) * mm});
            skLineSegment(sketch, "E2892", {"start": v(-16.27, -28.48) * mm, "end": v(-16.6, -28.83) * mm});
            skLineSegment(sketch, "E2893", {"start": v(-16.6, -28.83) * mm, "end": v(-16.7, -29.12) * mm});
            skLineSegment(sketch, "E2894", {"start": v(-16.7, -29.12) * mm, "end": v(-16.66, -29.36) * mm});
            skLineSegment(sketch, "E2895", {"start": v(-16.66, -29.36) * mm, "end": v(-16.45, -29.57) * mm});
            skLineSegment(sketch, "E2896", {"start": v(-16.45, -29.57) * mm, "end": v(-16, -29.81) * mm});
            skLineSegment(sketch, "E2897", {"start": v(-15.96, -36.55) * mm, "end": v(-15.46, -36.5) * mm});
            skLineSegment(sketch, "E2898", {"start": v(-15.46, -36.5) * mm, "end": v(-14.84, -36.39) * mm});
            skLineSegment(sketch, "E2899", {"start": v(-14.84, -36.39) * mm, "end": v(-13.93, -36.14) * mm});
            skLineSegment(sketch, "E2900", {"start": v(-13.93, -36.14) * mm, "end": v(-13.27, -35.98) * mm});
            skLineSegment(sketch, "E2901", {"start": v(-13.27, -35.98) * mm, "end": v(-13.05, -35.86) * mm});
            skLineSegment(sketch, "E2902", {"start": v(-13.05, -35.86) * mm, "end": v(-12.97, -35.73) * mm});
            skLineSegment(sketch, "E2903", {"start": v(-12.97, -35.73) * mm, "end": v(-13.05, -35.64) * mm});
            skLineSegment(sketch, "E2904", {"start": v(-13.05, -35.64) * mm, "end": v(-13.31, -35.51) * mm});
            skLineSegment(sketch, "E2905", {"start": v(-13.31, -35.51) * mm, "end": v(-13.73, -35.37) * mm});
            skLineSegment(sketch, "E2906", {"start": v(-13.73, -35.37) * mm, "end": v(-14.34, -35.2) * mm});
            skLineSegment(sketch, "E2907", {"start": v(-14.34, -35.2) * mm, "end": v(-16.37, -34.66) * mm});
            skLineSegment(sketch, "E2908", {"start": v(-16.37, -34.66) * mm, "end": v(-17.35, -34.4) * mm});
            skLineSegment(sketch, "E2909", {"start": v(-17.35, -34.4) * mm, "end": v(-17.62, -34.39) * mm});
            skLineSegment(sketch, "E2910", {"start": v(-17.62, -34.39) * mm, "end": v(-17.8, -34.43) * mm});
            skLineSegment(sketch, "E2911", {"start": v(-17.8, -34.43) * mm, "end": v(-17.9, -34.53) * mm});
            skLineSegment(sketch, "E2912", {"start": v(-17.9, -34.53) * mm, "end": v(-17.95, -34.7) * mm});
            skLineSegment(sketch, "E2913", {"start": v(-17.95, -34.7) * mm, "end": v(-17.94, -34.9) * mm});
            skLineSegment(sketch, "E2914", {"start": v(-17.94, -34.9) * mm, "end": v(-17.83, -35.25) * mm});
            skLineSegment(sketch, "E2915", {"start": v(-17.83, -35.25) * mm, "end": v(-17.5, -35.83) * mm});
            skLineSegment(sketch, "E2916", {"start": v(-17.5, -35.83) * mm, "end": v(-17.24, -36.14) * mm});
            skLineSegment(sketch, "E2917", {"start": v(-17.24, -36.14) * mm, "end": v(-17.04, -36.3) * mm});
            skLineSegment(sketch, "E2918", {"start": v(-17.04, -36.3) * mm, "end": v(-16.78, -36.43) * mm});
            skLineSegment(sketch, "E2919", {"start": v(-16.78, -36.43) * mm, "end": v(-16.5, -36.5) * mm});
            skLineSegment(sketch, "E2920", {"start": v(-16.5, -36.5) * mm, "end": v(-16.32, -36.54) * mm});
            skLineSegment(sketch, "E2921", {"start": v(-16.32, -36.54) * mm, "end": v(-15.96, -36.55) * mm});
            skLineSegment(sketch, "E2922", {"start": v(-10.8, -34.93) * mm, "end": v(-10.53, -34.96) * mm});
            skLineSegment(sketch, "E2923", {"start": v(-10.53, -34.96) * mm, "end": v(-10.14, -34.98) * mm});
            skLineSegment(sketch, "E2924", {"start": v(-10.14, -34.98) * mm, "end": v(-9.62, -34.94) * mm});
            skLineSegment(sketch, "E2925", {"start": v(-9.62, -34.94) * mm, "end": v(-9.15, -34.83) * mm});
            skLineSegment(sketch, "E2926", {"start": v(-9.15, -34.83) * mm, "end": v(-8.72, -34.65) * mm});
            skLineSegment(sketch, "E2927", {"start": v(-8.72, -34.65) * mm, "end": v(-8.55, -34.5) * mm});
            skLineSegment(sketch, "E2928", {"start": v(-8.55, -34.5) * mm, "end": v(-8.45, -34.34) * mm});
            skLineSegment(sketch, "E2929", {"start": v(-8.45, -34.34) * mm, "end": v(-8.42, -34.16) * mm});
            skLineSegment(sketch, "E2930", {"start": v(-8.42, -34.16) * mm, "end": v(-8.45, -33.97) * mm});
            skLineSegment(sketch, "E2931", {"start": v(-8.45, -33.97) * mm, "end": v(-8.62, -33.64) * mm});
            skLineSegment(sketch, "E2932", {"start": v(-8.62, -33.64) * mm, "end": v(-8.88, -33.34) * mm});
            skLineSegment(sketch, "E2933", {"start": v(-8.88, -33.34) * mm, "end": v(-9.11, -33.13) * mm});
            skLineSegment(sketch, "E2934", {"start": v(-9.11, -33.13) * mm, "end": v(-9.35, -32.98) * mm});
            skLineSegment(sketch, "E2935", {"start": v(-9.35, -32.98) * mm, "end": v(-9.72, -32.8) * mm});
            skLineSegment(sketch, "E2936", {"start": v(-9.72, -32.8) * mm, "end": v(-10.32, -32.6) * mm});
            skLineSegment(sketch, "E2937", {"start": v(-10.32, -32.6) * mm, "end": v(-10.76, -32.48) * mm});
            skLineSegment(sketch, "E2938", {"start": v(-10.76, -32.48) * mm, "end": v(-11.2, -32.39) * mm});
            skLineSegment(sketch, "E2939", {"start": v(-11.2, -32.39) * mm, "end": v(-11.75, -32.33) * mm});
            skLineSegment(sketch, "E2940", {"start": v(-11.75, -32.33) * mm, "end": v(-11.99, -32.34) * mm});
            skLineSegment(sketch, "E2941", {"start": v(-11.99, -32.34) * mm, "end": v(-12.28, -32.39) * mm});
            skLineSegment(sketch, "E2942", {"start": v(-12.28, -32.39) * mm, "end": v(-12.5, -32.53) * mm});
            skLineSegment(sketch, "E2943", {"start": v(-12.5, -32.53) * mm, "end": v(-12.6, -32.7) * mm});
            skLineSegment(sketch, "E2944", {"start": v(-12.6, -32.7) * mm, "end": v(-12.62, -33) * mm});
            skLineSegment(sketch, "E2945", {"start": v(-12.62, -33) * mm, "end": v(-12.57, -33.36) * mm});
            skLineSegment(sketch, "E2946", {"start": v(-12.57, -33.36) * mm, "end": v(-12.49, -33.6) * mm});
            skLineSegment(sketch, "E2947", {"start": v(-12.49, -33.6) * mm, "end": v(-12.28, -34.05) * mm});
            skLineSegment(sketch, "E2948", {"start": v(-12.28, -34.05) * mm, "end": v(-12.11, -34.3) * mm});
            skLineSegment(sketch, "E2949", {"start": v(-12.11, -34.3) * mm, "end": v(-11.99, -34.43) * mm});
            skLineSegment(sketch, "E2950", {"start": v(-11.99, -34.43) * mm, "end": v(-11.62, -34.66) * mm});
            skLineSegment(sketch, "E2951", {"start": v(-11.62, -34.66) * mm, "end": v(-11.4, -34.76) * mm});
            skLineSegment(sketch, "E2952", {"start": v(-11.4, -34.76) * mm, "end": v(-10.8, -34.93) * mm});
            skLineSegment(sketch, "E2953", {"start": v(-11.48, -31.02) * mm, "end": v(-11.2, -31.1) * mm});
            skLineSegment(sketch, "E2954", {"start": v(-11.2, -31.1) * mm, "end": v(-10.9, -31.17) * mm});
            skLineSegment(sketch, "E2955", {"start": v(-10.9, -31.17) * mm, "end": v(-10.63, -31.19) * mm});
            skLineSegment(sketch, "E2956", {"start": v(-10.63, -31.19) * mm, "end": v(-10.4, -31.16) * mm});
            skLineSegment(sketch, "E2957", {"start": v(-10.4, -31.16) * mm, "end": v(-10.19, -31.1) * mm});
            skLineSegment(sketch, "E2958", {"start": v(-10.19, -31.1) * mm, "end": v(-10.04, -31) * mm});
            skLineSegment(sketch, "E2959", {"start": v(-10.04, -31) * mm, "end": v(-9.93, -30.81) * mm});
            skLineSegment(sketch, "E2960", {"start": v(-9.93, -30.81) * mm, "end": v(-9.9, -30.62) * mm});
            skLineSegment(sketch, "E2961", {"start": v(-9.9, -30.62) * mm, "end": v(-10, -30.41) * mm});
            skLineSegment(sketch, "E2962", {"start": v(-10, -30.41) * mm, "end": v(-10.1, -30.28) * mm});
            skLineSegment(sketch, "E2963", {"start": v(-10.1, -30.28) * mm, "end": v(-10.29, -30.08) * mm});
            skLineSegment(sketch, "E2964", {"start": v(-10.29, -30.08) * mm, "end": v(-10.62, -29.85) * mm});
            skLineSegment(sketch, "E2965", {"start": v(-10.62, -29.85) * mm, "end": v(-10.96, -29.69) * mm});
            skLineSegment(sketch, "E2966", {"start": v(-10.96, -29.69) * mm, "end": v(-11.3, -29.59) * mm});
            skLineSegment(sketch, "E2967", {"start": v(-11.3, -29.59) * mm, "end": v(-11.59, -29.56) * mm});
            skLineSegment(sketch, "E2968", {"start": v(-11.59, -29.56) * mm, "end": v(-11.84, -29.6) * mm});
            skLineSegment(sketch, "E2969", {"start": v(-11.84, -29.6) * mm, "end": v(-12.04, -29.69) * mm});
            skLineSegment(sketch, "E2970", {"start": v(-12.04, -29.69) * mm, "end": v(-12.24, -29.84) * mm});
            skLineSegment(sketch, "E2971", {"start": v(-12.24, -29.84) * mm, "end": v(-12.36, -30.03) * mm});
            skLineSegment(sketch, "E2972", {"start": v(-12.36, -30.03) * mm, "end": v(-12.38, -30.16) * mm});
            skLineSegment(sketch, "E2973", {"start": v(-12.38, -30.16) * mm, "end": v(-12.37, -30.29) * mm});
            skLineSegment(sketch, "E2974", {"start": v(-12.37, -30.29) * mm, "end": v(-12.28, -30.47) * mm});
            skLineSegment(sketch, "E2975", {"start": v(-12.28, -30.47) * mm, "end": v(-12.12, -30.64) * mm});
            skLineSegment(sketch, "E2976", {"start": v(-12.12, -30.64) * mm, "end": v(-11.91, -30.8) * mm});
            skLineSegment(sketch, "E2977", {"start": v(-11.91, -30.8) * mm, "end": v(-11.66, -30.94) * mm});
            skLineSegment(sketch, "E2978", {"start": v(-11.66, -30.94) * mm, "end": v(-11.48, -31.02) * mm});
            skLineSegment(sketch, "E2979", {"start": v(-12.85, -27.57) * mm, "end": v(-12.69, -27.64) * mm});
            skLineSegment(sketch, "E2980", {"start": v(-12.69, -27.64) * mm, "end": v(-12.5, -27.66) * mm});
            skLineSegment(sketch, "E2981", {"start": v(-12.5, -27.66) * mm, "end": v(-12.26, -27.6) * mm});
            skLineSegment(sketch, "E2982", {"start": v(-12.26, -27.6) * mm, "end": v(-12.11, -27.52) * mm});
            skLineSegment(sketch, "E2983", {"start": v(-12.11, -27.52) * mm, "end": v(-12.03, -27.43) * mm});
            skLineSegment(sketch, "E2984", {"start": v(-12.03, -27.43) * mm, "end": v(-12.03, -27.33) * mm});
            skLineSegment(sketch, "E2985", {"start": v(-12.03, -27.33) * mm, "end": v(-12.1, -27.25) * mm});
            skLineSegment(sketch, "E2986", {"start": v(-12.1, -27.25) * mm, "end": v(-12.18, -27.2) * mm});
            skLineSegment(sketch, "E2987", {"start": v(-12.18, -27.2) * mm, "end": v(-12.32, -27.15) * mm});
            skLineSegment(sketch, "E2988", {"start": v(-12.32, -27.15) * mm, "end": v(-12.52, -27.14) * mm});
            skLineSegment(sketch, "E2989", {"start": v(-12.52, -27.14) * mm, "end": v(-12.71, -27.17) * mm});
            skLineSegment(sketch, "E2990", {"start": v(-12.71, -27.17) * mm, "end": v(-12.86, -27.24) * mm});
            skLineSegment(sketch, "E2991", {"start": v(-12.86, -27.24) * mm, "end": v(-12.96, -27.31) * mm});
            skLineSegment(sketch, "E2992", {"start": v(-12.96, -27.31) * mm, "end": v(-12.98, -27.43) * mm});
            skLineSegment(sketch, "E2993", {"start": v(-12.98, -27.43) * mm, "end": v(-12.92, -27.52) * mm});
            skLineSegment(sketch, "E2994", {"start": v(-12.92, -27.52) * mm, "end": v(-12.85, -27.57) * mm});
            skLineSegment(sketch, "E2995", {"start": v(-9.76, -28.56) * mm, "end": v(-9.53, -28.44) * mm});
            skLineSegment(sketch, "E2996", {"start": v(-9.53, -28.44) * mm, "end": v(-9.34, -28.25) * mm});
            skLineSegment(sketch, "E2997", {"start": v(-9.34, -28.25) * mm, "end": v(-9.2, -27.96) * mm});
            skLineSegment(sketch, "E2998", {"start": v(-9.2, -27.96) * mm, "end": v(-9.17, -27.76) * mm});
            skLineSegment(sketch, "E2999", {"start": v(-9.17, -27.76) * mm, "end": v(-9.26, -27.61) * mm});
            skLineSegment(sketch, "E3000", {"start": v(-9.26, -27.61) * mm, "end": v(-9.44, -27.53) * mm});
            skLineSegment(sketch, "E3001", {"start": v(-9.44, -27.53) * mm, "end": v(-9.62, -27.53) * mm});
            skLineSegment(sketch, "E3002", {"start": v(-9.62, -27.53) * mm, "end": v(-9.88, -27.6) * mm});
            skLineSegment(sketch, "E3003", {"start": v(-9.88, -27.6) * mm, "end": v(-10.11, -27.7) * mm});
            skLineSegment(sketch, "E3004", {"start": v(-10.11, -27.7) * mm, "end": v(-10.33, -27.85) * mm});
            skLineSegment(sketch, "E3005", {"start": v(-10.33, -27.85) * mm, "end": v(-10.5, -28.05) * mm});
            skLineSegment(sketch, "E3006", {"start": v(-10.5, -28.05) * mm, "end": v(-10.57, -28.18) * mm});
            skLineSegment(sketch, "E3007", {"start": v(-10.57, -28.18) * mm, "end": v(-10.6, -28.37) * mm});
            skLineSegment(sketch, "E3008", {"start": v(-10.6, -28.37) * mm, "end": v(-10.56, -28.48) * mm});
            skLineSegment(sketch, "E3009", {"start": v(-10.56, -28.48) * mm, "end": v(-10.5, -28.57) * mm});
            skLineSegment(sketch, "E3010", {"start": v(-10.5, -28.57) * mm, "end": v(-10.31, -28.65) * mm});
            skLineSegment(sketch, "E3011", {"start": v(-10.31, -28.65) * mm, "end": v(-10.13, -28.65) * mm});
            skLineSegment(sketch, "E3012", {"start": v(-10.13, -28.65) * mm, "end": v(-9.9, -28.6) * mm});
            skLineSegment(sketch, "E3013", {"start": v(-9.9, -28.6) * mm, "end": v(-9.76, -28.56) * mm});
            skLineSegment(sketch, "E3014", {"start": v(-7.32, -29.14) * mm, "end": v(-6.97, -28.95) * mm});
            skLineSegment(sketch, "E3015", {"start": v(-6.97, -28.95) * mm, "end": v(-6.88, -28.73) * mm});
            skLineSegment(sketch, "E3016", {"start": v(-6.88, -28.73) * mm, "end": v(-6.93, -28.5) * mm});
            skLineSegment(sketch, "E3017", {"start": v(-6.93, -28.5) * mm, "end": v(-7.09, -28.32) * mm});
            skLineSegment(sketch, "E3018", {"start": v(-7.09, -28.32) * mm, "end": v(-7.31, -28.2) * mm});
            skLineSegment(sketch, "E3019", {"start": v(-7.31, -28.2) * mm, "end": v(-7.59, -28.23) * mm});
            skLineSegment(sketch, "E3020", {"start": v(-7.59, -28.23) * mm, "end": v(-7.78, -28.33) * mm});
            skLineSegment(sketch, "E3021", {"start": v(-7.78, -28.33) * mm, "end": v(-7.96, -28.5) * mm});
            skLineSegment(sketch, "E3022", {"start": v(-7.96, -28.5) * mm, "end": v(-8.04, -28.69) * mm});
            skLineSegment(sketch, "E3023", {"start": v(-8.04, -28.69) * mm, "end": v(-7.95, -28.95) * mm});
            skLineSegment(sketch, "E3024", {"start": v(-7.95, -28.95) * mm, "end": v(-7.76, -29.09) * mm});
            skLineSegment(sketch, "E3025", {"start": v(-7.76, -29.09) * mm, "end": v(-7.51, -29.15) * mm});
            skLineSegment(sketch, "E3026", {"start": v(-7.51, -29.15) * mm, "end": v(-7.32, -29.14) * mm});
            skLineSegment(sketch, "E3027", {"start": v(-7.78, -31.74) * mm, "end": v(-7.36, -31.9) * mm});
            skLineSegment(sketch, "E3028", {"start": v(-7.36, -31.9) * mm, "end": v(-6.93, -32) * mm});
            skLineSegment(sketch, "E3029", {"start": v(-6.93, -32) * mm, "end": v(-6.54, -32.06) * mm});
            skLineSegment(sketch, "E3030", {"start": v(-6.54, -32.06) * mm, "end": v(-6.21, -32.05) * mm});
            skLineSegment(sketch, "E3031", {"start": v(-6.21, -32.05) * mm, "end": v(-6, -31.96) * mm});
            skLineSegment(sketch, "E3032", {"start": v(-6, -31.96) * mm, "end": v(-5.88, -31.78) * mm});
            skLineSegment(sketch, "E3033", {"start": v(-5.88, -31.78) * mm, "end": v(-5.86, -31.56) * mm});
            skLineSegment(sketch, "E3034", {"start": v(-5.86, -31.56) * mm, "end": v(-6, -31.27) * mm});
            skLineSegment(sketch, "E3035", {"start": v(-6, -31.27) * mm, "end": v(-6.18, -31.06) * mm});
            skLineSegment(sketch, "E3036", {"start": v(-6.18, -31.06) * mm, "end": v(-6.48, -30.83) * mm});
            skLineSegment(sketch, "E3037", {"start": v(-6.48, -30.83) * mm, "end": v(-6.73, -30.7) * mm});
            skLineSegment(sketch, "E3038", {"start": v(-6.73, -30.7) * mm, "end": v(-7.28, -30.49) * mm});
            skLineSegment(sketch, "E3039", {"start": v(-7.28, -30.49) * mm, "end": v(-7.7, -30.4) * mm});
            skLineSegment(sketch, "E3040", {"start": v(-7.7, -30.4) * mm, "end": v(-7.95, -30.4) * mm});
            skLineSegment(sketch, "E3041", {"start": v(-7.95, -30.4) * mm, "end": v(-8.18, -30.44) * mm});
            skLineSegment(sketch, "E3042", {"start": v(-8.18, -30.44) * mm, "end": v(-8.43, -30.59) * mm});
            skLineSegment(sketch, "E3043", {"start": v(-8.43, -30.59) * mm, "end": v(-8.56, -30.74) * mm});
            skLineSegment(sketch, "E3044", {"start": v(-8.56, -30.74) * mm, "end": v(-8.62, -30.93) * mm});
            skLineSegment(sketch, "E3045", {"start": v(-8.62, -30.93) * mm, "end": v(-8.6, -31.06) * mm});
            skLineSegment(sketch, "E3046", {"start": v(-8.6, -31.06) * mm, "end": v(-8.48, -31.25) * mm});
            skLineSegment(sketch, "E3047", {"start": v(-8.48, -31.25) * mm, "end": v(-8.3, -31.43) * mm});
            skLineSegment(sketch, "E3048", {"start": v(-8.3, -31.43) * mm, "end": v(-8.06, -31.59) * mm});
            skLineSegment(sketch, "E3049", {"start": v(-8.06, -31.59) * mm, "end": v(-7.78, -31.74) * mm});
            skLineSegment(sketch, "E3050", {"start": v(-6.84, -33.85) * mm, "end": v(-6.59, -33.86) * mm});
            skLineSegment(sketch, "E3051", {"start": v(-6.59, -33.86) * mm, "end": v(-6.32, -33.84) * mm});
            skLineSegment(sketch, "E3052", {"start": v(-6.32, -33.84) * mm, "end": v(-6.06, -33.77) * mm});
            skLineSegment(sketch, "E3053", {"start": v(-6.06, -33.77) * mm, "end": v(-5.84, -33.62) * mm});
            skLineSegment(sketch, "E3054", {"start": v(-5.84, -33.62) * mm, "end": v(-5.77, -33.5) * mm});
            skLineSegment(sketch, "E3055", {"start": v(-5.77, -33.5) * mm, "end": v(-5.8, -33.42) * mm});
            skLineSegment(sketch, "E3056", {"start": v(-5.8, -33.42) * mm, "end": v(-5.9, -33.37) * mm});
            skLineSegment(sketch, "E3057", {"start": v(-5.9, -33.37) * mm, "end": v(-6.04, -33.32) * mm});
            skLineSegment(sketch, "E3058", {"start": v(-6.04, -33.32) * mm, "end": v(-6.5, -33.22) * mm});
            skLineSegment(sketch, "E3059", {"start": v(-6.5, -33.22) * mm, "end": v(-6.81, -33.19) * mm});
            skLineSegment(sketch, "E3060", {"start": v(-6.81, -33.19) * mm, "end": v(-7.06, -33.18) * mm});
            skLineSegment(sketch, "E3061", {"start": v(-7.06, -33.18) * mm, "end": v(-7.26, -33.2) * mm});
            skLineSegment(sketch, "E3062", {"start": v(-7.26, -33.2) * mm, "end": v(-7.4, -33.25) * mm});
            skLineSegment(sketch, "E3063", {"start": v(-7.4, -33.25) * mm, "end": v(-7.5, -33.33) * mm});
            skLineSegment(sketch, "E3064", {"start": v(-7.5, -33.33) * mm, "end": v(-7.5, -33.48) * mm});
            skLineSegment(sketch, "E3065", {"start": v(-7.5, -33.48) * mm, "end": v(-7.37, -33.66) * mm});
            skLineSegment(sketch, "E3066", {"start": v(-7.37, -33.66) * mm, "end": v(-7.22, -33.75) * mm});
            skLineSegment(sketch, "E3067", {"start": v(-7.22, -33.75) * mm, "end": v(-7.03, -33.81) * mm});
            skLineSegment(sketch, "E3068", {"start": v(-7.03, -33.81) * mm, "end": v(-6.84, -33.85) * mm});
            skLineSegment(sketch, "E3069", {"start": v(-3.13, -32.35) * mm, "end": v(-2.8, -32.32) * mm});
            skLineSegment(sketch, "E3070", {"start": v(-2.8, -32.32) * mm, "end": v(-2.32, -32.2) * mm});
            skLineSegment(sketch, "E3071", {"start": v(-2.32, -32.2) * mm, "end": v(-1.99, -32.03) * mm});
            skLineSegment(sketch, "E3072", {"start": v(-1.99, -32.03) * mm, "end": v(-1.82, -31.87) * mm});
            skLineSegment(sketch, "E3073", {"start": v(-1.82, -31.87) * mm, "end": v(-1.75, -31.69) * mm});
            skLineSegment(sketch, "E3074", {"start": v(-1.75, -31.69) * mm, "end": v(-1.78, -31.5) * mm});
            skLineSegment(sketch, "E3075", {"start": v(-1.78, -31.5) * mm, "end": v(-1.95, -31.28) * mm});
            skLineSegment(sketch, "E3076", {"start": v(-1.95, -31.28) * mm, "end": v(-2.3, -31.03) * mm});
            skLineSegment(sketch, "E3077", {"start": v(-2.3, -31.03) * mm, "end": v(-2.7, -30.86) * mm});
            skLineSegment(sketch, "E3078", {"start": v(-2.7, -30.86) * mm, "end": v(-3.09, -30.78) * mm});
            skLineSegment(sketch, "E3079", {"start": v(-3.09, -30.78) * mm, "end": v(-3.5, -30.74) * mm});
            skLineSegment(sketch, "E3080", {"start": v(-3.5, -30.74) * mm, "end": v(-3.9, -30.73) * mm});
            skLineSegment(sketch, "E3081", {"start": v(-3.9, -30.73) * mm, "end": v(-4.35, -30.75) * mm});
            skLineSegment(sketch, "E3082", {"start": v(-4.35, -30.75) * mm, "end": v(-4.64, -30.8) * mm});
            skLineSegment(sketch, "E3083", {"start": v(-4.64, -30.8) * mm, "end": v(-4.82, -30.9) * mm});
            skLineSegment(sketch, "E3084", {"start": v(-4.82, -30.9) * mm, "end": v(-4.9, -31.12) * mm});
            skLineSegment(sketch, "E3085", {"start": v(-4.9, -31.12) * mm, "end": v(-4.86, -31.31) * mm});
            skLineSegment(sketch, "E3086", {"start": v(-4.86, -31.31) * mm, "end": v(-4.72, -31.56) * mm});
            skLineSegment(sketch, "E3087", {"start": v(-4.72, -31.56) * mm, "end": v(-4.48, -31.86) * mm});
            skLineSegment(sketch, "E3088", {"start": v(-4.48, -31.86) * mm, "end": v(-4.24, -32.05) * mm});
            skLineSegment(sketch, "E3089", {"start": v(-4.24, -32.05) * mm, "end": v(-3.96, -32.2) * mm});
            skLineSegment(sketch, "E3090", {"start": v(-3.96, -32.2) * mm, "end": v(-3.74, -32.27) * mm});
            skLineSegment(sketch, "E3091", {"start": v(-3.74, -32.27) * mm, "end": v(-3.38, -32.34) * mm});
            skLineSegment(sketch, "E3092", {"start": v(-3.38, -32.34) * mm, "end": v(-3.13, -32.35) * mm});
            skLineSegment(sketch, "E3093", {"start": v(-4.65, -29.45) * mm, "end": v(-4.34, -29.52) * mm});
            skLineSegment(sketch, "E3094", {"start": v(-4.34, -29.52) * mm, "end": v(-4.06, -29.53) * mm});
            skLineSegment(sketch, "E3095", {"start": v(-4.06, -29.53) * mm, "end": v(-3.8, -29.47) * mm});
            skLineSegment(sketch, "E3096", {"start": v(-3.8, -29.47) * mm, "end": v(-3.65, -29.4) * mm});
            skLineSegment(sketch, "E3097", {"start": v(-3.65, -29.4) * mm, "end": v(-3.56, -29.3) * mm});
            skLineSegment(sketch, "E3098", {"start": v(-3.56, -29.3) * mm, "end": v(-3.55, -29.2) * mm});
            skLineSegment(sketch, "E3099", {"start": v(-3.55, -29.2) * mm, "end": v(-3.6, -29.1) * mm});
            skLineSegment(sketch, "E3100", {"start": v(-3.6, -29.1) * mm, "end": v(-3.74, -28.96) * mm});
            skLineSegment(sketch, "E3101", {"start": v(-3.74, -28.96) * mm, "end": v(-3.94, -28.84) * mm});
            skLineSegment(sketch, "E3102", {"start": v(-3.94, -28.84) * mm, "end": v(-4.27, -28.7) * mm});
            skLineSegment(sketch, "E3103", {"start": v(-4.27, -28.7) * mm, "end": v(-4.62, -28.6) * mm});
            skLineSegment(sketch, "E3104", {"start": v(-4.62, -28.6) * mm, "end": v(-4.84, -28.57) * mm});
            skLineSegment(sketch, "E3105", {"start": v(-4.84, -28.57) * mm, "end": v(-5.05, -28.6) * mm});
            skLineSegment(sketch, "E3106", {"start": v(-5.05, -28.6) * mm, "end": v(-5.27, -28.7) * mm});
            skLineSegment(sketch, "E3107", {"start": v(-5.27, -28.7) * mm, "end": v(-5.36, -28.78) * mm});
            skLineSegment(sketch, "E3108", {"start": v(-5.36, -28.78) * mm, "end": v(-5.4, -28.87) * mm});
            skLineSegment(sketch, "E3109", {"start": v(-5.4, -28.87) * mm, "end": v(-5.38, -28.96) * mm});
            skLineSegment(sketch, "E3110", {"start": v(-5.38, -28.96) * mm, "end": v(-5.3, -29.1) * mm});
            skLineSegment(sketch, "E3111", {"start": v(-5.3, -29.1) * mm, "end": v(-5.11, -29.24) * mm});
            skLineSegment(sketch, "E3112", {"start": v(-5.11, -29.24) * mm, "end": v(-4.91, -29.35) * mm});
            skLineSegment(sketch, "E3113", {"start": v(-4.91, -29.35) * mm, "end": v(-4.65, -29.45) * mm});
            skLineSegment(sketch, "E3114", {"start": v(-4.3, -27.53) * mm, "end": v(-4.03, -27.58) * mm});
            skLineSegment(sketch, "E3115", {"start": v(-4.03, -27.58) * mm, "end": v(-3.73, -27.49) * mm});
            skLineSegment(sketch, "E3116", {"start": v(-3.73, -27.49) * mm, "end": v(-3.64, -27.3) * mm});
            skLineSegment(sketch, "E3117", {"start": v(-3.64, -27.3) * mm, "end": v(-3.7, -27.1) * mm});
            skLineSegment(sketch, "E3118", {"start": v(-3.7, -27.1) * mm, "end": v(-3.94, -26.99) * mm});
            skLineSegment(sketch, "E3119", {"start": v(-3.94, -26.99) * mm, "end": v(-4.14, -26.99) * mm});
            skLineSegment(sketch, "E3120", {"start": v(-4.14, -26.99) * mm, "end": v(-4.4, -27.13) * mm});
            skLineSegment(sketch, "E3121", {"start": v(-4.4, -27.13) * mm, "end": v(-4.47, -27.32) * mm});
            skLineSegment(sketch, "E3122", {"start": v(-4.47, -27.32) * mm, "end": v(-4.36, -27.49) * mm});
            skLineSegment(sketch, "E3123", {"start": v(-4.36, -27.49) * mm, "end": v(-4.3, -27.53) * mm});
            skLineSegment(sketch, "E3124", {"start": v(-1.44, -27.62) * mm, "end": v(-1.2, -27.63) * mm});
            skLineSegment(sketch, "E3125", {"start": v(-1.2, -27.63) * mm, "end": v(-0.94, -27.59) * mm});
            skLineSegment(sketch, "E3126", {"start": v(-0.94, -27.59) * mm, "end": v(-0.81, -27.53) * mm});
            skLineSegment(sketch, "E3127", {"start": v(-0.81, -27.53) * mm, "end": v(-0.76, -27.47) * mm});
            skLineSegment(sketch, "E3128", {"start": v(-0.76, -27.47) * mm, "end": v(-0.78, -27.38) * mm});
            skLineSegment(sketch, "E3129", {"start": v(-0.78, -27.38) * mm, "end": v(-0.9, -27.3) * mm});
            skLineSegment(sketch, "E3130", {"start": v(-0.9, -27.3) * mm, "end": v(-1.26, -27.2) * mm});
            skLineSegment(sketch, "E3131", {"start": v(-1.26, -27.2) * mm, "end": v(-1.53, -27.19) * mm});
            skLineSegment(sketch, "E3132", {"start": v(-1.53, -27.19) * mm, "end": v(-1.75, -27.2) * mm});
            skLineSegment(sketch, "E3133", {"start": v(-1.75, -27.2) * mm, "end": v(-1.87, -27.26) * mm});
            skLineSegment(sketch, "E3134", {"start": v(-1.87, -27.26) * mm, "end": v(-1.98, -27.34) * mm});
            skLineSegment(sketch, "E3135", {"start": v(-1.98, -27.34) * mm, "end": v(-2, -27.39) * mm});
            skLineSegment(sketch, "E3136", {"start": v(-2, -27.39) * mm, "end": v(-1.98, -27.47) * mm});
            skLineSegment(sketch, "E3137", {"start": v(-1.98, -27.47) * mm, "end": v(-1.88, -27.53) * mm});
            skLineSegment(sketch, "E3138", {"start": v(-1.88, -27.53) * mm, "end": v(-1.72, -27.58) * mm});
            skLineSegment(sketch, "E3139", {"start": v(-1.72, -27.58) * mm, "end": v(-1.44, -27.62) * mm});
            skLineSegment(sketch, "E3140", {"start": v(-1.2, -29.76) * mm, "end": v(-0.82, -29.84) * mm});
            skLineSegment(sketch, "E3141", {"start": v(-0.82, -29.84) * mm, "end": v(-0.5, -29.87) * mm});
            skLineSegment(sketch, "E3142", {"start": v(-0.5, -29.87) * mm, "end": v(-0.2, -29.86) * mm});
            skLineSegment(sketch, "E3143", {"start": v(-0.2, -29.86) * mm, "end": v(0.05, -29.8) * mm});
            skLineSegment(sketch, "E3144", {"start": v(0.05, -29.8) * mm, "end": v(0.23, -29.7) * mm});
            skLineSegment(sketch, "E3145", {"start": v(0.23, -29.7) * mm, "end": v(0.34, -29.5) * mm});
            skLineSegment(sketch, "E3146", {"start": v(0.34, -29.5) * mm, "end": v(0.34, -29.37) * mm});
            skLineSegment(sketch, "E3147", {"start": v(0.34, -29.37) * mm, "end": v(0.24, -29.18) * mm});
            skLineSegment(sketch, "E3148", {"start": v(0.24, -29.18) * mm, "end": v(0.05, -29) * mm});
            skLineSegment(sketch, "E3149", {"start": v(0.05, -29) * mm, "end": v(-0.44, -28.78) * mm});
            skLineSegment(sketch, "E3150", {"start": v(-0.44, -28.78) * mm, "end": v(-1.02, -28.64) * mm});
            skLineSegment(sketch, "E3151", {"start": v(-1.02, -28.64) * mm, "end": v(-1.43, -28.6) * mm});
            skLineSegment(sketch, "E3152", {"start": v(-1.43, -28.6) * mm, "end": v(-1.69, -28.6) * mm});
            skLineSegment(sketch, "E3153", {"start": v(-1.69, -28.6) * mm, "end": v(-1.87, -28.64) * mm});
            skLineSegment(sketch, "E3154", {"start": v(-1.87, -28.64) * mm, "end": v(-2.08, -28.73) * mm});
            skLineSegment(sketch, "E3155", {"start": v(-2.08, -28.73) * mm, "end": v(-2.23, -28.89) * mm});
            skLineSegment(sketch, "E3156", {"start": v(-2.23, -28.89) * mm, "end": v(-2.26, -29.07) * mm});
            skLineSegment(sketch, "E3157", {"start": v(-2.26, -29.07) * mm, "end": v(-2.22, -29.19) * mm});
            skLineSegment(sketch, "E3158", {"start": v(-2.22, -29.19) * mm, "end": v(-2.1, -29.33) * mm});
            skLineSegment(sketch, "E3159", {"start": v(-2.1, -29.33) * mm, "end": v(-1.86, -29.5) * mm});
            skLineSegment(sketch, "E3160", {"start": v(-1.86, -29.5) * mm, "end": v(-1.58, -29.64) * mm});
            skLineSegment(sketch, "E3161", {"start": v(-1.58, -29.64) * mm, "end": v(-1.2, -29.76) * mm});
            skLineSegment(sketch, "E3162", {"start": v(1.23, -27.66) * mm, "end": v(1.62, -27.68) * mm});
            skLineSegment(sketch, "E3163", {"start": v(1.62, -27.68) * mm, "end": v(1.91, -27.65) * mm});
            skLineSegment(sketch, "E3164", {"start": v(1.91, -27.65) * mm, "end": v(2.07, -27.59) * mm});
            skLineSegment(sketch, "E3165", {"start": v(2.07, -27.59) * mm, "end": v(2.13, -27.53) * mm});
            skLineSegment(sketch, "E3166", {"start": v(2.13, -27.53) * mm, "end": v(2.16, -27.46) * mm});
            skLineSegment(sketch, "E3167", {"start": v(2.16, -27.46) * mm, "end": v(2.11, -27.37) * mm});
            skLineSegment(sketch, "E3168", {"start": v(2.11, -27.37) * mm, "end": v(1.9, -27.25) * mm});
            skLineSegment(sketch, "E3169", {"start": v(1.9, -27.25) * mm, "end": v(1.57, -27.17) * mm});
            skLineSegment(sketch, "E3170", {"start": v(1.57, -27.17) * mm, "end": v(1.34, -27.15) * mm});
            skLineSegment(sketch, "E3171", {"start": v(1.34, -27.15) * mm, "end": v(1.03, -27.17) * mm});
            skLineSegment(sketch, "E3172", {"start": v(1.03, -27.17) * mm, "end": v(0.89, -27.23) * mm});
            skLineSegment(sketch, "E3173", {"start": v(0.89, -27.23) * mm, "end": v(0.81, -27.35) * mm});
            skLineSegment(sketch, "E3174", {"start": v(0.81, -27.35) * mm, "end": v(0.82, -27.44) * mm});
            skLineSegment(sketch, "E3175", {"start": v(0.82, -27.44) * mm, "end": v(0.92, -27.54) * mm});
            skLineSegment(sketch, "E3176", {"start": v(0.92, -27.54) * mm, "end": v(1.05, -27.61) * mm});
            skLineSegment(sketch, "E3177", {"start": v(1.05, -27.61) * mm, "end": v(1.23, -27.66) * mm});
            skLineSegment(sketch, "E3178", {"start": v(2.74, -29.62) * mm, "end": v(3.06, -29.47) * mm});
            skLineSegment(sketch, "E3179", {"start": v(3.06, -29.47) * mm, "end": v(3.47, -29.16) * mm});
            skLineSegment(sketch, "E3180", {"start": v(3.47, -29.16) * mm, "end": v(3.65, -28.92) * mm});
            skLineSegment(sketch, "E3181", {"start": v(3.65, -28.92) * mm, "end": v(3.68, -28.8) * mm});
            skLineSegment(sketch, "E3182", {"start": v(3.68, -28.8) * mm, "end": v(3.6, -28.64) * mm});
            skLineSegment(sketch, "E3183", {"start": v(3.6, -28.64) * mm, "end": v(3.4, -28.58) * mm});
            skLineSegment(sketch, "E3184", {"start": v(3.4, -28.58) * mm, "end": v(3.17, -28.56) * mm});
            skLineSegment(sketch, "E3185", {"start": v(3.17, -28.56) * mm, "end": v(2.76, -28.57) * mm});
            skLineSegment(sketch, "E3186", {"start": v(2.76, -28.57) * mm, "end": v(2.06, -28.58) * mm});
            skLineSegment(sketch, "E3187", {"start": v(2.06, -28.58) * mm, "end": v(1.78, -28.6) * mm});
            skLineSegment(sketch, "E3188", {"start": v(1.78, -28.6) * mm, "end": v(1.5, -28.65) * mm});
            skLineSegment(sketch, "E3189", {"start": v(1.5, -28.65) * mm, "end": v(1.35, -28.77) * mm});
            skLineSegment(sketch, "E3190", {"start": v(1.35, -28.77) * mm, "end": v(1.29, -28.96) * mm});
            skLineSegment(sketch, "E3191", {"start": v(1.29, -28.96) * mm, "end": v(1.3, -29.1) * mm});
            skLineSegment(sketch, "E3192", {"start": v(1.3, -29.1) * mm, "end": v(1.45, -29.33) * mm});
            skLineSegment(sketch, "E3193", {"start": v(1.45, -29.33) * mm, "end": v(1.65, -29.49) * mm});
            skLineSegment(sketch, "E3194", {"start": v(1.65, -29.49) * mm, "end": v(1.97, -29.63) * mm});
            skLineSegment(sketch, "E3195", {"start": v(1.97, -29.63) * mm, "end": v(2.25, -29.71) * mm});
            skLineSegment(sketch, "E3196", {"start": v(2.25, -29.71) * mm, "end": v(2.49, -29.7) * mm});
            skLineSegment(sketch, "E3197", {"start": v(2.49, -29.7) * mm, "end": v(2.74, -29.62) * mm});
            skLineSegment(sketch, "E3198", {"start": v(4.55, -27.7) * mm, "end": v(4.87, -27.73) * mm});
            skLineSegment(sketch, "E3199", {"start": v(4.87, -27.73) * mm, "end": v(5.2, -27.71) * mm});
            skLineSegment(sketch, "E3200", {"start": v(5.2, -27.71) * mm, "end": v(5.61, -27.62) * mm});
            skLineSegment(sketch, "E3201", {"start": v(5.61, -27.62) * mm, "end": v(5.85, -27.5) * mm});
            skLineSegment(sketch, "E3202", {"start": v(5.85, -27.5) * mm, "end": v(5.9, -27.45) * mm});
            skLineSegment(sketch, "E3203", {"start": v(5.9, -27.45) * mm, "end": v(5.91, -27.39) * mm});
            skLineSegment(sketch, "E3204", {"start": v(5.91, -27.39) * mm, "end": v(5.86, -27.28) * mm});
            skLineSegment(sketch, "E3205", {"start": v(5.86, -27.28) * mm, "end": v(5.7, -27.18) * mm});
            skLineSegment(sketch, "E3206", {"start": v(5.7, -27.18) * mm, "end": v(5.35, -27.06) * mm});
            skLineSegment(sketch, "E3207", {"start": v(5.35, -27.06) * mm, "end": v(4.9, -26.96) * mm});
            skLineSegment(sketch, "E3208", {"start": v(4.9, -26.96) * mm, "end": v(4.42, -26.9) * mm});
            skLineSegment(sketch, "E3209", {"start": v(4.42, -26.9) * mm, "end": v(4.04, -26.9) * mm});
            skLineSegment(sketch, "E3210", {"start": v(4.04, -26.9) * mm, "end": v(3.93, -26.94) * mm});
            skLineSegment(sketch, "E3211", {"start": v(3.93, -26.94) * mm, "end": v(3.75, -27.05) * mm});
            skLineSegment(sketch, "E3212", {"start": v(3.75, -27.05) * mm, "end": v(3.7, -27.17) * mm});
            skLineSegment(sketch, "E3213", {"start": v(3.7, -27.17) * mm, "end": v(3.76, -27.33) * mm});
            skLineSegment(sketch, "E3214", {"start": v(3.76, -27.33) * mm, "end": v(3.93, -27.5) * mm});
            skLineSegment(sketch, "E3215", {"start": v(3.93, -27.5) * mm, "end": v(4.12, -27.6) * mm});
            skLineSegment(sketch, "E3216", {"start": v(4.12, -27.6) * mm, "end": v(4.35, -27.67) * mm});
            skLineSegment(sketch, "E3217", {"start": v(4.35, -27.67) * mm, "end": v(4.55, -27.7) * mm});
            skLineSegment(sketch, "E3218", {"start": v(3.47, -26.06) * mm, "end": v(3.66, -26.07) * mm});
            skLineSegment(sketch, "E3219", {"start": v(3.66, -26.07) * mm, "end": v(3.77, -26.05) * mm});
            skLineSegment(sketch, "E3220", {"start": v(3.77, -26.05) * mm, "end": v(3.89, -25.99) * mm});
            skLineSegment(sketch, "E3221", {"start": v(3.89, -25.99) * mm, "end": v(3.91, -25.9) * mm});
            skLineSegment(sketch, "E3222", {"start": v(3.91, -25.9) * mm, "end": v(3.88, -25.81) * mm});
            skLineSegment(sketch, "E3223", {"start": v(3.88, -25.81) * mm, "end": v(3.77, -25.74) * mm});
            skLineSegment(sketch, "E3224", {"start": v(3.77, -25.74) * mm, "end": v(3.6, -25.7) * mm});
            skLineSegment(sketch, "E3225", {"start": v(3.6, -25.7) * mm, "end": v(3.44, -25.7) * mm});
            skLineSegment(sketch, "E3226", {"start": v(3.44, -25.7) * mm, "end": v(3.33, -25.74) * mm});
            skLineSegment(sketch, "E3227", {"start": v(3.33, -25.74) * mm, "end": v(3.25, -25.79) * mm});
            skLineSegment(sketch, "E3228", {"start": v(3.25, -25.79) * mm, "end": v(3.22, -25.85) * mm});
            skLineSegment(sketch, "E3229", {"start": v(3.22, -25.85) * mm, "end": v(3.23, -25.92) * mm});
            skLineSegment(sketch, "E3230", {"start": v(3.23, -25.92) * mm, "end": v(3.27, -25.97) * mm});
            skLineSegment(sketch, "E3231", {"start": v(3.27, -25.97) * mm, "end": v(3.33, -26.01) * mm});
            skLineSegment(sketch, "E3232", {"start": v(3.33, -26.01) * mm, "end": v(3.42, -26.05) * mm});
            skLineSegment(sketch, "E3233", {"start": v(3.42, -26.05) * mm, "end": v(3.47, -26.06) * mm});
            skLineSegment(sketch, "E3234", {"start": v(5.89, -25.89) * mm, "end": v(6.17, -25.97) * mm});
            skLineSegment(sketch, "E3235", {"start": v(6.17, -25.97) * mm, "end": v(6.58, -26.03) * mm});
            skLineSegment(sketch, "E3236", {"start": v(6.58, -26.03) * mm, "end": v(6.89, -26.03) * mm});
            skLineSegment(sketch, "E3237", {"start": v(6.89, -26.03) * mm, "end": v(7.07, -25.97) * mm});
            skLineSegment(sketch, "E3238", {"start": v(7.07, -25.97) * mm, "end": v(7.15, -25.89) * mm});
            skLineSegment(sketch, "E3239", {"start": v(7.15, -25.89) * mm, "end": v(7.14, -25.8) * mm});
            skLineSegment(sketch, "E3240", {"start": v(7.14, -25.8) * mm, "end": v(7.05, -25.72) * mm});
            skLineSegment(sketch, "E3241", {"start": v(7.05, -25.72) * mm, "end": v(6.81, -25.6) * mm});
            skLineSegment(sketch, "E3242", {"start": v(6.81, -25.6) * mm, "end": v(6.45, -25.49) * mm});
            skLineSegment(sketch, "E3243", {"start": v(6.45, -25.49) * mm, "end": v(6.13, -25.42) * mm});
            skLineSegment(sketch, "E3244", {"start": v(6.13, -25.42) * mm, "end": v(5.9, -25.4) * mm});
            skLineSegment(sketch, "E3245", {"start": v(5.9, -25.4) * mm, "end": v(5.8, -25.4) * mm});
            skLineSegment(sketch, "E3246", {"start": v(5.8, -25.4) * mm, "end": v(5.68, -25.44) * mm});
            skLineSegment(sketch, "E3247", {"start": v(5.68, -25.44) * mm, "end": v(5.6, -25.48) * mm});
            skLineSegment(sketch, "E3248", {"start": v(5.6, -25.48) * mm, "end": v(5.5, -25.55) * mm});
            skLineSegment(sketch, "E3249", {"start": v(5.5, -25.55) * mm, "end": v(5.5, -25.64) * mm});
            skLineSegment(sketch, "E3250", {"start": v(5.5, -25.64) * mm, "end": v(5.57, -25.72) * mm});
            skLineSegment(sketch, "E3251", {"start": v(5.57, -25.72) * mm, "end": v(5.7, -25.8) * mm});
            skLineSegment(sketch, "E3252", {"start": v(5.7, -25.8) * mm, "end": v(5.89, -25.89) * mm});
            skLineSegment(sketch, "E3253", {"start": v(8.43, -23.01) * mm, "end": v(8.53, -23.04) * mm});
            skLineSegment(sketch, "E3254", {"start": v(8.53, -23.04) * mm, "end": v(8.64, -23.04) * mm});
            skLineSegment(sketch, "E3255", {"start": v(8.64, -23.04) * mm, "end": v(8.76, -22.95) * mm});
            skLineSegment(sketch, "E3256", {"start": v(8.76, -22.95) * mm, "end": v(8.74, -22.85) * mm});
            skLineSegment(sketch, "E3257", {"start": v(8.74, -22.85) * mm, "end": v(8.62, -22.78) * mm});
            skLineSegment(sketch, "E3258", {"start": v(8.62, -22.78) * mm, "end": v(8.46, -22.77) * mm});
            skLineSegment(sketch, "E3259", {"start": v(8.46, -22.77) * mm, "end": v(8.35, -22.86) * mm});
            skLineSegment(sketch, "E3260", {"start": v(8.35, -22.86) * mm, "end": v(8.35, -22.92) * mm});
            skLineSegment(sketch, "E3261", {"start": v(8.35, -22.92) * mm, "end": v(8.38, -22.97) * mm});
            skLineSegment(sketch, "E3262", {"start": v(8.38, -22.97) * mm, "end": v(8.43, -23.01) * mm});
            skLineSegment(sketch, "E3263", {"start": v(10.56, -22.9) * mm, "end": v(10.81, -22.82) * mm});
            skLineSegment(sketch, "E3264", {"start": v(10.81, -22.82) * mm, "end": v(10.99, -22.63) * mm});
            skLineSegment(sketch, "E3265", {"start": v(10.99, -22.63) * mm, "end": v(10.99, -22.5) * mm});
            skLineSegment(sketch, "E3266", {"start": v(10.99, -22.5) * mm, "end": v(10.91, -22.42) * mm});
            skLineSegment(sketch, "E3267", {"start": v(10.91, -22.42) * mm, "end": v(10.72, -22.35) * mm});
            skLineSegment(sketch, "E3268", {"start": v(10.72, -22.35) * mm, "end": v(10.52, -22.36) * mm});
            skLineSegment(sketch, "E3269", {"start": v(10.52, -22.36) * mm, "end": v(10.35, -22.41) * mm});
            skLineSegment(sketch, "E3270", {"start": v(10.35, -22.41) * mm, "end": v(10.15, -22.6) * mm});
            skLineSegment(sketch, "E3271", {"start": v(10.15, -22.6) * mm, "end": v(10.13, -22.7) * mm});
            skLineSegment(sketch, "E3272", {"start": v(10.13, -22.7) * mm, "end": v(10.19, -22.8) * mm});
            skLineSegment(sketch, "E3273", {"start": v(10.19, -22.8) * mm, "end": v(10.34, -22.89) * mm});
            skLineSegment(sketch, "E3274", {"start": v(10.34, -22.89) * mm, "end": v(10.56, -22.9) * mm});
            skLineSegment(sketch, "E3275", {"start": v(11.42, -20.45) * mm, "end": v(11.52, -20.43) * mm});
            skLineSegment(sketch, "E3276", {"start": v(11.52, -20.43) * mm, "end": v(11.57, -20.36) * mm});
            skLineSegment(sketch, "E3277", {"start": v(11.57, -20.36) * mm, "end": v(11.55, -20.33) * mm});
            skLineSegment(sketch, "E3278", {"start": v(11.55, -20.33) * mm, "end": v(11.46, -20.33) * mm});
            skLineSegment(sketch, "E3279", {"start": v(11.46, -20.33) * mm, "end": v(11.38, -20.4) * mm});
            skLineSegment(sketch, "E3280", {"start": v(11.38, -20.4) * mm, "end": v(11.37, -20.43) * mm});
            skLineSegment(sketch, "E3281", {"start": v(11.37, -20.43) * mm, "end": v(11.42, -20.45) * mm});
            skSolve(sketch);
        }
        {
            var Q0;
            Q0 = qSketchRegion(id + "F0", true);
            extrude(context, id + "F1", {"entities" : qUnion([Q0]), "depth" : 2.54 * mm});
        }
        {
            var Q0;
            Q0=qCreatedBy(makeId("Top.planeOp"),FACE);
            var sketch = newSketch(context, id + "F2", { "sketchPlane" : qUnion([Q0])});
            skLineSegment(sketch, "E3282.bottom", {"start": v(-41.28, 50.37) * mm, "end": v(41.27, 50.37) * mm});
            skLineSegment(sketch, "E3282.top", {"start": v(-41.28, -63.93) * mm, "end": v(41.28, -63.93) * mm});
            skLineSegment(sketch, "E3282.left", {"start": v(-41.28, 50.37) * mm, "end": v(-41.28, -63.93) * mm});
            skLineSegment(sketch, "E3282.right", {"start": v(41.27, 50.37) * mm, "end": v(41.28, -63.93) * mm});
            skArc(sketch, "E3283", {"start": v(2.38, 41.64) * mm, "mid": v(4.76, 44.02) * mm, "end": v(2.38, 46.4) * mm});
            skLineSegment(sketch, "E3284", {"start": v(0, 50.37) * mm, "end": v(0, 39.17) * mm, "construction": true});
            skPoint(sketch, "E3284.endSnap0", {"position": v(0, 50.37) * mm});
            skArc(sketch, "E3285.MirrorC", {"start": v(-2.38, 41.64) * mm, "mid": v(-4.76, 44.02) * mm, "end": v(-2.38, 46.4) * mm});
            skLineSegment(sketch, "E3286", {"start": v(-2.38, 44.02) * mm, "end": v(2.38, 44.02) * mm, "construction": true});
            skLineSegment(sketch, "E3287", {"start": v(-2.38, 44.02) * mm, "end": v(-2.38, 46.86) * mm, "construction": true});
            skLineSegment(sketch, "E3288", {"start": v(2.38, 44.02) * mm, "end": v(2.38, 46.94) * mm, "construction": true});
            skLineSegment(sketch, "E3289", {"start": v(-2.38, 46.4) * mm, "end": v(2.38, 46.4) * mm});
            skLineSegment(sketch, "E3290.MirrorCS", {"start": v(-2.38, 41.64) * mm, "end": v(2.38, 41.64) * mm});
            skSolve(sketch);
        }
        {
            var Q0;
            Q0 = qSketchRegion(id + "F2", true);
            extrude(context, id + "F3", {"entities" : qUnion([Q0]), "operationType" : NewBodyOperationType.ADD, "oppositeDirection" : true, "depth" : 2.54 * mm});
        }
        {
            var Q0;
            Q0=makeQuery(id+"F3.opExtrude","SWEPT_EDGE",EDGE,{"disambiguationData":[OSD([sQuery(id+"F2.wireOp",EDGE,"E3282.bottom"),sQuery(id+"F2.wireOp",EDGE,"E3282.right")])]});
            var Q1;
            Q1=makeQuery(id+"F3.opExtrude","SWEPT_EDGE",EDGE,{"disambiguationData":[OSD([sQuery(id+"F2.wireOp",EDGE,"E3282.bottom"),sQuery(id+"F2.wireOp",EDGE,"E3282.left")])]});
            var Q2;
            Q2=makeQuery(id+"F3.opExtrude","SWEPT_EDGE",EDGE,{"disambiguationData":[OSD([sQuery(id+"F2.wireOp",EDGE,"E3282.top"),sQuery(id+"F2.wireOp",EDGE,"E3282.left")])]});
            var Q3;
            Q3=makeQuery(id+"F3.opExtrude","SWEPT_EDGE",EDGE,{"disambiguationData":[OSD([sQuery(id+"F2.wireOp",EDGE,"E3282.top"),sQuery(id+"F2.wireOp",EDGE,"E3282.right")])]});
            fillet(context, id + "F4", {"entities" : qUnion([Q0, Q1, Q2, Q3]), "radius" : 5.08 * mm, "tangentPropagation" : true, "allowEdgeOverflow" : false});
        }
        {
            var Q0;
            {var subQ0=sQuery(id+"F2.wireOp",EDGE,"E3282.left");var subQ1=sQuery(id+"F2.wireOp",EDGE,"E3282.bottom");var subQ2=sQuery(id+"F2.wireOp",EDGE,"E3282.top");var subQ3=sQuery(id+"F2.wireOp",EDGE,"E3282.right");Q0=makeQuery(id+"F3.boolean.opBoolean","SPLIT",FACE,{"disambiguationData":[TD([makeQuery(id+"F1.opExtrude","SWEPT_FACE",FACE,{"disambiguationData":[OSD([sQuery(id+"F0.wireOp",EDGE,"E42")])]})])],"derivedFrom":makeQuery(id+"F3.opExtrude","CAP_FACE",FACE,{"disambiguationData":[OSD([subQ1,subQ2,subQ0,subQ3])],"isStart":true})});}
            var sketch = newSketch(context, id + "F5", { "sketchPlane" : qUnion([Q0])});
            skLineSegment(sketch, "E3291", {"start": v(-6.12, -42.37) * mm, "end": v(-6.12, -57.14) * mm});
            skLineSegment(sketch, "E3292", {"start": v(-6.12, -57.14) * mm, "end": v(-4.22, -57.14) * mm});
            skLineSegment(sketch, "E3293", {"start": v(-4.22, -57.14) * mm, "end": v(-4.22, -61.42) * mm});
            skLineSegment(sketch, "E3294", {"start": v(-4.22, -61.42) * mm, "end": v(-13.74, -61.42) * mm});
            skLineSegment(sketch, "E3295", {"start": v(-13.74, -61.42) * mm, "end": v(-13.74, -57.14) * mm});
            skLineSegment(sketch, "E3296", {"start": v(-13.74, -57.14) * mm, "end": v(-11.35, -57.14) * mm});
            skLineSegment(sketch, "E3297", {"start": v(-11.35, -57.14) * mm, "end": v(-11.35, -48.93) * mm});
            skLineSegment(sketch, "E3298", {"start": v(-11.35, -48.93) * mm, "end": v(-13.74, -48.93) * mm});
            skLineSegment(sketch, "E3299", {"start": v(-13.74, -48.93) * mm, "end": v(-13.74, -45.9) * mm});
            skLineSegment(sketch, "E3300", {"start": v(-13.74, -45.9) * mm, "end": v(-10.2, -42.37) * mm});
            skLineSegment(sketch, "E3301", {"start": v(-10.2, -42.37) * mm, "end": v(-6.12, -42.37) * mm});
            skLineSegment(sketch, "E3302", {"start": v(-6.56, -42.83) * mm, "end": v(-6.56, -57.6) * mm});
            skLineSegment(sketch, "E3303", {"start": v(-6.56, -57.6) * mm, "end": v(-4.65, -57.6) * mm});
            skLineSegment(sketch, "E3304", {"start": v(-4.65, -57.6) * mm, "end": v(-4.65, -60.95) * mm});
            skLineSegment(sketch, "E3305", {"start": v(-4.65, -60.95) * mm, "end": v(-13.28, -60.95) * mm});
            skLineSegment(sketch, "E3306", {"start": v(-13.28, -60.95) * mm, "end": v(-13.28, -57.6) * mm});
            skLineSegment(sketch, "E3307", {"start": v(-13.28, -57.6) * mm, "end": v(-10.88, -57.6) * mm});
            skLineSegment(sketch, "E3308", {"start": v(-10.88, -57.6) * mm, "end": v(-10.88, -48.46) * mm});
            skLineSegment(sketch, "E3309", {"start": v(-10.88, -48.46) * mm, "end": v(-13.28, -48.46) * mm});
            skLineSegment(sketch, "E3310", {"start": v(-13.28, -48.46) * mm, "end": v(-13.28, -46.1) * mm});
            skLineSegment(sketch, "E3311", {"start": v(-13.28, -46.1) * mm, "end": v(-10.01, -42.83) * mm});
            skLineSegment(sketch, "E3312", {"start": v(-10.01, -42.83) * mm, "end": v(-6.56, -42.83) * mm});
            skLineSegment(sketch, "E3313", {"start": v(-7.15, -43.42) * mm, "end": v(-7.15, -58.2) * mm});
            skLineSegment(sketch, "E3314", {"start": v(-7.15, -58.2) * mm, "end": v(-5.25, -58.2) * mm});
            skLineSegment(sketch, "E3315", {"start": v(-5.25, -58.2) * mm, "end": v(-5.25, -60.36) * mm});
            skLineSegment(sketch, "E3316", {"start": v(-5.25, -60.36) * mm, "end": v(-12.68, -60.36) * mm});
            skLineSegment(sketch, "E3317", {"start": v(-12.68, -60.36) * mm, "end": v(-12.68, -58.2) * mm});
            skLineSegment(sketch, "E3318", {"start": v(-12.68, -58.2) * mm, "end": v(-10.29, -58.2) * mm});
            skLineSegment(sketch, "E3319", {"start": v(-10.29, -58.2) * mm, "end": v(-10.29, -47.87) * mm});
            skLineSegment(sketch, "E3320", {"start": v(-10.29, -47.87) * mm, "end": v(-12.68, -47.87) * mm});
            skLineSegment(sketch, "E3321", {"start": v(-12.68, -47.87) * mm, "end": v(-12.68, -46.34) * mm});
            skLineSegment(sketch, "E3322", {"start": v(-12.68, -46.34) * mm, "end": v(-9.77, -43.42) * mm});
            skLineSegment(sketch, "E3323", {"start": v(-9.77, -43.42) * mm, "end": v(-7.15, -43.42) * mm});
            skLineSegment(sketch, "E3324", {"start": v(2.42, -42.24) * mm, "end": v(10.79, -42.24) * mm});
            skLineSegment(sketch, "E3325", {"start": v(10.79, -42.24) * mm, "end": v(13.85, -45.3) * mm});
            skLineSegment(sketch, "E3326", {"start": v(13.85, -45.3) * mm, "end": v(13.85, -58.26) * mm});
            skLineSegment(sketch, "E3327", {"start": v(13.85, -58.26) * mm, "end": v(10.7, -61.42) * mm});
            skLineSegment(sketch, "E3328", {"start": v(10.7, -61.42) * mm, "end": v(2.37, -61.42) * mm});
            skLineSegment(sketch, "E3329", {"start": v(2.37, -61.42) * mm, "end": v(-0.69, -58.31) * mm});
            skLineSegment(sketch, "E3330", {"start": v(-0.69, -58.31) * mm, "end": v(-0.69, -55.19) * mm});
            skLineSegment(sketch, "E3331", {"start": v(-0.69, -55.19) * mm, "end": v(4.54, -55.19) * mm});
            skLineSegment(sketch, "E3332", {"start": v(4.54, -55.19) * mm, "end": v(4.54, -56.43) * mm});
            skLineSegment(sketch, "E3333", {"start": v(4.54, -56.43) * mm, "end": v(5.15, -57.06) * mm});
            skLineSegment(sketch, "E3334", {"start": v(5.15, -57.06) * mm, "end": v(7.98, -57.06) * mm});
            skLineSegment(sketch, "E3335", {"start": v(7.98, -57.06) * mm, "end": v(8.54, -56.48) * mm});
            skLineSegment(sketch, "E3336", {"start": v(8.54, -56.48) * mm, "end": v(8.54, -53.73) * mm});
            skLineSegment(sketch, "E3337", {"start": v(8.54, -53.73) * mm, "end": v(2.38, -53.73) * mm});
            skLineSegment(sketch, "E3338", {"start": v(2.38, -53.73) * mm, "end": v(-0.68, -50.68) * mm});
            skLineSegment(sketch, "E3339", {"start": v(-0.68, -50.68) * mm, "end": v(-0.68, -45.34) * mm});
            skLineSegment(sketch, "E3340", {"start": v(-0.68, -45.34) * mm, "end": v(2.42, -42.24) * mm});
            skLineSegment(sketch, "E3341", {"start": v(2.64, -42.77) * mm, "end": v(10.57, -42.77) * mm});
            skLineSegment(sketch, "E3342", {"start": v(10.57, -42.77) * mm, "end": v(13.32, -45.52) * mm});
            skLineSegment(sketch, "E3343", {"start": v(13.32, -45.52) * mm, "end": v(13.32, -58.04) * mm});
            skLineSegment(sketch, "E3344", {"start": v(13.32, -58.04) * mm, "end": v(10.47, -60.89) * mm});
            skLineSegment(sketch, "E3345", {"start": v(10.47, -60.89) * mm, "end": v(2.6, -60.89) * mm});
            skLineSegment(sketch, "E3346", {"start": v(2.6, -60.89) * mm, "end": v(-0.16, -58.1) * mm});
            skLineSegment(sketch, "E3347", {"start": v(-0.16, -58.1) * mm, "end": v(-0.16, -55.72) * mm});
            skLineSegment(sketch, "E3348", {"start": v(-0.16, -55.72) * mm, "end": v(4.01, -55.72) * mm});
            skLineSegment(sketch, "E3349", {"start": v(4.01, -55.72) * mm, "end": v(4.01, -56.64) * mm});
            skLineSegment(sketch, "E3350", {"start": v(4.01, -56.64) * mm, "end": v(4.92, -57.59) * mm});
            skLineSegment(sketch, "E3351", {"start": v(4.92, -57.59) * mm, "end": v(8.2, -57.59) * mm});
            skLineSegment(sketch, "E3352", {"start": v(8.2, -57.59) * mm, "end": v(9.07, -56.7) * mm});
            skLineSegment(sketch, "E3353", {"start": v(9.07, -56.7) * mm, "end": v(9.07, -53.2) * mm});
            skLineSegment(sketch, "E3354", {"start": v(9.07, -53.2) * mm, "end": v(2.6, -53.2) * mm});
            skLineSegment(sketch, "E3355", {"start": v(2.6, -53.2) * mm, "end": v(-0.15, -50.46) * mm});
            skLineSegment(sketch, "E3356", {"start": v(-0.15, -50.46) * mm, "end": v(-0.15, -45.56) * mm});
            skLineSegment(sketch, "E3357", {"start": v(-0.15, -45.56) * mm, "end": v(2.64, -42.77) * mm});
            skLineSegment(sketch, "E3358", {"start": v(2.86, -43.3) * mm, "end": v(10.35, -43.3) * mm});
            skLineSegment(sketch, "E3359", {"start": v(10.35, -43.3) * mm, "end": v(12.79, -45.74) * mm});
            skLineSegment(sketch, "E3360", {"start": v(12.79, -45.74) * mm, "end": v(12.79, -57.82) * mm});
            skLineSegment(sketch, "E3361", {"start": v(12.79, -57.82) * mm, "end": v(10.25, -60.36) * mm});
            skLineSegment(sketch, "E3362", {"start": v(10.25, -60.36) * mm, "end": v(2.82, -60.36) * mm});
            skLineSegment(sketch, "E3363", {"start": v(2.82, -60.36) * mm, "end": v(0.37, -57.88) * mm});
            skLineSegment(sketch, "E3364", {"start": v(0.37, -57.88) * mm, "end": v(0.37, -56.25) * mm});
            skLineSegment(sketch, "E3365", {"start": v(0.37, -56.25) * mm, "end": v(3.48, -56.25) * mm});
            skLineSegment(sketch, "E3366", {"start": v(3.48, -56.25) * mm, "end": v(3.48, -56.86) * mm});
            skLineSegment(sketch, "E3367", {"start": v(3.48, -56.86) * mm, "end": v(4.7, -58.12) * mm});
            skLineSegment(sketch, "E3368", {"start": v(4.7, -58.12) * mm, "end": v(8.42, -58.12) * mm});
            skLineSegment(sketch, "E3369", {"start": v(8.42, -58.12) * mm, "end": v(9.6, -56.91) * mm});
            skLineSegment(sketch, "E3370", {"start": v(9.6, -56.91) * mm, "end": v(9.6, -52.68) * mm});
            skLineSegment(sketch, "E3371", {"start": v(9.6, -52.68) * mm, "end": v(2.82, -52.68) * mm});
            skLineSegment(sketch, "E3372", {"start": v(2.82, -52.68) * mm, "end": v(0.38, -50.24) * mm});
            skLineSegment(sketch, "E3373", {"start": v(0.38, -50.24) * mm, "end": v(0.38, -45.78) * mm});
            skLineSegment(sketch, "E3374", {"start": v(0.38, -45.78) * mm, "end": v(2.86, -43.3) * mm});
            skLineSegment(sketch, "E3375", {"start": v(4.69, -45.56) * mm, "end": v(8.41, -45.56) * mm});
            skLineSegment(sketch, "E3376", {"start": v(8.41, -45.56) * mm, "end": v(9.61, -46.7) * mm});
            skLineSegment(sketch, "E3377", {"start": v(9.61, -46.7) * mm, "end": v(9.61, -49.3) * mm});
            skLineSegment(sketch, "E3378", {"start": v(9.61, -49.3) * mm, "end": v(8.41, -50.49) * mm});
            skLineSegment(sketch, "E3379", {"start": v(8.41, -50.49) * mm, "end": v(4.69, -50.49) * mm});
            skLineSegment(sketch, "E3380", {"start": v(4.69, -50.49) * mm, "end": v(3.52, -49.32) * mm});
            skLineSegment(sketch, "E3381", {"start": v(3.52, -49.32) * mm, "end": v(3.52, -46.7) * mm});
            skLineSegment(sketch, "E3382", {"start": v(3.52, -46.7) * mm, "end": v(4.69, -45.56) * mm});
            skLineSegment(sketch, "E3383", {"start": v(4.92, -46.13) * mm, "end": v(8.19, -46.13) * mm});
            skLineSegment(sketch, "E3384", {"start": v(8.19, -46.13) * mm, "end": v(9.05, -46.95) * mm});
            skLineSegment(sketch, "E3385", {"start": v(9.05, -46.95) * mm, "end": v(9.05, -49.06) * mm});
            skLineSegment(sketch, "E3386", {"start": v(9.05, -49.06) * mm, "end": v(8.18, -49.93) * mm});
            skLineSegment(sketch, "E3387", {"start": v(8.18, -49.93) * mm, "end": v(4.92, -49.93) * mm});
            skLineSegment(sketch, "E3388", {"start": v(4.92, -49.93) * mm, "end": v(4.08, -49.09) * mm});
            skLineSegment(sketch, "E3389", {"start": v(4.08, -49.09) * mm, "end": v(4.08, -46.94) * mm});
            skLineSegment(sketch, "E3390", {"start": v(4.08, -46.94) * mm, "end": v(4.92, -46.13) * mm});
            skLineSegment(sketch, "E3391", {"start": v(5.14, -46.69) * mm, "end": v(7.96, -46.69) * mm});
            skLineSegment(sketch, "E3392", {"start": v(7.96, -46.69) * mm, "end": v(8.49, -47.19) * mm});
            skLineSegment(sketch, "E3393", {"start": v(8.49, -47.19) * mm, "end": v(8.49, -48.83) * mm});
            skLineSegment(sketch, "E3394", {"start": v(8.49, -48.83) * mm, "end": v(7.95, -49.37) * mm});
            skLineSegment(sketch, "E3395", {"start": v(7.95, -49.37) * mm, "end": v(5.15, -49.37) * mm});
            skLineSegment(sketch, "E3396", {"start": v(5.15, -49.37) * mm, "end": v(4.64, -48.85) * mm});
            skLineSegment(sketch, "E3397", {"start": v(4.64, -48.85) * mm, "end": v(4.64, -47.18) * mm});
            skLineSegment(sketch, "E3398", {"start": v(4.64, -47.18) * mm, "end": v(5.14, -46.69) * mm});
            skPoint(sketch, "E3399.firstSnap0", {"position": v(0, -63.93) * mm});
            skSolve(sketch);
        }
        {
            var Q0;
            Q0 = qSketchRegion(id + "F5", true);
            var Q1;
            Q1=makeQuery(id+"F5.imprint","IMPRINT",FACE,{"disambiguationData":[TD([[makeQuery(id+"F5.imprint","IMPRINT",EDGE,{"derivedFrom":sQuery(id+"F5.wireOp",EDGE,"E3313")}),-1.0]])]});
            var Q2;
            Q2=makeQuery(id+"F5.imprint","IMPRINT",FACE,{"disambiguationData":[TD([[makeQuery(id+"F5.imprint","IMPRINT",EDGE,{"derivedFrom":sQuery(id+"F5.wireOp",EDGE,"E3358")}),-1.0]])]});
            var Q3;
            Q3=makeQuery(id+"F5.imprint","IMPRINT",FACE,{"disambiguationData":[TD([[makeQuery(id+"F5.imprint","IMPRINT",EDGE,{"derivedFrom":sQuery(id+"F5.wireOp",EDGE,"E3383")}),-1.0]])]});
            extrude(context, id + "F6", {"entities" : qUnion([Q0, Q1, Q2, Q3]), "operationType" : NewBodyOperationType.ADD, "depth" : 2.54 * mm});
        }
    });
